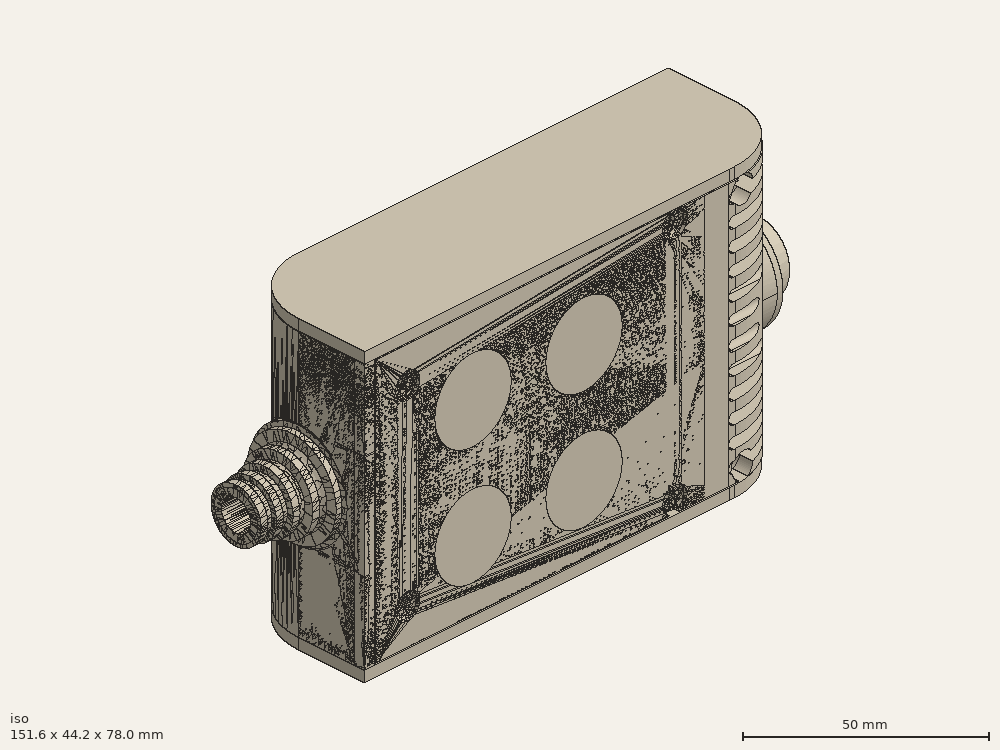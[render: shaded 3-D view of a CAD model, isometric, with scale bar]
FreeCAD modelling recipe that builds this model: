
FCSTD DOCUMENT  (FreeCAD 0.19R0.19.2)
Label: enclosure_180FCStd
License: All rights reserved
LicenseURL: http://en.wikipedia.org/wiki/All_rights_reserved
objects: Part::Revolution×152, Part::MultiFuse×146, Part::Feature×146, Sketcher::SketchObject×84, Part::Cut×70, Part::Cylinder×70, Part::Extrusion×67, Part::Fillet×58, Part::Box×36, App::MeasureDistance×4, PartDesign::Body×2, Image::ImagePlane×1
note: 831 computed .brp shape members not serialized (recipe doc carries the construction recipe); baked Part::Feature solids carry a one-line shape summary decoded from their .brp

FEATURE [Sketcher::SketchObject] Sketch  label="topSketch"
  FullyConstrained = true
  sketch-geometry (20):
    g0: LineSegment StartX=5.21097e-06 StartY=3 StartZ=0 EndX=5.21097e-06 EndY=19 EndZ=0
    g1: ArcOfCircle CenterX=19 CenterY=19 CenterZ=0 NormalX=0 NormalY=0 NormalZ=1 AngleXU=0 Radius=19 StartAngle=1.5708 EndAngle=3.14159
    g2: ArcOfCircle CenterX=19 CenterY=19 CenterZ=0 NormalX=0 NormalY=0 NormalZ=1 AngleXU=0 Radius=16 StartAngle=1.5708 EndAngle=3.14159
    g3: LineSegment StartX=114 StartY=35 StartZ=0 EndX=19 EndY=35 EndZ=0
    g4: LineSegment StartX=5.21097e-06 StartY=3 StartZ=0 EndX=5.21097e-06 EndY=0 EndZ=0
    g5: LineSegment StartX=3 StartY=0 StartZ=0 EndX=5.21097e-06 EndY=0 EndZ=0
    g6: LineSegment StartX=3 StartY=19 StartZ=0 EndX=3 EndY=0 EndZ=0
    g7: LineSegment StartX=19 StartY=38 StartZ=0 EndX=124 EndY=38 EndZ=0
    g8: Circle CenterX=119 CenterY=35 CenterZ=0 NormalX=0 NormalY=0 NormalZ=1 AngleXU=0 Radius=1
    g9: Circle CenterX=121 CenterY=35 CenterZ=0 NormalX=0 NormalY=0 NormalZ=1 AngleXU=0 Radius=1
    g10: Circle CenterX=121 CenterY=33 CenterZ=0 NormalX=0 NormalY=0 NormalZ=1 AngleXU=0 Radius=1
    g11: BSplineCurve PolesCount=3 KnotsCount=2 Degree=2 IsPeriodic=0
    g12: GeomPoint X=119 Y=35 Z=0
    g13: GeomPoint X=121 Y=33 Z=0
    g14: LineSegment StartX=119 StartY=35 StartZ=0 EndX=114 EndY=35 EndZ=0
    g15: ArcOfCircle CenterX=105 CenterY=19 CenterZ=0 NormalX=0 NormalY=0 NormalZ=1 AngleXU=0 Radius=19 StartAngle=5.7297 EndAngle=6.28319
    g16: ArcOfCircle CenterX=105 CenterY=19 CenterZ=0 NormalX=0 NormalY=0 NormalZ=1 AngleXU=0 Radius=16 StartAngle=5.60905 EndAngle=6.28319
    g17: LineSegment StartX=121 StartY=33 StartZ=0 EndX=121 EndY=19 EndZ=0
    g18: LineSegment StartX=124 StartY=38 StartZ=0 EndX=124 EndY=19 EndZ=0
    g19: LineSegment StartX=117.5 StartY=9.01251 StartZ=0 EndX=121.163 EndY=9.0125 EndZ=0
  constraints (46):
    c: Vertical(g0)
    c: Block(g0)
    c: Coincident(g1,g0)
    c: Block(g1)
    c: Coincident(g2,g1)
    c: Block(g2)
    c: Coincident(g3,g2)
    c: Horizontal(g3)
    c: Tangent(g3,g2)
    c: Coincident(g4,g0)
    c: Distance(g4) = 3
    c: Vertical(g4)
    c: Coincident(g5,g4)
    c: Horizontal(g5)
    c: Coincident(g6,g2)
    c: Coincident(g6,g5)
    c: Vertical(g6)
    c: Horizontal(g7)
    c: Distance(g7) = 105
    c: Coincident(g7,g1)
    c: Block(g3)
    c: Weight(g8) = 1
    c: Equal(g8,g9)
    c: Equal(g8,g10)
    c: InternalAlignment(g8,g11)
    c: InternalAlignment(g9,g11)
    c: InternalAlignment(g10,g11)
    c: InternalAlignment(g12,g11)
    c: InternalAlignment(g13,g11)
    c: Block(g11)
    c: Coincident(g14,g11)
    c: Coincident(g14,g3)
    c: Horizontal(g14)
    c: Block(g15)
    c: Coincident(g16,g15)
    c: Block(g16)
    c: Coincident(g17,g11)
    c: Coincident(g17,g16)
    c: Vertical(g17)
    c: Distance(g17) = 14
    c: Coincident(g18,g7)
    c: Coincident(g18,g15)
    c: Vertical(g18)
    c: Distance(g18) = 19
    c: Coincident(g19,g16)
    c: Coincident(g19,g15)
FEATURE [Sketcher::SketchObject] Sketch001  label="bottomSketch"
  FullyConstrained = true
  sketch-geometry (32):
    g0: LineSegment StartX=3.3 StartY=-6.03275e-07 StartZ=0 EndX=98 EndY=-6.03275e-07 EndZ=0
    g1: ArcOfCircle CenterX=98 CenterY=19 CenterZ=0 NormalX=0 NormalY=0 NormalZ=1 AngleXU=0 Radius=19 StartAngle=4.71239 EndAngle=5.71103
    g2: LineSegment StartX=6.3 StartY=8 StartZ=0 EndX=3.3 EndY=8 EndZ=0
    g3: LineSegment StartX=3.3 StartY=8 StartZ=0 EndX=3.3 EndY=-6.03275e-07 EndZ=0
    g4: ArcOfCircle CenterX=8.3 CenterY=5 CenterZ=0 NormalX=0 NormalY=0 NormalZ=1 AngleXU=0 Radius=2 StartAngle=3.14159 EndAngle=4.71239
    g5: LineSegment StartX=6.3 StartY=8 StartZ=0 EndX=6.3 EndY=5 EndZ=0
    g6: ArcOfCircle CenterX=98 CenterY=19 CenterZ=0 NormalX=0 NormalY=0 NormalZ=1 AngleXU=0 Radius=12.7 StartAngle=4.71239 EndAngle=6.28319
    g7: LineSegment StartX=94.7 StartY=3 StartZ=0 EndX=8.3 EndY=3 EndZ=0
    g8-g12: Circle x5 (B-spline internal-alignment scaffolding for g13; pole/knot coordinates omitted)
    g13: BSplineCurve PolesCount=5 KnotsCount=3 Degree=3 IsPeriodic=0
    g14: GeomPoint X=98 Y=6.3 Z=0
    g15: GeomPoint X=96.3938 Y=4.71946 Z=0
    g16: GeomPoint X=94.7 Y=3 Z=0
    g17-g23: Circle x7 (B-spline internal-alignment scaffolding for g24; pole/knot coordinates omitted)
    g24: BSplineCurve PolesCount=7 KnotsCount=5 Degree=3 IsPeriodic=0
    g25-g29: GeomPoint x5 (B-spline internal-alignment scaffolding for g24; pole/knot coordinates omitted)
    g30: ArcOfCircle CenterX=98 CenterY=19 CenterZ=0 NormalX=0 NormalY=0 NormalZ=1 AngleXU=0 Radius=15.7 StartAngle=5.81226 EndAngle=6.28319
    g31: LineSegment StartX=110.7 StartY=19 StartZ=0 EndX=113.7 EndY=19 EndZ=0
  constraints (41):
    c: Horizontal(g0)
    c: Coincident(g1,g0)
    c: Block(g1)
    c: Horizontal(g2)
    c: Distance(g2) = 3
    c: Coincident(g3,g2)
    c: Vertical(g3)
    c: Coincident(g3,g0)
    c: Block(g4)
    c: Block(g2)
    c: Coincident(g5,g2)
    c: Coincident(g5,g4)
    c: Vertical(g5)
    c: Coincident(g6,g1)
    c: Block(g6)
    c: Coincident(g7,g4)
    c: Horizontal(g7)
    c: Block(g0)
    c: Block(g7)
    c: Block(g3)
    c: Coincident(g13,g6)
    c: Weight(g8) = 1
    c: Equal(g8, g9-g12) x4
    c: Coincident(g13,g7)
    c: InternalAlignment(g8-g12 -> g13) x5
    c: InternalAlignment(g14,g13)
    c: InternalAlignment(g15,g13)
    c: InternalAlignment(g16,g13)
    c: Block(g13)
    c: Weight(g17) = 1
    c: Equal(g17, g18-g23) x6
    c: Coincident(g24,g1)
    c: InternalAlignment(g17-g23 -> g24) x7
    c: InternalAlignment(g25-g29 -> g24) x5
    c: Block(g24)
    c: Coincident(g30,g24)
    c: Coincident(g31,g6)
    c: Coincident(g31,g30)
    c: Horizontal(g31)
    c: Block(g31)
    c: Block(g30)
FEATURE [Part::Extrusion] Extrude  label="top"
  Base = -> Sketch
  Dir = (0,0,1)
  DirMode = 2
  FaceMakerClass = Part::FaceMakerBullseye
  LengthFwd = 72
  LengthRev = 0
  Solid = true
  Symmetric = false
FEATURE [Part::Extrusion] Extrude001  label="bottom"
  Base = -> Sketch001
  Dir = (0,0,1)
  DirMode = 2
  FaceMakerClass = Part::FaceMakerBullseye
  LengthFwd = 71.4
  LengthRev = 0
  Placement = pos=(0,0,0.3) rot=(0,0,1;0rad)
  Solid = true
  Symmetric = false
FEATURE [Sketcher::SketchObject] Sketch002  label="topSketch001"
  FullyConstrained = true
  sketch-geometry (8):
    g0: ArcOfCircle CenterX=19 CenterY=19.0975 CenterZ=0 NormalX=0 NormalY=0 NormalZ=1 AngleXU=0 Radius=18.9025 StartAngle=1.5708 EndAngle=3.14674
    g1: LineSegment StartX=0.0977805 StartY=19.0003 StartZ=0 EndX=0.0977805 EndY=0.000251602 EndZ=0
    g2: LineSegment StartX=19 StartY=38 StartZ=0 EndX=124 EndY=38 EndZ=0
    g3: LineSegment StartX=0.0977805 StartY=0.000251602 StartZ=0 EndX=105.098 EndY=0.000251602 EndZ=0
    g4: LineSegment StartX=124 StartY=38 StartZ=0 EndX=125.616 EndY=38 EndZ=0
    g5: LineSegment StartX=105.098 StartY=0.000251602 StartZ=0 EndX=106.713 EndY=0.000251602 EndZ=0
    g6: ArcOfCircle CenterX=106.616 CenterY=19 CenterZ=0 NormalX=0 NormalY=0 NormalZ=1 AngleXU=0 Radius=19 StartAngle=4.71754 EndAngle=6.28319
    g7: LineSegment StartX=125.616 StartY=38 StartZ=0 EndX=125.616 EndY=19 EndZ=0
  constraints (21):
    c: Block(g0)
    c: Coincident(g1,g0)
    c: Vertical(g1)
    c: Horizontal(g2)
    c: Distance(g2) = 105
    c: Coincident(g2,g0)
    c: Distance(g1) = 19
    c: Coincident(g3,g1)
    c: Horizontal(g3)
    c: Distance(g3) = 105
    c: Coincident(g4,g2)
    c: Horizontal(g4)
    c: Distance(g4) = 1.61553
    c: Horizontal(g5)
    c: Equal(g4,g5) = 1.61553
    c: Coincident(g5,g3)
    c: Block(g6)
    c: Coincident(g6,g5)
    c: Coincident(g7,g4)
    c: Coincident(g7,g6)
    c: Vertical(g7)
FEATURE [Part::Extrusion] Extrude002  label="sideA"
  Base = -> Sketch002
  Dir = (0,0,1)
  DirMode = 2
  FaceMakerClass = Part::FaceMakerBullseye
  LengthFwd = 3
  LengthRev = 0
  Placement = pos=(0,0,-3) rot=(0,0,1;0rad)
  Solid = true
  Symmetric = false
FEATURE [Sketcher::SketchObject] Sketch003  label="topSketch002"
  FullyConstrained = true
  sketch-geometry (6):
    g0: LineSegment StartX=19 StartY=38 StartZ=0 EndX=117 EndY=38 EndZ=0
    g1: ArcOfCircle CenterX=19 CenterY=19 CenterZ=0 NormalX=0 NormalY=0 NormalZ=1 AngleXU=0 Radius=19 StartAngle=1.5708 EndAngle=3.14159
    g2: LineSegment StartX=117 StartY=38 StartZ=0 EndX=117 EndY=19 EndZ=0
    g3: LineSegment StartX=98 StartY=1.0161e-12 StartZ=0 EndX=5.22862e-06 EndY=1.0161e-12 EndZ=0
    g4: LineSegment StartX=5.22862e-06 StartY=19 StartZ=0 EndX=5.22862e-06 EndY=1.0161e-12 EndZ=0
    g5: ArcOfCircle CenterX=98 CenterY=19 CenterZ=0 NormalX=0 NormalY=0 NormalZ=1 AngleXU=0 Radius=19 StartAngle=4.71239 EndAngle=6.28319
  constraints (16):
    c: Horizontal(g0)
    c: Distance(g0) = 98
    c: Coincident(g1,g0)
    c: Block(g1)
    c: Coincident(g2,g0)
    c: Vertical(g2)
    c: Distance(g2) = 19
    c: Horizontal(g3)
    c: Coincident(g4,g1)
    c: Vertical(g4)
    c: Coincident(g3,g4)
    c: Block(g3)
    c: Coincident(g5,g2)
    c: Coincident(g5,g3)
    c: Block(g0)
    c: Block(g5)
FEATURE [Sketcher::SketchObject] Sketch004
  FullyConstrained = true
  MapMode = 3
  Placement = pos=(0,0,0) rot=(1,0,0;1.5708rad)
  Support = -> [Extrude]
  sketch-geometry (8):
    g0: Circle CenterX=80.351 CenterY=-67.6202 CenterZ=0 NormalX=0 NormalY=0 NormalZ=1 AngleXU=0 Radius=2
    g1: Circle CenterX=80.351 CenterY=-67.6202 CenterZ=0 NormalX=0 NormalY=0 NormalZ=1 AngleXU=0 Radius=3
    g2: Circle CenterX=80.351 CenterY=-4.92017 CenterZ=0 NormalX=0 NormalY=0 NormalZ=1 AngleXU=0 Radius=2
    g3: Circle CenterX=80.351 CenterY=-4.92017 CenterZ=0 NormalX=0 NormalY=0 NormalZ=1 AngleXU=0 Radius=3
    g4: Circle CenterX=23.851 CenterY=-4.92017 CenterZ=0 NormalX=0 NormalY=0 NormalZ=1 AngleXU=0 Radius=2
    g5: Circle CenterX=23.851 CenterY=-4.92017 CenterZ=0 NormalX=0 NormalY=0 NormalZ=1 AngleXU=0 Radius=3
    g6: Circle CenterX=23.851 CenterY=-67.6202 CenterZ=0 NormalX=0 NormalY=0 NormalZ=1 AngleXU=0 Radius=2
    g7: Circle CenterX=23.851 CenterY=-67.6202 CenterZ=0 NormalX=0 NormalY=0 NormalZ=1 AngleXU=0 Radius=3
  constraints (8):
    c: Block(g3)
    c: Block(g2)
    c: Block(g1)
    c: Block(g0)
    c: Block(g6)
    c: Block(g7)
    c: Block(g4)
    c: Block(g5)
FEATURE [Part::Extrusion] Extrude004
  Base = -> Sketch004
  Dir = (0,-1,2e-16)
  DirMode = 2
  FaceMakerClass = Part::FaceMakerBullseye
  LengthFwd = 6
  LengthRev = 0
  Placement = pos=(0,9,0) rot=(0,0,1;0rad)
  Solid = true
  Symmetric = false
FEATURE [Sketcher::SketchObject] Sketch005
  FullyConstrained = true
  MapMode = 3
  Placement = pos=(0,0,0) rot=(1,0,0;1.5708rad)
  Support = -> [Extrude]
  sketch-geometry (8):
    g0: Circle CenterX=80.351 CenterY=-67.6202 CenterZ=0 NormalX=0 NormalY=0 NormalZ=1 AngleXU=0 Radius=3
    g1: Circle CenterX=80.351 CenterY=-4.92017 CenterZ=0 NormalX=0 NormalY=0 NormalZ=1 AngleXU=0 Radius=3
    g2: Circle CenterX=23.851 CenterY=-4.92017 CenterZ=0 NormalX=0 NormalY=0 NormalZ=1 AngleXU=0 Radius=3
    g3: Circle CenterX=23.851 CenterY=-67.6202 CenterZ=0 NormalX=0 NormalY=0 NormalZ=1 AngleXU=0 Radius=3
    g4: Circle CenterX=23.851 CenterY=-67.6202 CenterZ=0 NormalX=0 NormalY=0 NormalZ=1 AngleXU=0 Radius=5
    g5: Circle CenterX=80.351 CenterY=-67.6202 CenterZ=0 NormalX=0 NormalY=0 NormalZ=1 AngleXU=0 Radius=5
    g6: Circle CenterX=23.851 CenterY=-4.92017 CenterZ=0 NormalX=0 NormalY=0 NormalZ=1 AngleXU=0 Radius=5
    g7: Circle CenterX=80.351 CenterY=-4.92017 CenterZ=0 NormalX=0 NormalY=0 NormalZ=1 AngleXU=0 Radius=5
  constraints (8):
    c: Block(g1)
    c: Block(g0)
    c: Block(g3)
    c: Block(g2)
    c: Block(g5)
    c: Block(g4)
    c: Block(g6)
    c: Block(g7)
FEATURE [Part::Extrusion] Extrude005
  Base = -> Sketch005
  Dir = (0,-1,2e-16)
  DirMode = 2
  FaceMakerClass = Part::FaceMakerBullseye
  LengthFwd = 2
  LengthRev = 0
  Solid = true
  Symmetric = false
FEATURE [Sketcher::SketchObject] Sketch006
  FullyConstrained = true
  MapMode = 3
  Placement = pos=(0,0,0) rot=(1,0,0;1.5708rad)
  sketch-geometry (8):
    g0: Circle CenterX=80.351 CenterY=-67.6202 CenterZ=0 NormalX=0 NormalY=0 NormalZ=1 AngleXU=0 Radius=3
    g1: Circle CenterX=80.351 CenterY=-4.92017 CenterZ=0 NormalX=0 NormalY=0 NormalZ=1 AngleXU=0 Radius=3
    g2: Circle CenterX=23.851 CenterY=-4.92017 CenterZ=0 NormalX=0 NormalY=0 NormalZ=1 AngleXU=0 Radius=3
    g3: Circle CenterX=23.851 CenterY=-67.6202 CenterZ=0 NormalX=0 NormalY=0 NormalZ=1 AngleXU=0 Radius=3
    g4: Circle CenterX=23.851 CenterY=-67.6202 CenterZ=0 NormalX=0 NormalY=0 NormalZ=1 AngleXU=0 Radius=5
    g5: Circle CenterX=80.351 CenterY=-67.6202 CenterZ=0 NormalX=0 NormalY=0 NormalZ=1 AngleXU=0 Radius=5
    g6: Circle CenterX=23.851 CenterY=-4.92017 CenterZ=0 NormalX=0 NormalY=0 NormalZ=1 AngleXU=0 Radius=5
    g7: Circle CenterX=80.351 CenterY=-4.92017 CenterZ=0 NormalX=0 NormalY=0 NormalZ=1 AngleXU=0 Radius=5
  constraints (8):
    c: Block(g1)
    c: Block(g0)
    c: Block(g3)
    c: Block(g2)
    c: Block(g5)
    c: Block(g4)
    c: Block(g6)
    c: Block(g7)
FEATURE [Part::Extrusion] Extrude007
  Base = -> Sketch006
  Dir = (0,-1,2e-16)
  DirMode = 2
  FaceMakerClass = Part::FaceMakerBullseye
  LengthFwd = 2
  LengthRev = 0
  Solid = true
  Symmetric = false
FEATURE [Part::Fillet] Fillet
  Base = -> Extrude007
  Edges = 4 edges r=1.99: [Edge6,Edge12,Edge18,Edge24]
FEATURE [Part::Cut] Cut
  Base = -> Extrude005
  Placement = pos=(0,5,0) rot=(0,0,1;0rad)
  Tool = -> Fillet
FEATURE [Part::MultiFuse] Fusion  label="pCBScrews"
  Placement = pos=(-2.5,0,72.3) rot=(0,0,1;0rad)
  Shapes = -> [Extrude004,Cut]
FEATURE [App::MeasureDistance] Distance  label="Distance: 0.69 mm"
  Distance = 0.685967
  P1 = (24.0138,2.9647,0.3)
  P2 = (23.8901,3,-0.373787)
FEATURE [App::MeasureDistance] Distance001  label="Distance: 0.53 mm"
  Distance = 0.533607
  P1 = (80.2939,3,72.2334)
  P2 = (80.281,2.99661,71.7)
FEATURE [Part::Fillet] Fillet001
  Base = -> Extrude001
  Edges = 1 edges r=2.4: [Edge17]
FEATURE [Part::Fillet] Fillet002  label="bottom001"
  Base = -> Fillet001
  Edges = 1 edges r=2.4: [Edge36]
FEATURE [Part::Fillet] Fillet003  label="top001"
  Base = -> Extrude
  Edges = 1 edges r=2: [Edge1]
FEATURE [Sketcher::SketchObject] Sketch007
  FullyConstrained = true
  sketch-geometry (16):
    g0: LineSegment StartX=4 StartY=0 StartZ=0 EndX=4 EndY=2.4 EndZ=0
    g1: LineSegment StartX=4 StartY=2.4 StartZ=0 EndX=7 EndY=2.4 EndZ=0
    g2: LineSegment StartX=4 StartY=0 StartZ=0 EndX=5.7 EndY=0 EndZ=0
    g3: LineSegment StartX=5.7 StartY=0 StartZ=0 EndX=5.7 EndY=-5.6 EndZ=0
    g4-g8: Circle x5 (B-spline internal-alignment scaffolding for g9; pole/knot coordinates omitted)
    g9: BSplineCurve PolesCount=5 KnotsCount=3 Degree=3 IsPeriodic=0
    g10: GeomPoint X=7 Y=2.4 Z=0
    g11: GeomPoint X=10.4582 Y=-1.55472 Z=0
    g12: GeomPoint X=14 Y=-5.6 Z=0
    g13: LineSegment StartX=14 StartY=-5.6 StartZ=0 EndX=14 EndY=-14.1 EndZ=0
    g14: LineSegment StartX=14 StartY=-14.1 StartZ=0 EndX=6.5 EndY=-14.1 EndZ=0
    g15: LineSegment StartX=5.7 StartY=-5.6 StartZ=0 EndX=6.5 EndY=-14.1 EndZ=0
  constraints (28):
    c: Distance(g0) = 2.4
    c: Vertical(g0)
    c: Block(g0)
    c: Coincident(g1,g0)
    c: Horizontal(g1)
    c: Distance(g1) = 3
    c: Coincident(g2,g0)
    c: Horizontal(g2)
    c: Distance(g2) = 1.7
    c: Coincident(g3,g2)
    c: Vertical(g3)
    c: Distance(g3) = 5.6
    c: Coincident(g9,g1)
    c: Weight(g4) = 1
    c: Equal(g4, g5-g8) x4
    c: InternalAlignment(g4-g8 -> g9) x5
    c: InternalAlignment(g10,g9)
    c: InternalAlignment(g11,g9)
    c: InternalAlignment(g12,g9)
    c: Block(g9)
    c: Coincident(g13,g9)
    c: Vertical(g13)
    c: Distance(g13) = 8.5
    c: Coincident(g14,g13)
    c: Horizontal(g14)
    c: Distance(g14) = 7.5
    c: Coincident(g15,g3)
    c: Coincident(g15,g14)
FEATURE [Part::Feature] Face
  shape: bbox 10 x 16.5 x 2e-07 mm, 1 faces, 0 solids (baked)
FEATURE [Part::Revolution] Revolve  label="plugHousing"
  Angle = 360
  Axis = (0,1,0)
  Base = (0,0,0)
  FaceMakerClass = Part::FaceMakerBullseye
  Placement = pos=(0,0,36.15) rot=(0,0,1;0rad)
  Solid = false
  Source = -> Face
  Symmetric = false
FEATURE [Part::Feature] Face001
  shape: bbox 10 x 16.5 x 2e-07 mm, 1 faces, 0 solids (baked)
FEATURE [Part::Revolution] Revolve001  label="plugHousing001"
  Angle = 360
  Axis = (0,1,0)
  Base = (0,0,0)
  FaceMakerClass = Part::FaceMakerBullseye
  Placement = pos=(0,0,36.15) rot=(0,0,1;0rad)
  Solid = false
  Source = -> Face001
  Symmetric = false
FEATURE [Part::MultiFuse] Fusion001  label="plugHousing002"
  Placement = pos=(0,0,0) rot=(0,0,1;1.5708rad)
  Shapes = -> [Revolve001,Revolve]
FEATURE [Part::Feature] Face002
  shape: bbox 10 x 16.5 x 2e-07 mm, 1 faces, 0 solids (baked)
FEATURE [Part::Revolution] Revolve003  label="plugHousing005"
  Angle = 360
  Axis = (0,1,0)
  Base = (0,0,0)
  FaceMakerClass = Part::FaceMakerBullseye
  Placement = pos=(0,0,36.15) rot=(0,0,1;0rad)
  Solid = false
  Source = -> Face002
  Symmetric = false
FEATURE [Part::Feature] Face003
  shape: bbox 10 x 16.5 x 2e-07 mm, 1 faces, 0 solids (baked)
FEATURE [Part::Revolution] Revolve002  label="plugHousing003"
  Angle = 360
  Axis = (0,1,0)
  Base = (0,0,0)
  FaceMakerClass = Part::FaceMakerBullseye
  Placement = pos=(0,0,36.15) rot=(0,0,1;0rad)
  Solid = false
  Source = -> Face003
  Symmetric = false
FEATURE [Part::MultiFuse] Fusion002  label="plugHousing004"
  Placement = pos=(0,0,0) rot=(0,0,1;1.5708rad)
  Shapes = -> [Revolve002,Revolve003]
FEATURE [Part::MultiFuse] Fusion003  label="plugHousing006"
  Placement = pos=(0,19,0) rot=(0,0,1;3.14159rad)
  Shapes = -> [Fusion002,Fusion001]
FEATURE [Part::Feature] Face004
  shape: bbox 10 x 16.5 x 2e-07 mm, 1 faces, 0 solids (baked)
FEATURE [Part::Revolution] Revolve006  label="plugHousing010"
  Angle = 360
  Axis = (0,1,0)
  Base = (0,0,0)
  FaceMakerClass = Part::FaceMakerBullseye
  Placement = pos=(0,0,36.15) rot=(0,0,1;0rad)
  Solid = false
  Source = -> Face004
  Symmetric = false
FEATURE [Part::Feature] Face005
  shape: bbox 10 x 16.5 x 2e-07 mm, 1 faces, 0 solids (baked)
FEATURE [Part::Revolution] Revolve007  label="plugHousing011"
  Angle = 360
  Axis = (0,1,0)
  Base = (0,0,0)
  FaceMakerClass = Part::FaceMakerBullseye
  Placement = pos=(0,0,36.15) rot=(0,0,1;0rad)
  Solid = false
  Source = -> Face005
  Symmetric = false
FEATURE [Part::Feature] Face006
  shape: bbox 10 x 16.5 x 2e-07 mm, 1 faces, 0 solids (baked)
FEATURE [Part::Revolution] Revolve004  label="plugHousing007"
  Angle = 360
  Axis = (0,1,0)
  Base = (0,0,0)
  FaceMakerClass = Part::FaceMakerBullseye
  Placement = pos=(0,0,36.15) rot=(0,0,1;0rad)
  Solid = false
  Source = -> Face006
  Symmetric = false
FEATURE [Part::MultiFuse] Fusion004  label="plugHousing009"
  Placement = pos=(0,0,0) rot=(0,0,1;1.5708rad)
  Shapes = -> [Revolve004,Revolve007]
FEATURE [Part::Feature] Face007
  shape: bbox 10 x 16.5 x 2e-07 mm, 1 faces, 0 solids (baked)
FEATURE [Part::Revolution] Revolve005  label="plugHousing008"
  Angle = 360
  Axis = (0,1,0)
  Base = (0,0,0)
  FaceMakerClass = Part::FaceMakerBullseye
  Placement = pos=(0,0,36.15) rot=(0,0,1;0rad)
  Solid = false
  Source = -> Face007
  Symmetric = false
FEATURE [Part::MultiFuse] Fusion005  label="plugHousing012"
  Placement = pos=(0,0,0) rot=(0,0,1;1.5708rad)
  Shapes = -> [Revolve006,Revolve005]
FEATURE [Part::MultiFuse] Fusion006  label="plugHousing013"
  Placement = pos=(0,19,0) rot=(0,0,1;3.14159rad)
  Shapes = -> [Fusion005,Fusion004]
FEATURE [Part::MultiFuse] Fusion007  label="plugHousing014"
  Placement = pos=(122.621,0,-0.15) rot=(0,0,1;0rad)
  Shapes = -> [Fusion003,Fusion006]
FEATURE [Part::Cylinder] Cylinder002
  Angle = 360
  AttacherType = Attacher::AttachEngine3D
  Height = 20
  Placement = pos=(0,0,36.15) rot=(0,0,1;0rad)
  Radius = 4
FEATURE [Part::Cylinder] Cylinder003
  Angle = 360
  AttacherType = Attacher::AttachEngine3D
  Height = 10
  Placement = pos=(0,0,36.15) rot=(0,0,1;0rad)
  Radius = 4
FEATURE [Part::MultiFuse] Fusion009  label="removeToCreateHoleForPlugHousing"
  Placement = pos=(70,19,36.15) rot=(0,1,0;1.5708rad)
  Shapes = -> [Cylinder002,Cylinder003]
FEATURE [Part::Cylinder] Cylinder004
  Angle = 360
  AttacherType = Attacher::AttachEngine3D
  Height = 20
  Placement = pos=(0,0,36.15) rot=(0,0,1;0rad)
  Radius = 4
FEATURE [Part::Cylinder] Cylinder005
  Angle = 360
  AttacherType = Attacher::AttachEngine3D
  Height = 10
  Placement = pos=(0,0,36.15) rot=(0,0,1;0rad)
  Radius = 4
FEATURE [Part::MultiFuse] Fusion010  label="removeToCreateHoleForPlugHousing001"
  Placement = pos=(70,19,36.15) rot=(0,1,0;1.5708rad)
  Shapes = -> [Cylinder004,Cylinder005]
FEATURE [Part::Cut] Cut001
  Base = -> Fillet003
  Tool = -> Fusion010
FEATURE [Part::Cut] Cut002  label="Bottom"
  Base = -> Fillet002
  Tool = -> Fusion009
FEATURE [Part::Feature] Face008
  shape: bbox 10 x 16.5 x 2e-07 mm, 1 faces, 0 solids (baked)
FEATURE [Part::Revolution] Revolve011  label="plugHousing021"
  Angle = 360
  Axis = (0,1,0)
  Base = (0,0,0)
  FaceMakerClass = Part::FaceMakerBullseye
  Placement = pos=(0,0,36.15) rot=(0,0,1;0rad)
  Solid = false
  Source = -> Face008
  Symmetric = false
FEATURE [Part::Feature] Face009
  shape: bbox 10 x 16.5 x 2e-07 mm, 1 faces, 0 solids (baked)
FEATURE [Part::Revolution] Revolve012  label="plugHousing022"
  Angle = 360
  Axis = (0,1,0)
  Base = (0,0,0)
  FaceMakerClass = Part::FaceMakerBullseye
  Placement = pos=(0,0,36.15) rot=(0,0,1;0rad)
  Solid = false
  Source = -> Face009
  Symmetric = false
FEATURE [Part::Feature] Face010 .. Face013  x4 (patterned run collapsed; names and placements below)
  shape: bbox 10 x 16.5 x 2e-07 mm, 1 faces, 0 solids (baked)
FEATURE [Part::Revolution] Revolve015  label="plugHousing027"
  Angle = 360
  Axis = (0,1,0)
  Base = (0,0,0)
  FaceMakerClass = Part::FaceMakerBullseye
  Placement = pos=(0,0,36.15) rot=(0,0,1;0rad)
  Solid = false
  Source = -> Face013
  Symmetric = false
FEATURE [Part::Feature] Face014
  shape: bbox 10 x 16.5 x 2e-07 mm, 1 faces, 0 solids (baked)
FEATURE [Part::Feature] Face015
  shape: bbox 10 x 16.5 x 2e-07 mm, 1 faces, 0 solids (baked)
FEATURE [Part::Feature] Face016
  shape: bbox 10 x 16.5 x 2e-07 mm, 1 faces, 0 solids (baked)
FEATURE [Part::Revolution] Revolve019  label="plugHousing033"
  Angle = 360
  Axis = (0,1,0)
  Base = (0,0,0)
  FaceMakerClass = Part::FaceMakerBullseye
  Placement = pos=(0,0,36.15) rot=(0,0,1;0rad)
  Solid = false
  Source = -> Face016
  Symmetric = false
FEATURE [Part::Feature] Face017
  shape: bbox 10 x 16.5 x 2e-07 mm, 1 faces, 0 solids (baked)
FEATURE [Part::Revolution] Revolve020  label="plugHousing034"
  Angle = 360
  Axis = (0,1,0)
  Base = (0,0,0)
  FaceMakerClass = Part::FaceMakerBullseye
  Placement = pos=(0,0,36.15) rot=(0,0,1;0rad)
  Solid = false
  Source = -> Face017
  Symmetric = false
FEATURE [Part::Feature] Face018
  shape: bbox 10 x 16.5 x 2e-07 mm, 1 faces, 0 solids (baked)
FEATURE [Part::Revolution] Revolve016  label="plugHousing030"
  Angle = 360
  Axis = (0,1,0)
  Base = (0,0,0)
  FaceMakerClass = Part::FaceMakerBullseye
  Placement = pos=(0,0,36.15) rot=(0,0,1;0rad)
  Solid = false
  Source = -> Face018
  Symmetric = false
FEATURE [Part::MultiFuse] Fusion020  label="plugHousing038"
  Placement = pos=(0,0,0) rot=(0,0,1;1.5708rad)
  Shapes = -> [Revolve016,Revolve020]
FEATURE [Part::Feature] Face019
  shape: bbox 10 x 16.5 x 2e-07 mm, 1 faces, 0 solids (baked)
FEATURE [Part::Feature] Face020
  shape: bbox 10 x 16.5 x 2e-07 mm, 1 faces, 0 solids (baked)
FEATURE [Part::Revolution] Revolve017  label="plugHousing031"
  Angle = 360
  Axis = (0,1,0)
  Base = (0,0,0)
  FaceMakerClass = Part::FaceMakerBullseye
  Placement = pos=(0,0,36.15) rot=(0,0,1;0rad)
  Solid = false
  Source = -> Face020
  Symmetric = false
FEATURE [Part::MultiFuse] Fusion021  label="plugHousing039"
  Placement = pos=(0,0,0) rot=(0,0,1;1.5708rad)
  Shapes = -> [Revolve019,Revolve017]
FEATURE [Part::MultiFuse] Fusion023  label="plugHousing041"
  Placement = pos=(0,19,0) rot=(0,0,1;3.14159rad)
  Shapes = -> [Fusion021,Fusion020]
FEATURE [Part::Revolution] Revolve022  label="plugHousing043"
  Angle = 360
  Axis = (0,1,0)
  Base = (0,0,0)
  FaceMakerClass = Part::FaceMakerBullseye
  Placement = pos=(0,0,36.15) rot=(0,0,1;0rad)
  Solid = false
  Source = -> Face019
  Symmetric = false
FEATURE [Part::Feature] Face021
  shape: bbox 10 x 16.5 x 2e-07 mm, 1 faces, 0 solids (baked)
FEATURE [Part::Revolution] Revolve023  label="plugHousing044"
  Angle = 360
  Axis = (0,1,0)
  Base = (0,0,0)
  FaceMakerClass = Part::FaceMakerBullseye
  Placement = pos=(0,0,36.15) rot=(0,0,1;0rad)
  Solid = false
  Source = -> Face021
  Symmetric = false
FEATURE [Part::Feature] Face022
  shape: bbox 10 x 16.5 x 2e-07 mm, 1 faces, 0 solids (baked)
FEATURE [Part::Revolution] Revolve018  label="plugHousing032"
  Angle = 360
  Axis = (0,1,0)
  Base = (0,0,0)
  FaceMakerClass = Part::FaceMakerBullseye
  Placement = pos=(0,0,36.15) rot=(0,0,1;0rad)
  Solid = false
  Source = -> Face022
  Symmetric = false
FEATURE [Part::MultiFuse] Fusion022  label="plugHousing040"
  Placement = pos=(0,0,0) rot=(0,0,1;1.5708rad)
  Shapes = -> [Revolve018,Revolve023]
FEATURE [Part::Feature] Face023
  shape: bbox 10 x 16.5 x 2e-07 mm, 1 faces, 0 solids (baked)
FEATURE [Part::Revolution] Revolve021  label="plugHousing035"
  Angle = 360
  Axis = (0,1,0)
  Base = (0,0,0)
  FaceMakerClass = Part::FaceMakerBullseye
  Placement = pos=(0,0,36.15) rot=(0,0,1;0rad)
  Solid = false
  Source = -> Face023
  Symmetric = false
FEATURE [Part::MultiFuse] Fusion018  label="plugHousing036"
  Placement = pos=(0,0,0) rot=(0,0,1;1.5708rad)
  Shapes = -> [Revolve022,Revolve021]
FEATURE [Part::MultiFuse] Fusion019  label="plugHousing037"
  Placement = pos=(0,19,0) rot=(0,0,1;3.14159rad)
  Shapes = -> [Fusion018,Fusion022]
FEATURE [Part::MultiFuse] Fusion024  label="plugHousing042"
  Placement = pos=(122.621,0,-0.15) rot=(0,0,1;0rad)
  Shapes = -> [Fusion023,Fusion019]
FEATURE [Part::Cylinder] Cylinder006
  Angle = 360
  AttacherType = Attacher::AttachEngine3D
  Height = 20
  Placement = pos=(0,0,36.15) rot=(0,0,1;0rad)
  Radius = 14.3
FEATURE [Part::Cylinder] Cylinder007
  Angle = 360
  AttacherType = Attacher::AttachEngine3D
  Height = 10
  Placement = pos=(0,0,36.15) rot=(0,0,1;0rad)
  Radius = 4
FEATURE [Part::MultiFuse] Fusion026  label="removeToCreteHoleForPlugHousing"
  Placement = pos=(70,19,36) rot=(0,1,0;1.5708rad)
  Shapes = -> [Cylinder006,Cylinder007]
FEATURE [Part::Box] Box001  label="Cube001"
  AttacherType = Attacher::AttachEngine3D
  Height = 28
  Length = 3
  Placement = pos=(110.7,19,22) rot=(0,0,1;0rad)
  Width = 15.7
FEATURE [Part::Cut] Cut003  label="top002"
  Base = -> Cut001
  Tool = -> Fusion007
FEATURE [Part::Revolution] Revolve008  label="plugHousing015"
  Angle = 360
  Axis = (0,1,0)
  Base = (0,0,0)
  FaceMakerClass = Part::FaceMakerBullseye
  Placement = pos=(0,0,36.15) rot=(0,0,1;0rad)
  Solid = false
  Source = -> Face010
  Symmetric = false
FEATURE [Part::MultiFuse] Fusion013  label="plugHousing020"
  Placement = pos=(0,0,0) rot=(0,0,1;1.5708rad)
  Shapes = -> [Revolve008,Revolve012]
FEATURE [Part::Cut] Cut004  label="top003"
  Base = -> Cut003
  Placement = pos=(1,0,0) rot=(0,0,1;0rad)
  Tool = -> Fusion026
FEATURE [Part::Cylinder] Cylinder008
  Angle = 360
  AttacherType = Attacher::AttachEngine3D
  Height = 20
  Placement = pos=(0,0,36.15) rot=(0,0,1;0rad)
  Radius = 10.3
FEATURE [Part::Cylinder] Cylinder009
  Angle = 360
  AttacherType = Attacher::AttachEngine3D
  Height = 10
  Placement = pos=(0,0,36.15) rot=(0,0,1;0rad)
  Radius = 4
FEATURE [Part::MultiFuse] Fusion027  label="removeToCreteHoleForPlugHousing001"
  Placement = pos=(70,19,36) rot=(0,1,0;1.5708rad)
  Shapes = -> [Cylinder008,Cylinder009]
FEATURE [Part::Cut] Cut005  label="plugHousingTab"
  Base = -> Box001
  Tool = -> Fusion027
FEATURE [Part::MultiFuse] Fusion028  label="plugHousing045"
  Shapes = -> [Fusion024,Cut005]
FEATURE [Part::Box] Box002  label="Cube002"
  AttacherType = Attacher::AttachEngine3D
  Height = 28.8
  Length = 3
  Placement = pos=(107.3,28,21.6) rot=(0,0,1;0rad)
  Width = 7
FEATURE [Part::Box] Box003  label="Cube003"
  AttacherType = Attacher::AttachEngine3D
  Height = 3
  Length = 6.4
  Placement = pos=(107.3,28,18.6) rot=(0,0,1;0rad)
  Width = 7
FEATURE [Part::Box] Box004  label="Cube004"
  AttacherType = Attacher::AttachEngine3D
  Height = 3
  Length = 6.4
  Placement = pos=(107.3,28,50.4) rot=(0,0,1;0rad)
  Width = 7
FEATURE [Part::MultiFuse] Fusion029  label="plugHousingBracketHolder"
  Shapes = -> [Box004,Box002,Box003]
FEATURE [Part::Cylinder] Cylinder010
  Angle = 360
  AttacherType = Attacher::AttachEngine3D
  Height = 20
  Placement = pos=(0,0,36.15) rot=(0,0,1;0rad)
  Radius = 14.3
FEATURE [Part::Cylinder] Cylinder011
  Angle = 360
  AttacherType = Attacher::AttachEngine3D
  Height = 10
  Placement = pos=(0,0,36.15) rot=(0,0,1;0rad)
  Radius = 4
FEATURE [Part::MultiFuse] Fusion030  label="removeToCreteHoleForPlugHousing002"
  Placement = pos=(70,19,36) rot=(0,1,0;1.5708rad)
  Shapes = -> [Cylinder010,Cylinder011]
FEATURE [Part::Cut] Cut006  label="plugHousingBracketHolder001"
  Base = -> Fusion029
  Tool = -> Fusion030
FEATURE [Part::Cylinder] Cylinder012
  Angle = 360
  AttacherType = Attacher::AttachEngine3D
  Height = 20
  Placement = pos=(0,0,36.15) rot=(0,0,1;0rad)
  Radius = 7
FEATURE [Part::Cylinder] Cylinder013
  Angle = 360
  AttacherType = Attacher::AttachEngine3D
  Height = 10
  Placement = pos=(0,0,36.15) rot=(0,0,1;0rad)
  Radius = 4
FEATURE [Part::MultiFuse] Fusion032  label="removeToCreteHoleForPlugHousing003"
  Placement = pos=(70,19,36) rot=(0,1,0;1.5708rad)
  Shapes = -> [Cylinder012,Cylinder013]
FEATURE [Part::Cut] Cut007  label="bottom002"
  Base = -> Cut002
  Tool = -> Fusion032
FEATURE [Sketcher::SketchObject] Sketch008
  FullyConstrained = true
  sketch-geometry (54):
    g0: LineSegment StartX=-4.2 StartY=0 StartZ=0 EndX=-6.2 EndY=0 EndZ=0
    g1: LineSegment StartX=-14 StartY=-18 StartZ=0 EndX=-14 EndY=-26.5 EndZ=0
    g2: LineSegment StartX=-4.2 StartY=0 StartZ=0 EndX=-4.2 EndY=-13.4877 EndZ=0
    g3: Circle CenterX=-4.2 CenterY=-13.4877 CenterZ=0 NormalX=0 NormalY=0 NormalZ=1 AngleXU=0 Radius=1
    g4: Circle CenterX=-4.2 CenterY=-26.5 CenterZ=0 NormalX=0 NormalY=0 NormalZ=1 AngleXU=0 Radius=1
    g5: Circle CenterX=-8.2 CenterY=-26.5 CenterZ=0 NormalX=0 NormalY=0 NormalZ=1 AngleXU=0 Radius=1
    g6: BSplineCurve PolesCount=3 KnotsCount=2 Degree=2 IsPeriodic=0
    g7: GeomPoint X=-4.2 Y=-13.4877 Z=0
    g8: GeomPoint X=-8.2 Y=-26.5 Z=0
    g9: LineSegment StartX=-14 StartY=-26.5 StartZ=0 EndX=-8.2 EndY=-26.5 EndZ=0
    g10: LineSegment StartX=-10.15 StartY=-12 StartZ=0 EndX=-10.15 EndY=-14 EndZ=0
    g11: LineSegment StartX=-12.8401 StartY=-16 StartZ=0 EndX=-10.1571 EndY=-16 EndZ=0
    g12: LineSegment StartX=-10.15 StartY=-14 StartZ=0 EndX=-8.70761 EndY=-14 EndZ=0
    g13: LineSegment StartX=-12.8401 StartY=-16 StartZ=0 EndX=-12.8401 EndY=-17.6958 EndZ=0
    g14: LineSegment StartX=-10.15 StartY=-12 StartZ=0 EndX=-7.79258 EndY=-12 EndZ=0
    g15: Circle CenterX=-6.2215 CenterY=-2 CenterZ=0 NormalX=0 NormalY=0 NormalZ=1 AngleXU=0 Radius=1
    g16: Circle CenterX=-6.22762 CenterY=-2.58724 CenterZ=0 NormalX=0 NormalY=0 NormalZ=1 AngleXU=0 Radius=1
    g17: Circle CenterX=-6.32538 CenterY=-4 CenterZ=0 NormalX=0 NormalY=0 NormalZ=1 AngleXU=0 Radius=1
    g18: BSplineCurve PolesCount=3 KnotsCount=2 Degree=2 IsPeriodic=0
    g19: GeomPoint X=-6.2215 Y=-2 Z=0
    g20: GeomPoint X=-6.32538 Y=-4 Z=0
    g21: Circle CenterX=-6.48644 CenterY=-5.99526 CenterZ=0 NormalX=0 NormalY=0 NormalZ=1 AngleXU=0 Radius=1
    g22: Circle CenterX=-6.58486 CenterY=-6.99526 CenterZ=0 NormalX=0 NormalY=0 NormalZ=1 AngleXU=0 Radius=1
    g23: Circle CenterX=-6.77343 CenterY=-8 CenterZ=0 NormalX=0 NormalY=0 NormalZ=1 AngleXU=0 Radius=1
    g24: BSplineCurve PolesCount=3 KnotsCount=2 Degree=2 IsPeriodic=0
    g25: GeomPoint X=-6.48644 Y=-5.99526 Z=0
    g26: GeomPoint X=-6.77343 Y=-8 Z=0
    g27: Circle CenterX=-7.19003 CenterY=-10 CenterZ=0 NormalX=0 NormalY=0 NormalZ=1 AngleXU=0 Radius=1
    g28: Circle CenterX=-7.44407 CenterY=-11.0915 CenterZ=0 NormalX=0 NormalY=0 NormalZ=1 AngleXU=0 Radius=1
    g29: Circle CenterX=-7.79258 CenterY=-12 CenterZ=0 NormalX=0 NormalY=0 NormalZ=1 AngleXU=0 Radius=1
    g30: BSplineCurve PolesCount=3 KnotsCount=2 Degree=2 IsPeriodic=0
    g31: GeomPoint X=-7.19003 Y=-10 Z=0
    g32: GeomPoint X=-7.79258 Y=-12 Z=0
    g33: Circle CenterX=-8.70761 CenterY=-14 CenterZ=0 NormalX=0 NormalY=0 NormalZ=1 AngleXU=0 Radius=1
    g34: Circle CenterX=-9.33087 CenterY=-15.1837 CenterZ=0 NormalX=0 NormalY=0 NormalZ=1 AngleXU=0 Radius=1
    g35: Circle CenterX=-10.1571 CenterY=-16 CenterZ=0 NormalX=0 NormalY=0 NormalZ=1 AngleXU=0 Radius=1
    g36: BSplineCurve PolesCount=3 KnotsCount=2 Degree=2 IsPeriodic=0
    g37: GeomPoint X=-8.70761 Y=-14 Z=0
    g38: GeomPoint X=-10.1571 Y=-16 Z=0
    g39: Circle CenterX=-12.8401 CenterY=-17.6958 CenterZ=0 NormalX=0 NormalY=0 NormalZ=1 AngleXU=0 Radius=1
    g40: Circle CenterX=-13.3521 CenterY=-17.9027 CenterZ=0 NormalX=0 NormalY=0 NormalZ=1 AngleXU=0 Radius=1
    g41: Circle CenterX=-14 CenterY=-18 CenterZ=0 NormalX=0 NormalY=0 NormalZ=1 AngleXU=0 Radius=1
    g42: BSplineCurve PolesCount=3 KnotsCount=2 Degree=2 IsPeriodic=0
    g43: GeomPoint X=-12.8401 Y=-17.6958 Z=0
    g44: GeomPoint X=-14 Y=-18 Z=0
    g45: LineSegment StartX=-6.2 StartY=0 StartZ=0 EndX=-7.2 EndY=0 EndZ=0
    g46: LineSegment StartX=-7.2 StartY=0 StartZ=0 EndX=-7.2 EndY=-2 EndZ=0
    g47: LineSegment StartX=-7.2 StartY=-2 StartZ=0 EndX=-6.2215 EndY=-2 EndZ=0
    g48: LineSegment StartX=-6.32538 StartY=-4 StartZ=0 EndX=-7.65538 EndY=-4 EndZ=0
    g49: LineSegment StartX=-7.65538 StartY=-4 StartZ=0 EndX=-7.65538 EndY=-5.99526 EndZ=0
    g50: LineSegment StartX=-7.65538 StartY=-5.99526 StartZ=0 EndX=-6.48644 EndY=-5.99526 EndZ=0
    g51: LineSegment StartX=-6.77343 StartY=-8 StartZ=0 EndX=-8.43343 EndY=-8 EndZ=0
    g52: LineSegment StartX=-8.43343 StartY=-8 StartZ=0 EndX=-8.43343 EndY=-10 EndZ=0
    g53: LineSegment StartX=-8.43343 StartY=-10 StartZ=0 EndX=-7.19003 EndY=-10 EndZ=0
  constraints (112):
    c: Horizontal(g0)
    c: Distance(g0) = 2
    c: Block(g0)
    c: Vertical(g1)
    c: Coincident(g2,g0)
    c: Vertical(g2)
    c: Block(g2)
    c: Coincident(g6,g2)
    c: Weight(g3) = 1
    c: Equal(g3,g4)
    c: Equal(g3,g5)
    c: InternalAlignment(g3,g6)
    c: InternalAlignment(g4,g6)
    c: InternalAlignment(g5,g6)
    c: InternalAlignment(g7,g6)
    c: InternalAlignment(g8,g6)
    c: Block(g6)
    c: Coincident(g9,g1)
    c: Coincident(g9,g6)
    c: Horizontal(g9)
    c: Vertical(g10)
    c: Block(g10)
    c: Horizontal(g11)
    c: Block(g11)
    c: Coincident(g12,g10)
    c: Horizontal(g12)
    c: Block(g12)
    c: Coincident(g13,g11)
    c: Vertical(g13)
    c: Block(g13)
    c: Coincident(g14,g10)
    c: Horizontal(g14)
    c: Block(g14)
    c: Block(g9)
    c: Block(g1)
    c: Weight(g15) = 1
    c: Equal(g15,g16)
    c: Equal(g15,g17)
    c: InternalAlignment(g15,g18)
    c: InternalAlignment(g16,g18)
    c: InternalAlignment(g17,g18)
    c: InternalAlignment(g19,g18)
    c: InternalAlignment(g20,g18)
    c: Weight(g21) = 1
    c: Equal(g21,g22)
    c: Equal(g21,g23)
    c: InternalAlignment(g21,g24)
    c: InternalAlignment(g22,g24)
    c: InternalAlignment(g23,g24)
    c: InternalAlignment(g25,g24)
    c: InternalAlignment(g26,g24)
    c: Weight(g27) = 1
    c: Equal(g27,g28)
    c: Equal(g27,g29)
    c: Coincident(g30,g14)
    c: InternalAlignment(g27,g30)
    c: InternalAlignment(g28,g30)
    c: InternalAlignment(g29,g30)
    c: InternalAlignment(g31,g30)
    c: InternalAlignment(g32,g30)
    c: Coincident(g36,g12)
    c: Weight(g33) = 1
    c: Equal(g33,g34)
    c: Equal(g33,g35)
    c: Coincident(g36,g11)
    c: InternalAlignment(g33,g36)
    c: InternalAlignment(g34,g36)
    c: InternalAlignment(g35,g36)
    c: InternalAlignment(g37,g36)
    c: InternalAlignment(g38,g36)
    c: Coincident(g42,g13)
    c: Weight(g39) = 1
    c: Equal(g39,g40)
    c: Equal(g39,g41)
    c: Coincident(g42,g1)
    c: InternalAlignment(g39,g42)
    c: InternalAlignment(g40,g42)
    c: InternalAlignment(g41,g42)
    c: InternalAlignment(g43,g42)
    c: InternalAlignment(g44,g42)
    c: Block(g18)
    c: Block(g24)
    c: Block(g30)
    c: Block(g36)
    c: Block(g42)
    c: Horizontal(g45)
    c: Coincident(g45,g0)
    c: Vertical(g46)
    c: Coincident(g46,g45)
    c: Coincident(g47,g46)
    c: Coincident(g47,g18)
    c: Horizontal(g47)
    c: Block(g46)
    c: Coincident(g48,g18)
    c: Horizontal(g48)
    c: Distance(g48) = 1.33
    c: Vertical(g49)
    c: Coincident(g49,g48)
    c: Coincident(g50,g49)
    c: Coincident(g50,g24)
    c: Horizontal(g50)
    c: Tangent(g50,g22)
    c: Horizontal(g51)
    c: Coincident(g51,g24)
    c: Block(g51)
    c: Vertical(g52)
    c: Block(g52)
    c: Coincident(g52,g51)
    c: Coincident(g53,g52)
    c: Coincident(g53,g30)
    c: Horizontal(g53)
    c: Distance(g1) = 8.5
FEATURE [Part::Feature] Face024
  shape: bbox 9.8 x 26.5 x 2e-07 mm, 1 faces, 0 solids (baked)
FEATURE [Part::Revolution] Revolve024
  Angle = 360
  Axis = (0,1,0)
  Base = (0,0,0)
  FaceMakerClass = Part::FaceMakerBullseye
  Placement = pos=(0,0,0) rot=(0,0,1;1.5708rad)
  Solid = false
  Source = -> Face024
  Symmetric = false
FEATURE [Part::Feature] Face025
  shape: bbox 9.8 x 26.5 x 2e-07 mm, 1 faces, 0 solids (baked)
FEATURE [Part::Revolution] Revolve025
  Angle = 360
  Axis = (0,1,0)
  Base = (0,0,0)
  FaceMakerClass = Part::FaceMakerBullseye
  Placement = pos=(0,0,0) rot=(0,0,1;1.5708rad)
  Solid = false
  Source = -> Face025
  Symmetric = false
FEATURE [Part::MultiFuse] Fusion033
  Placement = pos=(-18,19,36) rot=(0,0,1;0rad)
  Shapes = -> [Revolve025,Revolve024]
FEATURE [Part::Cylinder] Cylinder014
  Angle = 360
  AttacherType = Attacher::AttachEngine3D
  Height = 20
  Placement = pos=(0,0,36.15) rot=(0,0,1;0rad)
  Radius = 14.3
FEATURE [Part::Cylinder] Cylinder015
  Angle = 360
  AttacherType = Attacher::AttachEngine3D
  Height = 10
  Placement = pos=(0,0,36.15) rot=(0,0,1;0rad)
  Radius = 4
FEATURE [Part::MultiFuse] Fusion034  label="removeToCreteHoleForPlugHousing004"
  Placement = pos=(-42,19,36) rot=(0,1,0;1.5708rad)
  Shapes = -> [Cylinder014,Cylinder015]
FEATURE [Part::Cut] Cut008  label="top004"
  Base = -> Cut004
  Placement = pos=(-1,0,0) rot=(0,0,1;0rad)
  Tool = -> Fusion034
FEATURE [Part::Box] Box005  label="Cube005"
  AttacherType = Attacher::AttachEngine3D
  Height = 28
  Length = 3
  Placement = pos=(110.7,19,22) rot=(0,0,1;0rad)
  Width = 15.7
FEATURE [Part::Cylinder] Cylinder016
  Angle = 360
  AttacherType = Attacher::AttachEngine3D
  Height = 10
  Placement = pos=(0,0,36.15) rot=(0,0,1;0rad)
  Radius = 4
FEATURE [Part::Cylinder] Cylinder017
  Angle = 360
  AttacherType = Attacher::AttachEngine3D
  Height = 20
  Placement = pos=(0,0,36.15) rot=(0,0,1;0rad)
  Radius = 10.3
FEATURE [Part::MultiFuse] Fusion035  label="removeToCreteHoleForPlugHousing005"
  Placement = pos=(70,19,36) rot=(0,1,0;1.5708rad)
  Shapes = -> [Cylinder017,Cylinder016]
FEATURE [Part::Cut] Cut009  label="plugHousingTab001"
  Base = -> Box005
  Placement = pos=(-107.4,-14,0) rot=(0,0,1;0rad)
  Tool = -> Fusion035
FEATURE [Part::Box] Box006  label="Cube006"
  AttacherType = Attacher::AttachEngine3D
  Height = 28
  Length = 3
  Placement = pos=(110.7,19,22) rot=(0,0,1;0rad)
  Width = 15.7
FEATURE [Part::Cylinder] Cylinder018
  Angle = 360
  AttacherType = Attacher::AttachEngine3D
  Height = 10
  Placement = pos=(0,0,36.15) rot=(0,0,1;0rad)
  Radius = 4
FEATURE [Part::Cylinder] Cylinder019
  Angle = 360
  AttacherType = Attacher::AttachEngine3D
  Height = 20
  Placement = pos=(0,0,36.15) rot=(0,0,1;0rad)
  Radius = 10.3
FEATURE [Part::MultiFuse] Fusion036  label="removeToCreteHoleForPlugHousing006"
  Placement = pos=(70,19,36) rot=(0,1,0;1.5708rad)
  Shapes = -> [Cylinder019,Cylinder018]
FEATURE [Part::Cut] Cut010  label="plugHousingTab002"
  Base = -> Box006
  Placement = pos=(-107.4,-14,0) rot=(0,0,1;0rad)
  Tool = -> Fusion036
FEATURE [Part::MultiFuse] Fusion037
  Placement = pos=(9.6,23,0) rot=(0,0,1;3.14159rad)
  Shapes = -> [Cut009,Cut010]
FEATURE [Part::Box] Box  label="Cube"
  AttacherType = Attacher::AttachEngine3D
  Height = 10
  Length = 3
  Placement = pos=(3.3,4,12) rot=(0,0,1;0rad)
  Width = 10
FEATURE [Part::Fillet] Fillet004
  Base = -> Fusion028
  Edges = 1 edges r=2: [Edge25]
FEATURE [Part::Fillet] Fillet005  label="plugHousing046"
  Base = -> Fillet004
  Edges = 1 edges r=2: [Edge8]
FEATURE [Part::Fillet] Fillet006
  Base = -> Box
  Edges = 1 edges r=2: [Edge11]
FEATURE [Part::Box] Box007  label="Cube007"
  AttacherType = Attacher::AttachEngine3D
  Height = 10
  Length = 3
  Placement = pos=(3.3,4,50) rot=(0,0,1;0rad)
  Width = 10
FEATURE [Part::Fillet] Fillet007
  Base = -> Box007
  Edges = 1 edges r=2: [Edge12]
FEATURE [Part::Box] Box008  label="Cube008"
  AttacherType = Attacher::AttachEngine3D
  Height = 28
  Length = 4
  Placement = pos=(5,0,22) rot=(0,0,1;0rad)
  Width = 10
FEATURE [Part::Fillet] Fillet008
  Base = -> Box008
  Edges = 1 edges r=1: [Edge7]
FEATURE [Part::Fillet] Fillet009
  Base = -> Fillet008
  Edges = 1 edges r=2: [Edge5]
FEATURE [Part::Fillet] Fillet010
  Base = -> Fillet009
  Edges = 1 edges r=2: [Edge2]
FEATURE [Sketcher::SketchObject] Sketch009  label="topSketch003"
  FullyConstrained = true
  sketch-geometry (4):
    g0: LineSegment StartX=16.8446 StartY=31.512 StartZ=0 EndX=16.3251 EndY=34.4666 EndZ=0
    g1: ArcOfCircle CenterX=19 CenterY=19.2524 CenterZ=0 NormalX=0 NormalY=0 NormalZ=1 AngleXU=0 Radius=15.4476 StartAngle=1.74483 EndAngle=2.72717
    g2: ArcOfCircle CenterX=19 CenterY=19.2524 CenterZ=0 NormalX=0 NormalY=0 NormalZ=1 AngleXU=0 Radius=12.4476 StartAngle=1.74483 EndAngle=2.73189
    g3: LineSegment StartX=4.86004 StartY=25.4725 StartZ=0 EndX=7.58253 EndY=24.2107 EndZ=0
  constraints (7):
    c: Block(g0)
    c: Coincident(g1,g0)
    c: Coincident(g2,g0)
    c: Coincident(g3,g1)
    c: Coincident(g3,g2)
    c: Block(g1)
    c: Block(g2)
FEATURE [Part::Extrusion] Extrude008
  Base = -> Sketch009
  Dir = (0,0,1)
  DirMode = 2
  FaceMakerClass = Part::FaceMakerBullseye
  LengthFwd = 10
  LengthRev = 0
  Placement = pos=(0,0,31) rot=(0,0,1;0rad)
  Solid = true
  Symmetric = false
FEATURE [Part::Cylinder] Cylinder020
  Angle = 360
  AttacherType = Attacher::AttachEngine3D
  Height = 20
  Placement = pos=(0,0,36.15) rot=(0,0,1;0rad)
  Radius = 8.2
FEATURE [Part::Cylinder] Cylinder021
  Angle = 360
  AttacherType = Attacher::AttachEngine3D
  Height = 10
  Placement = pos=(0,0,36.15) rot=(0,0,1;0rad)
  Radius = 4
FEATURE [Part::MultiFuse] Fusion038  label="removeToCreteHoleForPlugHousing007"
  Placement = pos=(-42,19,36) rot=(0,1,0;1.5708rad)
  Shapes = -> [Cylinder020,Cylinder021]
FEATURE [Part::Cut] Cut011
  Base = -> Extrude008
  Tool = -> Fusion038
FEATURE [Part::Fillet] Fillet011
  Base = -> Cut011
  Edges = 1 edges r=2: [Edge1]
FEATURE [Part::Fillet] Fillet012
  Base = -> Fillet011
  Edges = 1 edges r=2.5: [Edge1]
FEATURE [Part::Fillet] Fillet013
  Base = -> Fillet012
  Edges = 1 edges r=2.5: [Edge2]
FEATURE [Part::Box] Box010  label="Cube010"
  AttacherType = Attacher::AttachEngine3D
  Height = 16
  Length = 8
  Placement = pos=(12.7,31.52,28) rot=(0,0,1;0rad)
  Width = 4
FEATURE [Sketcher::SketchObject] Sketch010  label="topSketch004"
  FullyConstrained = true
  sketch-geometry (4):
    g0: LineSegment StartX=16.8446 StartY=31.512 StartZ=0 EndX=16.3251 EndY=34.4666 EndZ=0
    g1: ArcOfCircle CenterX=19 CenterY=19.2524 CenterZ=0 NormalX=0 NormalY=0 NormalZ=1 AngleXU=0 Radius=15.4476 StartAngle=1.74483 EndAngle=2.72717
    g2: ArcOfCircle CenterX=19 CenterY=19.2524 CenterZ=0 NormalX=0 NormalY=0 NormalZ=1 AngleXU=0 Radius=12.4476 StartAngle=1.74483 EndAngle=2.73189
    g3: LineSegment StartX=4.86004 StartY=25.4725 StartZ=0 EndX=7.58253 EndY=24.2107 EndZ=0
  constraints (7):
    c: Block(g0)
    c: Coincident(g1,g0)
    c: Coincident(g2,g0)
    c: Coincident(g3,g1)
    c: Coincident(g3,g2)
    c: Block(g1)
    c: Block(g2)
FEATURE [Part::Cylinder] Cylinder022
  Angle = 360
  AttacherType = Attacher::AttachEngine3D
  Height = 10
  Placement = pos=(0,0,36.15) rot=(0,0,1;0rad)
  Radius = 4
FEATURE [Sketcher::SketchObject] Sketch011  label="topSketch005"
  FullyConstrained = true
  sketch-geometry (4):
    g0: LineSegment StartX=16.8446 StartY=31.512 StartZ=0 EndX=16.3251 EndY=34.4666 EndZ=0
    g1: ArcOfCircle CenterX=19 CenterY=19.2524 CenterZ=0 NormalX=0 NormalY=0 NormalZ=1 AngleXU=0 Radius=15.4476 StartAngle=1.74483 EndAngle=2.72717
    g2: ArcOfCircle CenterX=19 CenterY=19.2524 CenterZ=0 NormalX=0 NormalY=0 NormalZ=1 AngleXU=0 Radius=12.4476 StartAngle=1.74483 EndAngle=2.73189
    g3: LineSegment StartX=4.86004 StartY=25.4725 StartZ=0 EndX=7.58253 EndY=24.2107 EndZ=0
  constraints (7):
    c: Block(g0)
    c: Coincident(g1,g0)
    c: Coincident(g2,g0)
    c: Coincident(g3,g1)
    c: Coincident(g3,g2)
    c: Block(g1)
    c: Block(g2)
FEATURE [Part::Extrusion] Extrude010
  Base = -> Sketch011
  Dir = (0,0,1)
  DirMode = 2
  FaceMakerClass = Part::FaceMakerBullseye
  LengthFwd = 10.6
  LengthRev = 0
  Placement = pos=(0,0,31) rot=(0,0,1;0rad)
  Solid = true
  Symmetric = false
FEATURE [Part::Cylinder] Cylinder023
  Angle = 360
  AttacherType = Attacher::AttachEngine3D
  Height = 20
  Placement = pos=(0,0,36.15) rot=(0,0,1;0rad)
  Radius = 8.2
FEATURE [Part::MultiFuse] Fusion039  label="removeToCreteHoleForPlugHousing008"
  Placement = pos=(-42,19,36) rot=(0,1,0;1.5708rad)
  Shapes = -> [Cylinder023,Cylinder022]
FEATURE [Part::Cut] Cut012
  Base = -> Extrude010
  Placement = pos=(0,0,-0.3) rot=(0,0,1;0rad)
  Tool = -> Fusion039
FEATURE [Part::Cut] Cut013
  Base = -> Box010
  Tool = -> Cut012
FEATURE [Part::Fillet] Fillet014
  Base = -> Cut013
  Edges = 1 edges r=0.7: [Edge13]
FEATURE [Part::Fillet] Fillet015
  Base = -> Fillet014
  Edges = 1 edges r=0.7: [Edge13]
FEATURE [Part::Fillet] Fillet016
  Base = -> Fillet015
  Edges = 1 edges r=0.7: [Edge16]
FEATURE [Part::Fillet] Fillet017
  Base = -> Fillet016
  Edges = 1 edges r=0.7: [Edge11]
FEATURE [Part::Fillet] Fillet018
  Base = -> Fillet017
  Edges = 1 edges r=0.7: [Edge10]
FEATURE [Part::Fillet] Fillet019
  Base = -> Fillet018
  Edges = 1 edges r=1.2: [Edge5]
FEATURE [Part::Fillet] Fillet020
  Base = -> Fillet019
  Edges = 1 edges r=1.2: [Edge12]
FEATURE [Part::Fillet] Fillet021
  Base = -> Fillet020
  Edges = 1 edges r=2: [Edge1]
  Placement = pos=(0.3,0,0) rot=(0,0,1;0rad)
FEATURE [Part::MultiFuse] Fusion040  label="top005"
  Shapes = -> [Cut008,Fillet021]
FEATURE [Part::MultiFuse] Fusion041  label="wireHolder"
  Shapes = -> [Fusion033,Fillet013]
FEATURE [Part::MultiFuse] Fusion042
  Shapes = -> [Fillet007,Fusion041]
FEATURE [Part::MultiFuse] Fusion043  label="wireHolder001"
  Shapes = -> [Fusion042,Fillet010]
FEATURE [Part::MultiFuse] Fusion044  label="wireHolder002"
  Shapes = -> [Fillet006,Fusion037,Fusion043]
FEATURE [Part::Feature] Face026
  shape: bbox 11 x 6 x 2e-07 mm, 1 faces, 0 solids (baked)
FEATURE [Part::Revolution] Revolve026
  Angle = 360
  Axis = (0,1,0)
  Base = (0,0,0)
  FaceMakerClass = Part::FaceMakerBullseye
  Placement = pos=(30.3,-1,19.7) rot=(0,0,1;0rad)
  Solid = false
  Source = -> Face026
  Symmetric = false
FEATURE [Sketcher::SketchObject] Sketch013  label="topSketch006"
  FullyConstrained = true
  sketch-geometry (13):
    g0: LineSegment StartX=117 StartY=19 StartZ=0 EndX=117 EndY=38 EndZ=0
    g1: ArcOfCircle CenterX=98 CenterY=19 CenterZ=0 NormalX=0 NormalY=0 NormalZ=1 AngleXU=0 Radius=19 StartAngle=5.7297 EndAngle=6.28319
    g2: LineSegment StartX=0 StartY=3 StartZ=0 EndX=0 EndY=19 EndZ=0
    g3: LineSegment StartX=19 StartY=38 StartZ=0 EndX=117 EndY=38 EndZ=0
    g4: ArcOfCircle CenterX=19 CenterY=19 CenterZ=0 NormalX=0 NormalY=0 NormalZ=1 AngleXU=0 Radius=19 StartAngle=1.5708 EndAngle=3.14159
    g5: ArcOfCircle CenterX=19 CenterY=19 CenterZ=0 NormalX=0 NormalY=0 NormalZ=1 AngleXU=0 Radius=16 StartAngle=1.5708 EndAngle=3.14159
    g6: ArcOfCircle CenterX=98 CenterY=19 CenterZ=0 NormalX=0 NormalY=0 NormalZ=1 AngleXU=0 Radius=16 StartAngle=5.60905 EndAngle=6.28319
    g7: LineSegment StartX=114 StartY=19 StartZ=0 EndX=114 EndY=35 EndZ=0
    g8: LineSegment StartX=110.5 StartY=9.01251 StartZ=0 EndX=114.163 EndY=9.01251 EndZ=0
    g9: LineSegment StartX=114 StartY=35 StartZ=0 EndX=19 EndY=35 EndZ=0
    g10: LineSegment StartX=0 StartY=3 StartZ=0 EndX=0 EndY=0 EndZ=0
    g11: LineSegment StartX=3 StartY=0 StartZ=0 EndX=0 EndY=0 EndZ=0
    g12: LineSegment StartX=3 StartY=19 StartZ=0 EndX=3 EndY=0 EndZ=0
  constraints (33):
    c: Vertical(g0)
    c: Distance(g0) = 19
    c: Block(g0)
    c: Coincident(g1,g0)
    c: Block(g1)
    c: Vertical(g2)
    c: Block(g2)
    c: Coincident(g3,g0)
    c: Horizontal(g3)
    c: Distance(g3) = 98
    c: Coincident(g4,g3)
    c: Coincident(g4,g2)
    c: Block(g4)
    c: Coincident(g5,g4)
    c: Coincident(g6,g1)
    c: Block(g6)
    c: Block(g5)
    c: Coincident(g7,g6)
    c: Vertical(g7)
    c: Coincident(g8,g6)
    c: Coincident(g8,g1)
    c: Coincident(g9,g7)
    c: Coincident(g9,g5)
    c: Horizontal(g9)
    c: Tangent(g9,g5)
    c: Coincident(g10,g2)
    c: Distance(g10) = 3
    c: Vertical(g10)
    c: Coincident(g11,g10)
    c: Horizontal(g11)
    c: Coincident(g12,g5)
    c: Coincident(g12,g11)
    c: Vertical(g12)
FEATURE [Part::Extrusion] Extrude011  label="top006"
  Base = -> Sketch013
  Dir = (0,0,1)
  DirMode = 2
  FaceMakerClass = Part::FaceMakerBullseye
  LengthFwd = 72
  LengthRev = 0
  Solid = true
  Symmetric = false
FEATURE [Sketcher::SketchObject] Sketch014
  FullyConstrained = true
  MapMode = 3
  Placement = pos=(0,0,0) rot=(1,0,0;1.5708rad)
  Support = -> [Extrude011]
  sketch-geometry (8):
    g0: Circle CenterX=80.351 CenterY=-67.6202 CenterZ=0 NormalX=0 NormalY=0 NormalZ=1 AngleXU=0 Radius=2
    g1: Circle CenterX=80.351 CenterY=-67.6202 CenterZ=0 NormalX=0 NormalY=0 NormalZ=1 AngleXU=0 Radius=3
    g2: Circle CenterX=80.351 CenterY=-4.92017 CenterZ=0 NormalX=0 NormalY=0 NormalZ=1 AngleXU=0 Radius=2
    g3: Circle CenterX=80.351 CenterY=-4.92017 CenterZ=0 NormalX=0 NormalY=0 NormalZ=1 AngleXU=0 Radius=3
    g4: Circle CenterX=23.851 CenterY=-4.92017 CenterZ=0 NormalX=0 NormalY=0 NormalZ=1 AngleXU=0 Radius=2
    g5: Circle CenterX=23.851 CenterY=-4.92017 CenterZ=0 NormalX=0 NormalY=0 NormalZ=1 AngleXU=0 Radius=3
    g6: Circle CenterX=23.851 CenterY=-67.6202 CenterZ=0 NormalX=0 NormalY=0 NormalZ=1 AngleXU=0 Radius=2
    g7: Circle CenterX=23.851 CenterY=-67.6202 CenterZ=0 NormalX=0 NormalY=0 NormalZ=1 AngleXU=0 Radius=3
  constraints (8):
    c: Block(g3)
    c: Block(g2)
    c: Block(g1)
    c: Block(g0)
    c: Block(g6)
    c: Block(g7)
    c: Block(g4)
    c: Block(g5)
FEATURE [Part::Feature] Face027
  shape: bbox 11 x 6 x 2e-07 mm, 1 faces, 0 solids (baked)
FEATURE [Part::Revolution] Revolve027
  Angle = 360
  Axis = (0,1,0)
  Base = (0,0,0)
  FaceMakerClass = Part::FaceMakerBullseye
  Placement = pos=(30.3,-1,51.7) rot=(0,0,1;0rad)
  Solid = false
  Source = -> Face027
  Symmetric = false
FEATURE [Part::Feature] Face028
  shape: bbox 11 x 6 x 2e-07 mm, 1 faces, 0 solids (baked)
FEATURE [Part::Revolution] Revolve028
  Angle = 360
  Axis = (0,1,0)
  Base = (0,0,0)
  FaceMakerClass = Part::FaceMakerBullseye
  Placement = pos=(62.3,-1,19.7) rot=(0,0,1;0rad)
  Solid = false
  Source = -> Face028
  Symmetric = false
FEATURE [Part::Feature] Face029
  shape: bbox 11 x 6 x 2e-07 mm, 1 faces, 0 solids (baked)
FEATURE [Part::Revolution] Revolve029
  Angle = 360
  Axis = (0,1,0)
  Base = (0,0,0)
  FaceMakerClass = Part::FaceMakerBullseye
  Placement = pos=(62.3,-1,51.7) rot=(0,0,1;0rad)
  Solid = false
  Source = -> Face029
  Symmetric = false
FEATURE [Part::Feature] Wire
  shape: bbox 11 x 5.2 x 2e-07 mm, 0 faces, 0 solids (baked)
FEATURE [Part::Revolution] Revolve030
  Angle = 360
  Axis = (0,1,0)
  Base = (0,0,0)
  FaceMakerClass = Part::FaceMakerBullseye
  Placement = pos=(30.3,38,19.7) rot=(0,0,1;0rad)
  Solid = true
  Source = -> Wire
  Symmetric = false
FEATURE [Part::Feature] Wire001
  shape: bbox 11 x 5.2 x 2e-07 mm, 0 faces, 0 solids (baked)
FEATURE [Part::Revolution] Revolve031
  Angle = 360
  Axis = (0,1,0)
  Base = (0,0,0)
  FaceMakerClass = Part::FaceMakerBullseye
  Placement = pos=(30.3,38,51.7) rot=(0,0,1;0rad)
  Solid = true
  Source = -> Wire001
  Symmetric = false
FEATURE [Part::Feature] Wire002
  shape: bbox 11 x 5.2 x 2e-07 mm, 0 faces, 0 solids (baked)
FEATURE [Part::Revolution] Revolve032
  Angle = 360
  Axis = (0,1,0)
  Base = (0,0,0)
  FaceMakerClass = Part::FaceMakerBullseye
  Placement = pos=(62.3,38,51.7) rot=(0,0,1;0rad)
  Solid = true
  Source = -> Wire002
  Symmetric = false
FEATURE [Part::Feature] Wire003
  shape: bbox 11 x 5.2 x 2e-07 mm, 0 faces, 0 solids (baked)
FEATURE [Part::Revolution] Revolve033
  Angle = 360
  Axis = (0,1,0)
  Base = (0,0,0)
  FaceMakerClass = Part::FaceMakerBullseye
  Placement = pos=(62.3,38,19.7) rot=(0,0,1;0rad)
  Solid = true
  Source = -> Wire003
  Symmetric = false
FEATURE [Part::MultiFuse] Fusion045  label="altRandScrewHousing"
  Shapes = -> [Revolve029,Revolve027,Revolve028,Revolve026]
FEATURE [Part::MultiFuse] Fusion046  label="fanScrewHousing"
  Shapes = -> [Revolve033,Revolve032,Revolve031,Revolve030]
FEATURE [Sketcher::SketchObject] Sketch015
  FullyConstrained = true
  sketch-geometry (17):
    g0: Circle CenterX=-3.5 CenterY=23.5 CenterZ=0 NormalX=0 NormalY=0 NormalZ=1 AngleXU=0 Radius=1
    g1: Circle CenterX=-1 CenterY=15.25 CenterZ=0 NormalX=0 NormalY=0 NormalZ=1 AngleXU=0 Radius=1
    g2: Circle CenterX=-3.5 CenterY=7 CenterZ=0 NormalX=0 NormalY=0 NormalZ=1 AngleXU=0 Radius=1
    g3: BSplineCurve PolesCount=3 KnotsCount=2 Degree=2 IsPeriodic=0
    g4: GeomPoint X=-3.5 Y=23.5 Z=0
    g5: GeomPoint X=-3.5 Y=7 Z=0
    g6: Circle CenterX=-4.8 CenterY=30.5 CenterZ=0 NormalX=0 NormalY=0 NormalZ=1 AngleXU=0 Radius=1
    g7: Circle CenterX=-3.5 CenterY=30.5 CenterZ=0 NormalX=0 NormalY=0 NormalZ=1 AngleXU=0 Radius=1
    g8: Circle CenterX=-3.5 CenterY=29.2 CenterZ=0 NormalX=0 NormalY=0 NormalZ=1 AngleXU=0 Radius=1
    g9: BSplineCurve PolesCount=3 KnotsCount=2 Degree=2 IsPeriodic=0
    g10: GeomPoint X=-4.8 Y=30.5 Z=0
    g11: GeomPoint X=-3.5 Y=29.2 Z=0
    g12: LineSegment StartX=-3.5 StartY=29.2 StartZ=0 EndX=-3.5 EndY=23.5 EndZ=0
    g13: LineSegment StartX=-4.8 StartY=30.5 StartZ=0 EndX=0 EndY=30.5 EndZ=0
    g14: LineSegment StartX=-3.5 StartY=0.3 StartZ=0 EndX=0 EndY=0.3 EndZ=0
    g15: LineSegment StartX=-3.5 StartY=0.3 StartZ=0 EndX=-3.5 EndY=7 EndZ=0
    g16: LineSegment StartX=0 StartY=0.3 StartZ=0 EndX=0 EndY=30.5 EndZ=0
  constraints (33):
    c: Weight(g0) = 1
    c: Equal(g0,g1)
    c: Equal(g0,g2)
    c: InternalAlignment(g0,g3)
    c: InternalAlignment(g1,g3)
    c: InternalAlignment(g2,g3)
    c: InternalAlignment(g4,g3)
    c: InternalAlignment(g5,g3)
    c: Block(g3)
    c: Weight(g6) = 1
    c: Equal(g6,g7)
    c: Equal(g6,g8)
    c: InternalAlignment(g6,g9)
    c: InternalAlignment(g7,g9)
    c: InternalAlignment(g8,g9)
    c: InternalAlignment(g10,g9)
    c: InternalAlignment(g11,g9)
    c: Block(g9)
    c: Coincident(g12,g9)
    c: Coincident(g12,g3)
    c: Vertical(g12)
    c: Coincident(g13,g9)
    c: Horizontal(g13)
    c: Distance(g13) = 4.8
    c: Horizontal(g14)
    c: Block(g14)
    c: Coincident(g15,g14)
    c: Coincident(g15,g3)
    c: Vertical(g15)
    c: Coincident(g16,g14)
    c: Coincident(g16,g13)
    c: Vertical(g16)
    c: Tangent(g16,g1)
FEATURE [Sketcher::SketchObject] Sketch016
  FullyConstrained = true
  sketch-geometry (16):
    g0: Circle CenterX=-3.5 CenterY=23.5 CenterZ=0 NormalX=0 NormalY=0 NormalZ=1 AngleXU=0 Radius=1
    g1: Circle CenterX=-1 CenterY=15.25 CenterZ=0 NormalX=0 NormalY=0 NormalZ=1 AngleXU=0 Radius=1
    g2: Circle CenterX=-3.5 CenterY=7 CenterZ=0 NormalX=0 NormalY=0 NormalZ=1 AngleXU=0 Radius=1
    g3: BSplineCurve PolesCount=3 KnotsCount=2 Degree=2 IsPeriodic=0
    g4: GeomPoint X=-3.5 Y=23.5 Z=0
    g5: GeomPoint X=-3.5 Y=7 Z=0
    g6: LineSegment StartX=-3.5 StartY=28.2 StartZ=0 EndX=-3.5 EndY=23.5 EndZ=0
    g7: LineSegment StartX=0 StartY=29.5 StartZ=0 EndX=0 EndY=30 EndZ=0
    g8: LineSegment StartX=-3.5 StartY=28.2 StartZ=0 EndX=-3.5 EndY=30 EndZ=0
    g9: LineSegment StartX=0 StartY=30 StartZ=0 EndX=0 EndY=30.5 EndZ=0
    g10: LineSegment StartX=0 StartY=30.5 StartZ=0 EndX=-3.5 EndY=30.5 EndZ=0
    g11: LineSegment StartX=-3.5 StartY=30.5 StartZ=0 EndX=-3.5 EndY=30 EndZ=0
    g12: LineSegment StartX=0 StartY=29.5 StartZ=0 EndX=0 EndY=5 EndZ=0
    g13: LineSegment StartX=-3.5 StartY=0.3 StartZ=0 EndX=-3.5 EndY=7 EndZ=0
    g14: LineSegment StartX=-3.5 StartY=0.3 StartZ=0 EndX=0 EndY=0.3 EndZ=0
    g15: LineSegment StartX=0 StartY=5 StartZ=0 EndX=0 EndY=0.3 EndZ=0
  constraints (39):
    c: Weight(g0) = 1
    c: Equal(g0,g1)
    c: Equal(g0,g2)
    c: InternalAlignment(g0,g3)
    c: InternalAlignment(g1,g3)
    c: InternalAlignment(g2,g3)
    c: InternalAlignment(g4,g3)
    c: InternalAlignment(g5,g3)
    c: Block(g3)
    c: Coincident(g6,g3)
    c: Vertical(g6)
    c: Vertical(g7)
    c: Distance(g7) = 0.5
    c: Coincident(g8,g6)
    c: Vertical(g8)
    c: Block(g6)
    c: Block(g7)
    c: Vertical(g9)
    c: Equal(g7,g9) = 0.5
    c: Block(g9)
    c: Coincident(g9,g7)
    c: Horizontal(g10)
    c: Coincident(g10,g9)
    c: Coincident(g11,g10)
    c: Coincident(g11,g8)
    c: Vertical(g11)
    c: Block(g11)
    c: Coincident(g12,g7)
    c: Vertical(g12)
    c: Coincident(g13,g3)
    c: Vertical(g13)
    c: Distance(g13) = 6.7
    c: Coincident(g14,g13)
    c: Horizontal(g14)
    c: Block(g14)
    c: Coincident(g15,g12)
    c: Coincident(g15,g14)
    c: Vertical(g15)
    c: Block(g15)
FEATURE [Sketcher::SketchObject] Sketch017
  FullyConstrained = true
  sketch-geometry (11):
    g0: LineSegment StartX=-3.5 StartY=1e-16 StartZ=0 EndX=-1.6 EndY=1e-16 EndZ=0
    g1: LineSegment StartX=-1.6 StartY=1e-16 StartZ=0 EndX=-1.6 EndY=1.5 EndZ=0
    g2: LineSegment StartX=-3.5 StartY=1.5 StartZ=0 EndX=-1.6 EndY=1.5 EndZ=0
    g3: LineSegment StartX=-3.5 StartY=1e-16 StartZ=0 EndX=-4.8 EndY=1e-16 EndZ=0
    g4: Circle CenterX=-3.5 CenterY=1.3 CenterZ=0 NormalX=0 NormalY=0 NormalZ=1 AngleXU=0 Radius=1
    g5: Circle CenterX=-3.5 CenterY=1e-16 CenterZ=0 NormalX=0 NormalY=0 NormalZ=1 AngleXU=0 Radius=1
    g6: Circle CenterX=-4.8 CenterY=1e-16 CenterZ=0 NormalX=0 NormalY=0 NormalZ=1 AngleXU=0 Radius=1
    g7: BSplineCurve PolesCount=3 KnotsCount=2 Degree=2 IsPeriodic=0
    g8: GeomPoint X=-3.5 Y=1.3 Z=0
    g9: GeomPoint X=-4.8 Y=1e-16 Z=0
    g10: LineSegment StartX=-3.5 StartY=1.3 StartZ=0 EndX=-3.5 EndY=1.5 EndZ=0
  constraints (24):
    c: Horizontal(g0)
    c: Distance(g0) = 1.9
    c: Block(g0)
    c: Coincident(g1,g0)
    c: Vertical(g1)
    c: Coincident(g2,g1)
    c: Horizontal(g2)
    c: Coincident(g3,g0)
    c: Horizontal(g3)
    c: Distance(g3) = 1.3
    c: Weight(g4) = 1
    c: Equal(g4,g5)
    c: Coincident(g5,g0)
    c: Equal(g4,g6)
    c: Coincident(g7,g3)
    c: InternalAlignment(g4,g7)
    c: InternalAlignment(g5,g7)
    c: InternalAlignment(g6,g7)
    c: InternalAlignment(g8,g7)
    c: InternalAlignment(g9,g7)
    c: Coincident(g10,g7)
    c: Coincident(g10,g2)
    c: Vertical(g10)
    c: Block(g10)
FEATURE [Part::Feature] Face035
  shape: bbox 3.2 x 1.5 x 2e-07 mm, 1 faces, 0 solids (baked)
FEATURE [Part::Revolution] Revolve039  label="backCaseScrewRetainer"
  Angle = 360
  Axis = (0,1,0)
  Base = (0,0,0)
  FaceMakerClass = Part::FaceMakerBullseye
  Placement = pos=(12.5,3,62) rot=(0,0,1;0rad)
  Solid = false
  Source = -> Face035
  Symmetric = false
FEATURE [Part::Feature] Face036
  shape: bbox 3.2 x 1.5 x 2e-07 mm, 1 faces, 0 solids (baked)
FEATURE [Part::Feature] Face039
  shape: bbox 4.8 x 30.2 x 2e-07 mm, 1 faces, 0 solids (baked)
FEATURE [Part::Revolution] Revolve043  label="frontCaseScrewPost002"
  Angle = 360
  Axis = (0,1,0)
  Base = (0,0,0)
  FaceMakerClass = Part::FaceMakerBullseye
  Placement = pos=(89.5,4.5,3.5) rot=(0,0,1;0rad)
  Solid = false
  Source = -> Face039
  Symmetric = false
FEATURE [Part::Feature] Face042
  shape: bbox 4.8 x 30.2 x 2e-07 mm, 1 faces, 0 solids (baked)
FEATURE [Part::Revolution] Revolve046  label="frontCaseScrewPost003"
  Angle = 360
  Axis = (0,1,0)
  Base = (0,0,0)
  FaceMakerClass = Part::FaceMakerBullseye
  Placement = pos=(89.5,4.5,68.5) rot=(0,0,1;0rad)
  Solid = false
  Source = -> Face042
  Symmetric = false
FEATURE [Part::Feature] Face043
  shape: bbox 3.2 x 1.5 x 2e-07 mm, 1 faces, 0 solids (baked)
FEATURE [Part::Revolution] Revolve047  label="frontCaseScrewRetainer002"
  Angle = 360
  Axis = (0,1,0)
  Base = (0,0,0)
  FaceMakerClass = Part::FaceMakerBullseye
  Placement = pos=(89.5,3,68.5) rot=(0,0,1;0rad)
  Solid = false
  Source = -> Face043
  Symmetric = false
FEATURE [Part::Feature] Face044
  shape: bbox 3.2 x 1.5 x 2e-07 mm, 1 faces, 0 solids (baked)
FEATURE [Part::Revolution] Revolve048  label="frontCaseScrewRetainer003"
  Angle = 360
  Axis = (0,1,0)
  Base = (0,0,0)
  FaceMakerClass = Part::FaceMakerBullseye
  Placement = pos=(89.5,3,3.5) rot=(0,0,1;0rad)
  Solid = false
  Source = -> Face044
  Symmetric = false
FEATURE [App::MeasureDistance] Distance002  label="Distance: 1.67 mm"
  Distance = 1.66921
  P1 = (99.2361,4.7524,71.7)
  P2 = (99.2347,6.42161,71.7)
FEATURE [Sketcher::SketchObject] Sketch018
  FullyConstrained = true
  sketch-geometry (7):
    g0: LineSegment StartX=0 StartY=0 StartZ=0 EndX=0 EndY=6 EndZ=0
    g1: Circle CenterX=0 CenterY=0 CenterZ=0 NormalX=0 NormalY=0 NormalZ=1 AngleXU=0 Radius=1
    g2: Circle CenterX=8 CenterY=6 CenterZ=0 NormalX=0 NormalY=0 NormalZ=1 AngleXU=0 Radius=1
    g3: BSplineCurve PolesCount=3 KnotsCount=2 Degree=2 IsPeriodic=0
    g4: GeomPoint X=0 Y=0 Z=0
    g5: GeomPoint X=8 Y=6 Z=0
    g6: LineSegment StartX=0 StartY=6 StartZ=0 EndX=8 EndY=6 EndZ=0
  constraints (14):
    c: Coincident(g0,g-1)
    c: Distance(g0) = 6
    c: Vertical(g0)
    c: Coincident(g3,g0)
    c: Weight(g1) = 1
    c: Equal(g1,g2)
    c: InternalAlignment(g1,g3)
    c: InternalAlignment(g2,g3)
    c: InternalAlignment(g4,g3)
    c: InternalAlignment(g5,g3)
    c: Block(g3)
    c: Coincident(g6,g0)
    c: Coincident(g6,g3)
    c: Horizontal(g6)
FEATURE [Part::Extrusion] Extrude012  label="caseScrewPillarBracket"
  Base = -> Sketch018
  Dir = (0,0,1)
  DirMode = 2
  FaceMakerClass = Part::FaceMakerBullseye
  LengthFwd = 2.4
  LengthRev = 0
  Placement = pos=(15.76,29,8.8) rot=(0,1,0;0rad)
  Solid = true
  Symmetric = false
FEATURE [Sketcher::SketchObject] Sketch019
  FullyConstrained = true
  sketch-geometry (7):
    g0: LineSegment StartX=0 StartY=0 StartZ=0 EndX=0 EndY=6 EndZ=0
    g1: Circle CenterX=0 CenterY=0 CenterZ=0 NormalX=0 NormalY=0 NormalZ=1 AngleXU=0 Radius=1
    g2: Circle CenterX=8 CenterY=6 CenterZ=0 NormalX=0 NormalY=0 NormalZ=1 AngleXU=0 Radius=1
    g3: BSplineCurve PolesCount=3 KnotsCount=2 Degree=2 IsPeriodic=0
    g4: GeomPoint X=0 Y=0 Z=0
    g5: GeomPoint X=8 Y=6 Z=0
    g6: LineSegment StartX=0 StartY=6 StartZ=0 EndX=8 EndY=6 EndZ=0
  constraints (14):
    c: Coincident(g0,g-1)
    c: Distance(g0) = 6
    c: Vertical(g0)
    c: Coincident(g3,g0)
    c: Weight(g1) = 1
    c: Equal(g1,g2)
    c: InternalAlignment(g1,g3)
    c: InternalAlignment(g2,g3)
    c: InternalAlignment(g4,g3)
    c: InternalAlignment(g5,g3)
    c: Block(g3)
    c: Coincident(g6,g0)
    c: Coincident(g6,g3)
    c: Horizontal(g6)
FEATURE [Part::Extrusion] Extrude013  label="caseScrewPillarBracket001"
  Base = -> Sketch019
  Dir = (0,0,1)
  DirMode = 2
  FaceMakerClass = Part::FaceMakerBullseye
  LengthFwd = 2.4
  LengthRev = 0
  Placement = pos=(15.76,29,60.8) rot=(0,0,1;0rad)
  Solid = true
  Symmetric = false
FEATURE [Sketcher::SketchObject] Sketch020
  FullyConstrained = true
  sketch-geometry (7):
    g0: LineSegment StartX=0 StartY=0 StartZ=0 EndX=0 EndY=6 EndZ=0
    g1: Circle CenterX=0 CenterY=0 CenterZ=0 NormalX=0 NormalY=0 NormalZ=1 AngleXU=0 Radius=1
    g2: Circle CenterX=8 CenterY=6 CenterZ=0 NormalX=0 NormalY=0 NormalZ=1 AngleXU=0 Radius=1
    g3: BSplineCurve PolesCount=3 KnotsCount=2 Degree=2 IsPeriodic=0
    g4: GeomPoint X=0 Y=0 Z=0
    g5: GeomPoint X=8 Y=6 Z=0
    g6: LineSegment StartX=0 StartY=6 StartZ=0 EndX=8 EndY=6 EndZ=0
  constraints (14):
    c: Coincident(g0,g-1)
    c: Distance(g0) = 6
    c: Vertical(g0)
    c: Coincident(g3,g0)
    c: Weight(g1) = 1
    c: Equal(g1,g2)
    c: InternalAlignment(g1,g3)
    c: InternalAlignment(g2,g3)
    c: InternalAlignment(g4,g3)
    c: InternalAlignment(g5,g3)
    c: Block(g3)
    c: Coincident(g6,g0)
    c: Coincident(g6,g3)
    c: Horizontal(g6)
FEATURE [Part::Extrusion] Extrude014  label="caseScrewPillarBracket002"
  Base = -> Sketch020
  Dir = (0,0,1)
  DirMode = 2
  FaceMakerClass = Part::FaceMakerBullseye
  LengthFwd = 2.4
  LengthRev = 0
  Placement = pos=(13.7,29,13.26) rot=(0,-1,0;1.5708rad)
  Solid = true
  Symmetric = false
FEATURE [Sketcher::SketchObject] Sketch021
  FullyConstrained = true
  sketch-geometry (7):
    g0: LineSegment StartX=0 StartY=0 StartZ=0 EndX=0 EndY=6 EndZ=0
    g1: Circle CenterX=0 CenterY=0 CenterZ=0 NormalX=0 NormalY=0 NormalZ=1 AngleXU=0 Radius=1
    g2: Circle CenterX=8 CenterY=6 CenterZ=0 NormalX=0 NormalY=0 NormalZ=1 AngleXU=0 Radius=1
    g3: BSplineCurve PolesCount=3 KnotsCount=2 Degree=2 IsPeriodic=0
    g4: GeomPoint X=0 Y=0 Z=0
    g5: GeomPoint X=8 Y=6 Z=0
    g6: LineSegment StartX=0 StartY=6 StartZ=0 EndX=8 EndY=6 EndZ=0
  constraints (14):
    c: Coincident(g0,g-1)
    c: Distance(g0) = 6
    c: Vertical(g0)
    c: Coincident(g3,g0)
    c: Weight(g1) = 1
    c: Equal(g1,g2)
    c: InternalAlignment(g1,g3)
    c: InternalAlignment(g2,g3)
    c: InternalAlignment(g4,g3)
    c: InternalAlignment(g5,g3)
    c: Block(g3)
    c: Coincident(g6,g0)
    c: Coincident(g6,g3)
    c: Horizontal(g6)
FEATURE [Part::Extrusion] Extrude015  label="caseScrewPillarBracket003"
  Base = -> Sketch021
  Dir = (0,0,1)
  DirMode = 2
  FaceMakerClass = Part::FaceMakerBullseye
  LengthFwd = 2.4
  LengthRev = 0
  Placement = pos=(11.3,29,58.74) rot=(0,1,0;1.5708rad)
  Solid = true
  Symmetric = false
FEATURE [Sketcher::SketchObject] Sketch022
  FullyConstrained = true
  sketch-geometry (7):
    g0: LineSegment StartX=0 StartY=0 StartZ=0 EndX=0 EndY=6 EndZ=0
    g1: Circle CenterX=0 CenterY=0 CenterZ=0 NormalX=0 NormalY=0 NormalZ=1 AngleXU=0 Radius=1
    g2: Circle CenterX=8 CenterY=6 CenterZ=0 NormalX=0 NormalY=0 NormalZ=1 AngleXU=0 Radius=1
    g3: BSplineCurve PolesCount=3 KnotsCount=2 Degree=2 IsPeriodic=0
    g4: GeomPoint X=0 Y=0 Z=0
    g5: GeomPoint X=8 Y=6 Z=0
    g6: LineSegment StartX=0 StartY=6 StartZ=0 EndX=8 EndY=6 EndZ=0
  constraints (14):
    c: Coincident(g0,g-1)
    c: Distance(g0) = 6
    c: Vertical(g0)
    c: Coincident(g3,g0)
    c: Weight(g1) = 1
    c: Equal(g1,g2)
    c: InternalAlignment(g1,g3)
    c: InternalAlignment(g2,g3)
    c: InternalAlignment(g4,g3)
    c: InternalAlignment(g5,g3)
    c: Block(g3)
    c: Coincident(g6,g0)
    c: Coincident(g6,g3)
    c: Horizontal(g6)
FEATURE [Part::Extrusion] Extrude016  label="caseScrewPillarBracket004"
  Base = -> Sketch022
  Dir = (0,0,1)
  DirMode = 2
  FaceMakerClass = Part::FaceMakerBullseye
  LengthFwd = 2.4
  LengthRev = 0
  Placement = pos=(88.3,29,65.23) rot=(0,1,0;1.5708rad)
  Solid = true
  Symmetric = false
FEATURE [Sketcher::SketchObject] Sketch023
  FullyConstrained = true
  sketch-geometry (7):
    g0: LineSegment StartX=0 StartY=0 StartZ=0 EndX=0 EndY=6 EndZ=0
    g1: Circle CenterX=0 CenterY=0 CenterZ=0 NormalX=0 NormalY=0 NormalZ=1 AngleXU=0 Radius=1
    g2: Circle CenterX=8 CenterY=6 CenterZ=0 NormalX=0 NormalY=0 NormalZ=1 AngleXU=0 Radius=1
    g3: BSplineCurve PolesCount=3 KnotsCount=2 Degree=2 IsPeriodic=0
    g4: GeomPoint X=0 Y=0 Z=0
    g5: GeomPoint X=8 Y=6 Z=0
    g6: LineSegment StartX=0 StartY=6 StartZ=0 EndX=8 EndY=6 EndZ=0
  constraints (14):
    c: Coincident(g0,g-1)
    c: Distance(g0) = 6
    c: Vertical(g0)
    c: Coincident(g3,g0)
    c: Weight(g1) = 1
    c: Equal(g1,g2)
    c: InternalAlignment(g1,g3)
    c: InternalAlignment(g2,g3)
    c: InternalAlignment(g4,g3)
    c: InternalAlignment(g5,g3)
    c: Block(g3)
    c: Coincident(g6,g0)
    c: Coincident(g6,g3)
    c: Horizontal(g6)
FEATURE [Part::Extrusion] Extrude017  label="caseScrewPillarBracket005"
  Base = -> Sketch023
  Dir = (0,0,1)
  DirMode = 2
  FaceMakerClass = Part::FaceMakerBullseye
  LengthFwd = 2.4
  LengthRev = 0
  Placement = pos=(90.7,29,6.77) rot=(0,-1,0;1.5708rad)
  Solid = true
  Symmetric = false
FEATURE [Sketcher::SketchObject] Sketch024
  FullyConstrained = true
  sketch-geometry (7):
    g0: LineSegment StartX=0 StartY=0 StartZ=0 EndX=0 EndY=6 EndZ=0
    g1: Circle CenterX=0 CenterY=0 CenterZ=0 NormalX=0 NormalY=0 NormalZ=1 AngleXU=0 Radius=1
    g2: Circle CenterX=8 CenterY=6 CenterZ=0 NormalX=0 NormalY=0 NormalZ=1 AngleXU=0 Radius=1
    g3: BSplineCurve PolesCount=3 KnotsCount=2 Degree=2 IsPeriodic=0
    g4: GeomPoint X=0 Y=0 Z=0
    g5: GeomPoint X=8 Y=6 Z=0
    g6: LineSegment StartX=0 StartY=6 StartZ=0 EndX=8 EndY=6 EndZ=0
  constraints (14):
    c: Coincident(g0,g-1)
    c: Distance(g0) = 6
    c: Vertical(g0)
    c: Coincident(g3,g0)
    c: Weight(g1) = 1
    c: Equal(g1,g2)
    c: InternalAlignment(g1,g3)
    c: InternalAlignment(g2,g3)
    c: InternalAlignment(g4,g3)
    c: InternalAlignment(g5,g3)
    c: Block(g3)
    c: Coincident(g6,g0)
    c: Coincident(g6,g3)
    c: Horizontal(g6)
FEATURE [Part::Extrusion] Extrude018  label="caseScrewPillarBracket006"
  Base = -> Sketch024
  Dir = (0,0,1)
  DirMode = 2
  FaceMakerClass = Part::FaceMakerBullseye
  LengthFwd = 2.4
  LengthRev = 0
  Placement = pos=(103.7,29,6.77) rot=(0,-1,0;1.5708rad)
  Solid = true
  Symmetric = false
FEATURE [Sketcher::SketchObject] Sketch025
  FullyConstrained = true
  sketch-geometry (7):
    g0: LineSegment StartX=0 StartY=0 StartZ=0 EndX=0 EndY=6 EndZ=0
    g1: Circle CenterX=0 CenterY=0 CenterZ=0 NormalX=0 NormalY=0 NormalZ=1 AngleXU=0 Radius=1
    g2: Circle CenterX=8 CenterY=6 CenterZ=0 NormalX=0 NormalY=0 NormalZ=1 AngleXU=0 Radius=1
    g3: BSplineCurve PolesCount=3 KnotsCount=2 Degree=2 IsPeriodic=0
    g4: GeomPoint X=0 Y=0 Z=0
    g5: GeomPoint X=8 Y=6 Z=0
    g6: LineSegment StartX=0 StartY=6 StartZ=0 EndX=8 EndY=6 EndZ=0
  constraints (14):
    c: Coincident(g0,g-1)
    c: Distance(g0) = 6
    c: Vertical(g0)
    c: Coincident(g3,g0)
    c: Weight(g1) = 1
    c: Equal(g1,g2)
    c: InternalAlignment(g1,g3)
    c: InternalAlignment(g2,g3)
    c: InternalAlignment(g4,g3)
    c: InternalAlignment(g5,g3)
    c: Block(g3)
    c: Coincident(g6,g0)
    c: Coincident(g6,g3)
    c: Horizontal(g6)
FEATURE [Part::Extrusion] Extrude019  label="caseScrewPillarBracket007"
  Base = -> Sketch025
  Dir = (0,0,1)
  DirMode = 2
  FaceMakerClass = Part::FaceMakerBullseye
  LengthFwd = 2.4
  LengthRev = 0
  Placement = pos=(101.3,29,65.23) rot=(0,1,0;1.5708rad)
  Solid = true
  Symmetric = false
FEATURE [Part::Box] Box011  label="frontCaseScrewPillarBracket"
  AttacherType = Attacher::AttachEngine3D
  Height = 2.4
  Length = 16
  Placement = pos=(87,28,2.3) rot=(0,0,1;0rad)
  Width = 7
FEATURE [Part::Box] Box012  label="frontCaseScrewPillarBracket001"
  AttacherType = Attacher::AttachEngine3D
  Height = 2.4
  Length = 16
  Placement = pos=(87,28,67.3) rot=(0,0,1;0rad)
  Width = 7
FEATURE [Sketcher::SketchObject] Sketch026
  FullyConstrained = true
  sketch-geometry (17):
    g0: Circle CenterX=-3.5 CenterY=23.5 CenterZ=0 NormalX=0 NormalY=0 NormalZ=1 AngleXU=0 Radius=1
    g1: Circle CenterX=-1 CenterY=15.25 CenterZ=0 NormalX=0 NormalY=0 NormalZ=1 AngleXU=0 Radius=1
    g2: Circle CenterX=-3.5 CenterY=7 CenterZ=0 NormalX=0 NormalY=0 NormalZ=1 AngleXU=0 Radius=1
    g3: BSplineCurve PolesCount=3 KnotsCount=2 Degree=2 IsPeriodic=0
    g4: GeomPoint X=-3.5 Y=23.5 Z=0
    g5: GeomPoint X=-3.5 Y=7 Z=0
    g6: Circle CenterX=-4.8 CenterY=30.5 CenterZ=0 NormalX=0 NormalY=0 NormalZ=1 AngleXU=0 Radius=1
    g7: Circle CenterX=-3.5 CenterY=30.5 CenterZ=0 NormalX=0 NormalY=0 NormalZ=1 AngleXU=0 Radius=1
    g8: Circle CenterX=-3.5 CenterY=29.2 CenterZ=0 NormalX=0 NormalY=0 NormalZ=1 AngleXU=0 Radius=1
    g9: BSplineCurve PolesCount=3 KnotsCount=2 Degree=2 IsPeriodic=0
    g10: GeomPoint X=-4.8 Y=30.5 Z=0
    g11: GeomPoint X=-3.5 Y=29.2 Z=0
    g12: LineSegment StartX=-3.5 StartY=29.2 StartZ=0 EndX=-3.5 EndY=23.5 EndZ=0
    g13: LineSegment StartX=-4.8 StartY=30.5 StartZ=0 EndX=0 EndY=30.5 EndZ=0
    g14: LineSegment StartX=-3.5 StartY=5 StartZ=0 EndX=-3.5 EndY=7 EndZ=0
    g15: LineSegment StartX=0 StartY=5 StartZ=0 EndX=0 EndY=30.5 EndZ=0
    g16: LineSegment StartX=-3.5 StartY=5 StartZ=0 EndX=0 EndY=5 EndZ=0
  constraints (33):
    c: Weight(g0) = 1
    c: Equal(g0,g1)
    c: Equal(g0,g2)
    c: InternalAlignment(g0,g3)
    c: InternalAlignment(g1,g3)
    c: InternalAlignment(g2,g3)
    c: InternalAlignment(g4,g3)
    c: InternalAlignment(g5,g3)
    c: Block(g3)
    c: Weight(g6) = 1
    c: Equal(g6,g7)
    c: Equal(g6,g8)
    c: InternalAlignment(g6,g9)
    c: InternalAlignment(g7,g9)
    c: InternalAlignment(g8,g9)
    c: InternalAlignment(g10,g9)
    c: InternalAlignment(g11,g9)
    c: Block(g9)
    c: Coincident(g12,g9)
    c: Coincident(g12,g3)
    c: Vertical(g12)
    c: Coincident(g13,g9)
    c: Horizontal(g13)
    c: Distance(g13) = 4.8
    c: Coincident(g14,g3)
    c: Vertical(g14)
    c: Coincident(g15,g13)
    c: Vertical(g15)
    c: Tangent(g15,g1)
    c: Distance(g14) = 2
    c: Coincident(g16,g14)
    c: Horizontal(g16)
    c: Coincident(g15,g16)
FEATURE [Part::Feature] Face050
  shape: bbox 4.8 x 25.5 x 2e-07 mm, 1 faces, 0 solids (baked)
FEATURE [Part::Revolution] Revolve054  label="moreFrontCaseScrewPost001"
  Angle = 360
  Axis = (0,1,0)
  Base = (0,0,0)
  FaceMakerClass = Part::FaceMakerBullseye
  Placement = pos=(102.5,4.5,3.5) rot=(0,0,1;0rad)
  Solid = false
  Source = -> Face050
  Symmetric = false
FEATURE [Part::Feature] Face051
  shape: bbox 4.8 x 25.5 x 2e-07 mm, 1 faces, 0 solids (baked)
FEATURE [Part::Revolution] Revolve055  label="moreFrontCaseScrewPost002"
  Angle = 360
  Axis = (0,1,0)
  Base = (0,0,0)
  FaceMakerClass = Part::FaceMakerBullseye
  Placement = pos=(102.5,4.5,68.5) rot=(0,0,1;0rad)
  Solid = false
  Source = -> Face051
  Symmetric = false
FEATURE [Sketcher::SketchObject] Sketch027
  FullyConstrained = true
  sketch-geometry (10):
    g0: LineSegment StartX=-1.6 StartY=4.7 StartZ=0 EndX=-1.6 EndY=1.7 EndZ=0
    g1: LineSegment StartX=-3.5 StartY=4.7 StartZ=0 EndX=-1.6 EndY=4.7 EndZ=0
    g2: LineSegment StartX=-1.6 StartY=1.7 StartZ=0 EndX=-1.6 EndY=1.5 EndZ=0
    g3: LineSegment StartX=-1.6 StartY=1.5 StartZ=0 EndX=-5.2 EndY=1.5 EndZ=0
    g4: Circle CenterX=-3.5 CenterY=4.7 CenterZ=0 NormalX=0 NormalY=0 NormalZ=1 AngleXU=0 Radius=1
    g5: Circle CenterX=-3.59627 CenterY=2.99743 CenterZ=0 NormalX=0 NormalY=0 NormalZ=1 AngleXU=0 Radius=1
    g6: Circle CenterX=-5.2 CenterY=1.5 CenterZ=0 NormalX=0 NormalY=0 NormalZ=1 AngleXU=0 Radius=1
    g7: BSplineCurve PolesCount=3 KnotsCount=2 Degree=2 IsPeriodic=0
    g8: GeomPoint X=-3.5 Y=4.7 Z=0
    g9: GeomPoint X=-5.2 Y=1.5 Z=0
  constraints (23):
    c: Vertical(g0)
    c: Distance(g0) = 3
    c: Coincident(g1,g0)
    c: Horizontal(g1)
    c: Block(g0)
    c: Block(g1)
    c: Coincident(g2,g0)
    c: Vertical(g2)
    c: Distance(g2) = 0.2
    c: Coincident(g3,g2)
    c: Horizontal(g3)
    c: Block(g3)
    c: Coincident(g7,g1)
    c: Weight(g4) = 1
    c: Equal(g4,g5)
    c: Equal(g4,g6)
    c: Coincident(g7,g3)
    c: InternalAlignment(g4,g7)
    c: InternalAlignment(g5,g7)
    c: InternalAlignment(g6,g7)
    c: InternalAlignment(g8,g7)
    c: InternalAlignment(g9,g7)
    c: Block(g7)
FEATURE [Sketcher::SketchObject] Sketch028
  FullyConstrained = true
  sketch-geometry (18):
    g0: LineSegment StartX=0 StartY=3e-16 StartZ=0 EndX=0 EndY=1.7 EndZ=0
    g1: LineSegment StartX=-3.5 StartY=0 StartZ=0 EndX=-3.5 EndY=0.9 EndZ=0
    g2: Circle CenterX=-2.7 CenterY=1.7 CenterZ=0 NormalX=0 NormalY=0 NormalZ=1 AngleXU=0 Radius=1
    g3: Circle CenterX=-3.5 CenterY=1.7 CenterZ=0 NormalX=0 NormalY=0 NormalZ=1 AngleXU=0 Radius=1
    g4: Circle CenterX=-3.5 CenterY=0.9 CenterZ=0 NormalX=0 NormalY=0 NormalZ=1 AngleXU=0 Radius=1
    g5: BSplineCurve PolesCount=3 KnotsCount=2 Degree=2 IsPeriodic=0
    g6: GeomPoint X=-2.7 Y=1.7 Z=0
    g7: GeomPoint X=-3.5 Y=0.9 Z=0
    g8: LineSegment StartX=-3.5 StartY=0 StartZ=0 EndX=-3.5 EndY=-7 EndZ=0
    g9: LineSegment StartX=0 StartY=3e-16 StartZ=0 EndX=0 EndY=-7 EndZ=0
    g10: LineSegment StartX=-3.5 StartY=-7 StartZ=0 EndX=0 EndY=-7 EndZ=0
    g11: LineSegment StartX=-2.7 StartY=1.7 StartZ=0 EndX=-1.6 EndY=1.7 EndZ=0
    g12: LineSegment StartX=0 StartY=1.7 StartZ=0 EndX=0 EndY=4.5 EndZ=0
    g13: LineSegment StartX=0 StartY=4.5 StartZ=0 EndX=0 EndY=10.8 EndZ=0
    g14: LineSegment StartX=0 StartY=10.8 StartZ=0 EndX=-2 EndY=10.8 EndZ=0
    g15: LineSegment StartX=-1.6 StartY=4.7 StartZ=0 EndX=-1.6 EndY=1.7 EndZ=0
    g16: LineSegment StartX=-1.6 StartY=4.7 StartZ=0 EndX=-2 EndY=4.7 EndZ=0
    g17: LineSegment StartX=-2 StartY=4.7 StartZ=0 EndX=-2 EndY=10.8 EndZ=0
  constraints (44):
    c: Vertical(g0)
    c: Vertical(g1)
    c: Distance(g1) = 0.9
    c: Block(g0)
    c: Distance(g0) = 1.7
    c: Weight(g2) = 1
    c: Equal(g2,g3)
    c: Equal(g2,g4)
    c: Coincident(g5,g1)
    c: InternalAlignment(g2,g5)
    c: InternalAlignment(g3,g5)
    c: InternalAlignment(g4,g5)
    c: InternalAlignment(g6,g5)
    c: InternalAlignment(g7,g5)
    c: Block(g5)
    c: Coincident(g8,g1)
    c: Vertical(g8)
    c: Distance(g8) = 7
    c: Vertical(g9)
    c: Equal(g8,g9) = 7
    c: Coincident(g9,g0)
    c: Coincident(g10,g8)
    c: Coincident(g10,g9)
    c: Horizontal(g10)
    c: Coincident(g11,g5)
    c: Horizontal(g11)
    c: Coincident(g12,g0)
    c: Vertical(g12)
    c: Distance(g12) = 2.8
    c: Coincident(g13,g12)
    c: Vertical(g13)
    c: Distance(g13) = 6.3
    c: Coincident(g14,g13)
    c: Horizontal(g14)
    c: Distance(g14) = 2
    c: Vertical(g15)
    c: Distance(g15) = 3
    c: Block(g11)
    c: Coincident(g15,g11)
    c: Coincident(g16,g15)
    c: Horizontal(g16)
    c: Coincident(g17,g16)
    c: Coincident(g17,g14)
    c: Vertical(g17)
FEATURE [Part::Revolution] Revolve040  label="backCaseScrewRetainer001"
  Angle = 360
  Axis = (0,1,0)
  Base = (0,0,0)
  FaceMakerClass = Part::FaceMakerBullseye
  Placement = pos=(12.5,3,10) rot=(0,0,1;0rad)
  Solid = false
  Source = -> Face036
  Symmetric = false
FEATURE [Part::Feature] Face055
  shape: bbox 3.5 x 30.2 x 2e-07 mm, 1 faces, 0 solids (baked)
FEATURE [Part::Revolution] Revolve059  label="backCaseScrewPost"
  Angle = 360
  Axis = (0,1,0)
  Base = (0,0,0)
  FaceMakerClass = Part::FaceMakerBullseye
  Placement = pos=(12.5,4.5,10) rot=(0,0,1;0rad)
  Solid = false
  Source = -> Face055
  Symmetric = false
FEATURE [Part::Feature] Face056
  shape: bbox 3.5 x 30.2 x 2e-07 mm, 1 faces, 0 solids (baked)
FEATURE [Part::Revolution] Revolve060  label="backCaseScrewPost001"
  Angle = 360
  Axis = (0,1,0)
  Base = (0,0,0)
  FaceMakerClass = Part::FaceMakerBullseye
  Placement = pos=(12.5,4.5,62) rot=(0,0,1;0rad)
  Solid = false
  Source = -> Face056
  Symmetric = false
FEATURE [Part::Feature] Face057
  shape: bbox 3.5 x 17.8 x 2e-07 mm, 1 faces, 0 solids (baked)
FEATURE [Part::Revolution] Revolve061  label="removeToCreateScrewAndThreadedInsertHole"
  Angle = 360
  Axis = (0,1,0)
  Base = (0,0,0)
  FaceMakerClass = Part::FaceMakerBullseye
  Placement = pos=(12.5,0,10) rot=(0,0,1;0rad)
  Solid = false
  Source = -> Face057
  Symmetric = false
FEATURE [Part::Feature] Face058
  shape: bbox 3.5 x 17.8 x 2e-07 mm, 1 faces, 0 solids (baked)
FEATURE [Part::Revolution] Revolve062  label="removeToCreateScrewAndThreadedInsertHole001"
  Angle = 360
  Axis = (0,1,0)
  Base = (0,0,0)
  FaceMakerClass = Part::FaceMakerBullseye
  Placement = pos=(12.5,0,62) rot=(0,0,1;0rad)
  Solid = false
  Source = -> Face058
  Symmetric = false
FEATURE [Part::Feature] Face059
  shape: bbox 3.5 x 17.8 x 2e-07 mm, 1 faces, 0 solids (baked)
FEATURE [Part::Revolution] Revolve063  label="removeToCreateScrewAndThreadedInsertHole002"
  Angle = 360
  Axis = (0,1,0)
  Base = (0,0,0)
  FaceMakerClass = Part::FaceMakerBullseye
  Placement = pos=(89.5,0,68.5) rot=(0,0,1;0rad)
  Solid = false
  Source = -> Face059
  Symmetric = false
FEATURE [Part::Feature] Face060
  shape: bbox 3.5 x 17.8 x 2e-07 mm, 1 faces, 0 solids (baked)
FEATURE [Part::Revolution] Revolve064  label="removeToCreateScrewAndThreadedInsertHole003"
  Angle = 360
  Axis = (0,1,0)
  Base = (0,0,0)
  FaceMakerClass = Part::FaceMakerBullseye
  Placement = pos=(89.5,0,3.5) rot=(0,0,1;0rad)
  Solid = false
  Source = -> Face060
  Symmetric = false
FEATURE [Part::Feature] Face061
  shape: bbox 3.5 x 17.8 x 2e-07 mm, 1 faces, 0 solids (baked)
FEATURE [Part::Revolution] Revolve065  label="removeToCreateScrewAndThreadedInsertHole004"
  Angle = 360
  Axis = (0,1,0)
  Base = (0,0,0)
  FaceMakerClass = Part::FaceMakerBullseye
  Placement = pos=(102.5,4.7,3.5) rot=(0,0,1;0rad)
  Solid = false
  Source = -> Face061
  Symmetric = false
FEATURE [Part::Feature] Face062
  shape: bbox 3.5 x 17.8 x 2e-07 mm, 1 faces, 0 solids (baked)
FEATURE [Part::Revolution] Revolve066  label="removeToCreateScrewAndThreadedInsertHole005"
  Angle = 360
  Axis = (0,1,0)
  Base = (0,0,0)
  FaceMakerClass = Part::FaceMakerBullseye
  Placement = pos=(102.5,4.7,68.5) rot=(0,0,1;0rad)
  Solid = false
  Source = -> Face062
  Symmetric = false
FEATURE [Part::MultiFuse] Fusion047  label="makeHoles"
  Shapes = -> [Revolve066,Revolve065,Revolve064,Revolve063,Revolve062,Revolve061]
FEATURE [Part::Feature] Face063
  shape: bbox 3.6 x 3.2 x 2e-07 mm, 1 faces, 0 solids (baked)
FEATURE [Part::Revolution] Revolve067  label="moreFrontCaseScrewRetainer002"
  Angle = 360
  Axis = (0,1,0)
  Base = (0,0,0)
  FaceMakerClass = Part::FaceMakerBullseye
  Placement = pos=(102.5,4.5,68.5) rot=(0,0,1;0rad)
  Solid = false
  Source = -> Face063
  Symmetric = false
FEATURE [Part::Feature] Face064
  shape: bbox 3.6 x 3.2 x 2e-07 mm, 1 faces, 0 solids (baked)
FEATURE [Part::Revolution] Revolve068  label="moreFrontCaseScrewRetainer003"
  Angle = 360
  Axis = (0,1,0)
  Base = (0,0,0)
  FaceMakerClass = Part::FaceMakerBullseye
  Placement = pos=(102.5,4.5,3.5) rot=(0,0,1;0rad)
  Solid = false
  Source = -> Face064
  Symmetric = false
FEATURE [Part::Feature] Face065
  shape: bbox 3.5 x 17.8 x 2e-07 mm, 1 faces, 0 solids (baked)
FEATURE [Part::Revolution] Revolve069  label="removeToCreateScrewAndThreadedInsertHole006"
  Angle = 360
  Axis = (0,1,0)
  Base = (0,0,0)
  FaceMakerClass = Part::FaceMakerBullseye
  Placement = pos=(12.5,0,10) rot=(0,0,1;0rad)
  Solid = false
  Source = -> Face065
  Symmetric = false
FEATURE [Part::Feature] Face066
  shape: bbox 3.5 x 17.8 x 2e-07 mm, 1 faces, 0 solids (baked)
FEATURE [Part::Revolution] Revolve070  label="removeToCreateScrewAndThreadedInsertHole007"
  Angle = 360
  Axis = (0,1,0)
  Base = (0,0,0)
  FaceMakerClass = Part::FaceMakerBullseye
  Placement = pos=(12.5,0,62) rot=(0,0,1;0rad)
  Solid = false
  Source = -> Face066
  Symmetric = false
FEATURE [Part::Feature] Face067
  shape: bbox 3.5 x 17.8 x 2e-07 mm, 1 faces, 0 solids (baked)
FEATURE [Part::Revolution] Revolve071  label="removeToCreateScrewAndThreadedInsertHole008"
  Angle = 360
  Axis = (0,1,0)
  Base = (0,0,0)
  FaceMakerClass = Part::FaceMakerBullseye
  Placement = pos=(89.5,0,68.5) rot=(0,0,1;0rad)
  Solid = false
  Source = -> Face067
  Symmetric = false
FEATURE [Part::Feature] Face068
  shape: bbox 3.5 x 17.8 x 2e-07 mm, 1 faces, 0 solids (baked)
FEATURE [Part::Revolution] Revolve072  label="removeToCreateScrewAndThreadedInsertHole009"
  Angle = 360
  Axis = (0,1,0)
  Base = (0,0,0)
  FaceMakerClass = Part::FaceMakerBullseye
  Placement = pos=(89.5,0,3.5) rot=(0,0,1;0rad)
  Solid = false
  Source = -> Face068
  Symmetric = false
FEATURE [Part::Feature] Face069
  shape: bbox 3.5 x 17.8 x 2e-07 mm, 1 faces, 0 solids (baked)
FEATURE [Part::Feature] Face070
  shape: bbox 3.5 x 17.8 x 2e-07 mm, 1 faces, 0 solids (baked)
FEATURE [Part::Revolution] Revolve073  label="removeToCreateScrewAndThreadedInsertHole010"
  Angle = 360
  Axis = (0,1,0)
  Base = (0,0,0)
  FaceMakerClass = Part::FaceMakerBullseye
  Placement = pos=(102.5,4.7,3.5) rot=(0,0,1;0rad)
  Solid = false
  Source = -> Face069
  Symmetric = false
FEATURE [Part::Revolution] Revolve074  label="removeToCreateScrewAndThreadedInsertHole011"
  Angle = 360
  Axis = (0,1,0)
  Base = (0,0,0)
  FaceMakerClass = Part::FaceMakerBullseye
  Placement = pos=(102.5,4.7,68.5) rot=(0,0,1;0rad)
  Solid = false
  Source = -> Face070
  Symmetric = false
FEATURE [Part::MultiFuse] Fusion048  label="makeHoles001"
  Shapes = -> [Revolve074,Revolve073,Revolve072,Revolve071,Revolve070,Revolve069]
FEATURE [Part::MultiFuse] Fusion049  label="caseScrewRetainers"
  Shapes = -> [Revolve067,Revolve068,Revolve048,Revolve047,Revolve039,Revolve040]
FEATURE [Part::Cut] Cut015  label="caseScrewRetainers001"
  Base = -> Fusion049
  Tool = -> Fusion048
FEATURE [Part::MultiFuse] Fusion050  label="casePillars"
  Shapes = -> [Revolve055,Revolve054,Revolve043,Revolve046,Revolve059,Revolve060]
FEATURE [Part::Feature] Face071 .. Face076  x6 (patterned run collapsed; names and placements below)
  shape: bbox 3.5 x 17.8 x 2e-07 mm, 1 faces, 0 solids (baked)
FEATURE [Part::Revolution] Revolve075  label="removeToCreateScrewAndThreadedInsertHole012"
  Angle = 360
  Axis = (0,1,0)
  Base = (0,0,0)
  FaceMakerClass = Part::FaceMakerBullseye
  Placement = pos=(12.5,0,10) rot=(0,0,1;0rad)
  Solid = false
  Source = -> Face071
  Symmetric = false
FEATURE [Part::Revolution] Revolve076  label="removeToCreateScrewAndThreadedInsertHole013"
  Angle = 360
  Axis = (0,1,0)
  Base = (0,0,0)
  FaceMakerClass = Part::FaceMakerBullseye
  Placement = pos=(12.5,0,62) rot=(0,0,1;0rad)
  Solid = false
  Source = -> Face072
  Symmetric = false
FEATURE [Part::Revolution] Revolve077  label="removeToCreateScrewAndThreadedInsertHole014"
  Angle = 360
  Axis = (0,1,0)
  Base = (0,0,0)
  FaceMakerClass = Part::FaceMakerBullseye
  Placement = pos=(89.5,0,68.5) rot=(0,0,1;0rad)
  Solid = false
  Source = -> Face073
  Symmetric = false
FEATURE [Part::Revolution] Revolve078  label="removeToCreateScrewAndThreadedInsertHole015"
  Angle = 360
  Axis = (0,1,0)
  Base = (0,0,0)
  FaceMakerClass = Part::FaceMakerBullseye
  Placement = pos=(89.5,0,3.5) rot=(0,0,1;0rad)
  Solid = false
  Source = -> Face074
  Symmetric = false
FEATURE [Part::Revolution] Revolve079  label="removeToCreateScrewAndThreadedInsertHole016"
  Angle = 360
  Axis = (0,1,0)
  Base = (0,0,0)
  FaceMakerClass = Part::FaceMakerBullseye
  Placement = pos=(102.5,4.7,3.5) rot=(0,0,1;0rad)
  Solid = false
  Source = -> Face075
  Symmetric = false
FEATURE [Part::Revolution] Revolve080  label="removeToCreateScrewAndThreadedInsertHole017"
  Angle = 360
  Axis = (0,1,0)
  Base = (0,0,0)
  FaceMakerClass = Part::FaceMakerBullseye
  Placement = pos=(102.5,4.7,68.5) rot=(0,0,1;0rad)
  Solid = false
  Source = -> Face076
  Symmetric = false
FEATURE [Part::MultiFuse] Fusion051  label="makeHoles002"
  Shapes = -> [Revolve080,Revolve079,Revolve078,Revolve077,Revolve076,Revolve075]
FEATURE [Part::Cut] Cut016  label="caesPillars"
  Base = -> Fusion050
  Tool = -> Fusion051
FEATURE [Part::Revolution] Revolve009  label="plugHousing016"
  Angle = 360
  Axis = (0,1,0)
  Base = (0,0,0)
  FaceMakerClass = Part::FaceMakerBullseye
  Placement = pos=(0,0,36.15) rot=(0,0,1;0rad)
  Solid = false
  Source = -> Face012
  Symmetric = false
FEATURE [Part::MultiFuse] Fusion014  label="plugHousing023"
  Placement = pos=(0,0,0) rot=(0,0,1;1.5708rad)
  Shapes = -> [Revolve011,Revolve009]
FEATURE [Part::Revolution] Revolve010  label="plugHousing017"
  Angle = 360
  Axis = (0,1,0)
  Base = (0,0,0)
  FaceMakerClass = Part::FaceMakerBullseye
  Placement = pos=(0,0,36.15) rot=(0,0,1;0rad)
  Solid = false
  Source = -> Face014
  Symmetric = false
FEATURE [Part::MultiFuse] Fusion015  label="plugHousing024"
  Placement = pos=(0,0,0) rot=(0,0,1;1.5708rad)
  Shapes = -> [Revolve010,Revolve015]
FEATURE [Part::Revolution] Revolve014  label="plugHousing026"
  Angle = 360
  Axis = (0,1,0)
  Base = (0,0,0)
  FaceMakerClass = Part::FaceMakerBullseye
  Placement = pos=(0,0,36.15) rot=(0,0,1;0rad)
  Solid = false
  Source = -> Face011
  Symmetric = false
FEATURE [Part::Revolution] Revolve013  label="plugHousing025"
  Angle = 360
  Axis = (0,1,0)
  Base = (0,0,0)
  FaceMakerClass = Part::FaceMakerBullseye
  Placement = pos=(0,0,36.15) rot=(0,0,1;0rad)
  Solid = false
  Source = -> Face015
  Symmetric = false
FEATURE [Part::MultiFuse] Fusion016  label="plugHousing028"
  Placement = pos=(0,19,0) rot=(0,0,1;3.14159rad)
  Shapes = -> [Fusion014,Fusion013]
FEATURE [Part::MultiFuse] Fusion011  label="plugHousing018"
  Placement = pos=(0,0,0) rot=(0,0,1;1.5708rad)
  Shapes = -> [Revolve014,Revolve013]
FEATURE [Part::MultiFuse] Fusion012  label="plugHousing019"
  Placement = pos=(0,19,0) rot=(0,0,1;3.14159rad)
  Shapes = -> [Fusion011,Fusion015]
FEATURE [Part::MultiFuse] Fusion017  label="plugHousing029"
  Placement = pos=(122.621,0,-0.15) rot=(0,0,1;0rad)
  Shapes = -> [Fusion016,Fusion012]
FEATURE [Part::MultiFuse] Fusion052  label="casePillarRetainers"
  Shapes = -> [Extrude012,Extrude013,Extrude014,Extrude015,Extrude016,Extrude017,Extrude018,Extrude019,Box011,Box012]
FEATURE [Part::Feature] Face077
  shape: bbox 3.5 x 17.8 x 2e-07 mm, 1 faces, 0 solids (baked)
FEATURE [Part::Revolution] Revolve081  label="removeToCreateScrewAndThreadedInsertHole018"
  Angle = 360
  Axis = (0,1,0)
  Base = (0,0,0)
  FaceMakerClass = Part::FaceMakerBullseye
  Placement = pos=(62.3,30.3,19.7) rot=(0,0,1;0rad)
  Solid = false
  Source = -> Face077
  Symmetric = false
FEATURE [Part::Feature] Face078
  shape: bbox 3.5 x 17.8 x 2e-07 mm, 1 faces, 0 solids (baked)
FEATURE [Part::Revolution] Revolve082  label="removeToCreateScrewAndThreadedInsertHole019"
  Angle = 360
  Axis = (0,1,0)
  Base = (0,0,0)
  FaceMakerClass = Part::FaceMakerBullseye
  Placement = pos=(62.3,30.3,51.7) rot=(0,0,1;0rad)
  Solid = false
  Source = -> Face078
  Symmetric = false
FEATURE [Part::Feature] Face079
  shape: bbox 3.5 x 17.8 x 2e-07 mm, 1 faces, 0 solids (baked)
FEATURE [Part::Revolution] Revolve083  label="removeToCreateScrewAndThreadedInsertHole020"
  Angle = 360
  Axis = (0,1,0)
  Base = (0,0,0)
  FaceMakerClass = Part::FaceMakerBullseye
  Placement = pos=(30.3,30.3,19.7) rot=(0,0,1;0rad)
  Solid = false
  Source = -> Face079
  Symmetric = false
FEATURE [Part::Feature] Face080
  shape: bbox 3.5 x 17.8 x 2e-07 mm, 1 faces, 0 solids (baked)
FEATURE [Part::Revolution] Revolve084  label="removeToCreateScrewAndThreadedInsertHole021"
  Angle = 360
  Axis = (0,1,0)
  Base = (0,0,0)
  FaceMakerClass = Part::FaceMakerBullseye
  Placement = pos=(30.3,30.3,51.7) rot=(0,0,1;0rad)
  Solid = false
  Source = -> Face080
  Symmetric = false
FEATURE [Part::MultiFuse] Fusion053  label="createThreadedInsertHolesForFan"
  Shapes = -> [Revolve081,Revolve082,Revolve083,Revolve084]
FEATURE [Part::Cut] Cut017  label="fanScrewHousing001"
  Base = -> Fusion046
  Tool = -> Fusion053
FEATURE [Part::Feature] Face081
  shape: bbox 3.5 x 17.8 x 2e-07 mm, 1 faces, 0 solids (baked)
FEATURE [Part::Revolution] Revolve085  label="removeToCreateScrewAndThreadedInsertHole022"
  Angle = 360
  Axis = (0,1,0)
  Base = (0,0,0)
  FaceMakerClass = Part::FaceMakerBullseye
  Placement = pos=(62.3,30.3,19.7) rot=(0,0,1;0rad)
  Solid = false
  Source = -> Face081
  Symmetric = false
FEATURE [Part::Feature] Face082
  shape: bbox 3.5 x 17.8 x 2e-07 mm, 1 faces, 0 solids (baked)
FEATURE [Part::Revolution] Revolve086  label="removeToCreateScrewAndThreadedInsertHole023"
  Angle = 360
  Axis = (0,1,0)
  Base = (0,0,0)
  FaceMakerClass = Part::FaceMakerBullseye
  Placement = pos=(62.3,30.3,51.7) rot=(0,0,1;0rad)
  Solid = false
  Source = -> Face082
  Symmetric = false
FEATURE [Part::Feature] Face083
  shape: bbox 3.5 x 17.8 x 2e-07 mm, 1 faces, 0 solids (baked)
FEATURE [Part::Revolution] Revolve087  label="removeToCreateScrewAndThreadedInsertHole024"
  Angle = 360
  Axis = (0,1,0)
  Base = (0,0,0)
  FaceMakerClass = Part::FaceMakerBullseye
  Placement = pos=(30.3,30.3,19.7) rot=(0,0,1;0rad)
  Solid = false
  Source = -> Face083
  Symmetric = false
FEATURE [Part::Feature] Face084
  shape: bbox 3.5 x 17.8 x 2e-07 mm, 1 faces, 0 solids (baked)
FEATURE [Part::Revolution] Revolve088  label="removeToCreateScrewAndThreadedInsertHole025"
  Angle = 360
  Axis = (0,1,0)
  Base = (0,0,0)
  FaceMakerClass = Part::FaceMakerBullseye
  Placement = pos=(30.3,30.3,51.7) rot=(0,0,1;0rad)
  Solid = false
  Source = -> Face084
  Symmetric = false
FEATURE [Part::MultiFuse] Fusion054  label="createThreadedInsertHolesForFan001"
  Shapes = -> [Revolve085,Revolve086,Revolve087,Revolve088]
FEATURE [Part::Cut] Cut018  label="top007"
  Base = -> Fusion040
  Tool = -> Fusion054
FEATURE [Sketcher::SketchObject] Sketch029
  FullyConstrained = false
  Placement = pos=(0,0,0) rot=(1,0,0;1.5708rad)
  sketch-geometry (24):
    g0: ArcOfCircle CenterX=-4 CenterY=-10.5 CenterZ=0 NormalX=0 NormalY=0 NormalZ=1 AngleXU=0 Radius=1.5 StartAngle=6e-16 EndAngle=3.14159
    g1: ArcOfCircle CenterX=-34.2 CenterY=-10.5 CenterZ=0 NormalX=0 NormalY=0 NormalZ=1 AngleXU=0 Radius=1.5 StartAngle=0 EndAngle=3.14159
    g2: ArcOfCircle CenterX=-34.2 CenterY=-27.7 CenterZ=0 NormalX=0 NormalY=0 NormalZ=1 AngleXU=0 Radius=1.5 StartAngle=3.14159 EndAngle=6.28319
    g3: ArcOfCircle CenterX=-4 CenterY=-27.7 CenterZ=0 NormalX=0 NormalY=0 NormalZ=1 AngleXU=0 Radius=1.5 StartAngle=3.1416 EndAngle=6.28319
    g4: ArcOfCircle CenterX=-10 CenterY=-4.3 CenterZ=0 NormalX=0 NormalY=0 NormalZ=1 AngleXU=0 Radius=1.5 StartAngle=2e-16 EndAngle=3.14159
    g5: ArcOfCircle CenterX=-16.1 CenterY=-1.8 CenterZ=0 NormalX=0 NormalY=0 NormalZ=1 AngleXU=0 Radius=1.5 StartAngle=5e-16 EndAngle=3.14159
    g6: ArcOfCircle CenterX=-22.1 CenterY=-1.8 CenterZ=0 NormalX=0 NormalY=0 NormalZ=1 AngleXU=0 Radius=1.5 StartAngle=5e-16 EndAngle=3.14159
    g7: ArcOfCircle CenterX=-28.2 CenterY=-4.3 CenterZ=0 NormalX=0 NormalY=0 NormalZ=1 AngleXU=0 Radius=1.5 StartAngle=2e-16 EndAngle=3.14159
    g8: ArcOfCircle CenterX=-10 CenterY=-33.9 CenterZ=0 NormalX=0 NormalY=0 NormalZ=1 AngleXU=0 Radius=1.5 StartAngle=3.14159 EndAngle=6.28319
    g9: ArcOfCircle CenterX=-16.1 CenterY=-36.4 CenterZ=0 NormalX=0 NormalY=0 NormalZ=1 AngleXU=0 Radius=1.5 StartAngle=3.14159 EndAngle=6.28319
    g10: ArcOfCircle CenterX=-22.1 CenterY=-36.4 CenterZ=0 NormalX=0 NormalY=0 NormalZ=1 AngleXU=0 Radius=1.5 StartAngle=3.14159 EndAngle=6.28319
    g11: ArcOfCircle CenterX=-28.2 CenterY=-33.9 CenterZ=0 NormalX=0 NormalY=0 NormalZ=1 AngleXU=0 Radius=1.5 StartAngle=3.14159 EndAngle=6.28319
    g12: LineSegment StartX=-35.7 StartY=-10.5 StartZ=0 EndX=-35.7 EndY=-27.7 EndZ=0
    g13: LineSegment StartX=-32.7 StartY=-10.5 StartZ=0 EndX=-32.7 EndY=-27.7 EndZ=0
    g14: LineSegment StartX=-29.7 StartY=-33.9 StartZ=0 EndX=-29.7 EndY=-4.3 EndZ=0
    g15: LineSegment StartX=-26.7 StartY=-33.9 StartZ=0 EndX=-26.7 EndY=-4.3 EndZ=0
    g16: LineSegment StartX=-2.5 StartY=-10.5 StartZ=0 EndX=-2.5 EndY=-27.7 EndZ=0
    g17: LineSegment StartX=-8.5 StartY=-4.3 StartZ=0 EndX=-8.5 EndY=-33.9 EndZ=0
    g18: LineSegment StartX=-5.5 StartY=-10.5 StartZ=0 EndX=-5.5 EndY=-27.7 EndZ=0
    g19: LineSegment StartX=-11.5 StartY=-4.3 StartZ=0 EndX=-11.5 EndY=-33.9 EndZ=0
    g20: LineSegment StartX=-14.6 StartY=-1.8 StartZ=0 EndX=-14.6 EndY=-36.4 EndZ=0
    g21: LineSegment StartX=-17.6 StartY=-1.8 StartZ=0 EndX=-17.6 EndY=-36.4 EndZ=0
    g22: LineSegment StartX=-20.6 StartY=-36.4 StartZ=0 EndX=-20.6 EndY=-1.8 EndZ=0
    g23: LineSegment StartX=-23.6 StartY=-1.8 StartZ=0 EndX=-23.6 EndY=-36.4 EndZ=0
  constraints (48):
    c: Block(g0)
    c: Block(g1)
    c: Block(g2)
    c: Block(g3)
    c: Block(g4)
    c: Block(g5)
    c: Block(g6)
    c: Block(g7)
    c: Block(g8)
    c: Block(g9)
    c: Block(g10)
    c: Block(g11)
    c: Coincident(g12,g1)
    c: Coincident(g12,g2)
    c: Vertical(g12)
    c: Coincident(g13,g1)
    c: Coincident(g13,g2)
    c: Vertical(g13)
    c: Coincident(g14,g11)
    c: Coincident(g14,g7)
    c: Vertical(g14)
    c: Coincident(g15,g11)
    c: Coincident(g15,g7)
    c: Vertical(g15)
    c: Coincident(g16,g0)
    c: Coincident(g16,g3)
    c: Vertical(g16)
    c: Coincident(g17,g4)
    c: Coincident(g17,g8)
    c: Vertical(g17)
    c: Coincident(g18,g0)
    c: Coincident(g18,g3)
    c: Vertical(g18)
    c: Coincident(g19,g4)
    c: Coincident(g19,g8)
    c: Vertical(g19)
    c: Coincident(g20,g5)
    c: Coincident(g20,g9)
    c: Vertical(g20)
    c: Coincident(g21,g5)
    c: Coincident(g21,g9)
    c: Vertical(g21)
    c: Coincident(g22,g10)
    c: Coincident(g22,g6)
    c: Vertical(g22)
    c: Coincident(g23,g6)
    c: Coincident(g23,g10)
    c: Vertical(g23)
FEATURE [Part::Extrusion] Extrude020  label="removeToCreateFanGrillHoles"
  Base = -> Sketch029
  Dir = (0,-1,6e-16)
  DirMode = 2
  FaceMakerClass = Part::FaceMakerBullseye
  LengthFwd = 10
  LengthRev = 0
  Placement = pos=(65.4,44,54.82) rot=(0,0,1;0rad)
  Solid = true
  Symmetric = false
FEATURE [Part::MultiFuse] Fusion055  label="top008"
  Shapes = -> [Cut017,Cut018]
FEATURE [Part::Cut] Cut019  label="top009"
  Base = -> Fusion055
  Tool = -> Extrude020
FEATURE [App::MeasureDistance] Distance003  label="Distance: 71.95 mm"
  Distance = 71.9513
  P1 = (117,38,72)
  P2 = (117,38,0.0487319)
FEATURE [Sketcher::SketchObject] Sketch030
  FullyConstrained = true
  Placement = pos=(117,19,0) rot=(0.57735,0.57735,0.57735;2.0944rad)
  sketch-geometry (48):
    g0: LineSegment StartX=-49.19 StartY=69.25 StartZ=0 EndX=-49.19 EndY=66.25 EndZ=0
    g1: LineSegment StartX=-49.19 StartY=63.5 StartZ=0 EndX=-49.19 EndY=60.5 EndZ=0
    g2: LineSegment StartX=-49.19 StartY=57.75 StartZ=0 EndX=-49.19 EndY=54.75 EndZ=0
    g3: LineSegment StartX=-49.19 StartY=52 StartZ=0 EndX=-49.19 EndY=49 EndZ=0
    g4: LineSegment StartX=-49.19 StartY=46.25 StartZ=0 EndX=-49.19 EndY=43.25 EndZ=0
    g5: LineSegment StartX=-49.19 StartY=40.5 StartZ=0 EndX=-49.19 EndY=37.5 EndZ=0
    g6: LineSegment StartX=-49.19 StartY=34.5 StartZ=0 EndX=-49.19 EndY=31.5 EndZ=0
    g7: LineSegment StartX=-49.19 StartY=28.75 StartZ=0 EndX=-49.19 EndY=25.75 EndZ=0
    g8: LineSegment StartX=-49.19 StartY=23 StartZ=0 EndX=-49.19 EndY=20 EndZ=0
    g9: LineSegment StartX=-49.19 StartY=17.25 StartZ=0 EndX=-49.19 EndY=14.25 EndZ=0
    g10: LineSegment StartX=-49.19 StartY=11.5 StartZ=0 EndX=-49.19 EndY=8.5 EndZ=0
    g11: LineSegment StartX=-49.19 StartY=5.75 StartZ=0 EndX=-49.19 EndY=2.75 EndZ=0
    g12: ArcOfCircle CenterX=-1.5 CenterY=67.75 CenterZ=0 NormalX=0 NormalY=0 NormalZ=1 AngleXU=0 Radius=1.5 StartAngle=4.71239 EndAngle=7.85398
    g13: ArcOfCircle CenterX=-1.5 CenterY=62 CenterZ=0 NormalX=0 NormalY=0 NormalZ=1 AngleXU=0 Radius=1.5 StartAngle=4.71239 EndAngle=7.85398
    g14: ArcOfCircle CenterX=-1.5 CenterY=56.25 CenterZ=0 NormalX=0 NormalY=0 NormalZ=1 AngleXU=0 Radius=1.5 StartAngle=4.71239 EndAngle=7.85398
    g15: ArcOfCircle CenterX=-11.49 CenterY=50.5 CenterZ=0 NormalX=0 NormalY=0 NormalZ=1 AngleXU=0 Radius=1.5 StartAngle=4.71239 EndAngle=7.85398
    g16: ArcOfCircle CenterX=-16.28 CenterY=44.75 CenterZ=0 NormalX=0 NormalY=0 NormalZ=1 AngleXU=0 Radius=1.5 StartAngle=4.71239 EndAngle=7.85398
    g17: ArcOfCircle CenterX=-18.2337 CenterY=39 CenterZ=0 NormalX=0 NormalY=0 NormalZ=1 AngleXU=0 Radius=1.5 StartAngle=4.71485 EndAngle=7.85398
    g18: ArcOfCircle CenterX=-16.2837 CenterY=27.25 CenterZ=0 NormalX=0 NormalY=0 NormalZ=1 AngleXU=0 Radius=1.5 StartAngle=4.71485 EndAngle=7.85398
    g19: ArcOfCircle CenterX=-18.2337 CenterY=33 CenterZ=0 NormalX=0 NormalY=0 NormalZ=1 AngleXU=0 Radius=1.5 StartAngle=4.71485 EndAngle=7.85398
    g20: ArcOfCircle CenterX=-11.49 CenterY=21.5 CenterZ=0 NormalX=0 NormalY=0 NormalZ=1 AngleXU=0 Radius=1.5 StartAngle=4.71239 EndAngle=7.85398
    g21: ArcOfCircle CenterX=-1.5 CenterY=4.25 CenterZ=0 NormalX=0 NormalY=0 NormalZ=1 AngleXU=0 Radius=1.5 StartAngle=4.71239 EndAngle=7.85398
    g22: ArcOfCircle CenterX=-1.5 CenterY=10 CenterZ=0 NormalX=0 NormalY=0 NormalZ=1 AngleXU=0 Radius=1.5 StartAngle=4.71239 EndAngle=7.85398
    g23: ArcOfCircle CenterX=-1.5 CenterY=15.75 CenterZ=0 NormalX=0 NormalY=0 NormalZ=1 AngleXU=0 Radius=1.5 StartAngle=4.71239 EndAngle=7.85398
    g24: LineSegment StartX=-49.19 StartY=69.25 StartZ=0 EndX=-1.5 EndY=69.25 EndZ=0
    g25: LineSegment StartX=-49.19 StartY=66.25 StartZ=0 EndX=-1.5 EndY=66.25 EndZ=0
    g26: LineSegment StartX=-49.19 StartY=63.5 StartZ=0 EndX=-1.5 EndY=63.5 EndZ=0
    g27: LineSegment StartX=-49.19 StartY=60.5 StartZ=0 EndX=-1.5 EndY=60.5 EndZ=0
    g28: LineSegment StartX=-49.19 StartY=57.75 StartZ=0 EndX=-1.5 EndY=57.75 EndZ=0
    g29: LineSegment StartX=-49.19 StartY=54.75 StartZ=0 EndX=-1.5 EndY=54.75 EndZ=0
    g30: LineSegment StartX=-49.19 StartY=52 StartZ=0 EndX=-11.49 EndY=52 EndZ=0
    g31: LineSegment StartX=-49.19 StartY=49 StartZ=0 EndX=-11.49 EndY=49 EndZ=0
    g32: LineSegment StartX=-49.19 StartY=46.25 StartZ=0 EndX=-16.28 EndY=46.25 EndZ=0
    g33: LineSegment StartX=-49.19 StartY=43.25 StartZ=0 EndX=-16.28 EndY=43.25 EndZ=0
    g34: LineSegment StartX=-49.19 StartY=40.5 StartZ=0 EndX=-18.2337 EndY=40.5 EndZ=0
    g35: LineSegment StartX=-49.19 StartY=37.5 StartZ=0 EndX=-18.23 EndY=37.5 EndZ=0
    g36: LineSegment StartX=-49.19 StartY=34.5 StartZ=0 EndX=-18.2337 EndY=34.5 EndZ=0
    g37: LineSegment StartX=-49.19 StartY=31.5 StartZ=0 EndX=-18.23 EndY=31.5 EndZ=0
    g38: LineSegment StartX=-49.19 StartY=28.75 StartZ=0 EndX=-16.2837 EndY=28.75 EndZ=0
    g39: LineSegment StartX=-49.19 StartY=25.75 StartZ=0 EndX=-16.28 EndY=25.75 EndZ=0
    g40: LineSegment StartX=-49.19 StartY=23 StartZ=0 EndX=-11.49 EndY=23 EndZ=0
    g41: LineSegment StartX=-49.19 StartY=20 StartZ=0 EndX=-11.49 EndY=20 EndZ=0
    g42: LineSegment StartX=-49.19 StartY=17.25 StartZ=0 EndX=-1.5 EndY=17.25 EndZ=0
    g43: LineSegment StartX=-49.19 StartY=14.25 StartZ=0 EndX=-1.5 EndY=14.25 EndZ=0
    g44: LineSegment StartX=-49.19 StartY=11.5 StartZ=0 EndX=-1.5 EndY=11.5 EndZ=0
    g45: LineSegment StartX=-49.19 StartY=8.5 StartZ=0 EndX=-1.5 EndY=8.5 EndZ=0
    g46: LineSegment StartX=-49.19 StartY=5.75 StartZ=0 EndX=-1.5 EndY=5.75 EndZ=0
    g47: LineSegment StartX=-49.19 StartY=2.75 StartZ=0 EndX=-1.5 EndY=2.75 EndZ=0
  constraints (120):
    c: Vertical(g0)
    c: Distance(g0) = 3
    c: Block(g0)
    c: Vertical(g1)
    c: Distance(g1) = 3
    c: Vertical(g2)
    c: Equal(g0,g2) = 3
    c: Block(g2)
    c: Vertical(g3)
    c: Equal(g1,g3) = 3
    c: Vertical(g4)
    c: Equal(g0,g4) = 3
    c: Block(g4)
    c: Vertical(g5)
    c: Equal(g1,g5) = 3
    c: Vertical(g6)
    c: Equal(g0,g6) = 3
    c: Block(g6)
    c: Vertical(g7)
    c: Equal(g1,g7) = 3
    c: Vertical(g8)
    c: Equal(g0,g8) = 3
    c: Block(g8)
    c: Vertical(g9)
    c: Equal(g1,g9) = 3
    c: Vertical(g10)
    c: Equal(g0,g10) = 3
    c: Block(g10)
    c: Vertical(g11)
    c: Equal(g1,g11) = 3
    c: Block(g12)
    c: Block(g13)
    c: Block(g14)
    c: Block(g15)
    c: Block(g16)
    c: Block(g17)
    c: Block(g18)
    c: Block(g19)
    c: Block(g20)
    c: Block(g21)
    c: Block(g22)
    c: Block(g23)
    c: Block(g11)
    c: Block(g9)
    c: Block(g7)
    c: Block(g5)
    c: Block(g3)
    c: Block(g1)
    c: Coincident(g24,g0)
    c: Coincident(g24,g12)
    c: Horizontal(g24)
    c: Coincident(g25,g0)
    c: Coincident(g25,g12)
    c: Horizontal(g25)
    c: Coincident(g26,g1)
    c: Coincident(g26,g13)
    c: Horizontal(g26)
    c: Coincident(g27,g1)
    c: Coincident(g27,g13)
    c: Horizontal(g27)
    c: Coincident(g28,g2)
    c: Coincident(g28,g14)
    c: Horizontal(g28)
    c: Coincident(g29,g2)
    c: Coincident(g29,g14)
    c: Horizontal(g29)
    c: Coincident(g30,g3)
    c: Coincident(g30,g15)
    c: Horizontal(g30)
    c: Coincident(g31,g3)
    c: Coincident(g31,g15)
    c: Horizontal(g31)
    c: Coincident(g32,g4)
    c: Coincident(g32,g16)
    c: Horizontal(g32)
    c: Coincident(g33,g4)
    c: Coincident(g33,g16)
    c: Horizontal(g33)
    c: Coincident(g34,g5)
    c: Coincident(g34,g17)
    c: Horizontal(g34)
    c: Coincident(g35,g5)
    c: Coincident(g35,g17)
    c: Horizontal(g35)
    c: Coincident(g36,g6)
    c: Coincident(g36,g19)
    c: Horizontal(g36)
    c: Coincident(g37,g6)
    c: Coincident(g37,g19)
    c: Horizontal(g37)
    c: Coincident(g38,g7)
    c: Coincident(g38,g18)
    c: Horizontal(g38)
    c: Coincident(g39,g7)
    c: Coincident(g39,g18)
    c: Horizontal(g39)
    c: Coincident(g40,g8)
    c: Coincident(g40,g20)
    c: Horizontal(g40)
    c: Coincident(g41,g8)
    c: Coincident(g41,g20)
    c: Horizontal(g41)
    c: Coincident(g42,g9)
    c: Coincident(g42,g23)
    c: Horizontal(g42)
    c: Coincident(g43,g9)
    c: Coincident(g43,g23)
    c: Horizontal(g43)
    c: Coincident(g44,g10)
    c: Coincident(g44,g22)
    c: Horizontal(g44)
    c: Coincident(g45,g10)
    c: Coincident(g45,g22)
    c: Horizontal(g45)
    c: Coincident(g46,g11)
    c: Coincident(g46,g21)
    c: Horizontal(g46)
    c: Coincident(g47,g11)
    c: Coincident(g47,g21)
    c: Horizontal(g47)
FEATURE [Sketcher::SketchObject] Sketch031
  FullyConstrained = true
  Placement = pos=(117,19,0) rot=(0.57735,0.57735,0.57735;2.0944rad)
  sketch-geometry (24):
    g0: ArcOfCircle CenterX=-49.19 CenterY=67.75 CenterZ=0 NormalX=0 NormalY=0 NormalZ=1 AngleXU=0 Radius=1.5 StartAngle=1.5708 EndAngle=4.71239
    g1: ArcOfCircle CenterX=-49.19 CenterY=62 CenterZ=0 NormalX=0 NormalY=0 NormalZ=1 AngleXU=0 Radius=1.5 StartAngle=1.5708 EndAngle=4.71239
    g2: ArcOfCircle CenterX=-49.19 CenterY=56.25 CenterZ=0 NormalX=0 NormalY=0 NormalZ=1 AngleXU=0 Radius=1.5 StartAngle=1.5708 EndAngle=4.71239
    g3: ArcOfCircle CenterX=-49.19 CenterY=50.5 CenterZ=0 NormalX=0 NormalY=0 NormalZ=1 AngleXU=0 Radius=1.5 StartAngle=1.5708 EndAngle=4.71239
    g4: ArcOfCircle CenterX=-49.19 CenterY=44.75 CenterZ=0 NormalX=0 NormalY=0 NormalZ=1 AngleXU=0 Radius=1.5 StartAngle=1.5708 EndAngle=4.71239
    g5: ArcOfCircle CenterX=-49.19 CenterY=39 CenterZ=0 NormalX=0 NormalY=0 NormalZ=1 AngleXU=0 Radius=1.5 StartAngle=1.5708 EndAngle=4.71239
    g6: ArcOfCircle CenterX=-49.19 CenterY=33 CenterZ=0 NormalX=0 NormalY=0 NormalZ=1 AngleXU=0 Radius=1.5 StartAngle=1.5708 EndAngle=4.71239
    g7: ArcOfCircle CenterX=-49.19 CenterY=27.25 CenterZ=0 NormalX=0 NormalY=0 NormalZ=1 AngleXU=0 Radius=1.5 StartAngle=1.5708 EndAngle=4.71239
    g8: ArcOfCircle CenterX=-49.19 CenterY=21.5 CenterZ=0 NormalX=0 NormalY=0 NormalZ=1 AngleXU=0 Radius=1.5 StartAngle=1.5708 EndAngle=4.71239
    g9: ArcOfCircle CenterX=-49.19 CenterY=15.75 CenterZ=0 NormalX=0 NormalY=0 NormalZ=1 AngleXU=0 Radius=1.5 StartAngle=1.5708 EndAngle=4.71239
    g10: ArcOfCircle CenterX=-49.19 CenterY=10 CenterZ=0 NormalX=0 NormalY=0 NormalZ=1 AngleXU=0 Radius=1.5 StartAngle=1.5708 EndAngle=4.71239
    g11: ArcOfCircle CenterX=-49.19 CenterY=4.25 CenterZ=0 NormalX=0 NormalY=0 NormalZ=1 AngleXU=0 Radius=1.5 StartAngle=1.5708 EndAngle=4.71239
    g12: LineSegment StartX=-49.19 StartY=69.25 StartZ=0 EndX=-49.19 EndY=66.25 EndZ=0
    g13: LineSegment StartX=-49.19 StartY=63.5 StartZ=0 EndX=-49.19 EndY=60.5 EndZ=0
    g14: LineSegment StartX=-49.19 StartY=57.75 StartZ=0 EndX=-49.19 EndY=54.75 EndZ=0
    g15: LineSegment StartX=-49.19 StartY=52 StartZ=0 EndX=-49.19 EndY=49 EndZ=0
    g16: LineSegment StartX=-49.19 StartY=46.25 StartZ=0 EndX=-49.19 EndY=43.25 EndZ=0
    g17: LineSegment StartX=-49.19 StartY=40.5 StartZ=0 EndX=-49.19 EndY=37.5 EndZ=0
    g18: LineSegment StartX=-49.19 StartY=34.5 StartZ=0 EndX=-49.19 EndY=31.5 EndZ=0
    g19: LineSegment StartX=-49.19 StartY=28.75 StartZ=0 EndX=-49.19 EndY=25.75 EndZ=0
    g20: LineSegment StartX=-49.19 StartY=23 StartZ=0 EndX=-49.19 EndY=20 EndZ=0
    g21: LineSegment StartX=-49.19 StartY=17.25 StartZ=0 EndX=-49.19 EndY=14.25 EndZ=0
    g22: LineSegment StartX=-49.19 StartY=11.5 StartZ=0 EndX=-49.19 EndY=8.5 EndZ=0
    g23: LineSegment StartX=-49.19 StartY=5.75 StartZ=0 EndX=-49.19 EndY=2.75 EndZ=0
  constraints (48):
    c: Block(g0)
    c: Block(g1)
    c: Block(g2)
    c: Block(g3)
    c: Block(g4)
    c: Block(g5)
    c: Block(g6)
    c: Block(g7)
    c: Block(g8)
    c: Block(g9)
    c: Block(g10)
    c: Block(g11)
    c: Coincident(g12,g0)
    c: Coincident(g12,g0)
    c: Vertical(g12)
    c: Vertical(g13)
    c: Coincident(g13,g1)
    c: Vertical(g14)
    c: Coincident(g14,g2)
    c: Vertical(g15)
    c: Coincident(g15,g3)
    c: Vertical(g16)
    c: Coincident(g16,g4)
    c: Vertical(g17)
    c: Coincident(g17,g5)
    c: Vertical(g18)
    c: Coincident(g18,g6)
    c: Vertical(g19)
    c: Coincident(g19,g7)
    c: Vertical(g20)
    c: Coincident(g20,g8)
    c: Vertical(g21)
    c: Coincident(g21,g9)
    c: Vertical(g22)
    c: Coincident(g22,g10)
    c: Vertical(g23)
    c: Coincident(g23,g11)
    c: Block(g23)
    c: Block(g22)
    c: Block(g21)
    c: Block(g20)
    c: Block(g13)
    c: Block(g14)
    c: Block(g15)
    c: Block(g16)
    c: Block(g17)
    c: Block(g18)
    c: Block(g19)
FEATURE [Part::Extrusion] Extrude022
  Base = -> Sketch030
  Dir = (1,-2e-16,2e-16)
  DirMode = 2
  FaceMakerClass = Part::FaceMakerBullseye
  LengthFwd = 19
  LengthRev = 0
  Placement = pos=(-19,0,0) rot=(0,0,1;0rad)
  Solid = true
  Symmetric = false
FEATURE [Part::Fillet] Fillet022
  Base = -> Extrude022
  Edges = 24 edges r=1.49: [Edge6,Edge11,Edge18,Edge23,Edge30,Edge35,Edge42,Edge47,Edge54,Edge59,Edge66,Edge71,Edge78,Edge83,Edge90,Edge95,Edge102,Edge107,Edge114,Edge119,Edge126,Edge131,Edge138,Edge143]
FEATURE [Part::Cut] Cut020  label="top010"
  Base = -> Cut019
  Tool = -> Fillet022
FEATURE [Sketcher::SketchObject] Sketch032
  FullyConstrained = true
  Placement = pos=(117,19,0) rot=(0.57735,0.57735,0.57735;2.0944rad)
  sketch-geometry (48):
    g0: LineSegment StartX=-49.19 StartY=69.25 StartZ=0 EndX=-49.19 EndY=66.25 EndZ=0
    g1: LineSegment StartX=-49.19 StartY=63.5 StartZ=0 EndX=-49.19 EndY=60.5 EndZ=0
    g2: LineSegment StartX=-49.19 StartY=57.75 StartZ=0 EndX=-49.19 EndY=54.75 EndZ=0
    g3: LineSegment StartX=-49.19 StartY=52 StartZ=0 EndX=-49.19 EndY=49 EndZ=0
    g4: LineSegment StartX=-49.19 StartY=46.25 StartZ=0 EndX=-49.19 EndY=43.25 EndZ=0
    g5: LineSegment StartX=-49.19 StartY=40.5 StartZ=0 EndX=-49.19 EndY=37.5 EndZ=0
    g6: LineSegment StartX=-49.19 StartY=34.5 StartZ=0 EndX=-49.19 EndY=31.5 EndZ=0
    g7: LineSegment StartX=-49.19 StartY=28.75 StartZ=0 EndX=-49.19 EndY=25.75 EndZ=0
    g8: LineSegment StartX=-49.19 StartY=23 StartZ=0 EndX=-49.19 EndY=20 EndZ=0
    g9: LineSegment StartX=-49.19 StartY=17.25 StartZ=0 EndX=-49.19 EndY=14.25 EndZ=0
    g10: LineSegment StartX=-49.19 StartY=11.5 StartZ=0 EndX=-49.19 EndY=8.5 EndZ=0
    g11: LineSegment StartX=-49.19 StartY=5.75 StartZ=0 EndX=-49.19 EndY=2.75 EndZ=0
    g12: ArcOfCircle CenterX=-1.5 CenterY=67.75 CenterZ=0 NormalX=0 NormalY=0 NormalZ=1 AngleXU=0 Radius=1.5 StartAngle=4.71239 EndAngle=7.85398
    g13: ArcOfCircle CenterX=-1.5 CenterY=62 CenterZ=0 NormalX=0 NormalY=0 NormalZ=1 AngleXU=0 Radius=1.5 StartAngle=4.71239 EndAngle=7.85398
    g14: ArcOfCircle CenterX=-1.5 CenterY=56.25 CenterZ=0 NormalX=0 NormalY=0 NormalZ=1 AngleXU=0 Radius=1.5 StartAngle=4.71239 EndAngle=7.85398
    g15: ArcOfCircle CenterX=-11.49 CenterY=50.5 CenterZ=0 NormalX=0 NormalY=0 NormalZ=1 AngleXU=0 Radius=1.5 StartAngle=4.71239 EndAngle=7.85398
    g16: ArcOfCircle CenterX=-16.28 CenterY=44.75 CenterZ=0 NormalX=0 NormalY=0 NormalZ=1 AngleXU=0 Radius=1.5 StartAngle=4.71239 EndAngle=7.85398
    g17: ArcOfCircle CenterX=-18.2337 CenterY=39 CenterZ=0 NormalX=0 NormalY=0 NormalZ=1 AngleXU=0 Radius=1.5 StartAngle=4.71485 EndAngle=7.85398
    g18: ArcOfCircle CenterX=-16.2837 CenterY=27.25 CenterZ=0 NormalX=0 NormalY=0 NormalZ=1 AngleXU=0 Radius=1.5 StartAngle=4.71485 EndAngle=7.85398
    g19: ArcOfCircle CenterX=-18.2337 CenterY=33 CenterZ=0 NormalX=0 NormalY=0 NormalZ=1 AngleXU=0 Radius=1.5 StartAngle=4.71485 EndAngle=7.85398
    g20: ArcOfCircle CenterX=-11.49 CenterY=21.5 CenterZ=0 NormalX=0 NormalY=0 NormalZ=1 AngleXU=0 Radius=1.5 StartAngle=4.71239 EndAngle=7.85398
    g21: ArcOfCircle CenterX=-1.5 CenterY=4.25 CenterZ=0 NormalX=0 NormalY=0 NormalZ=1 AngleXU=0 Radius=1.5 StartAngle=4.71239 EndAngle=7.85398
    g22: ArcOfCircle CenterX=-1.5 CenterY=10 CenterZ=0 NormalX=0 NormalY=0 NormalZ=1 AngleXU=0 Radius=1.5 StartAngle=4.71239 EndAngle=7.85398
    g23: ArcOfCircle CenterX=-1.5 CenterY=15.75 CenterZ=0 NormalX=0 NormalY=0 NormalZ=1 AngleXU=0 Radius=1.5 StartAngle=4.71239 EndAngle=7.85398
    g24: LineSegment StartX=-49.19 StartY=69.25 StartZ=0 EndX=-1.5 EndY=69.25 EndZ=0
    g25: LineSegment StartX=-49.19 StartY=66.25 StartZ=0 EndX=-1.5 EndY=66.25 EndZ=0
    g26: LineSegment StartX=-49.19 StartY=63.5 StartZ=0 EndX=-1.5 EndY=63.5 EndZ=0
    g27: LineSegment StartX=-49.19 StartY=60.5 StartZ=0 EndX=-1.5 EndY=60.5 EndZ=0
    g28: LineSegment StartX=-49.19 StartY=57.75 StartZ=0 EndX=-1.5 EndY=57.75 EndZ=0
    g29: LineSegment StartX=-49.19 StartY=54.75 StartZ=0 EndX=-1.5 EndY=54.75 EndZ=0
    g30: LineSegment StartX=-49.19 StartY=52 StartZ=0 EndX=-11.49 EndY=52 EndZ=0
    g31: LineSegment StartX=-49.19 StartY=49 StartZ=0 EndX=-11.49 EndY=49 EndZ=0
    g32: LineSegment StartX=-49.19 StartY=46.25 StartZ=0 EndX=-16.28 EndY=46.25 EndZ=0
    g33: LineSegment StartX=-49.19 StartY=43.25 StartZ=0 EndX=-16.28 EndY=43.25 EndZ=0
    g34: LineSegment StartX=-49.19 StartY=40.5 StartZ=0 EndX=-18.2337 EndY=40.5 EndZ=0
    g35: LineSegment StartX=-49.19 StartY=37.5 StartZ=0 EndX=-18.23 EndY=37.5 EndZ=0
    g36: LineSegment StartX=-49.19 StartY=34.5 StartZ=0 EndX=-18.2337 EndY=34.5 EndZ=0
    g37: LineSegment StartX=-49.19 StartY=31.5 StartZ=0 EndX=-18.23 EndY=31.5 EndZ=0
    g38: LineSegment StartX=-49.19 StartY=28.75 StartZ=0 EndX=-16.2837 EndY=28.75 EndZ=0
    g39: LineSegment StartX=-49.19 StartY=25.75 StartZ=0 EndX=-16.28 EndY=25.75 EndZ=0
    g40: LineSegment StartX=-49.19 StartY=23 StartZ=0 EndX=-11.49 EndY=23 EndZ=0
    g41: LineSegment StartX=-49.19 StartY=20 StartZ=0 EndX=-11.49 EndY=20 EndZ=0
    g42: LineSegment StartX=-49.19 StartY=17.25 StartZ=0 EndX=-1.5 EndY=17.25 EndZ=0
    g43: LineSegment StartX=-49.19 StartY=14.25 StartZ=0 EndX=-1.5 EndY=14.25 EndZ=0
    g44: LineSegment StartX=-49.19 StartY=11.5 StartZ=0 EndX=-1.5 EndY=11.5 EndZ=0
    g45: LineSegment StartX=-49.19 StartY=8.5 StartZ=0 EndX=-1.5 EndY=8.5 EndZ=0
    g46: LineSegment StartX=-49.19 StartY=5.75 StartZ=0 EndX=-1.5 EndY=5.75 EndZ=0
    g47: LineSegment StartX=-49.19 StartY=2.75 StartZ=0 EndX=-1.5 EndY=2.75 EndZ=0
  constraints (120):
    c: Vertical(g0)
    c: Distance(g0) = 3
    c: Block(g0)
    c: Vertical(g1)
    c: Distance(g1) = 3
    c: Vertical(g2)
    c: Equal(g0,g2) = 3
    c: Block(g2)
    c: Vertical(g3)
    c: Equal(g1,g3) = 3
    c: Vertical(g4)
    c: Equal(g0,g4) = 3
    c: Block(g4)
    c: Vertical(g5)
    c: Equal(g1,g5) = 3
    c: Vertical(g6)
    c: Equal(g0,g6) = 3
    c: Block(g6)
    c: Vertical(g7)
    c: Equal(g1,g7) = 3
    c: Vertical(g8)
    c: Equal(g0,g8) = 3
    c: Block(g8)
    c: Vertical(g9)
    c: Equal(g1,g9) = 3
    c: Vertical(g10)
    c: Equal(g0,g10) = 3
    c: Block(g10)
    c: Vertical(g11)
    c: Equal(g1,g11) = 3
    c: Block(g12)
    c: Block(g13)
    c: Block(g14)
    c: Block(g15)
    c: Block(g16)
    c: Block(g17)
    c: Block(g18)
    c: Block(g19)
    c: Block(g20)
    c: Block(g21)
    c: Block(g22)
    c: Block(g23)
    c: Block(g11)
    c: Block(g9)
    c: Block(g7)
    c: Block(g5)
    c: Block(g3)
    c: Block(g1)
    c: Coincident(g24,g0)
    c: Coincident(g24,g12)
    c: Horizontal(g24)
    c: Coincident(g25,g0)
    c: Coincident(g25,g12)
    c: Horizontal(g25)
    c: Coincident(g26,g1)
    c: Coincident(g26,g13)
    c: Horizontal(g26)
    c: Coincident(g27,g1)
    c: Coincident(g27,g13)
    c: Horizontal(g27)
    c: Coincident(g28,g2)
    c: Coincident(g28,g14)
    c: Horizontal(g28)
    c: Coincident(g29,g2)
    c: Coincident(g29,g14)
    c: Horizontal(g29)
    c: Coincident(g30,g3)
    c: Coincident(g30,g15)
    c: Horizontal(g30)
    c: Coincident(g31,g3)
    c: Coincident(g31,g15)
    c: Horizontal(g31)
    c: Coincident(g32,g4)
    c: Coincident(g32,g16)
    c: Horizontal(g32)
    c: Coincident(g33,g4)
    c: Coincident(g33,g16)
    c: Horizontal(g33)
    c: Coincident(g34,g5)
    c: Coincident(g34,g17)
    c: Horizontal(g34)
    c: Coincident(g35,g5)
    c: Coincident(g35,g17)
    c: Horizontal(g35)
    c: Coincident(g36,g6)
    c: Coincident(g36,g19)
    c: Horizontal(g36)
    c: Coincident(g37,g6)
    c: Coincident(g37,g19)
    c: Horizontal(g37)
    c: Coincident(g38,g7)
    c: Coincident(g38,g18)
    c: Horizontal(g38)
    c: Coincident(g39,g7)
    c: Coincident(g39,g18)
    c: Horizontal(g39)
    c: Coincident(g40,g8)
    c: Coincident(g40,g20)
    c: Horizontal(g40)
    c: Coincident(g41,g8)
    c: Coincident(g41,g20)
    c: Horizontal(g41)
    c: Coincident(g42,g9)
    c: Coincident(g42,g23)
    c: Horizontal(g42)
    c: Coincident(g43,g9)
    c: Coincident(g43,g23)
    c: Horizontal(g43)
    c: Coincident(g44,g10)
    c: Coincident(g44,g22)
    c: Horizontal(g44)
    c: Coincident(g45,g10)
    c: Coincident(g45,g22)
    c: Horizontal(g45)
    c: Coincident(g46,g11)
    c: Coincident(g46,g21)
    c: Horizontal(g46)
    c: Coincident(g47,g11)
    c: Coincident(g47,g21)
    c: Horizontal(g47)
FEATURE [Part::Extrusion] Extrude023
  Base = -> Sketch032
  Dir = (1,-2e-16,2e-16)
  DirMode = 2
  FaceMakerClass = Part::FaceMakerBullseye
  LengthFwd = 19
  LengthRev = 0
  Placement = pos=(-19,0,0) rot=(0,0,1;0rad)
  Solid = true
  Symmetric = false
FEATURE [Part::Fillet] Fillet023
  Base = -> Extrude023
  Edges = <same value as first occurrence — deduplicated (x6 in doc)>
  Placement = pos=(0,0.05,0) rot=(0,0,1;0rad)
FEATURE [Part::Cut] Cut014  label="bottom003"
  Base = -> Cut007
  Tool = -> Fusion047
FEATURE [Part::Cut] Cut021  label="bottom004"
  Base = -> Cut014
  Tool = -> Fillet023
FEATURE [Sketcher::SketchObject] Sketch033
  FullyConstrained = true
  Placement = pos=(117,19,0) rot=(0.57735,0.57735,0.57735;2.0944rad)
  sketch-geometry (8):
    g0: LineSegment StartX=-49.19 StartY=69.25 StartZ=0 EndX=-49.19 EndY=66.25 EndZ=0
    g1: LineSegment StartX=-49.19 StartY=5.75 StartZ=0 EndX=-49.19 EndY=2.75 EndZ=0
    g2: ArcOfCircle CenterX=-1.5 CenterY=67.75 CenterZ=0 NormalX=0 NormalY=0 NormalZ=1 AngleXU=0 Radius=1.5 StartAngle=4.71239 EndAngle=7.85398
    g3: ArcOfCircle CenterX=-1.5 CenterY=4.25 CenterZ=0 NormalX=0 NormalY=0 NormalZ=1 AngleXU=0 Radius=1.5 StartAngle=4.71239 EndAngle=7.85398
    g4: LineSegment StartX=-49.19 StartY=69.25 StartZ=0 EndX=-1.5 EndY=69.25 EndZ=0
    g5: LineSegment StartX=-49.19 StartY=66.25 StartZ=0 EndX=-1.5 EndY=66.25 EndZ=0
    g6: LineSegment StartX=-49.19 StartY=5.75 StartZ=0 EndX=-1.5 EndY=5.75 EndZ=0
    g7: LineSegment StartX=-49.19 StartY=2.75 StartZ=0 EndX=-1.5 EndY=2.75 EndZ=0
  constraints (19):
    c: Vertical(g0)
    c: Distance(g0) = 3
    c: Block(g0)
    c: Vertical(g1)
    c: Block(g2)
    c: Block(g3)
    c: Block(g1)
    c: Coincident(g4,g0)
    c: Coincident(g4,g2)
    c: Horizontal(g4)
    c: Coincident(g5,g0)
    c: Coincident(g5,g2)
    c: Horizontal(g5)
    c: Coincident(g6,g1)
    c: Coincident(g6,g3)
    c: Horizontal(g6)
    c: Coincident(g7,g1)
    c: Coincident(g7,g3)
    c: Horizontal(g7)
FEATURE [Sketcher::SketchObject] Sketch034
  FullyConstrained = true
  Placement = pos=(117,19,0) rot=(0.57735,0.57735,0.57735;2.0944rad)
  sketch-geometry (8):
    g0: LineSegment StartX=-49.19 StartY=63.5 StartZ=0 EndX=-49.19 EndY=60.5 EndZ=0
    g1: LineSegment StartX=-49.19 StartY=11.5 StartZ=0 EndX=-49.19 EndY=8.5 EndZ=0
    g2: ArcOfCircle CenterX=-1.5 CenterY=62 CenterZ=0 NormalX=0 NormalY=0 NormalZ=1 AngleXU=0 Radius=1.5 StartAngle=4.71239 EndAngle=7.85398
    g3: ArcOfCircle CenterX=-1.5 CenterY=10 CenterZ=0 NormalX=0 NormalY=0 NormalZ=1 AngleXU=0 Radius=1.5 StartAngle=4.71239 EndAngle=7.85398
    g4: LineSegment StartX=-49.19 StartY=63.5 StartZ=0 EndX=-1.5 EndY=63.5 EndZ=0
    g5: LineSegment StartX=-49.19 StartY=60.5 StartZ=0 EndX=-1.5 EndY=60.5 EndZ=0
    g6: LineSegment StartX=-49.19 StartY=11.5 StartZ=0 EndX=-1.5 EndY=11.5 EndZ=0
    g7: LineSegment StartX=-49.19 StartY=8.5 StartZ=0 EndX=-1.5 EndY=8.5 EndZ=0
  constraints (19):
    c: Vertical(g0)
    c: Distance(g0) = 3
    c: Vertical(g1)
    c: Block(g1)
    c: Block(g2)
    c: Block(g3)
    c: Block(g0)
    c: Coincident(g4,g0)
    c: Coincident(g4,g2)
    c: Horizontal(g4)
    c: Coincident(g5,g0)
    c: Coincident(g5,g2)
    c: Horizontal(g5)
    c: Coincident(g6,g1)
    c: Coincident(g6,g3)
    c: Horizontal(g6)
    c: Coincident(g7,g1)
    c: Coincident(g7,g3)
    c: Horizontal(g7)
FEATURE [Part::Extrusion] Extrude024
  Base = -> Sketch033
  Dir = (1,0,0)
  DirMode = 2
  FaceMakerClass = Part::FaceMakerBullseye
  LengthFwd = 10
  LengthRev = 0
  Solid = true
  Symmetric = false
FEATURE [Part::Extrusion] Extrude025
  Base = -> Sketch034
  Dir = (1,0,0)
  DirMode = 2
  FaceMakerClass = Part::FaceMakerBullseye
  LengthFwd = 10
  LengthRev = 0
  Solid = true
  Symmetric = false
FEATURE [Part::Fillet] Fillet024  label="removeFromtMoreFrontCaseScrewRetainers"
  Base = -> Extrude024
  Edges = 4 edges r=1.49: [Edge6,Edge11,Edge18,Edge23]
  Placement = pos=(-11,0,0) rot=(0,0,1;0rad)
FEATURE [Part::Fillet] Fillet025  label="removeFromtMoreFrontCaseScrewRetainers001"
  Base = -> Extrude025
  Edges = 4 edges r=1.49: [Edge6,Edge11,Edge18,Edge23]
  Placement = pos=(-19,0,0) rot=(0,0,1;0rad)
FEATURE [Part::Cut] Cut022
  Base = -> Cut015
  Tool = -> Fillet025
FEATURE [Part::Cut] Cut023  label="screwRetainers"
  Base = -> Cut022
  Tool = -> Fillet024
FEATURE [Part::MultiFuse] Fusion056  label="bottom005"
  Shapes = -> [Fusion044,Cut021]
FEATURE [Part::MultiFuse] Fusion057  label="casePillars001"
  Shapes = -> [Cut016,Fusion052]
FEATURE [Part::MultiFuse] Fusion058  label="bottom006"
  Shapes = -> [Fusion056,Cut023]
FEATURE [Part::MultiFuse] Fusion059  label="bottom007"
  Shapes = -> [Fusion058,Fillet005]
FEATURE [Part::MultiFuse] Fusion060  label="bottom008"
  Shapes = -> [Fusion059,Fusion]
FEATURE [Part::MultiFuse] Fusion061  label="top011"
  Shapes = -> [Cut006,Cut020]
FEATURE [Part::MultiFuse] Fusion062  label="top012"
  Shapes = -> [Fusion057,Fusion061]
FEATURE [Sketcher::SketchObject] Sketch035  label="topSketch007"
  FullyConstrained = true
  sketch-geometry (6):
    g0: LineSegment StartX=19 StartY=38 StartZ=0 EndX=117 EndY=38 EndZ=0
    g1: ArcOfCircle CenterX=19 CenterY=19 CenterZ=0 NormalX=0 NormalY=0 NormalZ=1 AngleXU=0 Radius=19 StartAngle=1.5708 EndAngle=3.14159
    g2: LineSegment StartX=117 StartY=38 StartZ=0 EndX=117 EndY=19 EndZ=0
    g3: LineSegment StartX=98 StartY=1.0161e-12 StartZ=0 EndX=5.22862e-06 EndY=1.0161e-12 EndZ=0
    g4: LineSegment StartX=5.22862e-06 StartY=19 StartZ=0 EndX=5.22862e-06 EndY=1.0161e-12 EndZ=0
    g5: ArcOfCircle CenterX=98 CenterY=19 CenterZ=0 NormalX=0 NormalY=0 NormalZ=1 AngleXU=0 Radius=19 StartAngle=4.71239 EndAngle=6.28319
  constraints (16):
    c: Horizontal(g0)
    c: Distance(g0) = 98
    c: Coincident(g1,g0)
    c: Block(g1)
    c: Coincident(g2,g0)
    c: Vertical(g2)
    c: Distance(g2) = 19
    c: Horizontal(g3)
    c: Coincident(g4,g1)
    c: Vertical(g4)
    c: Coincident(g3,g4)
    c: Block(g3)
    c: Coincident(g5,g2)
    c: Coincident(g5,g3)
    c: Block(g0)
    c: Block(g5)
FEATURE [Part::Extrusion] Extrude026  label="sideA001"
  Base = -> Sketch035
  Dir = (0,0,1)
  DirMode = 2
  FaceMakerClass = Part::FaceMakerBullseye
  LengthFwd = 3
  LengthRev = 0
  Placement = pos=(0,0,-2.7) rot=(0,0,1;0rad)
  Solid = true
  Symmetric = false
FEATURE [Sketcher::SketchObject] Sketch036  label="topSketch008"
  FullyConstrained = true
  sketch-geometry (6):
    g0: LineSegment StartX=19 StartY=38 StartZ=0 EndX=117 EndY=38 EndZ=0
    g1: ArcOfCircle CenterX=19 CenterY=19 CenterZ=0 NormalX=0 NormalY=0 NormalZ=1 AngleXU=0 Radius=19 StartAngle=1.5708 EndAngle=3.14159
    g2: LineSegment StartX=117 StartY=38 StartZ=0 EndX=117 EndY=19 EndZ=0
    g3: LineSegment StartX=98 StartY=1.0161e-12 StartZ=0 EndX=5.22862e-06 EndY=1.0161e-12 EndZ=0
    g4: LineSegment StartX=5.22862e-06 StartY=19 StartZ=0 EndX=5.22862e-06 EndY=1.0161e-12 EndZ=0
    g5: ArcOfCircle CenterX=98 CenterY=19 CenterZ=0 NormalX=0 NormalY=0 NormalZ=1 AngleXU=0 Radius=19 StartAngle=4.71239 EndAngle=6.28319
  constraints (16):
    c: Horizontal(g0)
    c: Distance(g0) = 98
    c: Coincident(g1,g0)
    c: Block(g1)
    c: Coincident(g2,g0)
    c: Vertical(g2)
    c: Distance(g2) = 19
    c: Horizontal(g3)
    c: Coincident(g4,g1)
    c: Vertical(g4)
    c: Coincident(g3,g4)
    c: Block(g3)
    c: Coincident(g5,g2)
    c: Coincident(g5,g3)
    c: Block(g0)
    c: Block(g5)
FEATURE [Part::Extrusion] Extrude027  label="sideB001"
  Base = -> Sketch036
  Dir = (0,0,1)
  DirMode = 2
  FaceMakerClass = Part::FaceMakerBullseye
  LengthFwd = 3
  LengthRev = 0
  Placement = pos=(0,0,71.7) rot=(0,0,1;0rad)
  Solid = true
  Symmetric = false
FEATURE [Part::MultiFuse] Fusion064  label="removeFromBottom"
  Shapes = -> [Extrude026,Extrude027]
FEATURE [Part::Cut] Cut024  label="bottom009"
  Base = -> Fusion060
  Tool = -> Fusion064
FEATURE [Sketcher::SketchObject] Sketch037  label="topSketch009"
  FullyConstrained = true
  sketch-geometry (8):
    g0: ArcOfCircle CenterX=19 CenterY=19.1201 CenterZ=0 NormalX=0 NormalY=0 NormalZ=1 AngleXU=0 Radius=18.8799 StartAngle=1.5708 EndAngle=3.14793
    g1: LineSegment StartX=0.120501 StartY=19.0004 StartZ=0 EndX=0.120501 EndY=0.000382114 EndZ=0
    g2: LineSegment StartX=19 StartY=38 StartZ=0 EndX=124 EndY=38 EndZ=0
    g3: LineSegment StartX=0.120501 StartY=0.000382114 StartZ=0 EndX=105.121 EndY=0.000382114 EndZ=0
    g4: LineSegment StartX=124 StartY=38 StartZ=0 EndX=125.616 EndY=38 EndZ=0
    g5: LineSegment StartX=105.121 StartY=0.000382114 StartZ=0 EndX=106.736 EndY=0.000382114 EndZ=0
    g6: ArcOfCircle CenterX=106.616 CenterY=19 CenterZ=0 NormalX=0 NormalY=0 NormalZ=1 AngleXU=0 Radius=19 StartAngle=4.71873 EndAngle=6.28319
    g7: LineSegment StartX=125.616 StartY=38 StartZ=0 EndX=125.616 EndY=19 EndZ=0
  constraints (21):
    c: Block(g0)
    c: Coincident(g1,g0)
    c: Vertical(g1)
    c: Horizontal(g2)
    c: Distance(g2) = 105
    c: Coincident(g2,g0)
    c: Distance(g1) = 19
    c: Coincident(g3,g1)
    c: Horizontal(g3)
    c: Distance(g3) = 105
    c: Coincident(g4,g2)
    c: Horizontal(g4)
    c: Distance(g4) = 1.61553
    c: Horizontal(g5)
    c: Equal(g4,g5) = 1.61553
    c: Coincident(g5,g3)
    c: Block(g6)
    c: Coincident(g6,g5)
    c: Coincident(g7,g4)
    c: Coincident(g7,g6)
    c: Vertical(g7)
FEATURE [Part::Extrusion] Extrude028  label="sideB"
  Base = -> Sketch037
  Dir = (0,0,1)
  DirMode = 2
  FaceMakerClass = Part::FaceMakerBullseye
  LengthFwd = 3
  LengthRev = 0
  Placement = pos=(0,0,72) rot=(0,0,1;0rad)
  Solid = true
  Symmetric = false
FEATURE [Sketcher::SketchObject] Sketch038  label="topSketch010"
  FullyConstrained = true
  sketch-geometry (22):
    g0: LineSegment StartX=5.21097e-06 StartY=3 StartZ=0 EndX=5.21097e-06 EndY=19 EndZ=0
    g1: ArcOfCircle CenterX=19 CenterY=19 CenterZ=0 NormalX=0 NormalY=0 NormalZ=1 AngleXU=0 Radius=19 StartAngle=1.5708 EndAngle=3.14159
    g2: ArcOfCircle CenterX=19 CenterY=19 CenterZ=0 NormalX=0 NormalY=0 NormalZ=1 AngleXU=0 Radius=16 StartAngle=1.5708 EndAngle=3.14159
    g3: LineSegment StartX=114 StartY=35 StartZ=0 EndX=19 EndY=35 EndZ=0
    g4: LineSegment StartX=5.21097e-06 StartY=3 StartZ=0 EndX=5.21097e-06 EndY=0 EndZ=0
    g5: LineSegment StartX=3 StartY=0 StartZ=0 EndX=5.21097e-06 EndY=0 EndZ=0
    g6: LineSegment StartX=3 StartY=19 StartZ=0 EndX=3 EndY=0 EndZ=0
    g7: LineSegment StartX=19 StartY=38 StartZ=0 EndX=124 EndY=38 EndZ=0
    g8: Circle CenterX=119 CenterY=35 CenterZ=0 NormalX=0 NormalY=0 NormalZ=1 AngleXU=0 Radius=1
    g9: Circle CenterX=121 CenterY=35 CenterZ=0 NormalX=0 NormalY=0 NormalZ=1 AngleXU=0 Radius=1
    g10: Circle CenterX=121 CenterY=33 CenterZ=0 NormalX=0 NormalY=0 NormalZ=1 AngleXU=0 Radius=1
    g11: BSplineCurve PolesCount=3 KnotsCount=2 Degree=2 IsPeriodic=0
    g12: GeomPoint X=119 Y=35 Z=0
    g13: GeomPoint X=121 Y=33 Z=0
    g14: LineSegment StartX=119 StartY=35 StartZ=0 EndX=114 EndY=35 EndZ=0
    g15: ArcOfCircle CenterX=105 CenterY=19 CenterZ=0 NormalX=0 NormalY=0 NormalZ=1 AngleXU=0 Radius=16 StartAngle=5.60905 EndAngle=6.28319
    g16: LineSegment StartX=121 StartY=33 StartZ=0 EndX=121 EndY=19 EndZ=0
    g17: LineSegment StartX=117.5 StartY=9.01251 StartZ=0 EndX=121.163 EndY=9.0125 EndZ=0
    g18: ArcOfCircle CenterX=105 CenterY=19 CenterZ=0 NormalX=0 NormalY=0 NormalZ=1 AngleXU=0 Radius=20.6155 StartAngle=5.7297 EndAngle=6.28319
    g19: LineSegment StartX=121.163 StartY=9.0125 StartZ=0 EndX=122.538 EndY=8.16329 EndZ=0
    g20: LineSegment StartX=124 StartY=38 StartZ=0 EndX=125.616 EndY=38 EndZ=0
    g21: LineSegment StartX=125.616 StartY=19 StartZ=0 EndX=125.616 EndY=38 EndZ=0
  constraints (49):
    c: Vertical(g0)
    c: Block(g0)
    c: Coincident(g1,g0)
    c: Block(g1)
    c: Coincident(g2,g1)
    c: Block(g2)
    c: Coincident(g3,g2)
    c: Horizontal(g3)
    c: Tangent(g3,g2)
    c: Coincident(g4,g0)
    c: Distance(g4) = 3
    c: Vertical(g4)
    c: Coincident(g5,g4)
    c: Horizontal(g5)
    c: Coincident(g6,g2)
    c: Coincident(g6,g5)
    c: Vertical(g6)
    c: Horizontal(g7)
    c: Distance(g7) = 105
    c: Coincident(g7,g1)
    c: Block(g3)
    c: Weight(g8) = 1
    c: Equal(g8,g9)
    c: Equal(g8,g10)
    c: InternalAlignment(g8,g11)
    c: InternalAlignment(g9,g11)
    c: InternalAlignment(g10,g11)
    c: InternalAlignment(g12,g11)
    c: InternalAlignment(g13,g11)
    c: Block(g11)
    c: Coincident(g14,g11)
    c: Coincident(g14,g3)
    c: Horizontal(g14)
    c: Block(g15)
    c: Coincident(g16,g11)
    c: Coincident(g16,g15)
    c: Vertical(g16)
    c: Distance(g16) = 14
    c: Coincident(g17,g15)
    c: Block(g18)
    c: Coincident(g19,g18)
    c: Coincident(g20,g7)
    c: Horizontal(g20)
    c: Vertical(g21)
    c: Coincident(g20,g21)
    c: Block(g20)
    c: Block(g21)
    c: Block(g19)
    c: Block(g17)
FEATURE [Part::Extrusion] Extrude029
  Base = -> Sketch038
  Dir = (0,0,1)
  DirMode = 2
  FaceMakerClass = Part::FaceMakerBullseye
  LengthFwd = 72
  LengthRev = 0
  Solid = true
  Symmetric = false
FEATURE [Part::Feature] Face085
  shape: bbox 4.8 x 25.5 x 2e-07 mm, 1 faces, 0 solids (baked)
FEATURE [Part::Revolution] Revolve089  label="moreFrontCaseScrewPost003"
  Angle = 360
  Axis = (0,1,0)
  Base = (0,0,0)
  FaceMakerClass = Part::FaceMakerBullseye
  Placement = pos=(109.5,4.5,3.5) rot=(0,0,1;0rad)
  Solid = false
  Source = -> Face085
  Symmetric = false
FEATURE [Part::Feature] Face086
  shape: bbox 4.8 x 25.5 x 2e-07 mm, 1 faces, 0 solids (baked)
FEATURE [Part::Revolution] Revolve090  label="moreFrontCaseScrewPost004"
  Angle = 360
  Axis = (0,1,0)
  Base = (0,0,0)
  FaceMakerClass = Part::FaceMakerBullseye
  Placement = pos=(109.5,4.5,68.5) rot=(0,0,1;0rad)
  Solid = false
  Source = -> Face086
  Symmetric = false
FEATURE [Part::Fillet] Fillet026  label="top013"
  Base = -> Extrude029
  Edges = 1 edges r=2: [Edge35]
FEATURE [Sketcher::SketchObject] Sketch039
  FullyConstrained = true
  sketch-geometry (7):
    g0: LineSegment StartX=0 StartY=0 StartZ=0 EndX=0 EndY=6 EndZ=0
    g1: Circle CenterX=0 CenterY=0 CenterZ=0 NormalX=0 NormalY=0 NormalZ=1 AngleXU=0 Radius=1
    g2: Circle CenterX=8 CenterY=6 CenterZ=0 NormalX=0 NormalY=0 NormalZ=1 AngleXU=0 Radius=1
    g3: BSplineCurve PolesCount=3 KnotsCount=2 Degree=2 IsPeriodic=0
    g4: GeomPoint X=0 Y=0 Z=0
    g5: GeomPoint X=8 Y=6 Z=0
    g6: LineSegment StartX=0 StartY=6 StartZ=0 EndX=8 EndY=6 EndZ=0
  constraints (14):
    c: Coincident(g0,g-1)
    c: Distance(g0) = 6
    c: Vertical(g0)
    c: Coincident(g3,g0)
    c: Weight(g1) = 1
    c: Equal(g1,g2)
    c: InternalAlignment(g1,g3)
    c: InternalAlignment(g2,g3)
    c: InternalAlignment(g4,g3)
    c: InternalAlignment(g5,g3)
    c: Block(g3)
    c: Coincident(g6,g0)
    c: Coincident(g6,g3)
    c: Horizontal(g6)
FEATURE [Sketcher::SketchObject] Sketch040
  FullyConstrained = true
  sketch-geometry (7):
    g0: LineSegment StartX=0 StartY=0 StartZ=0 EndX=0 EndY=6 EndZ=0
    g1: Circle CenterX=0 CenterY=0 CenterZ=0 NormalX=0 NormalY=0 NormalZ=1 AngleXU=0 Radius=1
    g2: Circle CenterX=8 CenterY=6 CenterZ=0 NormalX=0 NormalY=0 NormalZ=1 AngleXU=0 Radius=1
    g3: BSplineCurve PolesCount=3 KnotsCount=2 Degree=2 IsPeriodic=0
    g4: GeomPoint X=0 Y=0 Z=0
    g5: GeomPoint X=8 Y=6 Z=0
    g6: LineSegment StartX=0 StartY=6 StartZ=0 EndX=8 EndY=6 EndZ=0
  constraints (14):
    c: Coincident(g0,g-1)
    c: Distance(g0) = 6
    c: Vertical(g0)
    c: Coincident(g3,g0)
    c: Weight(g1) = 1
    c: Equal(g1,g2)
    c: InternalAlignment(g1,g3)
    c: InternalAlignment(g2,g3)
    c: InternalAlignment(g4,g3)
    c: InternalAlignment(g5,g3)
    c: Block(g3)
    c: Coincident(g6,g0)
    c: Coincident(g6,g3)
    c: Horizontal(g6)
FEATURE [Sketcher::SketchObject] Sketch041
  FullyConstrained = true
  sketch-geometry (7):
    g0: LineSegment StartX=0 StartY=0 StartZ=0 EndX=0 EndY=6 EndZ=0
    g1: Circle CenterX=0 CenterY=0 CenterZ=0 NormalX=0 NormalY=0 NormalZ=1 AngleXU=0 Radius=1
    g2: Circle CenterX=8 CenterY=6 CenterZ=0 NormalX=0 NormalY=0 NormalZ=1 AngleXU=0 Radius=1
    g3: BSplineCurve PolesCount=3 KnotsCount=2 Degree=2 IsPeriodic=0
    g4: GeomPoint X=0 Y=0 Z=0
    g5: GeomPoint X=8 Y=6 Z=0
    g6: LineSegment StartX=0 StartY=6 StartZ=0 EndX=8 EndY=6 EndZ=0
  constraints (14):
    c: Coincident(g0,g-1)
    c: Distance(g0) = 6
    c: Vertical(g0)
    c: Coincident(g3,g0)
    c: Weight(g1) = 1
    c: Equal(g1,g2)
    c: InternalAlignment(g1,g3)
    c: InternalAlignment(g2,g3)
    c: InternalAlignment(g4,g3)
    c: InternalAlignment(g5,g3)
    c: Block(g3)
    c: Coincident(g6,g0)
    c: Coincident(g6,g3)
    c: Horizontal(g6)
FEATURE [Sketcher::SketchObject] Sketch042
  FullyConstrained = true
  sketch-geometry (7):
    g0: LineSegment StartX=0 StartY=0 StartZ=0 EndX=0 EndY=6 EndZ=0
    g1: Circle CenterX=0 CenterY=0 CenterZ=0 NormalX=0 NormalY=0 NormalZ=1 AngleXU=0 Radius=1
    g2: Circle CenterX=8 CenterY=6 CenterZ=0 NormalX=0 NormalY=0 NormalZ=1 AngleXU=0 Radius=1
    g3: BSplineCurve PolesCount=3 KnotsCount=2 Degree=2 IsPeriodic=0
    g4: GeomPoint X=0 Y=0 Z=0
    g5: GeomPoint X=8 Y=6 Z=0
    g6: LineSegment StartX=0 StartY=6 StartZ=0 EndX=8 EndY=6 EndZ=0
  constraints (14):
    c: Coincident(g0,g-1)
    c: Distance(g0) = 6
    c: Vertical(g0)
    c: Coincident(g3,g0)
    c: Weight(g1) = 1
    c: Equal(g1,g2)
    c: InternalAlignment(g1,g3)
    c: InternalAlignment(g2,g3)
    c: InternalAlignment(g4,g3)
    c: InternalAlignment(g5,g3)
    c: Block(g3)
    c: Coincident(g6,g0)
    c: Coincident(g6,g3)
    c: Horizontal(g6)
FEATURE [Part::Extrusion] Extrude030  label="caseScrewPillarBracket008"
  Base = -> Sketch039
  Dir = (0,0,1)
  DirMode = 2
  FaceMakerClass = Part::FaceMakerBullseye
  LengthFwd = 2.4
  LengthRev = 0
  Placement = pos=(15.76,29,8.8) rot=(0,1,0;0rad)
  Solid = true
  Symmetric = false
FEATURE [Part::Extrusion] Extrude031  label="caseScrewPillarBracket009"
  Base = -> Sketch040
  Dir = (0,0,1)
  DirMode = 2
  FaceMakerClass = Part::FaceMakerBullseye
  LengthFwd = 2.4
  LengthRev = 0
  Placement = pos=(15.76,29,60.8) rot=(0,0,1;0rad)
  Solid = true
  Symmetric = false
FEATURE [Part::Extrusion] Extrude032  label="caseScrewPillarBracket010"
  Base = -> Sketch041
  Dir = (0,0,1)
  DirMode = 2
  FaceMakerClass = Part::FaceMakerBullseye
  LengthFwd = 2.4
  LengthRev = 0
  Placement = pos=(13.7,29,13.26) rot=(0,-1,0;1.5708rad)
  Solid = true
  Symmetric = false
FEATURE [Part::Extrusion] Extrude033  label="caseScrewPillarBracket011"
  Base = -> Sketch042
  Dir = (0,0,1)
  DirMode = 2
  FaceMakerClass = Part::FaceMakerBullseye
  LengthFwd = 2.4
  LengthRev = 0
  Placement = pos=(11.3,29,58.74) rot=(0,1,0;1.5708rad)
  Solid = true
  Symmetric = false
FEATURE [Sketcher::SketchObject] Sketch043
  FullyConstrained = true
  sketch-geometry (7):
    g0: LineSegment StartX=0 StartY=0 StartZ=0 EndX=0 EndY=6 EndZ=0
    g1: Circle CenterX=0 CenterY=0 CenterZ=0 NormalX=0 NormalY=0 NormalZ=1 AngleXU=0 Radius=1
    g2: Circle CenterX=8 CenterY=6 CenterZ=0 NormalX=0 NormalY=0 NormalZ=1 AngleXU=0 Radius=1
    g3: BSplineCurve PolesCount=3 KnotsCount=2 Degree=2 IsPeriodic=0
    g4: GeomPoint X=0 Y=0 Z=0
    g5: GeomPoint X=8 Y=6 Z=0
    g6: LineSegment StartX=0 StartY=6 StartZ=0 EndX=8 EndY=6 EndZ=0
  constraints (14):
    c: Coincident(g0,g-1)
    c: Distance(g0) = 6
    c: Vertical(g0)
    c: Coincident(g3,g0)
    c: Weight(g1) = 1
    c: Equal(g1,g2)
    c: InternalAlignment(g1,g3)
    c: InternalAlignment(g2,g3)
    c: InternalAlignment(g4,g3)
    c: InternalAlignment(g5,g3)
    c: Block(g3)
    c: Coincident(g6,g0)
    c: Coincident(g6,g3)
    c: Horizontal(g6)
FEATURE [Part::Extrusion] Extrude034  label="caseScrewPillarBracket012"
  Base = -> Sketch043
  Dir = (0,0,1)
  DirMode = 2
  FaceMakerClass = Part::FaceMakerBullseye
  LengthFwd = 2.4
  LengthRev = 0
  Placement = pos=(88.3,29,65.23) rot=(0,1,0;1.5708rad)
  Solid = true
  Symmetric = false
FEATURE [Sketcher::SketchObject] Sketch044
  FullyConstrained = true
  sketch-geometry (7):
    g0: LineSegment StartX=0 StartY=0 StartZ=0 EndX=0 EndY=6 EndZ=0
    g1: Circle CenterX=0 CenterY=0 CenterZ=0 NormalX=0 NormalY=0 NormalZ=1 AngleXU=0 Radius=1
    g2: Circle CenterX=8 CenterY=6 CenterZ=0 NormalX=0 NormalY=0 NormalZ=1 AngleXU=0 Radius=1
    g3: BSplineCurve PolesCount=3 KnotsCount=2 Degree=2 IsPeriodic=0
    g4: GeomPoint X=0 Y=0 Z=0
    g5: GeomPoint X=8 Y=6 Z=0
    g6: LineSegment StartX=0 StartY=6 StartZ=0 EndX=8 EndY=6 EndZ=0
  constraints (14):
    c: Coincident(g0,g-1)
    c: Distance(g0) = 6
    c: Vertical(g0)
    c: Coincident(g3,g0)
    c: Weight(g1) = 1
    c: Equal(g1,g2)
    c: InternalAlignment(g1,g3)
    c: InternalAlignment(g2,g3)
    c: InternalAlignment(g4,g3)
    c: InternalAlignment(g5,g3)
    c: Block(g3)
    c: Coincident(g6,g0)
    c: Coincident(g6,g3)
    c: Horizontal(g6)
FEATURE [Part::Extrusion] Extrude035  label="caseScrewPillarBracket013"
  Base = -> Sketch044
  Dir = (0,0,1)
  DirMode = 2
  FaceMakerClass = Part::FaceMakerBullseye
  LengthFwd = 2.4
  LengthRev = 0
  Placement = pos=(90.7,29,6.77) rot=(0,-1,0;1.5708rad)
  Solid = true
  Symmetric = false
FEATURE [Sketcher::SketchObject] Sketch045
  FullyConstrained = true
  sketch-geometry (7):
    g0: LineSegment StartX=0 StartY=0 StartZ=0 EndX=0 EndY=6 EndZ=0
    g1: Circle CenterX=0 CenterY=0 CenterZ=0 NormalX=0 NormalY=0 NormalZ=1 AngleXU=0 Radius=1
    g2: Circle CenterX=8 CenterY=6 CenterZ=0 NormalX=0 NormalY=0 NormalZ=1 AngleXU=0 Radius=1
    g3: BSplineCurve PolesCount=3 KnotsCount=2 Degree=2 IsPeriodic=0
    g4: GeomPoint X=0 Y=0 Z=0
    g5: GeomPoint X=8 Y=6 Z=0
    g6: LineSegment StartX=0 StartY=6 StartZ=0 EndX=8 EndY=6 EndZ=0
  constraints (14):
    c: Coincident(g0,g-1)
    c: Distance(g0) = 6
    c: Vertical(g0)
    c: Coincident(g3,g0)
    c: Weight(g1) = 1
    c: Equal(g1,g2)
    c: InternalAlignment(g1,g3)
    c: InternalAlignment(g2,g3)
    c: InternalAlignment(g4,g3)
    c: InternalAlignment(g5,g3)
    c: Block(g3)
    c: Coincident(g6,g0)
    c: Coincident(g6,g3)
    c: Horizontal(g6)
FEATURE [Sketcher::SketchObject] Sketch046
  FullyConstrained = true
  sketch-geometry (7):
    g0: LineSegment StartX=0 StartY=0 StartZ=0 EndX=0 EndY=6 EndZ=0
    g1: Circle CenterX=0 CenterY=0 CenterZ=0 NormalX=0 NormalY=0 NormalZ=1 AngleXU=0 Radius=1
    g2: Circle CenterX=8 CenterY=6 CenterZ=0 NormalX=0 NormalY=0 NormalZ=1 AngleXU=0 Radius=1
    g3: BSplineCurve PolesCount=3 KnotsCount=2 Degree=2 IsPeriodic=0
    g4: GeomPoint X=0 Y=0 Z=0
    g5: GeomPoint X=8 Y=6 Z=0
    g6: LineSegment StartX=0 StartY=6 StartZ=0 EndX=8 EndY=6 EndZ=0
  constraints (14):
    c: Coincident(g0,g-1)
    c: Distance(g0) = 6
    c: Vertical(g0)
    c: Coincident(g3,g0)
    c: Weight(g1) = 1
    c: Equal(g1,g2)
    c: InternalAlignment(g1,g3)
    c: InternalAlignment(g2,g3)
    c: InternalAlignment(g4,g3)
    c: InternalAlignment(g5,g3)
    c: Block(g3)
    c: Coincident(g6,g0)
    c: Coincident(g6,g3)
    c: Horizontal(g6)
FEATURE [Part::Extrusion] Extrude036  label="caseScrewPillarBracket014"
  Base = -> Sketch045
  Dir = (0,0,1)
  DirMode = 2
  FaceMakerClass = Part::FaceMakerBullseye
  LengthFwd = 2.4
  LengthRev = 0
  Placement = pos=(110.7,29,6.77) rot=(0,-1,0;1.5708rad)
  Solid = true
  Symmetric = false
FEATURE [Part::Extrusion] Extrude037  label="caseScrewPillarBracket015"
  Base = -> Sketch046
  Dir = (0,0,1)
  DirMode = 2
  FaceMakerClass = Part::FaceMakerBullseye
  LengthFwd = 2.4
  LengthRev = 0
  Placement = pos=(108.3,29,65.23) rot=(0,1,0;1.5708rad)
  Solid = true
  Symmetric = false
FEATURE [Part::Box] Box013  label="frontCaseScrewPillarBracket002"
  AttacherType = Attacher::AttachEngine3D
  Height = 2.4
  Length = 22
  Placement = pos=(87,28,2.3) rot=(0,0,1;0rad)
  Width = 7
FEATURE [Part::Box] Box014  label="frontCaseScrewPillarBracket003"
  AttacherType = Attacher::AttachEngine3D
  Height = 2.4
  Length = 22
  Placement = pos=(87,28,67.3) rot=(0,0,1;0rad)
  Width = 7
FEATURE [Part::Feature] Face087
  shape: bbox 4.8 x 30.2 x 2e-07 mm, 1 faces, 0 solids (baked)
FEATURE [Part::Revolution] Revolve091  label="frontCaseScrewPost004"
  Angle = 360
  Axis = (0,1,0)
  Base = (0,0,0)
  FaceMakerClass = Part::FaceMakerBullseye
  Placement = pos=(89.5,4.5,3.5) rot=(0,0,1;0rad)
  Solid = false
  Source = -> Face087
  Symmetric = false
FEATURE [Part::Feature] Face088
  shape: bbox 4.8 x 30.2 x 2e-07 mm, 1 faces, 0 solids (baked)
FEATURE [Part::Revolution] Revolve092  label="frontCaseScrewPost005"
  Angle = 360
  Axis = (0,1,0)
  Base = (0,0,0)
  FaceMakerClass = Part::FaceMakerBullseye
  Placement = pos=(89.5,4.5,68.5) rot=(0,0,1;0rad)
  Solid = false
  Source = -> Face088
  Symmetric = false
FEATURE [Part::Feature] Face089
  shape: bbox 3.5 x 30.2 x 2e-07 mm, 1 faces, 0 solids (baked)
FEATURE [Part::Revolution] Revolve093  label="backCaseScrewPost002"
  Angle = 360
  Axis = (0,1,0)
  Base = (0,0,0)
  FaceMakerClass = Part::FaceMakerBullseye
  Placement = pos=(12.5,4.5,10) rot=(0,0,1;0rad)
  Solid = false
  Source = -> Face089
  Symmetric = false
FEATURE [Part::Feature] Face090
  shape: bbox 3.5 x 30.2 x 2e-07 mm, 1 faces, 0 solids (baked)
FEATURE [Part::Revolution] Revolve094  label="backCaseScrewPost003"
  Angle = 360
  Axis = (0,1,0)
  Base = (0,0,0)
  FaceMakerClass = Part::FaceMakerBullseye
  Placement = pos=(12.5,4.5,62) rot=(0,0,1;0rad)
  Solid = false
  Source = -> Face090
  Symmetric = false
FEATURE [Part::Box] Box015  label="Cube011"
  AttacherType = Attacher::AttachEngine3D
  Height = 28.8
  Length = 3
  Placement = pos=(107.3,28,21.6) rot=(0,0,1;0rad)
  Width = 7
FEATURE [Part::Box] Box016  label="Cube012"
  AttacherType = Attacher::AttachEngine3D
  Height = 3
  Length = 7.4
  Placement = pos=(107.3,28,18.6) rot=(0,0,1;0rad)
  Width = 7
FEATURE [Part::Box] Box017  label="Cube013"
  AttacherType = Attacher::AttachEngine3D
  Height = 3
  Length = 7.4
  Placement = pos=(107.3,28,50.4) rot=(0,0,1;0rad)
  Width = 7
FEATURE [Part::Cylinder] Cylinder024
  Angle = 360
  AttacherType = Attacher::AttachEngine3D
  Height = 20
  Placement = pos=(0,0,36.15) rot=(0,0,1;0rad)
  Radius = 14.3
FEATURE [Part::Cylinder] Cylinder025
  Angle = 360
  AttacherType = Attacher::AttachEngine3D
  Height = 10
  Placement = pos=(0,0,36.15) rot=(0,0,1;0rad)
  Radius = 4
FEATURE [Part::MultiFuse] Fusion066  label="removeToCreteHoleForPlugHousing009"
  Placement = pos=(70,19,36) rot=(0,1,0;1.5708rad)
  Shapes = -> [Cylinder024,Cylinder025]
FEATURE [Part::MultiFuse] Fusion065  label="plugHousingBracketHolder002"
  Shapes = -> [Box017,Box015,Box016]
FEATURE [Part::Cut] Cut025  label="plugHousingBracketHolder003"
  Base = -> Fusion065
  Placement = pos=(7,0,0) rot=(0,0,1;0rad)
  Tool = -> Fusion066
FEATURE [Sketcher::SketchObject] Sketch047
  FullyConstrained = false
  Placement = pos=(0,0,0) rot=(1,0,0;1.5708rad)
  sketch-geometry (24):
    g0: ArcOfCircle CenterX=-4 CenterY=-10.5 CenterZ=0 NormalX=0 NormalY=0 NormalZ=1 AngleXU=0 Radius=1.5 StartAngle=6e-16 EndAngle=3.14159
    g1: ArcOfCircle CenterX=-34.2 CenterY=-10.5 CenterZ=0 NormalX=0 NormalY=0 NormalZ=1 AngleXU=0 Radius=1.5 StartAngle=0 EndAngle=3.14159
    g2: ArcOfCircle CenterX=-34.2 CenterY=-27.7 CenterZ=0 NormalX=0 NormalY=0 NormalZ=1 AngleXU=0 Radius=1.5 StartAngle=3.14159 EndAngle=6.28319
    g3: ArcOfCircle CenterX=-4 CenterY=-27.7 CenterZ=0 NormalX=0 NormalY=0 NormalZ=1 AngleXU=0 Radius=1.5 StartAngle=3.1416 EndAngle=6.28319
    g4: ArcOfCircle CenterX=-10 CenterY=-4.3 CenterZ=0 NormalX=0 NormalY=0 NormalZ=1 AngleXU=0 Radius=1.5 StartAngle=2e-16 EndAngle=3.14159
    g5: ArcOfCircle CenterX=-16.1 CenterY=-1.8 CenterZ=0 NormalX=0 NormalY=0 NormalZ=1 AngleXU=0 Radius=1.5 StartAngle=5e-16 EndAngle=3.14159
    g6: ArcOfCircle CenterX=-22.1 CenterY=-1.8 CenterZ=0 NormalX=0 NormalY=0 NormalZ=1 AngleXU=0 Radius=1.5 StartAngle=5e-16 EndAngle=3.14159
    g7: ArcOfCircle CenterX=-28.2 CenterY=-4.3 CenterZ=0 NormalX=0 NormalY=0 NormalZ=1 AngleXU=0 Radius=1.5 StartAngle=2e-16 EndAngle=3.14159
    g8: ArcOfCircle CenterX=-10 CenterY=-33.9 CenterZ=0 NormalX=0 NormalY=0 NormalZ=1 AngleXU=0 Radius=1.5 StartAngle=3.14159 EndAngle=6.28319
    g9: ArcOfCircle CenterX=-16.1 CenterY=-36.4 CenterZ=0 NormalX=0 NormalY=0 NormalZ=1 AngleXU=0 Radius=1.5 StartAngle=3.14159 EndAngle=6.28319
    g10: ArcOfCircle CenterX=-22.1 CenterY=-36.4 CenterZ=0 NormalX=0 NormalY=0 NormalZ=1 AngleXU=0 Radius=1.5 StartAngle=3.14159 EndAngle=6.28319
    g11: ArcOfCircle CenterX=-28.2 CenterY=-33.9 CenterZ=0 NormalX=0 NormalY=0 NormalZ=1 AngleXU=0 Radius=1.5 StartAngle=3.14159 EndAngle=6.28319
    g12: LineSegment StartX=-35.7 StartY=-10.5 StartZ=0 EndX=-35.7 EndY=-27.7 EndZ=0
    g13: LineSegment StartX=-32.7 StartY=-10.5 StartZ=0 EndX=-32.7 EndY=-27.7 EndZ=0
    g14: LineSegment StartX=-29.7 StartY=-33.9 StartZ=0 EndX=-29.7 EndY=-4.3 EndZ=0
    g15: LineSegment StartX=-26.7 StartY=-33.9 StartZ=0 EndX=-26.7 EndY=-4.3 EndZ=0
    g16: LineSegment StartX=-2.5 StartY=-10.5 StartZ=0 EndX=-2.5 EndY=-27.7 EndZ=0
    g17: LineSegment StartX=-8.5 StartY=-4.3 StartZ=0 EndX=-8.5 EndY=-33.9 EndZ=0
    g18: LineSegment StartX=-5.5 StartY=-10.5 StartZ=0 EndX=-5.5 EndY=-27.7 EndZ=0
    g19: LineSegment StartX=-11.5 StartY=-4.3 StartZ=0 EndX=-11.5 EndY=-33.9 EndZ=0
    g20: LineSegment StartX=-14.6 StartY=-1.8 StartZ=0 EndX=-14.6 EndY=-36.4 EndZ=0
    g21: LineSegment StartX=-17.6 StartY=-1.8 StartZ=0 EndX=-17.6 EndY=-36.4 EndZ=0
    g22: LineSegment StartX=-20.6 StartY=-36.4 StartZ=0 EndX=-20.6 EndY=-1.8 EndZ=0
    g23: LineSegment StartX=-23.6 StartY=-1.8 StartZ=0 EndX=-23.6 EndY=-36.4 EndZ=0
  constraints (48):
    c: Block(g0)
    c: Block(g1)
    c: Block(g2)
    c: Block(g3)
    c: Block(g4)
    c: Block(g5)
    c: Block(g6)
    c: Block(g7)
    c: Block(g8)
    c: Block(g9)
    c: Block(g10)
    c: Block(g11)
    c: Coincident(g12,g1)
    c: Coincident(g12,g2)
    c: Vertical(g12)
    c: Coincident(g13,g1)
    c: Coincident(g13,g2)
    c: Vertical(g13)
    c: Coincident(g14,g11)
    c: Coincident(g14,g7)
    c: Vertical(g14)
    c: Coincident(g15,g11)
    c: Coincident(g15,g7)
    c: Vertical(g15)
    c: Coincident(g16,g0)
    c: Coincident(g16,g3)
    c: Vertical(g16)
    c: Coincident(g17,g4)
    c: Coincident(g17,g8)
    c: Vertical(g17)
    c: Coincident(g18,g0)
    c: Coincident(g18,g3)
    c: Vertical(g18)
    c: Coincident(g19,g4)
    c: Coincident(g19,g8)
    c: Vertical(g19)
    c: Coincident(g20,g5)
    c: Coincident(g20,g9)
    c: Vertical(g20)
    c: Coincident(g21,g5)
    c: Coincident(g21,g9)
    c: Vertical(g21)
    c: Coincident(g22,g10)
    c: Coincident(g22,g6)
    c: Vertical(g22)
    c: Coincident(g23,g6)
    c: Coincident(g23,g10)
    c: Vertical(g23)
FEATURE [Part::Extrusion] Extrude038  label="removeToCreateFanGrillHoles001"
  Base = -> Sketch047
  Dir = (0,-1,6e-16)
  DirMode = 2
  FaceMakerClass = Part::FaceMakerBullseye
  LengthFwd = 10
  LengthRev = 0
  Placement = pos=(65.4,44,54.82) rot=(0,0,1;0rad)
  Solid = true
  Symmetric = false
FEATURE [Part::Feature] Wire004
  shape: bbox 11 x 5.2 x 2e-07 mm, 0 faces, 0 solids (baked)
FEATURE [Part::Revolution] Revolve095
  Angle = 360
  Axis = (0,1,0)
  Base = (0,0,0)
  FaceMakerClass = Part::FaceMakerBullseye
  Placement = pos=(30.3,38,19.7) rot=(0,0,1;0rad)
  Solid = true
  Source = -> Wire004
  Symmetric = false
FEATURE [Part::Feature] Wire005
  shape: bbox 11 x 5.2 x 2e-07 mm, 0 faces, 0 solids (baked)
FEATURE [Part::Revolution] Revolve096
  Angle = 360
  Axis = (0,1,0)
  Base = (0,0,0)
  FaceMakerClass = Part::FaceMakerBullseye
  Placement = pos=(30.3,38,51.7) rot=(0,0,1;0rad)
  Solid = true
  Source = -> Wire005
  Symmetric = false
FEATURE [Part::Feature] Wire006
  shape: bbox 11 x 5.2 x 2e-07 mm, 0 faces, 0 solids (baked)
FEATURE [Part::Revolution] Revolve097
  Angle = 360
  Axis = (0,1,0)
  Base = (0,0,0)
  FaceMakerClass = Part::FaceMakerBullseye
  Placement = pos=(62.3,38,51.7) rot=(0,0,1;0rad)
  Solid = true
  Source = -> Wire006
  Symmetric = false
FEATURE [Part::Feature] Wire007
  shape: bbox 11 x 5.2 x 2e-07 mm, 0 faces, 0 solids (baked)
FEATURE [Part::Revolution] Revolve098
  Angle = 360
  Axis = (0,1,0)
  Base = (0,0,0)
  FaceMakerClass = Part::FaceMakerBullseye
  Placement = pos=(62.3,38,19.7) rot=(0,0,1;0rad)
  Solid = true
  Source = -> Wire007
  Symmetric = false
FEATURE [Part::MultiFuse] Fusion067  label="fanScrewHousing002"
  Shapes = -> [Revolve098,Revolve097,Revolve096,Revolve095]
FEATURE [Part::Feature] Face091 .. Face094  x4 (patterned run collapsed; names and placements below)
  shape: bbox 3.5 x 17.8 x 2e-07 mm, 1 faces, 0 solids (baked)
FEATURE [Part::Revolution] Revolve099  label="removeToCreateScrewAndThreadedInsertHole026"
  Angle = 360
  Axis = (0,1,0)
  Base = (0,0,0)
  FaceMakerClass = Part::FaceMakerBullseye
  Placement = pos=(62.3,30.3,19.7) rot=(0,0,1;0rad)
  Solid = false
  Source = -> Face091
  Symmetric = false
FEATURE [Part::Revolution] Revolve100  label="removeToCreateScrewAndThreadedInsertHole027"
  Angle = 360
  Axis = (0,1,0)
  Base = (0,0,0)
  FaceMakerClass = Part::FaceMakerBullseye
  Placement = pos=(62.3,30.3,51.7) rot=(0,0,1;0rad)
  Solid = false
  Source = -> Face092
  Symmetric = false
FEATURE [Part::Revolution] Revolve101  label="removeToCreateScrewAndThreadedInsertHole028"
  Angle = 360
  Axis = (0,1,0)
  Base = (0,0,0)
  FaceMakerClass = Part::FaceMakerBullseye
  Placement = pos=(30.3,30.3,19.7) rot=(0,0,1;0rad)
  Solid = false
  Source = -> Face093
  Symmetric = false
FEATURE [Part::Revolution] Revolve102  label="removeToCreateScrewAndThreadedInsertHole029"
  Angle = 360
  Axis = (0,1,0)
  Base = (0,0,0)
  FaceMakerClass = Part::FaceMakerBullseye
  Placement = pos=(30.3,30.3,51.7) rot=(0,0,1;0rad)
  Solid = false
  Source = -> Face094
  Symmetric = false
FEATURE [Part::MultiFuse] Fusion068  label="createThreadedInsertHolesForFan002"
  Shapes = -> [Revolve099,Revolve100,Revolve101,Revolve102]
FEATURE [Part::Cut] Cut026  label="fanScrewHousing003"
  Base = -> Fusion067
  Tool = -> Fusion068
FEATURE [Sketcher::SketchObject] Sketch048
  FullyConstrained = false
  Placement = pos=(0,0,0) rot=(1,0,0;1.5708rad)
  sketch-geometry (24):
    g0: ArcOfCircle CenterX=-4 CenterY=-10.5 CenterZ=0 NormalX=0 NormalY=0 NormalZ=1 AngleXU=0 Radius=1.5 StartAngle=6e-16 EndAngle=3.14159
    g1: ArcOfCircle CenterX=-34.2 CenterY=-10.5 CenterZ=0 NormalX=0 NormalY=0 NormalZ=1 AngleXU=0 Radius=1.5 StartAngle=0 EndAngle=3.14159
    g2: ArcOfCircle CenterX=-34.2 CenterY=-27.7 CenterZ=0 NormalX=0 NormalY=0 NormalZ=1 AngleXU=0 Radius=1.5 StartAngle=3.14159 EndAngle=6.28319
    g3: ArcOfCircle CenterX=-4 CenterY=-27.7 CenterZ=0 NormalX=0 NormalY=0 NormalZ=1 AngleXU=0 Radius=1.5 StartAngle=3.1416 EndAngle=6.28319
    g4: ArcOfCircle CenterX=-10 CenterY=-4.3 CenterZ=0 NormalX=0 NormalY=0 NormalZ=1 AngleXU=0 Radius=1.5 StartAngle=2e-16 EndAngle=3.14159
    g5: ArcOfCircle CenterX=-16.1 CenterY=-1.8 CenterZ=0 NormalX=0 NormalY=0 NormalZ=1 AngleXU=0 Radius=1.5 StartAngle=5e-16 EndAngle=3.14159
    g6: ArcOfCircle CenterX=-22.1 CenterY=-1.8 CenterZ=0 NormalX=0 NormalY=0 NormalZ=1 AngleXU=0 Radius=1.5 StartAngle=5e-16 EndAngle=3.14159
    g7: ArcOfCircle CenterX=-28.2 CenterY=-4.3 CenterZ=0 NormalX=0 NormalY=0 NormalZ=1 AngleXU=0 Radius=1.5 StartAngle=2e-16 EndAngle=3.14159
    g8: ArcOfCircle CenterX=-10 CenterY=-33.9 CenterZ=0 NormalX=0 NormalY=0 NormalZ=1 AngleXU=0 Radius=1.5 StartAngle=3.14159 EndAngle=6.28319
    g9: ArcOfCircle CenterX=-16.1 CenterY=-36.4 CenterZ=0 NormalX=0 NormalY=0 NormalZ=1 AngleXU=0 Radius=1.5 StartAngle=3.14159 EndAngle=6.28319
    g10: ArcOfCircle CenterX=-22.1 CenterY=-36.4 CenterZ=0 NormalX=0 NormalY=0 NormalZ=1 AngleXU=0 Radius=1.5 StartAngle=3.14159 EndAngle=6.28319
    g11: ArcOfCircle CenterX=-28.2 CenterY=-33.9 CenterZ=0 NormalX=0 NormalY=0 NormalZ=1 AngleXU=0 Radius=1.5 StartAngle=3.14159 EndAngle=6.28319
    g12: LineSegment StartX=-35.7 StartY=-10.5 StartZ=0 EndX=-35.7 EndY=-27.7 EndZ=0
    g13: LineSegment StartX=-32.7 StartY=-10.5 StartZ=0 EndX=-32.7 EndY=-27.7 EndZ=0
    g14: LineSegment StartX=-29.7 StartY=-33.9 StartZ=0 EndX=-29.7 EndY=-4.3 EndZ=0
    g15: LineSegment StartX=-26.7 StartY=-33.9 StartZ=0 EndX=-26.7 EndY=-4.3 EndZ=0
    g16: LineSegment StartX=-2.5 StartY=-10.5 StartZ=0 EndX=-2.5 EndY=-27.7 EndZ=0
    g17: LineSegment StartX=-8.5 StartY=-4.3 StartZ=0 EndX=-8.5 EndY=-33.9 EndZ=0
    g18: LineSegment StartX=-5.5 StartY=-10.5 StartZ=0 EndX=-5.5 EndY=-27.7 EndZ=0
    g19: LineSegment StartX=-11.5 StartY=-4.3 StartZ=0 EndX=-11.5 EndY=-33.9 EndZ=0
    g20: LineSegment StartX=-14.6 StartY=-1.8 StartZ=0 EndX=-14.6 EndY=-36.4 EndZ=0
    g21: LineSegment StartX=-17.6 StartY=-1.8 StartZ=0 EndX=-17.6 EndY=-36.4 EndZ=0
    g22: LineSegment StartX=-20.6 StartY=-36.4 StartZ=0 EndX=-20.6 EndY=-1.8 EndZ=0
    g23: LineSegment StartX=-23.6 StartY=-1.8 StartZ=0 EndX=-23.6 EndY=-36.4 EndZ=0
  constraints (48):
    c: Block(g0)
    c: Block(g1)
    c: Block(g2)
    c: Block(g3)
    c: Block(g4)
    c: Block(g5)
    c: Block(g6)
    c: Block(g7)
    c: Block(g8)
    c: Block(g9)
    c: Block(g10)
    c: Block(g11)
    c: Coincident(g12,g1)
    c: Coincident(g12,g2)
    c: Vertical(g12)
    c: Coincident(g13,g1)
    c: Coincident(g13,g2)
    c: Vertical(g13)
    c: Coincident(g14,g11)
    c: Coincident(g14,g7)
    c: Vertical(g14)
    c: Coincident(g15,g11)
    c: Coincident(g15,g7)
    c: Vertical(g15)
    c: Coincident(g16,g0)
    c: Coincident(g16,g3)
    c: Vertical(g16)
    c: Coincident(g17,g4)
    c: Coincident(g17,g8)
    c: Vertical(g17)
    c: Coincident(g18,g0)
    c: Coincident(g18,g3)
    c: Vertical(g18)
    c: Coincident(g19,g4)
    c: Coincident(g19,g8)
    c: Vertical(g19)
    c: Coincident(g20,g5)
    c: Coincident(g20,g9)
    c: Vertical(g20)
    c: Coincident(g21,g5)
    c: Coincident(g21,g9)
    c: Vertical(g21)
    c: Coincident(g22,g10)
    c: Coincident(g22,g6)
    c: Vertical(g22)
    c: Coincident(g23,g6)
    c: Coincident(g23,g10)
    c: Vertical(g23)
FEATURE [Part::Extrusion] Extrude039  label="removeToCreateFanGrillHoles002"
  Base = -> Sketch048
  Dir = (0,-1,6e-16)
  DirMode = 2
  FaceMakerClass = Part::FaceMakerBullseye
  LengthFwd = 10
  LengthRev = 0
  Placement = pos=(65.4,44,54.82) rot=(0,0,1;0rad)
  Solid = true
  Symmetric = false
FEATURE [Part::Cut] Cut027  label="fanScrewHousing004"
  Base = -> Cut026
  Tool = -> Extrude038
FEATURE [Part::Cut] Cut028  label="top014"
  Base = -> Fillet026
  Tool = -> Extrude039
FEATURE [Part::Feature] Face095 .. Face098  x4 (patterned run collapsed; names and placements below)
  shape: bbox 3.5 x 17.8 x 2e-07 mm, 1 faces, 0 solids (baked)
FEATURE [Part::Revolution] Revolve103  label="removeToCreateScrewAndThreadedInsertHole030"
  Angle = 360
  Axis = (0,1,0)
  Base = (0,0,0)
  FaceMakerClass = Part::FaceMakerBullseye
  Placement = pos=(62.3,30.3,19.7) rot=(0,0,1;0rad)
  Solid = false
  Source = -> Face095
  Symmetric = false
FEATURE [Part::Revolution] Revolve104  label="removeToCreateScrewAndThreadedInsertHole031"
  Angle = 360
  Axis = (0,1,0)
  Base = (0,0,0)
  FaceMakerClass = Part::FaceMakerBullseye
  Placement = pos=(62.3,30.3,51.7) rot=(0,0,1;0rad)
  Solid = false
  Source = -> Face096
  Symmetric = false
FEATURE [Part::Revolution] Revolve105  label="removeToCreateScrewAndThreadedInsertHole032"
  Angle = 360
  Axis = (0,1,0)
  Base = (0,0,0)
  FaceMakerClass = Part::FaceMakerBullseye
  Placement = pos=(30.3,30.3,19.7) rot=(0,0,1;0rad)
  Solid = false
  Source = -> Face097
  Symmetric = false
FEATURE [Part::Revolution] Revolve106  label="removeToCreateScrewAndThreadedInsertHole033"
  Angle = 360
  Axis = (0,1,0)
  Base = (0,0,0)
  FaceMakerClass = Part::FaceMakerBullseye
  Placement = pos=(30.3,30.3,51.7) rot=(0,0,1;0rad)
  Solid = false
  Source = -> Face098
  Symmetric = false
FEATURE [Part::MultiFuse] Fusion069  label="createThreadedInsertHolesForFan003"
  Shapes = -> [Revolve103,Revolve104,Revolve105,Revolve106]
FEATURE [Part::Cut] Cut029  label="top015"
  Base = -> Cut028
  Tool = -> Fusion054
FEATURE [Part::Cut] Cut030  label="fanScrewHousing005"
  Base = -> Cut027
  Tool = -> Fusion069
FEATURE [Part::Cylinder] Cylinder026  label="removeToCreteHoleForPlugHousing010"
  Angle = 360
  AttacherType = Attacher::AttachEngine3D
  Height = 20
  Placement = pos=(-2,19,36) rot=(0,1,0;1.5708rad)
  Radius = 14.3
FEATURE [Part::Box] Box018  label="removeToCreteHoleForPlugHousing011"
  AttacherType = Attacher::AttachEngine3D
  Height = 28.6
  Length = 10
  Placement = pos=(-2,0,21.7) rot=(0,0,1;0rad)
  Width = 19
FEATURE [Part::Box] Box019  label="wireHolderBottomCaseBit"
  AttacherType = Attacher::AttachEngine3D
  Height = 28
  Length = 3
  Placement = pos=(0,0,22) rot=(0,0,1;0rad)
  Width = 21
FEATURE [Part::Cylinder] Cylinder027  label="removeToCreteHoleForPlugHousing012"
  Angle = 360
  AttacherType = Attacher::AttachEngine3D
  Height = 20
  Placement = pos=(-2,19,36) rot=(0,1,0;1.5708rad)
  Radius = 14.3
FEATURE [Part::Cut] Cut031  label="wireHolderBottomCaseBit001"
  Base = -> Box019
  Tool = -> Cylinder027
FEATURE [Part::MultiFuse] Fusion070  label="removeToCreteHoleForPlugHousing013"
  Shapes = -> [Box018,Cylinder026]
FEATURE [Part::Cut] Cut032  label="top016"
  Base = -> Cut029
  Tool = -> Fusion070
FEATURE [Part::Cylinder] Cylinder028
  Angle = 360
  AttacherType = Attacher::AttachEngine3D
  Height = 20
  Placement = pos=(0,0,36.15) rot=(0,0,1;0rad)
  Radius = 14.3
FEATURE [Part::Cylinder] Cylinder029
  Angle = 360
  AttacherType = Attacher::AttachEngine3D
  Height = 10
  Placement = pos=(0,0,36.15) rot=(0,0,1;0rad)
  Radius = 4
FEATURE [Part::MultiFuse] Fusion071  label="removeToCreteHoleForPlugHousing014"
  Placement = pos=(70,19,36) rot=(0,1,0;1.5708rad)
  Shapes = -> [Cylinder028,Cylinder029]
FEATURE [Sketcher::SketchObject] Sketch049  label="topSketch011"
  FullyConstrained = true
  sketch-geometry (4):
    g0: ArcOfCircle CenterX=105 CenterY=19 CenterZ=0 NormalX=0 NormalY=0 NormalZ=1 AngleXU=0 Radius=20.6155 StartAngle=5.54125 EndAngle=6.28319
    g1: ArcOfCircle CenterX=105 CenterY=19 CenterZ=0 NormalX=0 NormalY=0 NormalZ=1 AngleXU=0 Radius=13 StartAngle=5.54125 EndAngle=6.28319
    g2: LineSegment StartX=118 StartY=19 StartZ=0 EndX=125.616 EndY=19 EndZ=0
    g3: LineSegment StartX=114.583 StartY=10.2157 StartZ=0 EndX=120.197 EndY=5.06982 EndZ=0
  constraints (7):
    c: Block(g0)
    c: Block(g1)
    c: Coincident(g2,g1)
    c: Coincident(g2,g0)
    c: Horizontal(g2)
    c: Coincident(g3,g1)
    c: Coincident(g3,g0)
FEATURE [Part::Box] Box020  label="removeToCreteHoleForPlugHousing015"
  AttacherType = Attacher::AttachEngine3D
  Height = 28.6
  Length = 20
  Placement = pos=(106.15,0,21.7) rot=(0,0,1;0rad)
  Width = 19
FEATURE [Part::MultiFuse] Fusion072  label="removeToCreteHoleForPlugHousing016"
  Shapes = -> [Box020,Fusion071]
FEATURE [Part::Cut] Cut033  label="removeToCreteHoleForPlugHousing017"
  Base = -> Cut032
  Tool = -> Fusion072
FEATURE [Part::Cylinder] Cylinder030
  Angle = 360
  AttacherType = Attacher::AttachEngine3D
  Height = 20
  Placement = pos=(0,0,36.15) rot=(0,0,1;0rad)
  Radius = 14.3
FEATURE [Part::Cylinder] Cylinder031
  Angle = 360
  AttacherType = Attacher::AttachEngine3D
  Height = 10
  Placement = pos=(0,0,36.15) rot=(0,0,1;0rad)
  Radius = 4
FEATURE [Part::Box] Box021  label="removeToCreteHoleForPlugHousing019"
  AttacherType = Attacher::AttachEngine3D
  Height = 28.6
  Length = 20
  Placement = pos=(106.15,0,21.7) rot=(0,0,1;0rad)
  Width = 19
FEATURE [Part::MultiFuse] Fusion074  label="removeToCreteHoleForPlugHousing020"
  Placement = pos=(70,19,36) rot=(0,1,0;1.5708rad)
  Shapes = -> [Cylinder030,Cylinder031]
FEATURE [Part::MultiFuse] Fusion073  label="removeToCreteHoleForPlugHousing018"
  Placement = pos=(0,0,28.3) rot=(0,0,1;0rad)
  Shapes = -> [Box021,Fusion074]
FEATURE [Part::Cylinder] Cylinder032
  Angle = 360
  AttacherType = Attacher::AttachEngine3D
  Height = 20
  Placement = pos=(0,0,36.15) rot=(0,0,1;0rad)
  Radius = 14.3
FEATURE [Part::Cylinder] Cylinder033
  Angle = 360
  AttacherType = Attacher::AttachEngine3D
  Height = 10
  Placement = pos=(0,0,36.15) rot=(0,0,1;0rad)
  Radius = 4
FEATURE [Part::Box] Box022  label="removeToCreteHoleForPlugHousing021"
  AttacherType = Attacher::AttachEngine3D
  Height = 28.6
  Length = 20
  Placement = pos=(106.15,0,21.7) rot=(0,0,1;0rad)
  Width = 19
FEATURE [Part::MultiFuse] Fusion076  label="removeToCreteHoleForPlugHousing023"
  Placement = pos=(70,19,36) rot=(0,1,0;1.5708rad)
  Shapes = -> [Cylinder032,Cylinder033]
FEATURE [Part::MultiFuse] Fusion075  label="removeToCreteHoleForPlugHousing022"
  Placement = pos=(0,0,-28.3) rot=(0,0,1;0rad)
  Shapes = -> [Box022,Fusion076]
FEATURE [Part::MultiFuse] Fusion077  label="removeToCreatePlugHousingBottomBit"
  Shapes = -> [Fusion075,Fusion073]
FEATURE [Part::Cylinder] Cylinder034
  Angle = 360
  AttacherType = Attacher::AttachEngine3D
  Height = 20
  Placement = pos=(0,0,36.15) rot=(0,0,1;0rad)
  Radius = 14
FEATURE [Part::Cylinder] Cylinder035
  Angle = 360
  AttacherType = Attacher::AttachEngine3D
  Height = 10
  Placement = pos=(0,0,36.15) rot=(0,0,1;0rad)
  Radius = 4
FEATURE [Part::MultiFuse] Fusion078  label="removeToCreteHoleForPlugHousing024"
  Placement = pos=(70,19,36) rot=(0,1,0;1.5708rad)
  Shapes = -> [Cylinder034,Cylinder035]
FEATURE [Part::MultiFuse] Fusion079  label="removeToCreatePlugHousingBottomBit001"
  Shapes = -> [Fusion078,Fusion077]
FEATURE [Part::Extrusion] Extrude040  label="bottomPlugHousingBit"
  Base = -> Sketch049
  Dir = (0,0,1)
  DirMode = 2
  FaceMakerClass = Part::FaceMakerBullseye
  LengthFwd = 72
  LengthRev = 0
  Solid = true
  Symmetric = false
FEATURE [Part::Cut] Cut034  label="bottomPlugHousingBit001"
  Base = -> Extrude040
  Placement = pos=(-0.09,0,0) rot=(0,0,1;0rad)
  Tool = -> Fusion079
FEATURE [Part::Box] Box023  label="Cube014"
  AttacherType = Attacher::AttachEngine3D
  Height = 16
  Length = 8
  Placement = pos=(12.7,31.52,28) rot=(0,0,1;0rad)
  Width = 4
FEATURE [Part::Cylinder] Cylinder036
  Angle = 360
  AttacherType = Attacher::AttachEngine3D
  Height = 10
  Placement = pos=(0,0,36.15) rot=(0,0,1;0rad)
  Radius = 4
FEATURE [Part::Cylinder] Cylinder037
  Angle = 360
  AttacherType = Attacher::AttachEngine3D
  Height = 20
  Placement = pos=(0,0,36.15) rot=(0,0,1;0rad)
  Radius = 8.2
FEATURE [Part::MultiFuse] Fusion080  label="removeToCreteHoleForPlugHousing025"
  Placement = pos=(-42,19,36) rot=(0,1,0;1.5708rad)
  Shapes = -> [Cylinder037,Cylinder036]
FEATURE [Sketcher::SketchObject] Sketch050  label="topSketch012"
  FullyConstrained = true
  sketch-geometry (4):
    g0: LineSegment StartX=16.8446 StartY=31.512 StartZ=0 EndX=16.3251 EndY=34.4666 EndZ=0
    g1: ArcOfCircle CenterX=19 CenterY=19.2524 CenterZ=0 NormalX=0 NormalY=0 NormalZ=1 AngleXU=0 Radius=15.4476 StartAngle=1.74483 EndAngle=2.72717
    g2: ArcOfCircle CenterX=19 CenterY=19.2524 CenterZ=0 NormalX=0 NormalY=0 NormalZ=1 AngleXU=0 Radius=12.4476 StartAngle=1.74483 EndAngle=2.73189
    g3: LineSegment StartX=4.86004 StartY=25.4725 StartZ=0 EndX=7.58253 EndY=24.2107 EndZ=0
  constraints (7):
    c: Block(g0)
    c: Coincident(g1,g0)
    c: Coincident(g2,g0)
    c: Coincident(g3,g1)
    c: Coincident(g3,g2)
    c: Block(g1)
    c: Block(g2)
FEATURE [Part::Extrusion] Extrude041
  Base = -> Sketch050
  Dir = (0,0,1)
  DirMode = 2
  FaceMakerClass = Part::FaceMakerBullseye
  LengthFwd = 10.6
  LengthRev = 0
  Placement = pos=(0,0,31) rot=(0,0,1;0rad)
  Solid = true
  Symmetric = false
FEATURE [Part::Cut] Cut035
  Base = -> Extrude041
  Placement = pos=(0,0,-0.3) rot=(0,0,1;0rad)
  Tool = -> Fusion080
FEATURE [Part::Cut] Cut036
  Base = -> Box023
  Tool = -> Cut035
FEATURE [Part::Fillet] Fillet027
  Base = -> Cut036
  Edges = 1 edges r=0.7: [Edge13]
FEATURE [Part::Fillet] Fillet028
  Base = -> Fillet027
  Edges = 1 edges r=0.7: [Edge13]
FEATURE [Part::Fillet] Fillet029
  Base = -> Fillet028
  Edges = 1 edges r=0.7: [Edge16]
FEATURE [Part::Fillet] Fillet030
  Base = -> Fillet029
  Edges = 1 edges r=0.7: [Edge11]
FEATURE [Part::Fillet] Fillet031
  Base = -> Fillet030
  Edges = 1 edges r=0.7: [Edge10]
FEATURE [Part::Fillet] Fillet032
  Base = -> Fillet031
  Edges = 1 edges r=1.2: [Edge5]
FEATURE [Part::Fillet] Fillet033
  Base = -> Fillet032
  Edges = 1 edges r=1.2: [Edge12]
FEATURE [Part::Fillet] Fillet034  label="wireHousingRetainer"
  Base = -> Fillet033
  Edges = 1 edges r=2: [Edge1]
  Placement = pos=(0.3,0,0) rot=(0,0,1;0rad)
FEATURE [Part::Feature] Face099
  shape: bbox 3.5 x 17.8 x 2e-07 mm, 1 faces, 0 solids (baked)
FEATURE [Part::Revolution] Revolve107  label="removeToCreateScrewAndThreadedInsertHole034"
  Angle = 360
  Axis = (0,1,0)
  Base = (0,0,0)
  FaceMakerClass = Part::FaceMakerBullseye
  Placement = pos=(12.5,0,10) rot=(0,0,1;0rad)
  Solid = false
  Source = -> Face099
  Symmetric = false
FEATURE [Part::Feature] Face100
  shape: bbox 3.5 x 17.8 x 2e-07 mm, 1 faces, 0 solids (baked)
FEATURE [Part::Revolution] Revolve108  label="removeToCreateScrewAndThreadedInsertHole035"
  Angle = 360
  Axis = (0,1,0)
  Base = (0,0,0)
  FaceMakerClass = Part::FaceMakerBullseye
  Placement = pos=(12.5,0,62) rot=(0,0,1;0rad)
  Solid = false
  Source = -> Face100
  Symmetric = false
FEATURE [Part::Feature] Face101
  shape: bbox 3.5 x 17.8 x 2e-07 mm, 1 faces, 0 solids (baked)
FEATURE [Part::Revolution] Revolve109  label="removeToCreateScrewAndThreadedInsertHole036"
  Angle = 360
  Axis = (0,1,0)
  Base = (0,0,0)
  FaceMakerClass = Part::FaceMakerBullseye
  Placement = pos=(89.5,0,68.5) rot=(0,0,1;0rad)
  Solid = false
  Source = -> Face101
  Symmetric = false
FEATURE [Part::Feature] Face102
  shape: bbox 3.5 x 17.8 x 2e-07 mm, 1 faces, 0 solids (baked)
FEATURE [Part::Revolution] Revolve110  label="removeToCreateScrewAndThreadedInsertHole037"
  Angle = 360
  Axis = (0,1,0)
  Base = (0,0,0)
  FaceMakerClass = Part::FaceMakerBullseye
  Placement = pos=(89.5,0,3.5) rot=(0,0,1;0rad)
  Solid = false
  Source = -> Face102
  Symmetric = false
FEATURE [Part::Feature] Face103
  shape: bbox 3.5 x 17.8 x 2e-07 mm, 1 faces, 0 solids (baked)
FEATURE [Part::Revolution] Revolve111  label="removeToCreateScrewAndThreadedInsertHole038"
  Angle = 360
  Axis = (0,1,0)
  Base = (0,0,0)
  FaceMakerClass = Part::FaceMakerBullseye
  Placement = pos=(109.5,4.7,3.5) rot=(0,0,1;0rad)
  Solid = false
  Source = -> Face103
  Symmetric = false
FEATURE [Part::Feature] Face104
  shape: bbox 3.5 x 17.8 x 2e-07 mm, 1 faces, 0 solids (baked)
FEATURE [Part::Revolution] Revolve112  label="removeToCreateScrewAndThreadedInsertHole039"
  Angle = 360
  Axis = (0,1,0)
  Base = (0,0,0)
  FaceMakerClass = Part::FaceMakerBullseye
  Placement = pos=(109.5,4.7,68.5) rot=(0,0,1;0rad)
  Solid = false
  Source = -> Face104
  Symmetric = false
FEATURE [Part::MultiFuse] Fusion081  label="removeToCreateScrewAndThreadedInsertHole040"
  Shapes = -> [Revolve107,Revolve108,Revolve109,Revolve110,Revolve111,Revolve112]
FEATURE [Part::MultiFuse] Fusion082  label="casePillars002"
  Shapes = -> [Revolve094,Revolve092,Revolve090,Revolve089,Revolve091,Revolve093]
FEATURE [Part::Cut] Cut037  label="casePillars003"
  Base = -> Fusion082
  Tool = -> Fusion081
FEATURE [Sketcher::SketchObject] Sketch051
  FullyConstrained = true
  Placement = pos=(117,19,0) rot=(0.57735,0.57735,0.57735;2.0944rad)
  sketch-geometry (48):
    g0: LineSegment StartX=-49.19 StartY=69.25 StartZ=0 EndX=-49.19 EndY=66.25 EndZ=0
    g1: LineSegment StartX=-49.19 StartY=63.5 StartZ=0 EndX=-49.19 EndY=60.5 EndZ=0
    g2: LineSegment StartX=-49.19 StartY=57.75 StartZ=0 EndX=-49.19 EndY=54.75 EndZ=0
    g3: LineSegment StartX=-49.19 StartY=52 StartZ=0 EndX=-49.19 EndY=49 EndZ=0
    g4: LineSegment StartX=-49.19 StartY=46.25 StartZ=0 EndX=-49.19 EndY=43.25 EndZ=0
    g5: LineSegment StartX=-49.19 StartY=40.5 StartZ=0 EndX=-49.19 EndY=37.5 EndZ=0
    g6: LineSegment StartX=-49.19 StartY=34.5 StartZ=0 EndX=-49.19 EndY=31.5 EndZ=0
    g7: LineSegment StartX=-49.19 StartY=28.75 StartZ=0 EndX=-49.19 EndY=25.75 EndZ=0
    g8: LineSegment StartX=-49.19 StartY=23 StartZ=0 EndX=-49.19 EndY=20 EndZ=0
    g9: LineSegment StartX=-49.19 StartY=17.25 StartZ=0 EndX=-49.19 EndY=14.25 EndZ=0
    g10: LineSegment StartX=-49.19 StartY=11.5 StartZ=0 EndX=-49.19 EndY=8.5 EndZ=0
    g11: LineSegment StartX=-49.19 StartY=5.75 StartZ=0 EndX=-49.19 EndY=2.75 EndZ=0
    g12: ArcOfCircle CenterX=-1.5 CenterY=67.75 CenterZ=0 NormalX=0 NormalY=0 NormalZ=1 AngleXU=0 Radius=1.5 StartAngle=4.71239 EndAngle=7.85398
    g13: ArcOfCircle CenterX=-1.5 CenterY=62 CenterZ=0 NormalX=0 NormalY=0 NormalZ=1 AngleXU=0 Radius=1.5 StartAngle=4.71239 EndAngle=7.85398
    g14: ArcOfCircle CenterX=-1.5 CenterY=56.25 CenterZ=0 NormalX=0 NormalY=0 NormalZ=1 AngleXU=0 Radius=1.5 StartAngle=4.71239 EndAngle=7.85398
    g15: ArcOfCircle CenterX=-11.49 CenterY=50.5 CenterZ=0 NormalX=0 NormalY=0 NormalZ=1 AngleXU=0 Radius=1.5 StartAngle=4.71239 EndAngle=7.85398
    g16: ArcOfCircle CenterX=-16.28 CenterY=44.75 CenterZ=0 NormalX=0 NormalY=0 NormalZ=1 AngleXU=0 Radius=1.5 StartAngle=4.71239 EndAngle=7.85398
    g17: ArcOfCircle CenterX=-18.2337 CenterY=39 CenterZ=0 NormalX=0 NormalY=0 NormalZ=1 AngleXU=0 Radius=1.5 StartAngle=4.71485 EndAngle=7.85398
    g18: ArcOfCircle CenterX=-16.2837 CenterY=27.25 CenterZ=0 NormalX=0 NormalY=0 NormalZ=1 AngleXU=0 Radius=1.5 StartAngle=4.71485 EndAngle=7.85398
    g19: ArcOfCircle CenterX=-18.2337 CenterY=33 CenterZ=0 NormalX=0 NormalY=0 NormalZ=1 AngleXU=0 Radius=1.5 StartAngle=4.71485 EndAngle=7.85398
    g20: ArcOfCircle CenterX=-11.49 CenterY=21.5 CenterZ=0 NormalX=0 NormalY=0 NormalZ=1 AngleXU=0 Radius=1.5 StartAngle=4.71239 EndAngle=7.85398
    g21: ArcOfCircle CenterX=-1.5 CenterY=4.25 CenterZ=0 NormalX=0 NormalY=0 NormalZ=1 AngleXU=0 Radius=1.5 StartAngle=4.71239 EndAngle=7.85398
    g22: ArcOfCircle CenterX=-1.5 CenterY=10 CenterZ=0 NormalX=0 NormalY=0 NormalZ=1 AngleXU=0 Radius=1.5 StartAngle=4.71239 EndAngle=7.85398
    g23: ArcOfCircle CenterX=-1.5 CenterY=15.75 CenterZ=0 NormalX=0 NormalY=0 NormalZ=1 AngleXU=0 Radius=1.5 StartAngle=4.71239 EndAngle=7.85398
    g24: LineSegment StartX=-49.19 StartY=69.25 StartZ=0 EndX=-1.5 EndY=69.25 EndZ=0
    g25: LineSegment StartX=-49.19 StartY=66.25 StartZ=0 EndX=-1.5 EndY=66.25 EndZ=0
    g26: LineSegment StartX=-49.19 StartY=63.5 StartZ=0 EndX=-1.5 EndY=63.5 EndZ=0
    g27: LineSegment StartX=-49.19 StartY=60.5 StartZ=0 EndX=-1.5 EndY=60.5 EndZ=0
    g28: LineSegment StartX=-49.19 StartY=57.75 StartZ=0 EndX=-1.5 EndY=57.75 EndZ=0
    g29: LineSegment StartX=-49.19 StartY=54.75 StartZ=0 EndX=-1.5 EndY=54.75 EndZ=0
    g30: LineSegment StartX=-49.19 StartY=52 StartZ=0 EndX=-11.49 EndY=52 EndZ=0
    g31: LineSegment StartX=-49.19 StartY=49 StartZ=0 EndX=-11.49 EndY=49 EndZ=0
    g32: LineSegment StartX=-49.19 StartY=46.25 StartZ=0 EndX=-16.28 EndY=46.25 EndZ=0
    g33: LineSegment StartX=-49.19 StartY=43.25 StartZ=0 EndX=-16.28 EndY=43.25 EndZ=0
    g34: LineSegment StartX=-49.19 StartY=40.5 StartZ=0 EndX=-18.2337 EndY=40.5 EndZ=0
    g35: LineSegment StartX=-49.19 StartY=37.5 StartZ=0 EndX=-18.23 EndY=37.5 EndZ=0
    g36: LineSegment StartX=-49.19 StartY=34.5 StartZ=0 EndX=-18.2337 EndY=34.5 EndZ=0
    g37: LineSegment StartX=-49.19 StartY=31.5 StartZ=0 EndX=-18.23 EndY=31.5 EndZ=0
    g38: LineSegment StartX=-49.19 StartY=28.75 StartZ=0 EndX=-16.2837 EndY=28.75 EndZ=0
    g39: LineSegment StartX=-49.19 StartY=25.75 StartZ=0 EndX=-16.28 EndY=25.75 EndZ=0
    g40: LineSegment StartX=-49.19 StartY=23 StartZ=0 EndX=-11.49 EndY=23 EndZ=0
    g41: LineSegment StartX=-49.19 StartY=20 StartZ=0 EndX=-11.49 EndY=20 EndZ=0
    g42: LineSegment StartX=-49.19 StartY=17.25 StartZ=0 EndX=-1.5 EndY=17.25 EndZ=0
    g43: LineSegment StartX=-49.19 StartY=14.25 StartZ=0 EndX=-1.5 EndY=14.25 EndZ=0
    g44: LineSegment StartX=-49.19 StartY=11.5 StartZ=0 EndX=-1.5 EndY=11.5 EndZ=0
    g45: LineSegment StartX=-49.19 StartY=8.5 StartZ=0 EndX=-1.5 EndY=8.5 EndZ=0
    g46: LineSegment StartX=-49.19 StartY=5.75 StartZ=0 EndX=-1.5 EndY=5.75 EndZ=0
    g47: LineSegment StartX=-49.19 StartY=2.75 StartZ=0 EndX=-1.5 EndY=2.75 EndZ=0
  constraints (120):
    c: Vertical(g0)
    c: Distance(g0) = 3
    c: Block(g0)
    c: Vertical(g1)
    c: Distance(g1) = 3
    c: Vertical(g2)
    c: Equal(g0,g2) = 3
    c: Block(g2)
    c: Vertical(g3)
    c: Equal(g1,g3) = 3
    c: Vertical(g4)
    c: Equal(g0,g4) = 3
    c: Block(g4)
    c: Vertical(g5)
    c: Equal(g1,g5) = 3
    c: Vertical(g6)
    c: Equal(g0,g6) = 3
    c: Block(g6)
    c: Vertical(g7)
    c: Equal(g1,g7) = 3
    c: Vertical(g8)
    c: Equal(g0,g8) = 3
    c: Block(g8)
    c: Vertical(g9)
    c: Equal(g1,g9) = 3
    c: Vertical(g10)
    c: Equal(g0,g10) = 3
    c: Block(g10)
    c: Vertical(g11)
    c: Equal(g1,g11) = 3
    c: Block(g12)
    c: Block(g13)
    c: Block(g14)
    c: Block(g15)
    c: Block(g16)
    c: Block(g17)
    c: Block(g18)
    c: Block(g19)
    c: Block(g20)
    c: Block(g21)
    c: Block(g22)
    c: Block(g23)
    c: Block(g11)
    c: Block(g9)
    c: Block(g7)
    c: Block(g5)
    c: Block(g3)
    c: Block(g1)
    c: Coincident(g24,g0)
    c: Coincident(g24,g12)
    c: Horizontal(g24)
    c: Coincident(g25,g0)
    c: Coincident(g25,g12)
    c: Horizontal(g25)
    c: Coincident(g26,g1)
    c: Coincident(g26,g13)
    c: Horizontal(g26)
    c: Coincident(g27,g1)
    c: Coincident(g27,g13)
    c: Horizontal(g27)
    c: Coincident(g28,g2)
    c: Coincident(g28,g14)
    c: Horizontal(g28)
    c: Coincident(g29,g2)
    c: Coincident(g29,g14)
    c: Horizontal(g29)
    c: Coincident(g30,g3)
    c: Coincident(g30,g15)
    c: Horizontal(g30)
    c: Coincident(g31,g3)
    c: Coincident(g31,g15)
    c: Horizontal(g31)
    c: Coincident(g32,g4)
    c: Coincident(g32,g16)
    c: Horizontal(g32)
    c: Coincident(g33,g4)
    c: Coincident(g33,g16)
    c: Horizontal(g33)
    c: Coincident(g34,g5)
    c: Coincident(g34,g17)
    c: Horizontal(g34)
    c: Coincident(g35,g5)
    c: Coincident(g35,g17)
    c: Horizontal(g35)
    c: Coincident(g36,g6)
    c: Coincident(g36,g19)
    c: Horizontal(g36)
    c: Coincident(g37,g6)
    c: Coincident(g37,g19)
    c: Horizontal(g37)
    c: Coincident(g38,g7)
    c: Coincident(g38,g18)
    c: Horizontal(g38)
    c: Coincident(g39,g7)
    c: Coincident(g39,g18)
    c: Horizontal(g39)
    c: Coincident(g40,g8)
    c: Coincident(g40,g20)
    c: Horizontal(g40)
    c: Coincident(g41,g8)
    c: Coincident(g41,g20)
    c: Horizontal(g41)
    c: Coincident(g42,g9)
    c: Coincident(g42,g23)
    c: Horizontal(g42)
    c: Coincident(g43,g9)
    c: Coincident(g43,g23)
    c: Horizontal(g43)
    c: Coincident(g44,g10)
    c: Coincident(g44,g22)
    c: Horizontal(g44)
    c: Coincident(g45,g10)
    c: Coincident(g45,g22)
    c: Horizontal(g45)
    c: Coincident(g46,g11)
    c: Coincident(g46,g21)
    c: Horizontal(g46)
    c: Coincident(g47,g11)
    c: Coincident(g47,g21)
    c: Horizontal(g47)
FEATURE [Part::Extrusion] Extrude042
  Base = -> Sketch051
  Dir = (1,-2e-16,2e-16)
  DirMode = 2
  FaceMakerClass = Part::FaceMakerBullseye
  LengthFwd = 19
  LengthRev = 0
  Placement = pos=(-19,0,0) rot=(0,0,1;0rad)
  Solid = true
  Symmetric = false
FEATURE [Part::Fillet] Fillet035  label="removeToCreateVentalationHoles"
  Base = -> Extrude042
  Edges = <same value as first occurrence — deduplicated (x6 in doc)>
  Placement = pos=(7,0,0) rot=(0,0,1;0rad)
FEATURE [Part::Cut] Cut038  label="top017"
  Base = -> Cut033
  Tool = -> Fillet035
FEATURE [Sketcher::SketchObject] Sketch052  label="bottomSketch001"
  FullyConstrained = true
  sketch-geometry (45):
    g0: LineSegment StartX=6.29999 StartY=8 StartZ=0 EndX=3.29999 EndY=8 EndZ=0
    g1: LineSegment StartX=3.29999 StartY=8 StartZ=0 EndX=3.29999 EndY=-6.03275e-07 EndZ=0
    g2: ArcOfCircle CenterX=8.29999 CenterY=5 CenterZ=0 NormalX=0 NormalY=0 NormalZ=1 AngleXU=0 Radius=2 StartAngle=3.14159 EndAngle=4.71239
    g3: LineSegment StartX=6.29999 StartY=8 StartZ=0 EndX=6.29999 EndY=5 EndZ=0
    g4: ArcOfCircle CenterX=105 CenterY=19 CenterZ=0 NormalX=0 NormalY=0 NormalZ=1 AngleXU=0 Radius=12.7 StartAngle=4.71239 EndAngle=5.94289
    g5-g11: Circle x7 (B-spline internal-alignment scaffolding for g12; pole/knot coordinates omitted)
    g12: BSplineCurve PolesCount=7 KnotsCount=5 Degree=3 IsPeriodic=0
    g13-g17: GeomPoint x5 (B-spline internal-alignment scaffolding for g12; pole/knot coordinates omitted)
    g18: ArcOfCircle CenterX=105 CenterY=19 CenterZ=0 NormalX=0 NormalY=0 NormalZ=1 AngleXU=0 Radius=15.7 StartAngle=5.81226 EndAngle=6.28319
    g19: BSplineCurve PolesCount=5 KnotsCount=3 Degree=3 IsPeriodic=0
    g20: LineSegment StartX=8.29999 StartY=3 StartZ=0 EndX=101.7 EndY=3 EndZ=0
    g21: LineSegment StartX=3.29999 StartY=-6.03275e-07 StartZ=0 EndX=105 EndY=-6.03275e-07 EndZ=0
    g22: LineSegment StartX=120.974 StartY=8.71251 StartZ=0 EndX=122.332 EndY=7.83778 EndZ=0
    g23: LineSegment StartX=105 StartY=-6.03274e-07 StartZ=0 EndX=113 EndY=-6.03274e-07 EndZ=0
    g24: ArcOfCircle CenterX=105 CenterY=19 CenterZ=0 NormalX=0 NormalY=0 NormalZ=1 AngleXU=0 Radius=20.6155 StartAngle=5.11091 EndAngle=5.71103
    g25: ArcOfCircle CenterX=117.7 CenterY=19 CenterZ=0 NormalX=0 NormalY=0 NormalZ=1 AngleXU=0 Radius=3 StartAngle=1.2e-15 EndAngle=2.10468
    g26: Circle CenterX=116.345 CenterY=16.3232 CenterZ=0 NormalX=0 NormalY=0 NormalZ=1 AngleXU=0 Radius=1
    g27: Circle CenterX=117.24 CenterY=15.7584 CenterZ=0 NormalX=0 NormalY=0 NormalZ=1 AngleXU=0 Radius=1
    g28: Circle CenterX=116.972 CenterY=14.7612 CenterZ=0 NormalX=0 NormalY=0 NormalZ=1 AngleXU=0 Radius=1
    g29: BSplineCurve PolesCount=3 KnotsCount=2 Degree=2 IsPeriodic=0
    g30: GeomPoint X=116.345 Y=16.3232 Z=0
    g31: GeomPoint X=116.972 Y=14.7612 Z=0
    g32: Circle CenterX=115.828 CenterY=17.157 CenterZ=0 NormalX=0 NormalY=0 NormalZ=1 AngleXU=0 Radius=1
    g33: Circle CenterX=115.841 CenterY=16.639 CenterZ=0 NormalX=0 NormalY=0 NormalZ=1 AngleXU=0 Radius=1
    g34: Circle CenterX=116.345 CenterY=16.3232 CenterZ=0 NormalX=0 NormalY=0 NormalZ=1 AngleXU=0 Radius=1
    g35: BSplineCurve PolesCount=3 KnotsCount=2 Degree=2 IsPeriodic=0
    g36: GeomPoint X=115.828 Y=17.157 Z=0
    g37: GeomPoint X=116.345 Y=16.3232 Z=0
    g38: LineSegment StartX=115.828 StartY=17.157 StartZ=0 EndX=115.828 EndY=20.8307 EndZ=0
    g39: Circle CenterX=115.828 CenterY=20.8307 CenterZ=0 NormalX=0 NormalY=0 NormalZ=1 AngleXU=0 Radius=1
    g40: Circle CenterX=115.831 CenterY=21.3396 CenterZ=0 NormalX=0 NormalY=0 NormalZ=1 AngleXU=0 Radius=1
    g41: Circle CenterX=116.173 CenterY=21.5825 CenterZ=0 NormalX=0 NormalY=0 NormalZ=1 AngleXU=0 Radius=1
    g42: BSplineCurve PolesCount=3 KnotsCount=2 Degree=2 IsPeriodic=0
    g43: GeomPoint X=115.828 Y=20.8307 Z=0
    g44: GeomPoint X=116.173 Y=21.5825 Z=0
  constraints (70):
    c: Horizontal(g0)
    c: Distance(g0) = 3
    c: Coincident(g1,g0)
    c: Vertical(g1)
    c: Block(g2)
    c: Block(g0)
    c: Coincident(g3,g0)
    c: Coincident(g3,g2)
    c: Vertical(g3)
    c: Block(g1)
    c: Block(g4)
    c: Coincident(g19,g4)
    c: Block(g19)
    c: Equal(g5, g6-g11) x6
    c: InternalAlignment(g5-g11 -> g12) x7
    c: InternalAlignment(g13-g17 -> g12) x5
    c: Block(g12)
    c: Coincident(g18,g12)
    c: Block(g18)
    c: Coincident(g20,g2)
    c: Coincident(g20,g19)
    c: Horizontal(g20)
    c: Distance(g20) = 93.4
    c: Coincident(g21,g1)
    c: Horizontal(g21)
    c: Distance(g21) = 101.7
    c: Horizontal(g23)
    c: Distance(g23) = 8
    c: Coincident(g24,g23)
    c: Block(g23)
    c: Coincident(g22,g24)
    c: Block(g24)
    c: Block(g22)
    c: Distance(g22) = 1.61553
    c: Coincident(g25,g18)
    c: Block(g25)
    c: Weight(g26) = 1
    c: Equal(g26,g27)
    c: Equal(g26,g28)
    c: Coincident(g29,g4)
    c: InternalAlignment(g26,g29)
    c: InternalAlignment(g27,g29)
    c: InternalAlignment(g28,g29)
    c: InternalAlignment(g30,g29)
    c: InternalAlignment(g31,g29)
    c: Block(g29)
    c: Weight(g32) = 1
    c: Equal(g32,g33)
    c: Equal(g32,g34)
    c: Coincident(g35,g29)
    c: InternalAlignment(g32,g35)
    c: InternalAlignment(g33,g35)
    c: InternalAlignment(g34,g35)
    c: InternalAlignment(g36,g35)
    c: InternalAlignment(g37,g35)
    c: Block(g35)
    c: Coincident(g38,g35)
    c: Vertical(g38)
    c: Block(g38)
    c: Coincident(g42,g38)
    c: Weight(g39) = 1
    c: Equal(g39,g40)
    c: Equal(g39,g41)
    c: Coincident(g42,g25)
    c: InternalAlignment(g39,g42)
    c: InternalAlignment(g40,g42)
    c: InternalAlignment(g41,g42)
    c: InternalAlignment(g43,g42)
    c: InternalAlignment(g44,g42)
    c: Block(g42)
FEATURE [Part::Extrusion] Extrude043  label="bottom010"
  Base = -> Sketch052
  Dir = (0,0,1)
  DirMode = 2
  FaceMakerClass = Part::FaceMakerBullseye
  LengthFwd = 71.4
  LengthRev = 0
  Placement = pos=(0,0,0.3) rot=(0,0,1;0rad)
  Solid = true
  Symmetric = false
FEATURE [Sketcher::SketchObject] Sketch053  label="topSketch013"
  FullyConstrained = true
  sketch-geometry (22):
    g0: LineSegment StartX=5.21097e-06 StartY=3 StartZ=0 EndX=5.21097e-06 EndY=19 EndZ=0
    g1: ArcOfCircle CenterX=19 CenterY=19 CenterZ=0 NormalX=0 NormalY=0 NormalZ=1 AngleXU=0 Radius=19 StartAngle=1.5708 EndAngle=3.14159
    g2: ArcOfCircle CenterX=19 CenterY=19 CenterZ=0 NormalX=0 NormalY=0 NormalZ=1 AngleXU=0 Radius=16 StartAngle=1.5708 EndAngle=3.14159
    g3: LineSegment StartX=114 StartY=35 StartZ=0 EndX=19 EndY=35 EndZ=0
    g4: LineSegment StartX=5.21097e-06 StartY=3 StartZ=0 EndX=5.21097e-06 EndY=0 EndZ=0
    g5: LineSegment StartX=3 StartY=0 StartZ=0 EndX=5.21097e-06 EndY=0 EndZ=0
    g6: LineSegment StartX=3 StartY=19 StartZ=0 EndX=3 EndY=0 EndZ=0
    g7: LineSegment StartX=19 StartY=38 StartZ=0 EndX=124 EndY=38 EndZ=0
    g8: Circle CenterX=119 CenterY=35 CenterZ=0 NormalX=0 NormalY=0 NormalZ=1 AngleXU=0 Radius=1
    g9: Circle CenterX=121 CenterY=35 CenterZ=0 NormalX=0 NormalY=0 NormalZ=1 AngleXU=0 Radius=1
    g10: Circle CenterX=121 CenterY=33 CenterZ=0 NormalX=0 NormalY=0 NormalZ=1 AngleXU=0 Radius=1
    g11: BSplineCurve PolesCount=3 KnotsCount=2 Degree=2 IsPeriodic=0
    g12: GeomPoint X=119 Y=35 Z=0
    g13: GeomPoint X=121 Y=33 Z=0
    g14: LineSegment StartX=119 StartY=35 StartZ=0 EndX=114 EndY=35 EndZ=0
    g15: ArcOfCircle CenterX=105 CenterY=19 CenterZ=0 NormalX=0 NormalY=0 NormalZ=1 AngleXU=0 Radius=16 StartAngle=5.60905 EndAngle=6.28319
    g16: LineSegment StartX=121 StartY=33 StartZ=0 EndX=121 EndY=19 EndZ=0
    g17: LineSegment StartX=117.5 StartY=9.01251 StartZ=0 EndX=121.163 EndY=9.0125 EndZ=0
    g18: ArcOfCircle CenterX=105 CenterY=19 CenterZ=0 NormalX=0 NormalY=0 NormalZ=1 AngleXU=0 Radius=20.6155 StartAngle=5.7297 EndAngle=6.28319
    g19: LineSegment StartX=121.163 StartY=9.0125 StartZ=0 EndX=122.538 EndY=8.16329 EndZ=0
    g20: LineSegment StartX=124 StartY=38 StartZ=0 EndX=125.616 EndY=38 EndZ=0
    g21: LineSegment StartX=125.616 StartY=19 StartZ=0 EndX=125.616 EndY=38 EndZ=0
  constraints (50):
    c: Vertical(g0)
    c: Block(g0)
    c: Coincident(g1,g0)
    c: Block(g1)
    c: Coincident(g2,g1)
    c: Block(g2)
    c: Coincident(g3,g2)
    c: Horizontal(g3)
    c: Tangent(g3,g2)
    c: Coincident(g4,g0)
    c: Distance(g4) = 3
    c: Vertical(g4)
    c: Coincident(g5,g4)
    c: Horizontal(g5)
    c: Coincident(g6,g2)
    c: Coincident(g6,g5)
    c: Vertical(g6)
    c: Horizontal(g7)
    c: Distance(g7) = 105
    c: Coincident(g7,g1)
    c: Block(g3)
    c: Weight(g8) = 1
    c: Equal(g8,g9)
    c: Equal(g8,g10)
    c: InternalAlignment(g8,g11)
    c: InternalAlignment(g9,g11)
    c: InternalAlignment(g10,g11)
    c: InternalAlignment(g12,g11)
    c: InternalAlignment(g13,g11)
    c: Block(g11)
    c: Coincident(g14,g11)
    c: Coincident(g14,g3)
    c: Horizontal(g14)
    c: Block(g15)
    c: Coincident(g16,g11)
    c: Coincident(g16,g15)
    c: Vertical(g16)
    c: Distance(g16) = 14
    c: Coincident(g17,g15)
    c: Block(g18)
    c: Coincident(g19,g18)
    c: Coincident(g20,g7)
    c: Horizontal(g20)
    c: Vertical(g21)
    c: Coincident(g20,g21)
    c: Block(g20)
    c: Block(g21)
    c: Block(g19)
    c: Block(g17)
    c: Distance(g20) = 1.61553
FEATURE [Part::Extrusion] Extrude044
  Base = -> Sketch053
  Dir = (0,0,1)
  DirMode = 2
  FaceMakerClass = Part::FaceMakerBullseye
  LengthFwd = 72
  LengthRev = 0
  Solid = true
  Symmetric = false
FEATURE [Part::Fillet] Fillet036  label="top018"
  Base = -> Extrude044
  Edges = 1 edges r=2: [Edge41]
FEATURE [Sketcher::SketchObject] Sketch054
  FullyConstrained = false
  Placement = pos=(0,0,0) rot=(1,0,0;1.5708rad)
  sketch-geometry (24):
    g0: ArcOfCircle CenterX=-4 CenterY=-10.5 CenterZ=0 NormalX=0 NormalY=0 NormalZ=1 AngleXU=0 Radius=1.5 StartAngle=6e-16 EndAngle=3.14159
    g1: ArcOfCircle CenterX=-34.2 CenterY=-10.5 CenterZ=0 NormalX=0 NormalY=0 NormalZ=1 AngleXU=0 Radius=1.5 StartAngle=0 EndAngle=3.14159
    g2: ArcOfCircle CenterX=-34.2 CenterY=-27.7 CenterZ=0 NormalX=0 NormalY=0 NormalZ=1 AngleXU=0 Radius=1.5 StartAngle=3.14159 EndAngle=6.28319
    g3: ArcOfCircle CenterX=-4 CenterY=-27.7 CenterZ=0 NormalX=0 NormalY=0 NormalZ=1 AngleXU=0 Radius=1.5 StartAngle=3.1416 EndAngle=6.28319
    g4: ArcOfCircle CenterX=-10 CenterY=-4.3 CenterZ=0 NormalX=0 NormalY=0 NormalZ=1 AngleXU=0 Radius=1.5 StartAngle=2e-16 EndAngle=3.14159
    g5: ArcOfCircle CenterX=-16.1 CenterY=-1.8 CenterZ=0 NormalX=0 NormalY=0 NormalZ=1 AngleXU=0 Radius=1.5 StartAngle=5e-16 EndAngle=3.14159
    g6: ArcOfCircle CenterX=-22.1 CenterY=-1.8 CenterZ=0 NormalX=0 NormalY=0 NormalZ=1 AngleXU=0 Radius=1.5 StartAngle=5e-16 EndAngle=3.14159
    g7: ArcOfCircle CenterX=-28.2 CenterY=-4.3 CenterZ=0 NormalX=0 NormalY=0 NormalZ=1 AngleXU=0 Radius=1.5 StartAngle=2e-16 EndAngle=3.14159
    g8: ArcOfCircle CenterX=-10 CenterY=-33.9 CenterZ=0 NormalX=0 NormalY=0 NormalZ=1 AngleXU=0 Radius=1.5 StartAngle=3.14159 EndAngle=6.28319
    g9: ArcOfCircle CenterX=-16.1 CenterY=-36.4 CenterZ=0 NormalX=0 NormalY=0 NormalZ=1 AngleXU=0 Radius=1.5 StartAngle=3.14159 EndAngle=6.28319
    g10: ArcOfCircle CenterX=-22.1 CenterY=-36.4 CenterZ=0 NormalX=0 NormalY=0 NormalZ=1 AngleXU=0 Radius=1.5 StartAngle=3.14159 EndAngle=6.28319
    g11: ArcOfCircle CenterX=-28.2 CenterY=-33.9 CenterZ=0 NormalX=0 NormalY=0 NormalZ=1 AngleXU=0 Radius=1.5 StartAngle=3.14159 EndAngle=6.28319
    g12: LineSegment StartX=-35.7 StartY=-10.5 StartZ=0 EndX=-35.7 EndY=-27.7 EndZ=0
    g13: LineSegment StartX=-32.7 StartY=-10.5 StartZ=0 EndX=-32.7 EndY=-27.7 EndZ=0
    g14: LineSegment StartX=-29.7 StartY=-33.9 StartZ=0 EndX=-29.7 EndY=-4.3 EndZ=0
    g15: LineSegment StartX=-26.7 StartY=-33.9 StartZ=0 EndX=-26.7 EndY=-4.3 EndZ=0
    g16: LineSegment StartX=-2.5 StartY=-10.5 StartZ=0 EndX=-2.5 EndY=-27.7 EndZ=0
    g17: LineSegment StartX=-8.5 StartY=-4.3 StartZ=0 EndX=-8.5 EndY=-33.9 EndZ=0
    g18: LineSegment StartX=-5.5 StartY=-10.5 StartZ=0 EndX=-5.5 EndY=-27.7 EndZ=0
    g19: LineSegment StartX=-11.5 StartY=-4.3 StartZ=0 EndX=-11.5 EndY=-33.9 EndZ=0
    g20: LineSegment StartX=-14.6 StartY=-1.8 StartZ=0 EndX=-14.6 EndY=-36.4 EndZ=0
    g21: LineSegment StartX=-17.6 StartY=-1.8 StartZ=0 EndX=-17.6 EndY=-36.4 EndZ=0
    g22: LineSegment StartX=-20.6 StartY=-36.4 StartZ=0 EndX=-20.6 EndY=-1.8 EndZ=0
    g23: LineSegment StartX=-23.6 StartY=-1.8 StartZ=0 EndX=-23.6 EndY=-36.4 EndZ=0
  constraints (48):
    c: Block(g0)
    c: Block(g1)
    c: Block(g2)
    c: Block(g3)
    c: Block(g4)
    c: Block(g5)
    c: Block(g6)
    c: Block(g7)
    c: Block(g8)
    c: Block(g9)
    c: Block(g10)
    c: Block(g11)
    c: Coincident(g12,g1)
    c: Coincident(g12,g2)
    c: Vertical(g12)
    c: Coincident(g13,g1)
    c: Coincident(g13,g2)
    c: Vertical(g13)
    c: Coincident(g14,g11)
    c: Coincident(g14,g7)
    c: Vertical(g14)
    c: Coincident(g15,g11)
    c: Coincident(g15,g7)
    c: Vertical(g15)
    c: Coincident(g16,g0)
    c: Coincident(g16,g3)
    c: Vertical(g16)
    c: Coincident(g17,g4)
    c: Coincident(g17,g8)
    c: Vertical(g17)
    c: Coincident(g18,g0)
    c: Coincident(g18,g3)
    c: Vertical(g18)
    c: Coincident(g19,g4)
    c: Coincident(g19,g8)
    c: Vertical(g19)
    c: Coincident(g20,g5)
    c: Coincident(g20,g9)
    c: Vertical(g20)
    c: Coincident(g21,g5)
    c: Coincident(g21,g9)
    c: Vertical(g21)
    c: Coincident(g22,g10)
    c: Coincident(g22,g6)
    c: Vertical(g22)
    c: Coincident(g23,g6)
    c: Coincident(g23,g10)
    c: Vertical(g23)
FEATURE [Part::Extrusion] Extrude045  label="removeToCreateFanGrillHoles003"
  Base = -> Sketch054
  Dir = (0,-1,6e-16)
  DirMode = 2
  FaceMakerClass = Part::FaceMakerBullseye
  LengthFwd = 10
  LengthRev = 0
  Placement = pos=(65.4,44,54.82) rot=(0,0,1;0rad)
  Solid = true
  Symmetric = false
FEATURE [Part::Feature] Face105 .. Face108  x4 (patterned run collapsed; names and placements below)
  shape: bbox 3.5 x 17.8 x 2e-07 mm, 1 faces, 0 solids (baked)
FEATURE [Part::Revolution] Revolve113  label="removeToCreateScrewAndThreadedInsertHole041"
  Angle = 360
  Axis = (0,1,0)
  Base = (0,0,0)
  FaceMakerClass = Part::FaceMakerBullseye
  Placement = pos=(62.3,30.3,19.7) rot=(0,0,1;0rad)
  Solid = false
  Source = -> Face105
  Symmetric = false
FEATURE [Part::Revolution] Revolve114  label="removeToCreateScrewAndThreadedInsertHole042"
  Angle = 360
  Axis = (0,1,0)
  Base = (0,0,0)
  FaceMakerClass = Part::FaceMakerBullseye
  Placement = pos=(62.3,30.3,51.7) rot=(0,0,1;0rad)
  Solid = false
  Source = -> Face106
  Symmetric = false
FEATURE [Part::Revolution] Revolve115  label="removeToCreateScrewAndThreadedInsertHole043"
  Angle = 360
  Axis = (0,1,0)
  Base = (0,0,0)
  FaceMakerClass = Part::FaceMakerBullseye
  Placement = pos=(30.3,30.3,19.7) rot=(0,0,1;0rad)
  Solid = false
  Source = -> Face107
  Symmetric = false
FEATURE [Part::Revolution] Revolve116  label="removeToCreateScrewAndThreadedInsertHole044"
  Angle = 360
  Axis = (0,1,0)
  Base = (0,0,0)
  FaceMakerClass = Part::FaceMakerBullseye
  Placement = pos=(30.3,30.3,51.7) rot=(0,0,1;0rad)
  Solid = false
  Source = -> Face108
  Symmetric = false
FEATURE [Part::MultiFuse] Fusion083  label="createThreadedInsertHolesForFan004"
  Shapes = -> [Revolve113,Revolve114,Revolve115,Revolve116]
FEATURE [Part::Box] Box024  label="removeToCreteHoleForPlugHousing026"
  AttacherType = Attacher::AttachEngine3D
  Height = 28.6
  Length = 10
  Placement = pos=(-2,0,21.7) rot=(0,0,1;0rad)
  Width = 19
FEATURE [Part::Cylinder] Cylinder038  label="removeToCreteHoleForPlugHousing027"
  Angle = 360
  AttacherType = Attacher::AttachEngine3D
  Height = 20
  Placement = pos=(-2,19,36) rot=(0,1,0;1.5708rad)
  Radius = 14.3
FEATURE [Part::MultiFuse] Fusion084  label="removeToCreteHoleForPlugHousing028"
  Shapes = -> [Box024,Cylinder038]
FEATURE [Part::Cylinder] Cylinder039
  Angle = 360
  AttacherType = Attacher::AttachEngine3D
  Height = 20
  Placement = pos=(0,0,36.15) rot=(0,0,1;0rad)
  Radius = 14.3
FEATURE [Part::Cylinder] Cylinder040
  Angle = 360
  AttacherType = Attacher::AttachEngine3D
  Height = 10
  Placement = pos=(0,0,36.15) rot=(0,0,1;0rad)
  Radius = 4
FEATURE [Part::Box] Box025  label="removeToCreteHoleForPlugHousing030"
  AttacherType = Attacher::AttachEngine3D
  Height = 28.6
  Length = 20
  Placement = pos=(106.15,0,21.7) rot=(0,0,1;0rad)
  Width = 19
FEATURE [Part::MultiFuse] Fusion086  label="removeToCreteHoleForPlugHousing031"
  Placement = pos=(70,19,36) rot=(0,1,0;1.5708rad)
  Shapes = -> [Cylinder039,Cylinder040]
FEATURE [Part::MultiFuse] Fusion085  label="removeToCreteHoleForPlugHousing029"
  Shapes = -> [Box025,Fusion086]
FEATURE [Sketcher::SketchObject] Sketch055
  FullyConstrained = true
  Placement = pos=(117,19,0) rot=(0.57735,0.57735,0.57735;2.0944rad)
  sketch-geometry (48):
    g0: LineSegment StartX=-49.19 StartY=69.25 StartZ=0 EndX=-49.19 EndY=66.25 EndZ=0
    g1: LineSegment StartX=-49.19 StartY=63.5 StartZ=0 EndX=-49.19 EndY=60.5 EndZ=0
    g2: LineSegment StartX=-49.19 StartY=57.75 StartZ=0 EndX=-49.19 EndY=54.75 EndZ=0
    g3: LineSegment StartX=-49.19 StartY=52 StartZ=0 EndX=-49.19 EndY=49 EndZ=0
    g4: LineSegment StartX=-49.19 StartY=46.25 StartZ=0 EndX=-49.19 EndY=43.25 EndZ=0
    g5: LineSegment StartX=-49.19 StartY=40.5 StartZ=0 EndX=-49.19 EndY=37.5 EndZ=0
    g6: LineSegment StartX=-49.19 StartY=34.5 StartZ=0 EndX=-49.19 EndY=31.5 EndZ=0
    g7: LineSegment StartX=-49.19 StartY=28.75 StartZ=0 EndX=-49.19 EndY=25.75 EndZ=0
    g8: LineSegment StartX=-49.19 StartY=23 StartZ=0 EndX=-49.19 EndY=20 EndZ=0
    g9: LineSegment StartX=-49.19 StartY=17.25 StartZ=0 EndX=-49.19 EndY=14.25 EndZ=0
    g10: LineSegment StartX=-49.19 StartY=11.5 StartZ=0 EndX=-49.19 EndY=8.5 EndZ=0
    g11: LineSegment StartX=-49.19 StartY=5.75 StartZ=0 EndX=-49.19 EndY=2.75 EndZ=0
    g12: ArcOfCircle CenterX=-1.5 CenterY=67.75 CenterZ=0 NormalX=0 NormalY=0 NormalZ=1 AngleXU=0 Radius=1.5 StartAngle=4.71239 EndAngle=7.85398
    g13: ArcOfCircle CenterX=-1.5 CenterY=62 CenterZ=0 NormalX=0 NormalY=0 NormalZ=1 AngleXU=0 Radius=1.5 StartAngle=4.71239 EndAngle=7.85398
    g14: ArcOfCircle CenterX=-1.5 CenterY=56.25 CenterZ=0 NormalX=0 NormalY=0 NormalZ=1 AngleXU=0 Radius=1.5 StartAngle=4.71239 EndAngle=7.85398
    g15: ArcOfCircle CenterX=-11.49 CenterY=50.5 CenterZ=0 NormalX=0 NormalY=0 NormalZ=1 AngleXU=0 Radius=1.5 StartAngle=4.71239 EndAngle=7.85398
    g16: ArcOfCircle CenterX=-16.28 CenterY=44.75 CenterZ=0 NormalX=0 NormalY=0 NormalZ=1 AngleXU=0 Radius=1.5 StartAngle=4.71239 EndAngle=7.85398
    g17: ArcOfCircle CenterX=-18.2337 CenterY=39 CenterZ=0 NormalX=0 NormalY=0 NormalZ=1 AngleXU=0 Radius=1.5 StartAngle=4.71485 EndAngle=7.85398
    g18: ArcOfCircle CenterX=-16.2837 CenterY=27.25 CenterZ=0 NormalX=0 NormalY=0 NormalZ=1 AngleXU=0 Radius=1.5 StartAngle=4.71485 EndAngle=7.85398
    g19: ArcOfCircle CenterX=-18.2337 CenterY=33 CenterZ=0 NormalX=0 NormalY=0 NormalZ=1 AngleXU=0 Radius=1.5 StartAngle=4.71485 EndAngle=7.85398
    g20: ArcOfCircle CenterX=-11.49 CenterY=21.5 CenterZ=0 NormalX=0 NormalY=0 NormalZ=1 AngleXU=0 Radius=1.5 StartAngle=4.71239 EndAngle=7.85398
    g21: ArcOfCircle CenterX=-1.5 CenterY=4.25 CenterZ=0 NormalX=0 NormalY=0 NormalZ=1 AngleXU=0 Radius=1.5 StartAngle=4.71239 EndAngle=7.85398
    g22: ArcOfCircle CenterX=-1.5 CenterY=10 CenterZ=0 NormalX=0 NormalY=0 NormalZ=1 AngleXU=0 Radius=1.5 StartAngle=4.71239 EndAngle=7.85398
    g23: ArcOfCircle CenterX=-1.5 CenterY=15.75 CenterZ=0 NormalX=0 NormalY=0 NormalZ=1 AngleXU=0 Radius=1.5 StartAngle=4.71239 EndAngle=7.85398
    g24: LineSegment StartX=-49.19 StartY=69.25 StartZ=0 EndX=-1.5 EndY=69.25 EndZ=0
    g25: LineSegment StartX=-49.19 StartY=66.25 StartZ=0 EndX=-1.5 EndY=66.25 EndZ=0
    g26: LineSegment StartX=-49.19 StartY=63.5 StartZ=0 EndX=-1.5 EndY=63.5 EndZ=0
    g27: LineSegment StartX=-49.19 StartY=60.5 StartZ=0 EndX=-1.5 EndY=60.5 EndZ=0
    g28: LineSegment StartX=-49.19 StartY=57.75 StartZ=0 EndX=-1.5 EndY=57.75 EndZ=0
    g29: LineSegment StartX=-49.19 StartY=54.75 StartZ=0 EndX=-1.5 EndY=54.75 EndZ=0
    g30: LineSegment StartX=-49.19 StartY=52 StartZ=0 EndX=-11.49 EndY=52 EndZ=0
    g31: LineSegment StartX=-49.19 StartY=49 StartZ=0 EndX=-11.49 EndY=49 EndZ=0
    g32: LineSegment StartX=-49.19 StartY=46.25 StartZ=0 EndX=-16.28 EndY=46.25 EndZ=0
    g33: LineSegment StartX=-49.19 StartY=43.25 StartZ=0 EndX=-16.28 EndY=43.25 EndZ=0
    g34: LineSegment StartX=-49.19 StartY=40.5 StartZ=0 EndX=-18.2337 EndY=40.5 EndZ=0
    g35: LineSegment StartX=-49.19 StartY=37.5 StartZ=0 EndX=-18.23 EndY=37.5 EndZ=0
    g36: LineSegment StartX=-49.19 StartY=34.5 StartZ=0 EndX=-18.2337 EndY=34.5 EndZ=0
    g37: LineSegment StartX=-49.19 StartY=31.5 StartZ=0 EndX=-18.23 EndY=31.5 EndZ=0
    g38: LineSegment StartX=-49.19 StartY=28.75 StartZ=0 EndX=-16.2837 EndY=28.75 EndZ=0
    g39: LineSegment StartX=-49.19 StartY=25.75 StartZ=0 EndX=-16.28 EndY=25.75 EndZ=0
    g40: LineSegment StartX=-49.19 StartY=23 StartZ=0 EndX=-11.49 EndY=23 EndZ=0
    g41: LineSegment StartX=-49.19 StartY=20 StartZ=0 EndX=-11.49 EndY=20 EndZ=0
    g42: LineSegment StartX=-49.19 StartY=17.25 StartZ=0 EndX=-1.5 EndY=17.25 EndZ=0
    g43: LineSegment StartX=-49.19 StartY=14.25 StartZ=0 EndX=-1.5 EndY=14.25 EndZ=0
    g44: LineSegment StartX=-49.19 StartY=11.5 StartZ=0 EndX=-1.5 EndY=11.5 EndZ=0
    g45: LineSegment StartX=-49.19 StartY=8.5 StartZ=0 EndX=-1.5 EndY=8.5 EndZ=0
    g46: LineSegment StartX=-49.19 StartY=5.75 StartZ=0 EndX=-1.5 EndY=5.75 EndZ=0
    g47: LineSegment StartX=-49.19 StartY=2.75 StartZ=0 EndX=-1.5 EndY=2.75 EndZ=0
  constraints (120):
    c: Vertical(g0)
    c: Distance(g0) = 3
    c: Block(g0)
    c: Vertical(g1)
    c: Distance(g1) = 3
    c: Vertical(g2)
    c: Equal(g0,g2) = 3
    c: Block(g2)
    c: Vertical(g3)
    c: Equal(g1,g3) = 3
    c: Vertical(g4)
    c: Equal(g0,g4) = 3
    c: Block(g4)
    c: Vertical(g5)
    c: Equal(g1,g5) = 3
    c: Vertical(g6)
    c: Equal(g0,g6) = 3
    c: Block(g6)
    c: Vertical(g7)
    c: Equal(g1,g7) = 3
    c: Vertical(g8)
    c: Equal(g0,g8) = 3
    c: Block(g8)
    c: Vertical(g9)
    c: Equal(g1,g9) = 3
    c: Vertical(g10)
    c: Equal(g0,g10) = 3
    c: Block(g10)
    c: Vertical(g11)
    c: Equal(g1,g11) = 3
    c: Block(g12)
    c: Block(g13)
    c: Block(g14)
    c: Block(g15)
    c: Block(g16)
    c: Block(g17)
    c: Block(g18)
    c: Block(g19)
    c: Block(g20)
    c: Block(g21)
    c: Block(g22)
    c: Block(g23)
    c: Block(g11)
    c: Block(g9)
    c: Block(g7)
    c: Block(g5)
    c: Block(g3)
    c: Block(g1)
    c: Coincident(g24,g0)
    c: Coincident(g24,g12)
    c: Horizontal(g24)
    c: Coincident(g25,g0)
    c: Coincident(g25,g12)
    c: Horizontal(g25)
    c: Coincident(g26,g1)
    c: Coincident(g26,g13)
    c: Horizontal(g26)
    c: Coincident(g27,g1)
    c: Coincident(g27,g13)
    c: Horizontal(g27)
    c: Coincident(g28,g2)
    c: Coincident(g28,g14)
    c: Horizontal(g28)
    c: Coincident(g29,g2)
    c: Coincident(g29,g14)
    c: Horizontal(g29)
    c: Coincident(g30,g3)
    c: Coincident(g30,g15)
    c: Horizontal(g30)
    c: Coincident(g31,g3)
    c: Coincident(g31,g15)
    c: Horizontal(g31)
    c: Coincident(g32,g4)
    c: Coincident(g32,g16)
    c: Horizontal(g32)
    c: Coincident(g33,g4)
    c: Coincident(g33,g16)
    c: Horizontal(g33)
    c: Coincident(g34,g5)
    c: Coincident(g34,g17)
    c: Horizontal(g34)
    c: Coincident(g35,g5)
    c: Coincident(g35,g17)
    c: Horizontal(g35)
    c: Coincident(g36,g6)
    c: Coincident(g36,g19)
    c: Horizontal(g36)
    c: Coincident(g37,g6)
    c: Coincident(g37,g19)
    c: Horizontal(g37)
    c: Coincident(g38,g7)
    c: Coincident(g38,g18)
    c: Horizontal(g38)
    c: Coincident(g39,g7)
    c: Coincident(g39,g18)
    c: Horizontal(g39)
    c: Coincident(g40,g8)
    c: Coincident(g40,g20)
    c: Horizontal(g40)
    c: Coincident(g41,g8)
    c: Coincident(g41,g20)
    c: Horizontal(g41)
    c: Coincident(g42,g9)
    c: Coincident(g42,g23)
    c: Horizontal(g42)
    c: Coincident(g43,g9)
    c: Coincident(g43,g23)
    c: Horizontal(g43)
    c: Coincident(g44,g10)
    c: Coincident(g44,g22)
    c: Horizontal(g44)
    c: Coincident(g45,g10)
    c: Coincident(g45,g22)
    c: Horizontal(g45)
    c: Coincident(g46,g11)
    c: Coincident(g46,g21)
    c: Horizontal(g46)
    c: Coincident(g47,g11)
    c: Coincident(g47,g21)
    c: Horizontal(g47)
FEATURE [Part::Extrusion] Extrude046
  Base = -> Sketch055
  Dir = (1,0,0)
  DirMode = 2
  FaceMakerClass = Part::FaceMakerBullseye
  LengthFwd = 23
  LengthRev = 0
  Placement = pos=(-19,0,0) rot=(0,0,1;0rad)
  Solid = true
  Symmetric = false
FEATURE [Part::Fillet] Fillet038  label="removeToCreateVentalationHoles001"
  Base = -> Extrude046
  Edges = <same value as first occurrence — deduplicated (x6 in doc)>
  Placement = pos=(7,0,0) rot=(0,0,1;0rad)
FEATURE [Sketcher::SketchObject] Sketch056  label="topSketch014"
  FullyConstrained = true
  sketch-geometry (22):
    g0: LineSegment StartX=5.21097e-06 StartY=3 StartZ=0 EndX=5.21097e-06 EndY=19 EndZ=0
    g1: ArcOfCircle CenterX=19 CenterY=19 CenterZ=0 NormalX=0 NormalY=0 NormalZ=1 AngleXU=0 Radius=19 StartAngle=1.5708 EndAngle=3.14159
    g2: ArcOfCircle CenterX=19 CenterY=19 CenterZ=0 NormalX=0 NormalY=0 NormalZ=1 AngleXU=0 Radius=16 StartAngle=1.5708 EndAngle=3.14159
    g3: LineSegment StartX=114 StartY=35 StartZ=0 EndX=19 EndY=35 EndZ=0
    g4: LineSegment StartX=5.21097e-06 StartY=3 StartZ=0 EndX=5.21097e-06 EndY=0 EndZ=0
    g5: LineSegment StartX=3 StartY=0 StartZ=0 EndX=5.21097e-06 EndY=0 EndZ=0
    g6: LineSegment StartX=3 StartY=19 StartZ=0 EndX=3 EndY=0 EndZ=0
    g7: LineSegment StartX=19 StartY=38 StartZ=0 EndX=124 EndY=38 EndZ=0
    g8: Circle CenterX=119 CenterY=35 CenterZ=0 NormalX=0 NormalY=0 NormalZ=1 AngleXU=0 Radius=1
    g9: Circle CenterX=121 CenterY=35 CenterZ=0 NormalX=0 NormalY=0 NormalZ=1 AngleXU=0 Radius=1
    g10: Circle CenterX=121 CenterY=33 CenterZ=0 NormalX=0 NormalY=0 NormalZ=1 AngleXU=0 Radius=1
    g11: BSplineCurve PolesCount=3 KnotsCount=2 Degree=2 IsPeriodic=0
    g12: GeomPoint X=119 Y=35 Z=0
    g13: GeomPoint X=121 Y=33 Z=0
    g14: LineSegment StartX=119 StartY=35 StartZ=0 EndX=114 EndY=35 EndZ=0
    g15: ArcOfCircle CenterX=105 CenterY=19 CenterZ=0 NormalX=0 NormalY=0 NormalZ=1 AngleXU=0 Radius=16 StartAngle=5.60905 EndAngle=6.28319
    g16: LineSegment StartX=121 StartY=33 StartZ=0 EndX=121 EndY=19 EndZ=0
    g17: LineSegment StartX=117.5 StartY=9.01251 StartZ=0 EndX=121.163 EndY=9.0125 EndZ=0
    g18: ArcOfCircle CenterX=105 CenterY=19 CenterZ=0 NormalX=0 NormalY=0 NormalZ=1 AngleXU=0 Radius=20.6155 StartAngle=5.7297 EndAngle=6.28319
    g19: LineSegment StartX=121.163 StartY=9.0125 StartZ=0 EndX=122.538 EndY=8.16329 EndZ=0
    g20: LineSegment StartX=124 StartY=38 StartZ=0 EndX=125.616 EndY=38 EndZ=0
    g21: LineSegment StartX=125.616 StartY=19 StartZ=0 EndX=125.616 EndY=38 EndZ=0
  constraints (49):
    c: Vertical(g0)
    c: Block(g0)
    c: Coincident(g1,g0)
    c: Block(g1)
    c: Coincident(g2,g1)
    c: Block(g2)
    c: Coincident(g3,g2)
    c: Horizontal(g3)
    c: Tangent(g3,g2)
    c: Coincident(g4,g0)
    c: Distance(g4) = 3
    c: Vertical(g4)
    c: Coincident(g5,g4)
    c: Horizontal(g5)
    c: Coincident(g6,g2)
    c: Coincident(g6,g5)
    c: Vertical(g6)
    c: Horizontal(g7)
    c: Distance(g7) = 105
    c: Coincident(g7,g1)
    c: Block(g3)
    c: Weight(g8) = 1
    c: Equal(g8,g9)
    c: Equal(g8,g10)
    c: InternalAlignment(g8,g11)
    c: InternalAlignment(g9,g11)
    c: InternalAlignment(g10,g11)
    c: InternalAlignment(g12,g11)
    c: InternalAlignment(g13,g11)
    c: Block(g11)
    c: Coincident(g14,g11)
    c: Coincident(g14,g3)
    c: Horizontal(g14)
    c: Block(g15)
    c: Coincident(g16,g11)
    c: Coincident(g16,g15)
    c: Vertical(g16)
    c: Distance(g16) = 14
    c: Coincident(g17,g15)
    c: Block(g18)
    c: Coincident(g19,g18)
    c: Coincident(g20,g7)
    c: Horizontal(g20)
    c: Vertical(g21)
    c: Coincident(g20,g21)
    c: Block(g20)
    c: Block(g21)
    c: Block(g19)
    c: Block(g17)
FEATURE [Part::Box] Box026  label="removeToCreteHoleForPlugHousing032"
  AttacherType = Attacher::AttachEngine3D
  Height = 28.6
  Length = 10
  Placement = pos=(-2,0,21.7) rot=(0,0,1;0rad)
  Width = 19
FEATURE [Part::Feature] Face109 .. Face112  x4 (patterned run collapsed; names and placements below)
  shape: bbox 3.5 x 17.8 x 2e-07 mm, 1 faces, 0 solids (baked)
FEATURE [Part::Revolution] Revolve117  label="removeToCreateScrewAndThreadedInsertHole045"
  Angle = 360
  Axis = (0,1,0)
  Base = (0,0,0)
  FaceMakerClass = Part::FaceMakerBullseye
  Placement = pos=(62.3,30.3,19.7) rot=(0,0,1;0rad)
  Solid = false
  Source = -> Face109
  Symmetric = false
FEATURE [Part::Revolution] Revolve118  label="removeToCreateScrewAndThreadedInsertHole046"
  Angle = 360
  Axis = (0,1,0)
  Base = (0,0,0)
  FaceMakerClass = Part::FaceMakerBullseye
  Placement = pos=(62.3,30.3,51.7) rot=(0,0,1;0rad)
  Solid = false
  Source = -> Face110
  Symmetric = false
FEATURE [Part::Revolution] Revolve119  label="removeToCreateScrewAndThreadedInsertHole047"
  Angle = 360
  Axis = (0,1,0)
  Base = (0,0,0)
  FaceMakerClass = Part::FaceMakerBullseye
  Placement = pos=(30.3,30.3,19.7) rot=(0,0,1;0rad)
  Solid = false
  Source = -> Face111
  Symmetric = false
FEATURE [Part::Revolution] Revolve120  label="removeToCreateScrewAndThreadedInsertHole048"
  Angle = 360
  Axis = (0,1,0)
  Base = (0,0,0)
  FaceMakerClass = Part::FaceMakerBullseye
  Placement = pos=(30.3,30.3,51.7) rot=(0,0,1;0rad)
  Solid = false
  Source = -> Face112
  Symmetric = false
FEATURE [Part::MultiFuse] Fusion087  label="createThreadedInsertHolesForFan005"
  Shapes = -> [Revolve117,Revolve118,Revolve119,Revolve120]
FEATURE [Part::Extrusion] Extrude047
  Base = -> Sketch056
  Dir = (0,0,1)
  DirMode = 2
  FaceMakerClass = Part::FaceMakerBullseye
  LengthFwd = 72
  LengthRev = 0
  Solid = true
  Symmetric = false
FEATURE [Part::Fillet] Fillet039  label="top019"
  Base = -> Extrude047
  Edges = 1 edges r=2: [Edge35]
FEATURE [Sketcher::SketchObject] Sketch057
  FullyConstrained = false
  Placement = pos=(0,0,0) rot=(1,0,0;1.5708rad)
  sketch-geometry (24):
    g0: ArcOfCircle CenterX=-4 CenterY=-10.5 CenterZ=0 NormalX=0 NormalY=0 NormalZ=1 AngleXU=0 Radius=1.5 StartAngle=6e-16 EndAngle=3.14159
    g1: ArcOfCircle CenterX=-34.2 CenterY=-10.5 CenterZ=0 NormalX=0 NormalY=0 NormalZ=1 AngleXU=0 Radius=1.5 StartAngle=0 EndAngle=3.14159
    g2: ArcOfCircle CenterX=-34.2 CenterY=-27.7 CenterZ=0 NormalX=0 NormalY=0 NormalZ=1 AngleXU=0 Radius=1.5 StartAngle=3.14159 EndAngle=6.28319
    g3: ArcOfCircle CenterX=-4 CenterY=-27.7 CenterZ=0 NormalX=0 NormalY=0 NormalZ=1 AngleXU=0 Radius=1.5 StartAngle=3.1416 EndAngle=6.28319
    g4: ArcOfCircle CenterX=-10 CenterY=-4.3 CenterZ=0 NormalX=0 NormalY=0 NormalZ=1 AngleXU=0 Radius=1.5 StartAngle=2e-16 EndAngle=3.14159
    g5: ArcOfCircle CenterX=-16.1 CenterY=-1.8 CenterZ=0 NormalX=0 NormalY=0 NormalZ=1 AngleXU=0 Radius=1.5 StartAngle=5e-16 EndAngle=3.14159
    g6: ArcOfCircle CenterX=-22.1 CenterY=-1.8 CenterZ=0 NormalX=0 NormalY=0 NormalZ=1 AngleXU=0 Radius=1.5 StartAngle=5e-16 EndAngle=3.14159
    g7: ArcOfCircle CenterX=-28.2 CenterY=-4.3 CenterZ=0 NormalX=0 NormalY=0 NormalZ=1 AngleXU=0 Radius=1.5 StartAngle=2e-16 EndAngle=3.14159
    g8: ArcOfCircle CenterX=-10 CenterY=-33.9 CenterZ=0 NormalX=0 NormalY=0 NormalZ=1 AngleXU=0 Radius=1.5 StartAngle=3.14159 EndAngle=6.28319
    g9: ArcOfCircle CenterX=-16.1 CenterY=-36.4 CenterZ=0 NormalX=0 NormalY=0 NormalZ=1 AngleXU=0 Radius=1.5 StartAngle=3.14159 EndAngle=6.28319
    g10: ArcOfCircle CenterX=-22.1 CenterY=-36.4 CenterZ=0 NormalX=0 NormalY=0 NormalZ=1 AngleXU=0 Radius=1.5 StartAngle=3.14159 EndAngle=6.28319
    g11: ArcOfCircle CenterX=-28.2 CenterY=-33.9 CenterZ=0 NormalX=0 NormalY=0 NormalZ=1 AngleXU=0 Radius=1.5 StartAngle=3.14159 EndAngle=6.28319
    g12: LineSegment StartX=-35.7 StartY=-10.5 StartZ=0 EndX=-35.7 EndY=-27.7 EndZ=0
    g13: LineSegment StartX=-32.7 StartY=-10.5 StartZ=0 EndX=-32.7 EndY=-27.7 EndZ=0
    g14: LineSegment StartX=-29.7 StartY=-33.9 StartZ=0 EndX=-29.7 EndY=-4.3 EndZ=0
    g15: LineSegment StartX=-26.7 StartY=-33.9 StartZ=0 EndX=-26.7 EndY=-4.3 EndZ=0
    g16: LineSegment StartX=-2.5 StartY=-10.5 StartZ=0 EndX=-2.5 EndY=-27.7 EndZ=0
    g17: LineSegment StartX=-8.5 StartY=-4.3 StartZ=0 EndX=-8.5 EndY=-33.9 EndZ=0
    g18: LineSegment StartX=-5.5 StartY=-10.5 StartZ=0 EndX=-5.5 EndY=-27.7 EndZ=0
    g19: LineSegment StartX=-11.5 StartY=-4.3 StartZ=0 EndX=-11.5 EndY=-33.9 EndZ=0
    g20: LineSegment StartX=-14.6 StartY=-1.8 StartZ=0 EndX=-14.6 EndY=-36.4 EndZ=0
    g21: LineSegment StartX=-17.6 StartY=-1.8 StartZ=0 EndX=-17.6 EndY=-36.4 EndZ=0
    g22: LineSegment StartX=-20.6 StartY=-36.4 StartZ=0 EndX=-20.6 EndY=-1.8 EndZ=0
    g23: LineSegment StartX=-23.6 StartY=-1.8 StartZ=0 EndX=-23.6 EndY=-36.4 EndZ=0
  constraints (48):
    c: Block(g0)
    c: Block(g1)
    c: Block(g2)
    c: Block(g3)
    c: Block(g4)
    c: Block(g5)
    c: Block(g6)
    c: Block(g7)
    c: Block(g8)
    c: Block(g9)
    c: Block(g10)
    c: Block(g11)
    c: Coincident(g12,g1)
    c: Coincident(g12,g2)
    c: Vertical(g12)
    c: Coincident(g13,g1)
    c: Coincident(g13,g2)
    c: Vertical(g13)
    c: Coincident(g14,g11)
    c: Coincident(g14,g7)
    c: Vertical(g14)
    c: Coincident(g15,g11)
    c: Coincident(g15,g7)
    c: Vertical(g15)
    c: Coincident(g16,g0)
    c: Coincident(g16,g3)
    c: Vertical(g16)
    c: Coincident(g17,g4)
    c: Coincident(g17,g8)
    c: Vertical(g17)
    c: Coincident(g18,g0)
    c: Coincident(g18,g3)
    c: Vertical(g18)
    c: Coincident(g19,g4)
    c: Coincident(g19,g8)
    c: Vertical(g19)
    c: Coincident(g20,g5)
    c: Coincident(g20,g9)
    c: Vertical(g20)
    c: Coincident(g21,g5)
    c: Coincident(g21,g9)
    c: Vertical(g21)
    c: Coincident(g22,g10)
    c: Coincident(g22,g6)
    c: Vertical(g22)
    c: Coincident(g23,g6)
    c: Coincident(g23,g10)
    c: Vertical(g23)
FEATURE [Part::Extrusion] Extrude048  label="removeToCreateFanGrillHoles004"
  Base = -> Sketch057
  Dir = (0,-1,6e-16)
  DirMode = 2
  FaceMakerClass = Part::FaceMakerBullseye
  LengthFwd = 10
  LengthRev = 0
  Placement = pos=(65.4,44,54.82) rot=(0,0,1;0rad)
  Solid = true
  Symmetric = false
FEATURE [Part::Cut] Cut040  label="top021"
  Base = -> Fillet039
  Tool = -> Extrude048
FEATURE [Part::Cylinder] Cylinder041  label="removeToCreteHoleForPlugHousing034"
  Angle = 360
  AttacherType = Attacher::AttachEngine3D
  Height = 20
  Placement = pos=(-2,19,36) rot=(0,1,0;1.5708rad)
  Radius = 14.3
FEATURE [Part::MultiFuse] Fusion089  label="removeToCreteHoleForPlugHousing035"
  Shapes = -> [Box026,Cylinder041]
FEATURE [Part::Cylinder] Cylinder042
  Angle = 360
  AttacherType = Attacher::AttachEngine3D
  Height = 20
  Placement = pos=(0,0,36.15) rot=(0,0,1;0rad)
  Radius = 14.3
FEATURE [Part::Cylinder] Cylinder043
  Angle = 360
  AttacherType = Attacher::AttachEngine3D
  Height = 10
  Placement = pos=(0,0,36.15) rot=(0,0,1;0rad)
  Radius = 4
FEATURE [Part::Box] Box027  label="removeToCreteHoleForPlugHousing036"
  AttacherType = Attacher::AttachEngine3D
  Height = 28.6
  Length = 20
  Placement = pos=(106.15,0,21.7) rot=(0,0,1;0rad)
  Width = 19
FEATURE [Part::Cut] Cut041  label="top022"
  Base = -> Cut040
  Tool = -> Fusion087
FEATURE [Part::Cut] Cut039  label="top020"
  Base = -> Cut041
  Tool = -> Fusion089
FEATURE [Part::MultiFuse] Fusion090  label="removeToCreteHoleForPlugHousing037"
  Placement = pos=(70,19,36) rot=(0,1,0;1.5708rad)
  Shapes = -> [Cylinder042,Cylinder043]
FEATURE [Part::MultiFuse] Fusion088  label="removeToCreteHoleForPlugHousing033"
  Shapes = -> [Box027,Fusion090]
FEATURE [Part::Cut] Cut042  label="removeToCreteHoleForPlugHousing038"
  Base = -> Cut039
  Tool = -> Fusion088
FEATURE [Part::MultiFuse] Fusion091  label="removeFromTop"
  Shapes = -> [Fillet038,Fusion085,Fusion084,Fusion083,Extrude045]
FEATURE [Part::Cut] Cut043  label="REAL TOP ====="
  Base = -> Fillet036
  Tool = -> Fusion091
FEATURE [Part::MultiFuse] Fusion092  label="caseScrewPillarBracket016"
  Shapes = -> [Extrude030,Extrude031,Extrude032,Extrude033,Extrude034,Extrude035,Extrude036,Extrude037,Box013,Box014]
FEATURE [Sketcher::SketchObject] Sketch058  label="topSketch015"
  FullyConstrained = true
  sketch-geometry (20):
    g0: LineSegment StartX=5.21097e-06 StartY=3 StartZ=0 EndX=5.21097e-06 EndY=19 EndZ=0
    g1: ArcOfCircle CenterX=19 CenterY=19 CenterZ=0 NormalX=0 NormalY=0 NormalZ=1 AngleXU=0 Radius=19 StartAngle=1.5708 EndAngle=3.14159
    g2: ArcOfCircle CenterX=19 CenterY=19 CenterZ=0 NormalX=0 NormalY=0 NormalZ=1 AngleXU=0 Radius=16 StartAngle=1.5708 EndAngle=3.14159
    g3: LineSegment StartX=114 StartY=35 StartZ=0 EndX=19 EndY=35 EndZ=0
    g4: LineSegment StartX=5.21097e-06 StartY=3 StartZ=0 EndX=5.21097e-06 EndY=0 EndZ=0
    g5: LineSegment StartX=3 StartY=0 StartZ=0 EndX=5.21097e-06 EndY=0 EndZ=0
    g6: LineSegment StartX=3 StartY=19 StartZ=0 EndX=3 EndY=0 EndZ=0
    g7: LineSegment StartX=19 StartY=38 StartZ=0 EndX=124 EndY=38 EndZ=0
    g8: Circle CenterX=119 CenterY=35 CenterZ=0 NormalX=0 NormalY=0 NormalZ=1 AngleXU=0 Radius=1
    g9: Circle CenterX=121 CenterY=35 CenterZ=0 NormalX=0 NormalY=0 NormalZ=1 AngleXU=0 Radius=1
    g10: Circle CenterX=121 CenterY=33 CenterZ=0 NormalX=0 NormalY=0 NormalZ=1 AngleXU=0 Radius=1
    g11: BSplineCurve PolesCount=3 KnotsCount=2 Degree=2 IsPeriodic=0
    g12: GeomPoint X=119 Y=35 Z=0
    g13: GeomPoint X=121 Y=33 Z=0
    g14: LineSegment StartX=119 StartY=35 StartZ=0 EndX=114 EndY=35 EndZ=0
    g15: ArcOfCircle CenterX=105 CenterY=19 CenterZ=0 NormalX=0 NormalY=0 NormalZ=1 AngleXU=0 Radius=19 StartAngle=5.7297 EndAngle=6.28319
    g16: ArcOfCircle CenterX=105 CenterY=19 CenterZ=0 NormalX=0 NormalY=0 NormalZ=1 AngleXU=0 Radius=16 StartAngle=5.60905 EndAngle=6.28319
    g17: LineSegment StartX=121 StartY=33 StartZ=0 EndX=121 EndY=19 EndZ=0
    g18: LineSegment StartX=124 StartY=38 StartZ=0 EndX=124 EndY=19 EndZ=0
    g19: LineSegment StartX=117.5 StartY=9.01251 StartZ=0 EndX=121.163 EndY=9.0125 EndZ=0
  constraints (46):
    c: Vertical(g0)
    c: Block(g0)
    c: Coincident(g1,g0)
    c: Block(g1)
    c: Coincident(g2,g1)
    c: Block(g2)
    c: Coincident(g3,g2)
    c: Horizontal(g3)
    c: Tangent(g3,g2)
    c: Coincident(g4,g0)
    c: Distance(g4) = 3
    c: Vertical(g4)
    c: Coincident(g5,g4)
    c: Horizontal(g5)
    c: Coincident(g6,g2)
    c: Coincident(g6,g5)
    c: Vertical(g6)
    c: Horizontal(g7)
    c: Distance(g7) = 105
    c: Coincident(g7,g1)
    c: Block(g3)
    c: Weight(g8) = 1
    c: Equal(g8,g9)
    c: Equal(g8,g10)
    c: InternalAlignment(g8,g11)
    c: InternalAlignment(g9,g11)
    c: InternalAlignment(g10,g11)
    c: InternalAlignment(g12,g11)
    c: InternalAlignment(g13,g11)
    c: Block(g11)
    c: Coincident(g14,g11)
    c: Coincident(g14,g3)
    c: Horizontal(g14)
    c: Block(g15)
    c: Coincident(g16,g15)
    c: Block(g16)
    c: Coincident(g17,g11)
    c: Coincident(g17,g16)
    c: Vertical(g17)
    c: Distance(g17) = 14
    c: Coincident(g18,g7)
    c: Coincident(g18,g15)
    c: Vertical(g18)
    c: Distance(g18) = 19
    c: Coincident(g19,g16)
    c: Coincident(g19,g15)
FEATURE [Part::Extrusion] Extrude049  label="top023"
  Base = -> Sketch058
  Dir = (0,0,1)
  DirMode = 2
  FaceMakerClass = Part::FaceMakerBullseye
  LengthFwd = 72
  LengthRev = 0
  Solid = true
  Symmetric = false
FEATURE [Sketcher::SketchObject] Sketch059
  FullyConstrained = true
  MapMode = 3
  Placement = pos=(0,0,0) rot=(1,0,0;1.5708rad)
  Support = -> [Extrude049]
  sketch-geometry (8):
    g0: Circle CenterX=80.351 CenterY=-67.6202 CenterZ=0 NormalX=0 NormalY=0 NormalZ=1 AngleXU=0 Radius=2
    g1: Circle CenterX=80.351 CenterY=-67.6202 CenterZ=0 NormalX=0 NormalY=0 NormalZ=1 AngleXU=0 Radius=3
    g2: Circle CenterX=80.351 CenterY=-4.92017 CenterZ=0 NormalX=0 NormalY=0 NormalZ=1 AngleXU=0 Radius=2
    g3: Circle CenterX=80.351 CenterY=-4.92017 CenterZ=0 NormalX=0 NormalY=0 NormalZ=1 AngleXU=0 Radius=3
    g4: Circle CenterX=23.851 CenterY=-4.92017 CenterZ=0 NormalX=0 NormalY=0 NormalZ=1 AngleXU=0 Radius=2
    g5: Circle CenterX=23.851 CenterY=-4.92017 CenterZ=0 NormalX=0 NormalY=0 NormalZ=1 AngleXU=0 Radius=3
    g6: Circle CenterX=23.851 CenterY=-67.6202 CenterZ=0 NormalX=0 NormalY=0 NormalZ=1 AngleXU=0 Radius=2
    g7: Circle CenterX=23.851 CenterY=-67.6202 CenterZ=0 NormalX=0 NormalY=0 NormalZ=1 AngleXU=0 Radius=3
  constraints (8):
    c: Block(g3)
    c: Block(g2)
    c: Block(g1)
    c: Block(g0)
    c: Block(g6)
    c: Block(g7)
    c: Block(g4)
    c: Block(g5)
FEATURE [Sketcher::SketchObject] Sketch060
  FullyConstrained = true
  MapMode = 3
  Placement = pos=(0,0,0) rot=(1,0,0;1.5708rad)
  Support = -> [Extrude049]
  sketch-geometry (8):
    g0: Circle CenterX=80.351 CenterY=-67.6202 CenterZ=0 NormalX=0 NormalY=0 NormalZ=1 AngleXU=0 Radius=3
    g1: Circle CenterX=80.351 CenterY=-4.92017 CenterZ=0 NormalX=0 NormalY=0 NormalZ=1 AngleXU=0 Radius=3
    g2: Circle CenterX=23.851 CenterY=-4.92017 CenterZ=0 NormalX=0 NormalY=0 NormalZ=1 AngleXU=0 Radius=3
    g3: Circle CenterX=23.851 CenterY=-67.6202 CenterZ=0 NormalX=0 NormalY=0 NormalZ=1 AngleXU=0 Radius=3
    g4: Circle CenterX=23.851 CenterY=-67.6202 CenterZ=0 NormalX=0 NormalY=0 NormalZ=1 AngleXU=0 Radius=5
    g5: Circle CenterX=80.351 CenterY=-67.6202 CenterZ=0 NormalX=0 NormalY=0 NormalZ=1 AngleXU=0 Radius=5
    g6: Circle CenterX=23.851 CenterY=-4.92017 CenterZ=0 NormalX=0 NormalY=0 NormalZ=1 AngleXU=0 Radius=5
    g7: Circle CenterX=80.351 CenterY=-4.92017 CenterZ=0 NormalX=0 NormalY=0 NormalZ=1 AngleXU=0 Radius=5
  constraints (8):
    c: Block(g1)
    c: Block(g0)
    c: Block(g3)
    c: Block(g2)
    c: Block(g5)
    c: Block(g4)
    c: Block(g6)
    c: Block(g7)
FEATURE [Sketcher::SketchObject] Sketch061
  FullyConstrained = true
  MapMode = 3
  Placement = pos=(0,0,0) rot=(1,0,0;1.5708rad)
  sketch-geometry (8):
    g0: Circle CenterX=80.351 CenterY=-67.6202 CenterZ=0 NormalX=0 NormalY=0 NormalZ=1 AngleXU=0 Radius=3
    g1: Circle CenterX=80.351 CenterY=-4.92017 CenterZ=0 NormalX=0 NormalY=0 NormalZ=1 AngleXU=0 Radius=3
    g2: Circle CenterX=23.851 CenterY=-4.92017 CenterZ=0 NormalX=0 NormalY=0 NormalZ=1 AngleXU=0 Radius=3
    g3: Circle CenterX=23.851 CenterY=-67.6202 CenterZ=0 NormalX=0 NormalY=0 NormalZ=1 AngleXU=0 Radius=3
    g4: Circle CenterX=23.851 CenterY=-67.6202 CenterZ=0 NormalX=0 NormalY=0 NormalZ=1 AngleXU=0 Radius=5
    g5: Circle CenterX=80.351 CenterY=-67.6202 CenterZ=0 NormalX=0 NormalY=0 NormalZ=1 AngleXU=0 Radius=5
    g6: Circle CenterX=23.851 CenterY=-4.92017 CenterZ=0 NormalX=0 NormalY=0 NormalZ=1 AngleXU=0 Radius=5
    g7: Circle CenterX=80.351 CenterY=-4.92017 CenterZ=0 NormalX=0 NormalY=0 NormalZ=1 AngleXU=0 Radius=5
  constraints (8):
    c: Block(g1)
    c: Block(g0)
    c: Block(g3)
    c: Block(g2)
    c: Block(g5)
    c: Block(g4)
    c: Block(g6)
    c: Block(g7)
FEATURE [Sketcher::SketchObject] Sketch062  label="topSketch016"
  FullyConstrained = true
  sketch-geometry (20):
    g0: LineSegment StartX=5.21097e-06 StartY=3 StartZ=0 EndX=5.21097e-06 EndY=19 EndZ=0
    g1: ArcOfCircle CenterX=19 CenterY=19 CenterZ=0 NormalX=0 NormalY=0 NormalZ=1 AngleXU=0 Radius=19 StartAngle=1.5708 EndAngle=3.14159
    g2: ArcOfCircle CenterX=19 CenterY=19 CenterZ=0 NormalX=0 NormalY=0 NormalZ=1 AngleXU=0 Radius=16 StartAngle=1.5708 EndAngle=3.14159
    g3: LineSegment StartX=114 StartY=35 StartZ=0 EndX=19 EndY=35 EndZ=0
    g4: LineSegment StartX=5.21097e-06 StartY=3 StartZ=0 EndX=5.21097e-06 EndY=0 EndZ=0
    g5: LineSegment StartX=3 StartY=0 StartZ=0 EndX=5.21097e-06 EndY=0 EndZ=0
    g6: LineSegment StartX=3 StartY=19 StartZ=0 EndX=3 EndY=0 EndZ=0
    g7: LineSegment StartX=19 StartY=38 StartZ=0 EndX=124 EndY=38 EndZ=0
    g8: Circle CenterX=119 CenterY=35 CenterZ=0 NormalX=0 NormalY=0 NormalZ=1 AngleXU=0 Radius=1
    g9: Circle CenterX=121 CenterY=35 CenterZ=0 NormalX=0 NormalY=0 NormalZ=1 AngleXU=0 Radius=1
    g10: Circle CenterX=121 CenterY=33 CenterZ=0 NormalX=0 NormalY=0 NormalZ=1 AngleXU=0 Radius=1
    g11: BSplineCurve PolesCount=3 KnotsCount=2 Degree=2 IsPeriodic=0
    g12: GeomPoint X=119 Y=35 Z=0
    g13: GeomPoint X=121 Y=33 Z=0
    g14: LineSegment StartX=119 StartY=35 StartZ=0 EndX=114 EndY=35 EndZ=0
    g15: ArcOfCircle CenterX=105 CenterY=19 CenterZ=0 NormalX=0 NormalY=0 NormalZ=1 AngleXU=0 Radius=19 StartAngle=5.7297 EndAngle=6.28319
    g16: ArcOfCircle CenterX=105 CenterY=19 CenterZ=0 NormalX=0 NormalY=0 NormalZ=1 AngleXU=0 Radius=16 StartAngle=5.60905 EndAngle=6.28319
    g17: LineSegment StartX=121 StartY=33 StartZ=0 EndX=121 EndY=19 EndZ=0
    g18: LineSegment StartX=124 StartY=38 StartZ=0 EndX=124 EndY=19 EndZ=0
    g19: LineSegment StartX=117.5 StartY=9.01251 StartZ=0 EndX=121.163 EndY=9.0125 EndZ=0
  constraints (46):
    c: Vertical(g0)
    c: Block(g0)
    c: Coincident(g1,g0)
    c: Block(g1)
    c: Coincident(g2,g1)
    c: Block(g2)
    c: Coincident(g3,g2)
    c: Horizontal(g3)
    c: Tangent(g3,g2)
    c: Coincident(g4,g0)
    c: Distance(g4) = 3
    c: Vertical(g4)
    c: Coincident(g5,g4)
    c: Horizontal(g5)
    c: Coincident(g6,g2)
    c: Coincident(g6,g5)
    c: Vertical(g6)
    c: Horizontal(g7)
    c: Distance(g7) = 105
    c: Coincident(g7,g1)
    c: Block(g3)
    c: Weight(g8) = 1
    c: Equal(g8,g9)
    c: Equal(g8,g10)
    c: InternalAlignment(g8,g11)
    c: InternalAlignment(g9,g11)
    c: InternalAlignment(g10,g11)
    c: InternalAlignment(g12,g11)
    c: InternalAlignment(g13,g11)
    c: Block(g11)
    c: Coincident(g14,g11)
    c: Coincident(g14,g3)
    c: Horizontal(g14)
    c: Block(g15)
    c: Coincident(g16,g15)
    c: Block(g16)
    c: Coincident(g17,g11)
    c: Coincident(g17,g16)
    c: Vertical(g17)
    c: Distance(g17) = 14
    c: Coincident(g18,g7)
    c: Coincident(g18,g15)
    c: Vertical(g18)
    c: Distance(g18) = 19
    c: Coincident(g19,g16)
    c: Coincident(g19,g15)
FEATURE [Part::Extrusion] Extrude053  label="top024"
  Base = -> Sketch062
  Dir = (0,0,1)
  DirMode = 2
  FaceMakerClass = Part::FaceMakerBullseye
  LengthFwd = 72
  LengthRev = 0
  Solid = true
  Symmetric = false
FEATURE [Sketcher::SketchObject] Sketch063
  FullyConstrained = true
  MapMode = 3
  Placement = pos=(0,0,0) rot=(1,0,0;1.5708rad)
  Support = -> [Extrude053]
  sketch-geometry (8):
    g0: Circle CenterX=80.351 CenterY=-67.6202 CenterZ=0 NormalX=0 NormalY=0 NormalZ=1 AngleXU=0 Radius=2
    g1: Circle CenterX=80.351 CenterY=-67.6202 CenterZ=0 NormalX=0 NormalY=0 NormalZ=1 AngleXU=0 Radius=3
    g2: Circle CenterX=80.351 CenterY=-4.92017 CenterZ=0 NormalX=0 NormalY=0 NormalZ=1 AngleXU=0 Radius=2
    g3: Circle CenterX=80.351 CenterY=-4.92017 CenterZ=0 NormalX=0 NormalY=0 NormalZ=1 AngleXU=0 Radius=3
    g4: Circle CenterX=23.851 CenterY=-4.92017 CenterZ=0 NormalX=0 NormalY=0 NormalZ=1 AngleXU=0 Radius=2
    g5: Circle CenterX=23.851 CenterY=-4.92017 CenterZ=0 NormalX=0 NormalY=0 NormalZ=1 AngleXU=0 Radius=3
    g6: Circle CenterX=23.851 CenterY=-67.6202 CenterZ=0 NormalX=0 NormalY=0 NormalZ=1 AngleXU=0 Radius=2
    g7: Circle CenterX=23.851 CenterY=-67.6202 CenterZ=0 NormalX=0 NormalY=0 NormalZ=1 AngleXU=0 Radius=3
  constraints (8):
    c: Block(g3)
    c: Block(g2)
    c: Block(g1)
    c: Block(g0)
    c: Block(g6)
    c: Block(g7)
    c: Block(g4)
    c: Block(g5)
FEATURE [Part::Extrusion] Extrude054
  Base = -> Sketch063
  Dir = (0,-1,2e-16)
  DirMode = 2
  FaceMakerClass = Part::FaceMakerBullseye
  LengthFwd = 6
  LengthRev = 0
  Placement = pos=(0,9,0) rot=(0,0,1;0rad)
  Solid = true
  Symmetric = false
FEATURE [Sketcher::SketchObject] Sketch064  label="topSketch017"
  FullyConstrained = true
  sketch-geometry (20):
    g0: LineSegment StartX=5.21097e-06 StartY=3 StartZ=0 EndX=5.21097e-06 EndY=19 EndZ=0
    g1: ArcOfCircle CenterX=19 CenterY=19 CenterZ=0 NormalX=0 NormalY=0 NormalZ=1 AngleXU=0 Radius=19 StartAngle=1.5708 EndAngle=3.14159
    g2: ArcOfCircle CenterX=19 CenterY=19 CenterZ=0 NormalX=0 NormalY=0 NormalZ=1 AngleXU=0 Radius=16 StartAngle=1.5708 EndAngle=3.14159
    g3: LineSegment StartX=114 StartY=35 StartZ=0 EndX=19 EndY=35 EndZ=0
    g4: LineSegment StartX=5.21097e-06 StartY=3 StartZ=0 EndX=5.21097e-06 EndY=0 EndZ=0
    g5: LineSegment StartX=3 StartY=0 StartZ=0 EndX=5.21097e-06 EndY=0 EndZ=0
    g6: LineSegment StartX=3 StartY=19 StartZ=0 EndX=3 EndY=0 EndZ=0
    g7: LineSegment StartX=19 StartY=38 StartZ=0 EndX=124 EndY=38 EndZ=0
    g8: Circle CenterX=119 CenterY=35 CenterZ=0 NormalX=0 NormalY=0 NormalZ=1 AngleXU=0 Radius=1
    g9: Circle CenterX=121 CenterY=35 CenterZ=0 NormalX=0 NormalY=0 NormalZ=1 AngleXU=0 Radius=1
    g10: Circle CenterX=121 CenterY=33 CenterZ=0 NormalX=0 NormalY=0 NormalZ=1 AngleXU=0 Radius=1
    g11: BSplineCurve PolesCount=3 KnotsCount=2 Degree=2 IsPeriodic=0
    g12: GeomPoint X=119 Y=35 Z=0
    g13: GeomPoint X=121 Y=33 Z=0
    g14: LineSegment StartX=119 StartY=35 StartZ=0 EndX=114 EndY=35 EndZ=0
    g15: ArcOfCircle CenterX=105 CenterY=19 CenterZ=0 NormalX=0 NormalY=0 NormalZ=1 AngleXU=0 Radius=19 StartAngle=5.7297 EndAngle=6.28319
    g16: ArcOfCircle CenterX=105 CenterY=19 CenterZ=0 NormalX=0 NormalY=0 NormalZ=1 AngleXU=0 Radius=16 StartAngle=5.60905 EndAngle=6.28319
    g17: LineSegment StartX=121 StartY=33 StartZ=0 EndX=121 EndY=19 EndZ=0
    g18: LineSegment StartX=124 StartY=38 StartZ=0 EndX=124 EndY=19 EndZ=0
    g19: LineSegment StartX=117.5 StartY=9.01251 StartZ=0 EndX=121.163 EndY=9.0125 EndZ=0
  constraints (46):
    c: Vertical(g0)
    c: Block(g0)
    c: Coincident(g1,g0)
    c: Block(g1)
    c: Coincident(g2,g1)
    c: Block(g2)
    c: Coincident(g3,g2)
    c: Horizontal(g3)
    c: Tangent(g3,g2)
    c: Coincident(g4,g0)
    c: Distance(g4) = 3
    c: Vertical(g4)
    c: Coincident(g5,g4)
    c: Horizontal(g5)
    c: Coincident(g6,g2)
    c: Coincident(g6,g5)
    c: Vertical(g6)
    c: Horizontal(g7)
    c: Distance(g7) = 105
    c: Coincident(g7,g1)
    c: Block(g3)
    c: Weight(g8) = 1
    c: Equal(g8,g9)
    c: Equal(g8,g10)
    c: InternalAlignment(g8,g11)
    c: InternalAlignment(g9,g11)
    c: InternalAlignment(g10,g11)
    c: InternalAlignment(g12,g11)
    c: InternalAlignment(g13,g11)
    c: Block(g11)
    c: Coincident(g14,g11)
    c: Coincident(g14,g3)
    c: Horizontal(g14)
    c: Block(g15)
    c: Coincident(g16,g15)
    c: Block(g16)
    c: Coincident(g17,g11)
    c: Coincident(g17,g16)
    c: Vertical(g17)
    c: Distance(g17) = 14
    c: Coincident(g18,g7)
    c: Coincident(g18,g15)
    c: Vertical(g18)
    c: Distance(g18) = 19
    c: Coincident(g19,g16)
    c: Coincident(g19,g15)
FEATURE [Sketcher::SketchObject] Sketch065
  FullyConstrained = true
  MapMode = 3
  Placement = pos=(0,0,0) rot=(1,0,0;1.5708rad)
  sketch-geometry (8):
    g0: Circle CenterX=80.351 CenterY=-67.6202 CenterZ=0 NormalX=0 NormalY=0 NormalZ=1 AngleXU=0 Radius=3
    g1: Circle CenterX=80.351 CenterY=-4.92017 CenterZ=0 NormalX=0 NormalY=0 NormalZ=1 AngleXU=0 Radius=3
    g2: Circle CenterX=23.851 CenterY=-4.92017 CenterZ=0 NormalX=0 NormalY=0 NormalZ=1 AngleXU=0 Radius=3
    g3: Circle CenterX=23.851 CenterY=-67.6202 CenterZ=0 NormalX=0 NormalY=0 NormalZ=1 AngleXU=0 Radius=3
    g4: Circle CenterX=23.851 CenterY=-67.6202 CenterZ=0 NormalX=0 NormalY=0 NormalZ=1 AngleXU=0 Radius=5
    g5: Circle CenterX=80.351 CenterY=-67.6202 CenterZ=0 NormalX=0 NormalY=0 NormalZ=1 AngleXU=0 Radius=5
    g6: Circle CenterX=23.851 CenterY=-4.92017 CenterZ=0 NormalX=0 NormalY=0 NormalZ=1 AngleXU=0 Radius=5
    g7: Circle CenterX=80.351 CenterY=-4.92017 CenterZ=0 NormalX=0 NormalY=0 NormalZ=1 AngleXU=0 Radius=5
  constraints (8):
    c: Block(g1)
    c: Block(g0)
    c: Block(g3)
    c: Block(g2)
    c: Block(g5)
    c: Block(g4)
    c: Block(g6)
    c: Block(g7)
FEATURE [Part::Extrusion] Extrude056
  Base = -> Sketch065
  Dir = (0,-1,2e-16)
  DirMode = 2
  FaceMakerClass = Part::FaceMakerBullseye
  LengthFwd = 2
  LengthRev = 0
  Solid = true
  Symmetric = false
FEATURE [Part::Extrusion] Extrude057  label="top025"
  Base = -> Sketch064
  Dir = (0,0,1)
  DirMode = 2
  FaceMakerClass = Part::FaceMakerBullseye
  LengthFwd = 72
  LengthRev = 0
  Solid = true
  Symmetric = false
FEATURE [Sketcher::SketchObject] Sketch066
  FullyConstrained = true
  MapMode = 3
  Placement = pos=(0,0,0) rot=(1,0,0;1.5708rad)
  Support = -> [Extrude057]
  sketch-geometry (8):
    g0: Circle CenterX=80.351 CenterY=-67.6202 CenterZ=0 NormalX=0 NormalY=0 NormalZ=1 AngleXU=0 Radius=3
    g1: Circle CenterX=80.351 CenterY=-4.92017 CenterZ=0 NormalX=0 NormalY=0 NormalZ=1 AngleXU=0 Radius=3
    g2: Circle CenterX=23.851 CenterY=-4.92017 CenterZ=0 NormalX=0 NormalY=0 NormalZ=1 AngleXU=0 Radius=3
    g3: Circle CenterX=23.851 CenterY=-67.6202 CenterZ=0 NormalX=0 NormalY=0 NormalZ=1 AngleXU=0 Radius=3
    g4: Circle CenterX=23.851 CenterY=-67.6202 CenterZ=0 NormalX=0 NormalY=0 NormalZ=1 AngleXU=0 Radius=5
    g5: Circle CenterX=80.351 CenterY=-67.6202 CenterZ=0 NormalX=0 NormalY=0 NormalZ=1 AngleXU=0 Radius=5
    g6: Circle CenterX=23.851 CenterY=-4.92017 CenterZ=0 NormalX=0 NormalY=0 NormalZ=1 AngleXU=0 Radius=5
    g7: Circle CenterX=80.351 CenterY=-4.92017 CenterZ=0 NormalX=0 NormalY=0 NormalZ=1 AngleXU=0 Radius=5
  constraints (8):
    c: Block(g1)
    c: Block(g0)
    c: Block(g3)
    c: Block(g2)
    c: Block(g5)
    c: Block(g4)
    c: Block(g6)
    c: Block(g7)
FEATURE [Part::Extrusion] Extrude055
  Base = -> Sketch066
  Dir = (0,-1,2e-16)
  DirMode = 2
  FaceMakerClass = Part::FaceMakerBullseye
  LengthFwd = 2
  LengthRev = 0
  Solid = true
  Symmetric = false
FEATURE [Part::Fillet] Fillet041
  Base = -> Extrude056
  Edges = 4 edges r=1.99: [Edge6,Edge12,Edge18,Edge24]
FEATURE [Part::Cut] Cut045
  Base = -> Extrude055
  Placement = pos=(0,6,0) rot=(0,0,1;0rad)
  Tool = -> Fillet041
FEATURE [Part::MultiFuse] Fusion095  label="pcbScrewPillars"
  Placement = pos=(-3.2,-1,72.3) rot=(0,0,1;0rad)
  Shapes = -> [Cut045,Extrude054]
FEATURE [Part::Feature] Face113
  shape: bbox 3.2 x 1.5 x 2e-07 mm, 1 faces, 0 solids (baked)
FEATURE [Part::Revolution] Revolve121  label="backCaseScrewRetainer002"
  Angle = 360
  Axis = (0,1,0)
  Base = (0,0,0)
  FaceMakerClass = Part::FaceMakerBullseye
  Placement = pos=(12.5,3,62) rot=(0,0,1;0rad)
  Solid = false
  Source = -> Face113
  Symmetric = false
FEATURE [Part::Feature] Face114
  shape: bbox 3.2 x 1.5 x 2e-07 mm, 1 faces, 0 solids (baked)
FEATURE [Part::Feature] Face115
  shape: bbox 3.2 x 1.5 x 2e-07 mm, 1 faces, 0 solids (baked)
FEATURE [Part::Feature] Face116
  shape: bbox 3.2 x 1.5 x 2e-07 mm, 1 faces, 0 solids (baked)
FEATURE [Part::Revolution] Revolve122  label="frontCaseScrewRetainer004"
  Angle = 360
  Axis = (0,1,0)
  Base = (0,0,0)
  FaceMakerClass = Part::FaceMakerBullseye
  Placement = pos=(89.5,3,68.5) rot=(0,0,1;0rad)
  Solid = false
  Source = -> Face115
  Symmetric = false
FEATURE [Part::Revolution] Revolve123  label="frontCaseScrewRetainer005"
  Angle = 360
  Axis = (0,1,0)
  Base = (0,0,0)
  FaceMakerClass = Part::FaceMakerBullseye
  Placement = pos=(89.5,3,3.5) rot=(0,0,1;0rad)
  Solid = false
  Source = -> Face116
  Symmetric = false
FEATURE [Part::Revolution] Revolve124  label="backCaseScrewRetainer003"
  Angle = 360
  Axis = (0,1,0)
  Base = (0,0,0)
  FaceMakerClass = Part::FaceMakerBullseye
  Placement = pos=(12.5,3,10) rot=(0,0,1;0rad)
  Solid = false
  Source = -> Face114
  Symmetric = false
FEATURE [Part::Feature] Face117
  shape: bbox 3.6 x 3.2 x 2e-07 mm, 1 faces, 0 solids (baked)
FEATURE [Part::Revolution] Revolve125  label="moreFrontCaseScrewRetainer004"
  Angle = 360
  Axis = (0,1,0)
  Base = (0,0,0)
  FaceMakerClass = Part::FaceMakerBullseye
  Placement = pos=(109.5,4.5,68.5) rot=(0,0,1;0rad)
  Solid = false
  Source = -> Face117
  Symmetric = false
FEATURE [Part::Feature] Face118
  shape: bbox 3.6 x 3.2 x 2e-07 mm, 1 faces, 0 solids (baked)
FEATURE [Part::Revolution] Revolve126  label="moreFrontCaseScrewRetainer005"
  Angle = 360
  Axis = (0,1,0)
  Base = (0,0,0)
  FaceMakerClass = Part::FaceMakerBullseye
  Placement = pos=(109.5,4.5,3.5) rot=(0,0,1;0rad)
  Solid = false
  Source = -> Face118
  Symmetric = false
FEATURE [Part::MultiFuse] Fusion096  label="screwRetainers001"
  Shapes = -> [Revolve126,Revolve125,Revolve124,Revolve123,Revolve122,Revolve121]
FEATURE [Part::Feature] Face119
  shape: bbox 10 x 16.5 x 2e-07 mm, 1 faces, 0 solids (baked)
FEATURE [Part::Revolution] Revolve130  label="plugHousing050"
  Angle = 360
  Axis = (0,1,0)
  Base = (0,0,0)
  FaceMakerClass = Part::FaceMakerBullseye
  Placement = pos=(0,0,36.15) rot=(0,0,1;0rad)
  Solid = false
  Source = -> Face119
  Symmetric = false
FEATURE [Part::Feature] Face120
  shape: bbox 10 x 16.5 x 2e-07 mm, 1 faces, 0 solids (baked)
FEATURE [Part::Feature] Face121
  shape: bbox 10 x 16.5 x 2e-07 mm, 1 faces, 0 solids (baked)
FEATURE [Part::Revolution] Revolve127  label="plugHousing047"
  Angle = 360
  Axis = (0,1,0)
  Base = (0,0,0)
  FaceMakerClass = Part::FaceMakerBullseye
  Placement = pos=(0,0,36.15) rot=(0,0,1;0rad)
  Solid = false
  Source = -> Face121
  Symmetric = false
FEATURE [Part::Feature] Face122
  shape: bbox 10 x 16.5 x 2e-07 mm, 1 faces, 0 solids (baked)
FEATURE [Part::Feature] Face123
  shape: bbox 10 x 16.5 x 2e-07 mm, 1 faces, 0 solids (baked)
FEATURE [Part::Revolution] Revolve128  label="plugHousing048"
  Angle = 360
  Axis = (0,1,0)
  Base = (0,0,0)
  FaceMakerClass = Part::FaceMakerBullseye
  Placement = pos=(0,0,36.15) rot=(0,0,1;0rad)
  Solid = false
  Source = -> Face123
  Symmetric = false
FEATURE [Part::MultiFuse] Fusion100  label="plugHousing054"
  Placement = pos=(0,0,0) rot=(0,0,1;1.5708rad)
  Shapes = -> [Revolve130,Revolve128]
FEATURE [Part::Feature] Face124
  shape: bbox 10 x 16.5 x 2e-07 mm, 1 faces, 0 solids (baked)
FEATURE [Part::Feature] Face125
  shape: bbox 10 x 16.5 x 2e-07 mm, 1 faces, 0 solids (baked)
FEATURE [Part::Revolution] Revolve129  label="plugHousing049"
  Angle = 360
  Axis = (0,1,0)
  Base = (0,0,0)
  FaceMakerClass = Part::FaceMakerBullseye
  Placement = pos=(0,0,36.15) rot=(0,0,1;0rad)
  Solid = false
  Source = -> Face125
  Symmetric = false
FEATURE [Part::Feature] Face126
  shape: bbox 10 x 16.5 x 2e-07 mm, 1 faces, 0 solids (baked)
FEATURE [Part::Revolution] Revolve131  label="plugHousing058"
  Angle = 360
  Axis = (0,1,0)
  Base = (0,0,0)
  FaceMakerClass = Part::FaceMakerBullseye
  Placement = pos=(0,0,36.15) rot=(0,0,1;0rad)
  Solid = false
  Source = -> Face120
  Symmetric = false
FEATURE [Part::MultiFuse] Fusion099  label="plugHousing053"
  Placement = pos=(0,0,0) rot=(0,0,1;1.5708rad)
  Shapes = -> [Revolve127,Revolve131]
FEATURE [Part::MultiFuse] Fusion102  label="plugHousing056"
  Placement = pos=(0,19,0) rot=(0,0,1;3.14159rad)
  Shapes = -> [Fusion100,Fusion099]
FEATURE [Part::Revolution] Revolve132  label="plugHousing059"
  Angle = 360
  Axis = (0,1,0)
  Base = (0,0,0)
  FaceMakerClass = Part::FaceMakerBullseye
  Placement = pos=(0,0,36.15) rot=(0,0,1;0rad)
  Solid = false
  Source = -> Face126
  Symmetric = false
FEATURE [Part::Revolution] Revolve133  label="plugHousing060"
  Angle = 360
  Axis = (0,1,0)
  Base = (0,0,0)
  FaceMakerClass = Part::FaceMakerBullseye
  Placement = pos=(0,0,36.15) rot=(0,0,1;0rad)
  Solid = false
  Source = -> Face122
  Symmetric = false
FEATURE [Part::MultiFuse] Fusion097  label="plugHousing051"
  Placement = pos=(0,0,0) rot=(0,0,1;1.5708rad)
  Shapes = -> [Revolve133,Revolve132]
FEATURE [Part::Revolution] Revolve134  label="plugHousing061"
  Angle = 360
  Axis = (0,1,0)
  Base = (0,0,0)
  FaceMakerClass = Part::FaceMakerBullseye
  Placement = pos=(0,0,36.15) rot=(0,0,1;0rad)
  Solid = false
  Source = -> Face124
  Symmetric = false
FEATURE [Part::MultiFuse] Fusion101  label="plugHousing055"
  Placement = pos=(0,0,0) rot=(0,0,1;1.5708rad)
  Shapes = -> [Revolve129,Revolve134]
FEATURE [Part::MultiFuse] Fusion098  label="plugHousing052"
  Placement = pos=(0,19,0) rot=(0,0,1;3.14159rad)
  Shapes = -> [Fusion097,Fusion101]
FEATURE [Part::MultiFuse] Fusion103  label="plugHousing057"
  Placement = pos=(122.621,0,-0.15) rot=(0,0,1;0rad)
  Shapes = -> [Fusion102,Fusion098]
FEATURE [Part::Box] Box028  label="Cube015"
  AttacherType = Attacher::AttachEngine3D
  Height = 28
  Length = 3
  Placement = pos=(110.7,19,22) rot=(0,0,1;0rad)
  Width = 15.7
FEATURE [Part::Cylinder] Cylinder044
  Angle = 360
  AttacherType = Attacher::AttachEngine3D
  Height = 20
  Placement = pos=(0,0,36.15) rot=(0,0,1;0rad)
  Radius = 10.3
FEATURE [Part::Cylinder] Cylinder045
  Angle = 360
  AttacherType = Attacher::AttachEngine3D
  Height = 10
  Placement = pos=(0,0,36.15) rot=(0,0,1;0rad)
  Radius = 4
FEATURE [Part::MultiFuse] Fusion104  label="removeToCreteHoleForPlugHousing040"
  Placement = pos=(70,19,36) rot=(0,1,0;1.5708rad)
  Shapes = -> [Cylinder044,Cylinder045]
FEATURE [Part::Cut] Cut046  label="plugHousingTab003"
  Base = -> Box028
  Tool = -> Fusion104
FEATURE [Part::MultiFuse] Fusion105  label="plugHousing062"
  Shapes = -> [Fusion103,Cut046]
FEATURE [Part::Fillet] Fillet042
  Base = -> Fusion105
  Edges = 1 edges r=2: [Edge25]
FEATURE [Part::Fillet] Fillet043  label="plugHousing063"
  Base = -> Fillet042
  Edges = 1 edges r=2: [Edge8]
  Placement = pos=(7,0,0) rot=(0,0,1;0rad)
FEATURE [Part::Feature] Face127
  shape: bbox 10 x 16.5 x 2e-07 mm, 1 faces, 0 solids (baked)
FEATURE [Part::Feature] Face128
  shape: bbox 10 x 16.5 x 2e-07 mm, 1 faces, 0 solids (baked)
FEATURE [Part::Revolution] Revolve137  label="plugHousing070"
  Angle = 360
  Axis = (0,1,0)
  Base = (0,0,0)
  FaceMakerClass = Part::FaceMakerBullseye
  Placement = pos=(0,0,36.15) rot=(0,0,1;0rad)
  Solid = false
  Source = -> Face127
  Symmetric = false
FEATURE [Part::Revolution] Revolve140  label="plugHousing073"
  Angle = 360
  Axis = (0,1,0)
  Base = (0,0,0)
  FaceMakerClass = Part::FaceMakerBullseye
  Placement = pos=(0,0,36.15) rot=(0,0,1;0rad)
  Solid = false
  Source = -> Face128
  Symmetric = false
FEATURE [Part::Feature] Face129
  shape: bbox 10 x 16.5 x 2e-07 mm, 1 faces, 0 solids (baked)
FEATURE [Part::Revolution] Revolve138  label="plugHousing071"
  Angle = 360
  Axis = (0,1,0)
  Base = (0,0,0)
  FaceMakerClass = Part::FaceMakerBullseye
  Placement = pos=(0,0,36.15) rot=(0,0,1;0rad)
  Solid = false
  Source = -> Face129
  Symmetric = false
FEATURE [Part::Feature] Face130
  shape: bbox 10 x 16.5 x 2e-07 mm, 1 faces, 0 solids (baked)
FEATURE [Part::Revolution] Revolve139  label="plugHousing072"
  Angle = 360
  Axis = (0,1,0)
  Base = (0,0,0)
  FaceMakerClass = Part::FaceMakerBullseye
  Placement = pos=(0,0,36.15) rot=(0,0,1;0rad)
  Solid = false
  Source = -> Face130
  Symmetric = false
FEATURE [Part::Feature] Face131
  shape: bbox 10 x 16.5 x 2e-07 mm, 1 faces, 0 solids (baked)
FEATURE [Part::Revolution] Revolve135  label="plugHousing068"
  Angle = 360
  Axis = (0,1,0)
  Base = (0,0,0)
  FaceMakerClass = Part::FaceMakerBullseye
  Placement = pos=(0,0,36.15) rot=(0,0,1;0rad)
  Solid = false
  Source = -> Face131
  Symmetric = false
FEATURE [Part::MultiFuse] Fusion112  label="plugHousing078"
  Placement = pos=(0,0,0) rot=(0,0,1;1.5708rad)
  Shapes = -> [Revolve135,Revolve139]
FEATURE [Part::Feature] Face132
  shape: bbox 10 x 16.5 x 2e-07 mm, 1 faces, 0 solids (baked)
FEATURE [Part::Revolution] Revolve141  label="plugHousing074"
  Angle = 360
  Axis = (0,1,0)
  Base = (0,0,0)
  FaceMakerClass = Part::FaceMakerBullseye
  Placement = pos=(0,0,36.15) rot=(0,0,1;0rad)
  Solid = false
  Source = -> Face132
  Symmetric = false
FEATURE [Part::MultiFuse] Fusion110  label="plugHousing076"
  Placement = pos=(0,0,0) rot=(0,0,1;1.5708rad)
  Shapes = -> [Revolve141,Revolve140]
FEATURE [Part::Feature] Face133
  shape: bbox 10 x 16.5 x 2e-07 mm, 1 faces, 0 solids (baked)
FEATURE [Part::Revolution] Revolve136  label="plugHousing069"
  Angle = 360
  Axis = (0,1,0)
  Base = (0,0,0)
  FaceMakerClass = Part::FaceMakerBullseye
  Placement = pos=(0,0,36.15) rot=(0,0,1;0rad)
  Solid = false
  Source = -> Face133
  Symmetric = false
FEATURE [Part::MultiFuse] Fusion106  label="plugHousing064"
  Placement = pos=(0,0,0) rot=(0,0,1;1.5708rad)
  Shapes = -> [Revolve138,Revolve136]
FEATURE [Part::MultiFuse] Fusion108  label="plugHousing066"
  Placement = pos=(0,19,0) rot=(0,0,1;3.14159rad)
  Shapes = -> [Fusion106,Fusion112]
FEATURE [Part::Feature] Face134
  shape: bbox 10 x 16.5 x 2e-07 mm, 1 faces, 0 solids (baked)
FEATURE [Part::Revolution] Revolve142  label="plugHousing075"
  Angle = 360
  Axis = (0,1,0)
  Base = (0,0,0)
  FaceMakerClass = Part::FaceMakerBullseye
  Placement = pos=(0,0,36.15) rot=(0,0,1;0rad)
  Solid = false
  Source = -> Face134
  Symmetric = false
FEATURE [Part::MultiFuse] Fusion107  label="plugHousing065"
  Placement = pos=(0,0,0) rot=(0,0,1;1.5708rad)
  Shapes = -> [Revolve137,Revolve142]
FEATURE [Part::MultiFuse] Fusion111  label="plugHousing077"
  Placement = pos=(0,19,0) rot=(0,0,1;3.14159rad)
  Shapes = -> [Fusion110,Fusion107]
FEATURE [Part::MultiFuse] Fusion109  label="plugHousing067"
  Placement = pos=(131.236,0,-0.15) rot=(0,0,1;0rad)
  Shapes = -> [Fusion108,Fusion111]
FEATURE [Part::MultiFuse] Fusion113  label="plugHousing079"
  Shapes = -> [Fillet043,Fusion109]
FEATURE [Part::Feature] Face135
  shape: bbox 3.5 x 17.8 x 2e-07 mm, 1 faces, 0 solids (baked)
FEATURE [Part::Revolution] Revolve143  label="removeToCreateScrewAndThreadedInsertHole049"
  Angle = 360
  Axis = (0,1,0)
  Base = (0,0,0)
  FaceMakerClass = Part::FaceMakerBullseye
  Placement = pos=(12.5,0,10) rot=(0,0,1;0rad)
  Solid = false
  Source = -> Face135
  Symmetric = false
FEATURE [Part::Feature] Face136
  shape: bbox 3.5 x 17.8 x 2e-07 mm, 1 faces, 0 solids (baked)
FEATURE [Part::Revolution] Revolve144  label="removeToCreateScrewAndThreadedInsertHole050"
  Angle = 360
  Axis = (0,1,0)
  Base = (0,0,0)
  FaceMakerClass = Part::FaceMakerBullseye
  Placement = pos=(12.5,0,62) rot=(0,0,1;0rad)
  Solid = false
  Source = -> Face136
  Symmetric = false
FEATURE [Part::Feature] Face137
  shape: bbox 3.5 x 17.8 x 2e-07 mm, 1 faces, 0 solids (baked)
FEATURE [Part::Revolution] Revolve145  label="removeToCreateScrewAndThreadedInsertHole051"
  Angle = 360
  Axis = (0,1,0)
  Base = (0,0,0)
  FaceMakerClass = Part::FaceMakerBullseye
  Placement = pos=(89.5,0,68.5) rot=(0,0,1;0rad)
  Solid = false
  Source = -> Face137
  Symmetric = false
FEATURE [Part::Feature] Face138
  shape: bbox 3.5 x 17.8 x 2e-07 mm, 1 faces, 0 solids (baked)
FEATURE [Part::Revolution] Revolve146  label="removeToCreateScrewAndThreadedInsertHole052"
  Angle = 360
  Axis = (0,1,0)
  Base = (0,0,0)
  FaceMakerClass = Part::FaceMakerBullseye
  Placement = pos=(89.5,0,3.5) rot=(0,0,1;0rad)
  Solid = false
  Source = -> Face138
  Symmetric = false
FEATURE [Part::Feature] Face139
  shape: bbox 3.5 x 17.8 x 2e-07 mm, 1 faces, 0 solids (baked)
FEATURE [Part::Revolution] Revolve147  label="removeToCreateScrewAndThreadedInsertHole053"
  Angle = 360
  Axis = (0,1,0)
  Base = (0,0,0)
  FaceMakerClass = Part::FaceMakerBullseye
  Placement = pos=(109.5,4.7,3.5) rot=(0,0,1;0rad)
  Solid = false
  Source = -> Face139
  Symmetric = false
FEATURE [Part::Feature] Face140
  shape: bbox 3.5 x 17.8 x 2e-07 mm, 1 faces, 0 solids (baked)
FEATURE [Part::Revolution] Revolve148  label="removeToCreateScrewAndThreadedInsertHole054"
  Angle = 360
  Axis = (0,1,0)
  Base = (0,0,0)
  FaceMakerClass = Part::FaceMakerBullseye
  Placement = pos=(109.5,4.7,68.5) rot=(0,0,1;0rad)
  Solid = false
  Source = -> Face140
  Symmetric = false
FEATURE [Part::MultiFuse] Fusion114  label="removeToCreateScrewAndThreadedInsertHole055"
  Shapes = -> [Revolve148,Revolve147,Revolve146,Revolve145,Revolve144,Revolve143]
FEATURE [Part::Cut] Cut047  label="casePillars004"
  Base = -> Cut037
  Tool = -> Fusion114
FEATURE [Part::Feature] Face141
  shape: bbox 3.5 x 17.8 x 2e-07 mm, 1 faces, 0 solids (baked)
FEATURE [Part::Feature] Face142
  shape: bbox 3.5 x 17.8 x 2e-07 mm, 1 faces, 0 solids (baked)
FEATURE [Part::Feature] Face143
  shape: bbox 3.5 x 17.8 x 2e-07 mm, 1 faces, 0 solids (baked)
FEATURE [Part::Revolution] Revolve149  label="removeToCreateScrewAndThreadedInsertHole057"
  Angle = 360
  Axis = (0,1,0)
  Base = (0,0,0)
  FaceMakerClass = Part::FaceMakerBullseye
  Placement = pos=(12.5,0,10) rot=(0,0,1;0rad)
  Solid = false
  Source = -> Face141
  Symmetric = false
FEATURE [Part::Feature] Face144
  shape: bbox 3.5 x 17.8 x 2e-07 mm, 1 faces, 0 solids (baked)
FEATURE [Part::Feature] Face145
  shape: bbox 3.5 x 17.8 x 2e-07 mm, 1 faces, 0 solids (baked)
FEATURE [Part::Feature] Face146
  shape: bbox 3.5 x 17.8 x 2e-07 mm, 1 faces, 0 solids (baked)
FEATURE [Part::Revolution] Revolve150  label="removeToCreateScrewAndThreadedInsertHole058"
  Angle = 360
  Axis = (0,1,0)
  Base = (0,0,0)
  FaceMakerClass = Part::FaceMakerBullseye
  Placement = pos=(12.5,0,62) rot=(0,0,1;0rad)
  Solid = false
  Source = -> Face146
  Symmetric = false
FEATURE [Part::Revolution] Revolve151  label="removeToCreateScrewAndThreadedInsertHole059"
  Angle = 360
  Axis = (0,1,0)
  Base = (0,0,0)
  FaceMakerClass = Part::FaceMakerBullseye
  Placement = pos=(89.5,0,68.5) rot=(0,0,1;0rad)
  Solid = false
  Source = -> Face143
  Symmetric = false
FEATURE [Part::Revolution] Revolve152  label="removeToCreateScrewAndThreadedInsertHole060"
  Angle = 360
  Axis = (0,1,0)
  Base = (0,0,0)
  FaceMakerClass = Part::FaceMakerBullseye
  Placement = pos=(89.5,0,3.5) rot=(0,0,1;0rad)
  Solid = false
  Source = -> Face142
  Symmetric = false
FEATURE [Part::Revolution] Revolve153  label="removeToCreateScrewAndThreadedInsertHole061"
  Angle = 360
  Axis = (0,1,0)
  Base = (0,0,0)
  FaceMakerClass = Part::FaceMakerBullseye
  Placement = pos=(109.5,4.7,3.5) rot=(0,0,1;0rad)
  Solid = false
  Source = -> Face145
  Symmetric = false
FEATURE [Part::Revolution] Revolve154  label="removeToCreateScrewAndThreadedInsertHole062"
  Angle = 360
  Axis = (0,1,0)
  Base = (0,0,0)
  FaceMakerClass = Part::FaceMakerBullseye
  Placement = pos=(109.5,4.7,68.5) rot=(0,0,1;0rad)
  Solid = false
  Source = -> Face144
  Symmetric = false
FEATURE [Part::MultiFuse] Fusion115  label="removeToCreateScrewAndThreadedInsertHole056"
  Shapes = -> [Revolve154,Revolve153,Revolve152,Revolve151,Revolve150,Revolve149]
FEATURE [Part::Feature] Face147
  shape: bbox 9.8 x 26.5 x 2e-07 mm, 1 faces, 0 solids (baked)
FEATURE [Part::Revolution] Revolve155
  Angle = 360
  Axis = (0,1,0)
  Base = (0,0,0)
  FaceMakerClass = Part::FaceMakerBullseye
  Placement = pos=(0,0,0) rot=(0,0,1;1.5708rad)
  Solid = false
  Source = -> Face147
  Symmetric = false
FEATURE [Part::Feature] Face148
  shape: bbox 9.8 x 26.5 x 2e-07 mm, 1 faces, 0 solids (baked)
FEATURE [Part::Revolution] Revolve156
  Angle = 360
  Axis = (0,1,0)
  Base = (0,0,0)
  FaceMakerClass = Part::FaceMakerBullseye
  Placement = pos=(0,0,0) rot=(0,0,1;1.5708rad)
  Solid = false
  Source = -> Face148
  Symmetric = false
FEATURE [Part::MultiFuse] Fusion116
  Placement = pos=(-18,19,36) rot=(0,0,1;0rad)
  Shapes = -> [Revolve156,Revolve155]
FEATURE [Part::Box] Box029  label="Cube016"
  AttacherType = Attacher::AttachEngine3D
  Height = 28
  Length = 3
  Placement = pos=(110.7,19,22) rot=(0,0,1;0rad)
  Width = 15.7
FEATURE [Part::Cylinder] Cylinder046
  Angle = 360
  AttacherType = Attacher::AttachEngine3D
  Height = 10
  Placement = pos=(0,0,36.15) rot=(0,0,1;0rad)
  Radius = 4
FEATURE [Part::Cylinder] Cylinder047
  Angle = 360
  AttacherType = Attacher::AttachEngine3D
  Height = 20
  Placement = pos=(0,0,36.15) rot=(0,0,1;0rad)
  Radius = 10.3
FEATURE [Part::MultiFuse] Fusion117  label="removeToCreteHoleForPlugHousing041"
  Placement = pos=(70,19,36) rot=(0,1,0;1.5708rad)
  Shapes = -> [Cylinder047,Cylinder046]
FEATURE [Part::Cut] Cut049  label="plugHousingTab004"
  Base = -> Box029
  Placement = pos=(-107.4,-14,0) rot=(0,0,1;0rad)
  Tool = -> Fusion117
FEATURE [Part::Box] Box030  label="Cube017"
  AttacherType = Attacher::AttachEngine3D
  Height = 28
  Length = 3
  Placement = pos=(110.7,19,22) rot=(0,0,1;0rad)
  Width = 15.7
FEATURE [Part::Cylinder] Cylinder048
  Angle = 360
  AttacherType = Attacher::AttachEngine3D
  Height = 10
  Placement = pos=(0,0,36.15) rot=(0,0,1;0rad)
  Radius = 4
FEATURE [Part::Cylinder] Cylinder049
  Angle = 360
  AttacherType = Attacher::AttachEngine3D
  Height = 20
  Placement = pos=(0,0,36.15) rot=(0,0,1;0rad)
  Radius = 10.3
FEATURE [Part::MultiFuse] Fusion118  label="removeToCreteHoleForPlugHousing042"
  Placement = pos=(70,19,36) rot=(0,1,0;1.5708rad)
  Shapes = -> [Cylinder049,Cylinder048]
FEATURE [Part::Cut] Cut050  label="plugHousingTab005"
  Base = -> Box030
  Placement = pos=(-107.4,-14,0) rot=(0,0,1;0rad)
  Tool = -> Fusion118
FEATURE [Part::MultiFuse] Fusion119
  Placement = pos=(9.6,23,0) rot=(0,0,1;3.14159rad)
  Shapes = -> [Cut049,Cut050]
FEATURE [Part::Box] Box031  label="Cube018"
  AttacherType = Attacher::AttachEngine3D
  Height = 10
  Length = 3
  Placement = pos=(3.3,4,12) rot=(0,0,1;0rad)
  Width = 10
FEATURE [Part::Fillet] Fillet044
  Base = -> Box031
  Edges = 1 edges r=2: [Edge11]
FEATURE [Part::Box] Box032  label="Cube019"
  AttacherType = Attacher::AttachEngine3D
  Height = 10
  Length = 3
  Placement = pos=(3.3,4,50) rot=(0,0,1;0rad)
  Width = 10
FEATURE [Part::Fillet] Fillet045
  Base = -> Box032
  Edges = 1 edges r=2: [Edge12]
FEATURE [Part::Box] Box033  label="Cube020"
  AttacherType = Attacher::AttachEngine3D
  Height = 28
  Length = 4
  Placement = pos=(5,0,22) rot=(0,0,1;0rad)
  Width = 10
FEATURE [Part::Fillet] Fillet046
  Base = -> Box033
  Edges = 1 edges r=1: [Edge7]
FEATURE [Part::Fillet] Fillet047
  Base = -> Fillet046
  Edges = 1 edges r=2: [Edge5]
FEATURE [Part::Fillet] Fillet048
  Base = -> Fillet047
  Edges = 1 edges r=2: [Edge2]
FEATURE [Part::Cylinder] Cylinder050
  Angle = 360
  AttacherType = Attacher::AttachEngine3D
  Height = 20
  Placement = pos=(0,0,36.15) rot=(0,0,1;0rad)
  Radius = 8.2
FEATURE [Part::Cylinder] Cylinder051
  Angle = 360
  AttacherType = Attacher::AttachEngine3D
  Height = 10
  Placement = pos=(0,0,36.15) rot=(0,0,1;0rad)
  Radius = 4
FEATURE [Part::MultiFuse] Fusion120  label="removeToCreteHoleForPlugHousing043"
  Placement = pos=(-42,19,36) rot=(0,1,0;1.5708rad)
  Shapes = -> [Cylinder050,Cylinder051]
FEATURE [Sketcher::SketchObject] Sketch067  label="topSketch018"
  FullyConstrained = true
  sketch-geometry (4):
    g0: LineSegment StartX=16.8446 StartY=31.512 StartZ=0 EndX=16.3251 EndY=34.4666 EndZ=0
    g1: ArcOfCircle CenterX=19 CenterY=19.2524 CenterZ=0 NormalX=0 NormalY=0 NormalZ=1 AngleXU=0 Radius=15.4476 StartAngle=1.74483 EndAngle=2.72717
    g2: ArcOfCircle CenterX=19 CenterY=19.2524 CenterZ=0 NormalX=0 NormalY=0 NormalZ=1 AngleXU=0 Radius=12.4476 StartAngle=1.74483 EndAngle=2.73189
    g3: LineSegment StartX=4.86004 StartY=25.4725 StartZ=0 EndX=7.58253 EndY=24.2107 EndZ=0
  constraints (7):
    c: Block(g0)
    c: Coincident(g1,g0)
    c: Coincident(g2,g0)
    c: Coincident(g3,g1)
    c: Coincident(g3,g2)
    c: Block(g1)
    c: Block(g2)
FEATURE [Part::Extrusion] Extrude058
  Base = -> Sketch067
  Dir = (0,0,1)
  DirMode = 2
  FaceMakerClass = Part::FaceMakerBullseye
  LengthFwd = 10
  LengthRev = 0
  Placement = pos=(0,0,31) rot=(0,0,1;0rad)
  Solid = true
  Symmetric = false
FEATURE [Part::Cut] Cut051
  Base = -> Extrude058
  Tool = -> Fusion120
FEATURE [Part::Fillet] Fillet049
  Base = -> Cut051
  Edges = 1 edges r=2: [Edge1]
FEATURE [Part::Fillet] Fillet050
  Base = -> Fillet049
  Edges = 1 edges r=2.5: [Edge1]
FEATURE [Part::Fillet] Fillet051
  Base = -> Fillet050
  Edges = 1 edges r=2.5: [Edge2]
FEATURE [Part::MultiFuse] Fusion121  label="wireHolder003"
  Shapes = -> [Fusion116,Fillet051]
FEATURE [Part::MultiFuse] Fusion122
  Shapes = -> [Fillet045,Fusion121]
FEATURE [Part::MultiFuse] Fusion123  label="wireHolder004"
  Shapes = -> [Fusion122,Fillet048]
FEATURE [Part::MultiFuse] Fusion124  label="wireHolder005"
  Shapes = -> [Fillet044,Fusion119,Fusion123]
FEATURE [Sketcher::SketchObject] Sketch068  label="topSketch019"
  FullyConstrained = true
  sketch-geometry (6):
    g0: LineSegment StartX=19 StartY=38 StartZ=0 EndX=117 EndY=38 EndZ=0
    g1: ArcOfCircle CenterX=19 CenterY=19 CenterZ=0 NormalX=0 NormalY=0 NormalZ=1 AngleXU=0 Radius=19 StartAngle=1.5708 EndAngle=3.14159
    g2: LineSegment StartX=117 StartY=38 StartZ=0 EndX=117 EndY=19 EndZ=0
    g3: LineSegment StartX=98 StartY=1.0161e-12 StartZ=0 EndX=5.22862e-06 EndY=1.0161e-12 EndZ=0
    g4: LineSegment StartX=5.22862e-06 StartY=19 StartZ=0 EndX=5.22862e-06 EndY=1.0161e-12 EndZ=0
    g5: ArcOfCircle CenterX=98 CenterY=19 CenterZ=0 NormalX=0 NormalY=0 NormalZ=1 AngleXU=0 Radius=19 StartAngle=4.71239 EndAngle=6.28319
  constraints (16):
    c: Horizontal(g0)
    c: Distance(g0) = 98
    c: Coincident(g1,g0)
    c: Block(g1)
    c: Coincident(g2,g0)
    c: Vertical(g2)
    c: Distance(g2) = 19
    c: Horizontal(g3)
    c: Coincident(g4,g1)
    c: Vertical(g4)
    c: Coincident(g3,g4)
    c: Block(g3)
    c: Coincident(g5,g2)
    c: Coincident(g5,g3)
    c: Block(g0)
    c: Block(g5)
FEATURE [Part::Extrusion] Extrude059  label="sideA002"
  Base = -> Sketch068
  Dir = (0,0,1)
  DirMode = 2
  FaceMakerClass = Part::FaceMakerBullseye
  LengthFwd = 3
  LengthRev = 0
  Placement = pos=(0,0,-2.7) rot=(0,0,1;0rad)
  Solid = true
  Symmetric = false
FEATURE [Sketcher::SketchObject] Sketch069  label="topSketch020"
  FullyConstrained = true
  sketch-geometry (6):
    g0: LineSegment StartX=19 StartY=38 StartZ=0 EndX=117 EndY=38 EndZ=0
    g1: ArcOfCircle CenterX=19 CenterY=19 CenterZ=0 NormalX=0 NormalY=0 NormalZ=1 AngleXU=0 Radius=19 StartAngle=1.5708 EndAngle=3.14159
    g2: LineSegment StartX=117 StartY=38 StartZ=0 EndX=117 EndY=19 EndZ=0
    g3: LineSegment StartX=98 StartY=1.0161e-12 StartZ=0 EndX=5.22862e-06 EndY=1.0161e-12 EndZ=0
    g4: LineSegment StartX=5.22862e-06 StartY=19 StartZ=0 EndX=5.22862e-06 EndY=1.0161e-12 EndZ=0
    g5: ArcOfCircle CenterX=98 CenterY=19 CenterZ=0 NormalX=0 NormalY=0 NormalZ=1 AngleXU=0 Radius=19 StartAngle=4.71239 EndAngle=6.28319
  constraints (16):
    c: Horizontal(g0)
    c: Distance(g0) = 98
    c: Coincident(g1,g0)
    c: Block(g1)
    c: Coincident(g2,g0)
    c: Vertical(g2)
    c: Distance(g2) = 19
    c: Horizontal(g3)
    c: Coincident(g4,g1)
    c: Vertical(g4)
    c: Coincident(g3,g4)
    c: Block(g3)
    c: Coincident(g5,g2)
    c: Coincident(g5,g3)
    c: Block(g0)
    c: Block(g5)
FEATURE [Part::Extrusion] Extrude060  label="sideB002"
  Base = -> Sketch069
  Dir = (0,0,1)
  DirMode = 2
  FaceMakerClass = Part::FaceMakerBullseye
  LengthFwd = 3
  LengthRev = 0
  Placement = pos=(0,0,71.7) rot=(0,0,1;0rad)
  Solid = true
  Symmetric = false
FEATURE [Part::MultiFuse] Fusion127  label="removeFromBottom001"
  Placement = pos=(2,0,0) rot=(0,0,1;0rad)
  Shapes = -> [Extrude059,Extrude060]
FEATURE [Part::Cylinder] Cylinder052
  Angle = 360
  AttacherType = Attacher::AttachEngine3D
  Height = 20
  Placement = pos=(0,0,36.15) rot=(0,0,1;0rad)
  Radius = 14
FEATURE [Part::Cylinder] Cylinder053
  Angle = 360
  AttacherType = Attacher::AttachEngine3D
  Height = 10
  Placement = pos=(0,0,36.15) rot=(0,0,1;0rad)
  Radius = 4
FEATURE [Part::MultiFuse] Fusion128  label="removeToCreteHoleForPlugHousing044"
  Placement = pos=(70,19,36) rot=(0,1,0;1.5708rad)
  Shapes = -> [Cylinder052,Cylinder053]
FEATURE [Part::Cut] Cut052  label="bottom011"
  Base = -> Extrude043
  Tool = -> Fusion128
FEATURE [Part::Cut] Cut054  label="bottom012"
  Base = -> Cut052
  Tool = -> Fusion115
FEATURE [Sketcher::SketchObject] Sketch070
  FullyConstrained = true
  Placement = pos=(117,19,0) rot=(0.57735,0.57735,0.57735;2.0944rad)
  sketch-geometry (48):
    g0: LineSegment StartX=-49.19 StartY=69.25 StartZ=0 EndX=-49.19 EndY=66.25 EndZ=0
    g1: LineSegment StartX=-49.19 StartY=63.5 StartZ=0 EndX=-49.19 EndY=60.5 EndZ=0
    g2: LineSegment StartX=-49.19 StartY=57.75 StartZ=0 EndX=-49.19 EndY=54.75 EndZ=0
    g3: LineSegment StartX=-49.19 StartY=52 StartZ=0 EndX=-49.19 EndY=49 EndZ=0
    g4: LineSegment StartX=-49.19 StartY=46.25 StartZ=0 EndX=-49.19 EndY=43.25 EndZ=0
    g5: LineSegment StartX=-49.19 StartY=40.5 StartZ=0 EndX=-49.19 EndY=37.5 EndZ=0
    g6: LineSegment StartX=-49.19 StartY=34.5 StartZ=0 EndX=-49.19 EndY=31.5 EndZ=0
    g7: LineSegment StartX=-49.19 StartY=28.75 StartZ=0 EndX=-49.19 EndY=25.75 EndZ=0
    g8: LineSegment StartX=-49.19 StartY=23 StartZ=0 EndX=-49.19 EndY=20 EndZ=0
    g9: LineSegment StartX=-49.19 StartY=17.25 StartZ=0 EndX=-49.19 EndY=14.25 EndZ=0
    g10: LineSegment StartX=-49.19 StartY=11.5 StartZ=0 EndX=-49.19 EndY=8.5 EndZ=0
    g11: LineSegment StartX=-49.19 StartY=5.75 StartZ=0 EndX=-49.19 EndY=2.75 EndZ=0
    g12: ArcOfCircle CenterX=-1.5 CenterY=67.75 CenterZ=0 NormalX=0 NormalY=0 NormalZ=1 AngleXU=0 Radius=1.5 StartAngle=4.71239 EndAngle=7.85398
    g13: ArcOfCircle CenterX=-1.5 CenterY=62 CenterZ=0 NormalX=0 NormalY=0 NormalZ=1 AngleXU=0 Radius=1.5 StartAngle=4.71239 EndAngle=7.85398
    g14: ArcOfCircle CenterX=-1.5 CenterY=56.25 CenterZ=0 NormalX=0 NormalY=0 NormalZ=1 AngleXU=0 Radius=1.5 StartAngle=4.71239 EndAngle=7.85398
    g15: ArcOfCircle CenterX=-11.49 CenterY=50.5 CenterZ=0 NormalX=0 NormalY=0 NormalZ=1 AngleXU=0 Radius=1.5 StartAngle=4.71239 EndAngle=7.85398
    g16: ArcOfCircle CenterX=-16.28 CenterY=44.75 CenterZ=0 NormalX=0 NormalY=0 NormalZ=1 AngleXU=0 Radius=1.5 StartAngle=4.71239 EndAngle=7.85398
    g17: ArcOfCircle CenterX=-18.2337 CenterY=39 CenterZ=0 NormalX=0 NormalY=0 NormalZ=1 AngleXU=0 Radius=1.5 StartAngle=4.71485 EndAngle=7.85398
    g18: ArcOfCircle CenterX=-16.2837 CenterY=27.25 CenterZ=0 NormalX=0 NormalY=0 NormalZ=1 AngleXU=0 Radius=1.5 StartAngle=4.71485 EndAngle=7.85398
    g19: ArcOfCircle CenterX=-18.2337 CenterY=33 CenterZ=0 NormalX=0 NormalY=0 NormalZ=1 AngleXU=0 Radius=1.5 StartAngle=4.71485 EndAngle=7.85398
    g20: ArcOfCircle CenterX=-11.49 CenterY=21.5 CenterZ=0 NormalX=0 NormalY=0 NormalZ=1 AngleXU=0 Radius=1.5 StartAngle=4.71239 EndAngle=7.85398
    g21: ArcOfCircle CenterX=-1.5 CenterY=4.25 CenterZ=0 NormalX=0 NormalY=0 NormalZ=1 AngleXU=0 Radius=1.5 StartAngle=4.71239 EndAngle=7.85398
    g22: ArcOfCircle CenterX=-1.5 CenterY=10 CenterZ=0 NormalX=0 NormalY=0 NormalZ=1 AngleXU=0 Radius=1.5 StartAngle=4.71239 EndAngle=7.85398
    g23: ArcOfCircle CenterX=-1.5 CenterY=15.75 CenterZ=0 NormalX=0 NormalY=0 NormalZ=1 AngleXU=0 Radius=1.5 StartAngle=4.71239 EndAngle=7.85398
    g24: LineSegment StartX=-49.19 StartY=69.25 StartZ=0 EndX=-1.5 EndY=69.25 EndZ=0
    g25: LineSegment StartX=-49.19 StartY=66.25 StartZ=0 EndX=-1.5 EndY=66.25 EndZ=0
    g26: LineSegment StartX=-49.19 StartY=63.5 StartZ=0 EndX=-1.5 EndY=63.5 EndZ=0
    g27: LineSegment StartX=-49.19 StartY=60.5 StartZ=0 EndX=-1.5 EndY=60.5 EndZ=0
    g28: LineSegment StartX=-49.19 StartY=57.75 StartZ=0 EndX=-1.5 EndY=57.75 EndZ=0
    g29: LineSegment StartX=-49.19 StartY=54.75 StartZ=0 EndX=-1.5 EndY=54.75 EndZ=0
    g30: LineSegment StartX=-49.19 StartY=52 StartZ=0 EndX=-11.49 EndY=52 EndZ=0
    g31: LineSegment StartX=-49.19 StartY=49 StartZ=0 EndX=-11.49 EndY=49 EndZ=0
    g32: LineSegment StartX=-49.19 StartY=46.25 StartZ=0 EndX=-16.28 EndY=46.25 EndZ=0
    g33: LineSegment StartX=-49.19 StartY=43.25 StartZ=0 EndX=-16.28 EndY=43.25 EndZ=0
    g34: LineSegment StartX=-49.19 StartY=40.5 StartZ=0 EndX=-18.2337 EndY=40.5 EndZ=0
    g35: LineSegment StartX=-49.19 StartY=37.5 StartZ=0 EndX=-18.23 EndY=37.5 EndZ=0
    g36: LineSegment StartX=-49.19 StartY=34.5 StartZ=0 EndX=-18.2337 EndY=34.5 EndZ=0
    g37: LineSegment StartX=-49.19 StartY=31.5 StartZ=0 EndX=-18.23 EndY=31.5 EndZ=0
    g38: LineSegment StartX=-49.19 StartY=28.75 StartZ=0 EndX=-16.2837 EndY=28.75 EndZ=0
    g39: LineSegment StartX=-49.19 StartY=25.75 StartZ=0 EndX=-16.28 EndY=25.75 EndZ=0
    g40: LineSegment StartX=-49.19 StartY=23 StartZ=0 EndX=-11.49 EndY=23 EndZ=0
    g41: LineSegment StartX=-49.19 StartY=20 StartZ=0 EndX=-11.49 EndY=20 EndZ=0
    g42: LineSegment StartX=-49.19 StartY=17.25 StartZ=0 EndX=-1.5 EndY=17.25 EndZ=0
    g43: LineSegment StartX=-49.19 StartY=14.25 StartZ=0 EndX=-1.5 EndY=14.25 EndZ=0
    g44: LineSegment StartX=-49.19 StartY=11.5 StartZ=0 EndX=-1.5 EndY=11.5 EndZ=0
    g45: LineSegment StartX=-49.19 StartY=8.5 StartZ=0 EndX=-1.5 EndY=8.5 EndZ=0
    g46: LineSegment StartX=-49.19 StartY=5.75 StartZ=0 EndX=-1.5 EndY=5.75 EndZ=0
    g47: LineSegment StartX=-49.19 StartY=2.75 StartZ=0 EndX=-1.5 EndY=2.75 EndZ=0
  constraints (120):
    c: Vertical(g0)
    c: Distance(g0) = 3
    c: Block(g0)
    c: Vertical(g1)
    c: Distance(g1) = 3
    c: Vertical(g2)
    c: Equal(g0,g2) = 3
    c: Block(g2)
    c: Vertical(g3)
    c: Equal(g1,g3) = 3
    c: Vertical(g4)
    c: Equal(g0,g4) = 3
    c: Block(g4)
    c: Vertical(g5)
    c: Equal(g1,g5) = 3
    c: Vertical(g6)
    c: Equal(g0,g6) = 3
    c: Block(g6)
    c: Vertical(g7)
    c: Equal(g1,g7) = 3
    c: Vertical(g8)
    c: Equal(g0,g8) = 3
    c: Block(g8)
    c: Vertical(g9)
    c: Equal(g1,g9) = 3
    c: Vertical(g10)
    c: Equal(g0,g10) = 3
    c: Block(g10)
    c: Vertical(g11)
    c: Equal(g1,g11) = 3
    c: Block(g12)
    c: Block(g13)
    c: Block(g14)
    c: Block(g15)
    c: Block(g16)
    c: Block(g17)
    c: Block(g18)
    c: Block(g19)
    c: Block(g20)
    c: Block(g21)
    c: Block(g22)
    c: Block(g23)
    c: Block(g11)
    c: Block(g9)
    c: Block(g7)
    c: Block(g5)
    c: Block(g3)
    c: Block(g1)
    c: Coincident(g24,g0)
    c: Coincident(g24,g12)
    c: Horizontal(g24)
    c: Coincident(g25,g0)
    c: Coincident(g25,g12)
    c: Horizontal(g25)
    c: Coincident(g26,g1)
    c: Coincident(g26,g13)
    c: Horizontal(g26)
    c: Coincident(g27,g1)
    c: Coincident(g27,g13)
    c: Horizontal(g27)
    c: Coincident(g28,g2)
    c: Coincident(g28,g14)
    c: Horizontal(g28)
    c: Coincident(g29,g2)
    c: Coincident(g29,g14)
    c: Horizontal(g29)
    c: Coincident(g30,g3)
    c: Coincident(g30,g15)
    c: Horizontal(g30)
    c: Coincident(g31,g3)
    c: Coincident(g31,g15)
    c: Horizontal(g31)
    c: Coincident(g32,g4)
    c: Coincident(g32,g16)
    c: Horizontal(g32)
    c: Coincident(g33,g4)
    c: Coincident(g33,g16)
    c: Horizontal(g33)
    c: Coincident(g34,g5)
    c: Coincident(g34,g17)
    c: Horizontal(g34)
    c: Coincident(g35,g5)
    c: Coincident(g35,g17)
    c: Horizontal(g35)
    c: Coincident(g36,g6)
    c: Coincident(g36,g19)
    c: Horizontal(g36)
    c: Coincident(g37,g6)
    c: Coincident(g37,g19)
    c: Horizontal(g37)
    c: Coincident(g38,g7)
    c: Coincident(g38,g18)
    c: Horizontal(g38)
    c: Coincident(g39,g7)
    c: Coincident(g39,g18)
    c: Horizontal(g39)
    c: Coincident(g40,g8)
    c: Coincident(g40,g20)
    c: Horizontal(g40)
    c: Coincident(g41,g8)
    c: Coincident(g41,g20)
    c: Horizontal(g41)
    c: Coincident(g42,g9)
    c: Coincident(g42,g23)
    c: Horizontal(g42)
    c: Coincident(g43,g9)
    c: Coincident(g43,g23)
    c: Horizontal(g43)
    c: Coincident(g44,g10)
    c: Coincident(g44,g22)
    c: Horizontal(g44)
    c: Coincident(g45,g10)
    c: Coincident(g45,g22)
    c: Horizontal(g45)
    c: Coincident(g46,g11)
    c: Coincident(g46,g21)
    c: Horizontal(g46)
    c: Coincident(g47,g11)
    c: Coincident(g47,g21)
    c: Horizontal(g47)
FEATURE [Part::Extrusion] Extrude061
  Base = -> Sketch070
  Dir = (1,0,0)
  DirMode = 2
  FaceMakerClass = Part::FaceMakerBullseye
  LengthFwd = 23
  LengthRev = 0
  Placement = pos=(-19,0,0) rot=(0,0,1;0rad)
  Solid = true
  Symmetric = false
FEATURE [Part::Fillet] Fillet052  label="removeToCreateVentalationHoles002"
  Base = -> Extrude061
  Edges = <same value as first occurrence — deduplicated (x6 in doc)>
  Placement = pos=(7,0.02,0) rot=(0,0,1;0rad)
FEATURE [Part::MultiFuse] Fusion130  label="bottom013"
  Shapes = -> [Cut054,Cut034]
FEATURE [Part::Cut] Cut055
  Base = -> Fusion130
  Tool = -> Fillet052
FEATURE [Part::Cylinder] Cylinder054
  Angle = 360
  AttacherType = Attacher::AttachEngine3D
  Height = 20
  Placement = pos=(0,0,36.15) rot=(0,0,1;0rad)
  Radius = 4
FEATURE [Sketcher::SketchObject] Sketch071  label="bottomSketch002"
  FullyConstrained = true
  sketch-geometry (32):
    g0: LineSegment StartX=3.3 StartY=-6.03275e-07 StartZ=0 EndX=98 EndY=-6.03275e-07 EndZ=0
    g1: ArcOfCircle CenterX=98 CenterY=19 CenterZ=0 NormalX=0 NormalY=0 NormalZ=1 AngleXU=0 Radius=19 StartAngle=4.71239 EndAngle=5.71103
    g2: LineSegment StartX=6.3 StartY=8 StartZ=0 EndX=3.3 EndY=8 EndZ=0
    g3: LineSegment StartX=3.3 StartY=8 StartZ=0 EndX=3.3 EndY=-6.03275e-07 EndZ=0
    g4: ArcOfCircle CenterX=8.3 CenterY=5 CenterZ=0 NormalX=0 NormalY=0 NormalZ=1 AngleXU=0 Radius=2 StartAngle=3.14159 EndAngle=4.71239
    g5: LineSegment StartX=6.3 StartY=8 StartZ=0 EndX=6.3 EndY=5 EndZ=0
    g6: ArcOfCircle CenterX=98 CenterY=19 CenterZ=0 NormalX=0 NormalY=0 NormalZ=1 AngleXU=0 Radius=12.7 StartAngle=4.71239 EndAngle=6.28319
    g7: LineSegment StartX=94.7 StartY=3 StartZ=0 EndX=8.3 EndY=3 EndZ=0
    g8-g12: Circle x5 (B-spline internal-alignment scaffolding for g13; pole/knot coordinates omitted)
    g13: BSplineCurve PolesCount=5 KnotsCount=3 Degree=3 IsPeriodic=0
    g14: GeomPoint X=98 Y=6.3 Z=0
    g15: GeomPoint X=96.3938 Y=4.71946 Z=0
    g16: GeomPoint X=94.7 Y=3 Z=0
    g17-g23: Circle x7 (B-spline internal-alignment scaffolding for g24; pole/knot coordinates omitted)
    g24: BSplineCurve PolesCount=7 KnotsCount=5 Degree=3 IsPeriodic=0
    g25-g29: GeomPoint x5 (B-spline internal-alignment scaffolding for g24; pole/knot coordinates omitted)
    g30: ArcOfCircle CenterX=98 CenterY=19 CenterZ=0 NormalX=0 NormalY=0 NormalZ=1 AngleXU=0 Radius=15.7 StartAngle=5.81226 EndAngle=6.28319
    g31: LineSegment StartX=110.7 StartY=19 StartZ=0 EndX=113.7 EndY=19 EndZ=0
  constraints (41):
    c: Horizontal(g0)
    c: Coincident(g1,g0)
    c: Block(g1)
    c: Horizontal(g2)
    c: Distance(g2) = 3
    c: Coincident(g3,g2)
    c: Vertical(g3)
    c: Coincident(g3,g0)
    c: Block(g4)
    c: Block(g2)
    c: Coincident(g5,g2)
    c: Coincident(g5,g4)
    c: Vertical(g5)
    c: Coincident(g6,g1)
    c: Block(g6)
    c: Coincident(g7,g4)
    c: Horizontal(g7)
    c: Block(g0)
    c: Block(g7)
    c: Block(g3)
    c: Coincident(g13,g6)
    c: Weight(g8) = 1
    c: Equal(g8, g9-g12) x4
    c: Coincident(g13,g7)
    c: InternalAlignment(g8-g12 -> g13) x5
    c: InternalAlignment(g14,g13)
    c: InternalAlignment(g15,g13)
    c: InternalAlignment(g16,g13)
    c: Block(g13)
    c: Weight(g17) = 1
    c: Equal(g17, g18-g23) x6
    c: Coincident(g24,g1)
    c: InternalAlignment(g17-g23 -> g24) x7
    c: InternalAlignment(g25-g29 -> g24) x5
    c: Block(g24)
    c: Coincident(g30,g24)
    c: Coincident(g31,g6)
    c: Coincident(g31,g30)
    c: Horizontal(g31)
    c: Block(g31)
    c: Block(g30)
FEATURE [Part::Extrusion] Extrude062  label="bottom014"
  Base = -> Sketch071
  Dir = (0,0,1)
  DirMode = 2
  FaceMakerClass = Part::FaceMakerBullseye
  LengthFwd = 71.4
  LengthRev = 0
  Placement = pos=(0,0,0.3) rot=(0,0,1;0rad)
  Solid = true
  Symmetric = false
FEATURE [Part::Fillet] Fillet054
  Base = -> Extrude062
  Edges = 1 edges r=2.4: [Edge17]
FEATURE [Part::Fillet] Fillet055  label="bottom015"
  Base = -> Fillet054
  Edges = 1 edges r=2.4: [Edge36]
FEATURE [Part::Cylinder] Cylinder055
  Angle = 360
  AttacherType = Attacher::AttachEngine3D
  Height = 10
  Placement = pos=(0,0,36.15) rot=(0,0,1;0rad)
  Radius = 4
FEATURE [Part::MultiFuse] Fusion131  label="removeToCreateHoleForPlugHousing002"
  Placement = pos=(70,19,36.15) rot=(0,1,0;1.5708rad)
  Shapes = -> [Cylinder054,Cylinder055]
FEATURE [Part::Cut] Cut056  label="Bottom001"
  Base = -> Fillet055
  Placement = pos=(9,0,0) rot=(0,0,1;0rad)
  Tool = -> Fusion131
FEATURE [Part::Cut] Cut057
  Base = -> Cut055
  Tool = -> Cut056
FEATURE [Sketcher::SketchObject] Sketch072  label="topSketch021"
  FullyConstrained = true
  sketch-geometry (4):
    g0: ArcOfCircle CenterX=105 CenterY=19 CenterZ=0 NormalX=0 NormalY=0 NormalZ=1 AngleXU=0 Radius=20.6155 StartAngle=5.54125 EndAngle=6.28319
    g1: ArcOfCircle CenterX=105 CenterY=19 CenterZ=0 NormalX=0 NormalY=0 NormalZ=1 AngleXU=0 Radius=13 StartAngle=5.54125 EndAngle=6.28319
    g2: LineSegment StartX=118 StartY=19 StartZ=0 EndX=125.616 EndY=19 EndZ=0
    g3: LineSegment StartX=114.583 StartY=10.2157 StartZ=0 EndX=120.197 EndY=5.06982 EndZ=0
  constraints (7):
    c: Block(g0)
    c: Block(g1)
    c: Coincident(g2,g1)
    c: Coincident(g2,g0)
    c: Horizontal(g2)
    c: Coincident(g3,g1)
    c: Coincident(g3,g0)
FEATURE [Part::Extrusion] Extrude063  label="bottomPlugHousingBit003"
  Base = -> Sketch072
  Dir = (0,0,1)
  DirMode = 2
  FaceMakerClass = Part::FaceMakerBullseye
  LengthFwd = 72
  LengthRev = 0
  Solid = true
  Symmetric = false
FEATURE [Part::Cylinder] Cylinder056
  Angle = 360
  AttacherType = Attacher::AttachEngine3D
  Height = 20
  Placement = pos=(0,0,36.15) rot=(0,0,1;0rad)
  Radius = 14.3
FEATURE [Part::Cylinder] Cylinder057
  Angle = 360
  AttacherType = Attacher::AttachEngine3D
  Height = 10
  Placement = pos=(0,0,36.15) rot=(0,0,1;0rad)
  Radius = 4
FEATURE [Part::Box] Box034  label="removeToCreteHoleForPlugHousing047"
  AttacherType = Attacher::AttachEngine3D
  Height = 28.6
  Length = 20
  Placement = pos=(106.15,0,21.7) rot=(0,0,1;0rad)
  Width = 19
FEATURE [Part::Cylinder] Cylinder058
  Angle = 360
  AttacherType = Attacher::AttachEngine3D
  Height = 20
  Placement = pos=(0,0,36.15) rot=(0,0,1;0rad)
  Radius = 14.3
FEATURE [Part::Cylinder] Cylinder059
  Angle = 360
  AttacherType = Attacher::AttachEngine3D
  Height = 10
  Placement = pos=(0,0,36.15) rot=(0,0,1;0rad)
  Radius = 4
FEATURE [Part::MultiFuse] Fusion134  label="removeToCreteHoleForPlugHousing046"
  Placement = pos=(70,19,36) rot=(0,1,0;1.5708rad)
  Shapes = -> [Cylinder058,Cylinder059]
FEATURE [Part::Cylinder] Cylinder060
  Angle = 360
  AttacherType = Attacher::AttachEngine3D
  Height = 20
  Placement = pos=(0,0,36.15) rot=(0,0,1;0rad)
  Radius = 14
FEATURE [Part::Cylinder] Cylinder061
  Angle = 360
  AttacherType = Attacher::AttachEngine3D
  Height = 10
  Placement = pos=(0,0,36.15) rot=(0,0,1;0rad)
  Radius = 4
FEATURE [Part::MultiFuse] Fusion135  label="removeToCreteHoleForPlugHousing048"
  Placement = pos=(70,19,36) rot=(0,1,0;1.5708rad)
  Shapes = -> [Cylinder060,Cylinder061]
FEATURE [Part::Box] Box035  label="removeToCreteHoleForPlugHousing049"
  AttacherType = Attacher::AttachEngine3D
  Height = 28.6
  Length = 20
  Placement = pos=(106.15,0,21.7) rot=(0,0,1;0rad)
  Width = 19
FEATURE [Part::MultiFuse] Fusion133  label="removeToCreteHoleForPlugHousing045"
  Placement = pos=(0,0,-28.3) rot=(0,0,1;0rad)
  Shapes = -> [Box035,Fusion134]
FEATURE [Part::MultiFuse] Fusion138  label="removeToCreteHoleForPlugHousing051"
  Placement = pos=(70,19,36) rot=(0,1,0;1.5708rad)
  Shapes = -> [Cylinder056,Cylinder057]
FEATURE [Part::MultiFuse] Fusion137  label="removeToCreteHoleForPlugHousing050"
  Placement = pos=(0,0,28.3) rot=(0,0,1;0rad)
  Shapes = -> [Box034,Fusion138]
FEATURE [Part::MultiFuse] Fusion132  label="removeToCreatePlugHousingBottomBit002"
  Shapes = -> [Fusion133,Fusion137]
FEATURE [Part::MultiFuse] Fusion136  label="removeToCreatePlugHousingBottomBit003"
  Shapes = -> [Fusion135,Fusion132]
FEATURE [Part::Cut] Cut058  label="bottomPlugHousingBit002"
  Base = -> Extrude063
  Placement = pos=(-0.09,0,0) rot=(0,0,1;0rad)
  Tool = -> Fusion136
FEATURE [Sketcher::SketchObject] Sketch073  label="bottomSketch003"
  FullyConstrained = true
  sketch-geometry (45):
    g0: LineSegment StartX=6.29999 StartY=8 StartZ=0 EndX=3.29999 EndY=8 EndZ=0
    g1: LineSegment StartX=3.29999 StartY=8 StartZ=0 EndX=3.29999 EndY=-6.03275e-07 EndZ=0
    g2: ArcOfCircle CenterX=8.29999 CenterY=5 CenterZ=0 NormalX=0 NormalY=0 NormalZ=1 AngleXU=0 Radius=2 StartAngle=3.14159 EndAngle=4.71239
    g3: LineSegment StartX=6.29999 StartY=8 StartZ=0 EndX=6.29999 EndY=5 EndZ=0
    g4: ArcOfCircle CenterX=105 CenterY=19 CenterZ=0 NormalX=0 NormalY=0 NormalZ=1 AngleXU=0 Radius=12.7 StartAngle=4.71239 EndAngle=5.94289
    g5-g11: Circle x7 (B-spline internal-alignment scaffolding for g12; pole/knot coordinates omitted)
    g12: BSplineCurve PolesCount=7 KnotsCount=5 Degree=3 IsPeriodic=0
    g13-g17: GeomPoint x5 (B-spline internal-alignment scaffolding for g12; pole/knot coordinates omitted)
    g18: ArcOfCircle CenterX=105 CenterY=19 CenterZ=0 NormalX=0 NormalY=0 NormalZ=1 AngleXU=0 Radius=15.7 StartAngle=5.81226 EndAngle=6.28319
    g19: BSplineCurve PolesCount=5 KnotsCount=3 Degree=3 IsPeriodic=0
    g20: LineSegment StartX=8.29999 StartY=3 StartZ=0 EndX=101.7 EndY=3 EndZ=0
    g21: LineSegment StartX=3.29999 StartY=-6.03275e-07 StartZ=0 EndX=105 EndY=-6.03275e-07 EndZ=0
    g22: LineSegment StartX=120.974 StartY=8.71251 StartZ=0 EndX=122.332 EndY=7.83778 EndZ=0
    g23: LineSegment StartX=105 StartY=-6.03274e-07 StartZ=0 EndX=113 EndY=-6.03274e-07 EndZ=0
    g24: ArcOfCircle CenterX=105 CenterY=19 CenterZ=0 NormalX=0 NormalY=0 NormalZ=1 AngleXU=0 Radius=20.6155 StartAngle=5.11091 EndAngle=5.71103
    g25: ArcOfCircle CenterX=117.7 CenterY=19 CenterZ=0 NormalX=0 NormalY=0 NormalZ=1 AngleXU=0 Radius=3 StartAngle=1.2e-15 EndAngle=2.10468
    g26: Circle CenterX=116.345 CenterY=16.3232 CenterZ=0 NormalX=0 NormalY=0 NormalZ=1 AngleXU=0 Radius=1
    g27: Circle CenterX=117.24 CenterY=15.7584 CenterZ=0 NormalX=0 NormalY=0 NormalZ=1 AngleXU=0 Radius=1
    g28: Circle CenterX=116.972 CenterY=14.7612 CenterZ=0 NormalX=0 NormalY=0 NormalZ=1 AngleXU=0 Radius=1
    g29: BSplineCurve PolesCount=3 KnotsCount=2 Degree=2 IsPeriodic=0
    g30: GeomPoint X=116.345 Y=16.3232 Z=0
    g31: GeomPoint X=116.972 Y=14.7612 Z=0
    g32: Circle CenterX=115.828 CenterY=17.157 CenterZ=0 NormalX=0 NormalY=0 NormalZ=1 AngleXU=0 Radius=1
    g33: Circle CenterX=115.841 CenterY=16.639 CenterZ=0 NormalX=0 NormalY=0 NormalZ=1 AngleXU=0 Radius=1
    g34: Circle CenterX=116.345 CenterY=16.3232 CenterZ=0 NormalX=0 NormalY=0 NormalZ=1 AngleXU=0 Radius=1
    g35: BSplineCurve PolesCount=3 KnotsCount=2 Degree=2 IsPeriodic=0
    g36: GeomPoint X=115.828 Y=17.157 Z=0
    g37: GeomPoint X=116.345 Y=16.3232 Z=0
    g38: LineSegment StartX=115.828 StartY=17.157 StartZ=0 EndX=115.828 EndY=20.8307 EndZ=0
    g39: Circle CenterX=115.828 CenterY=20.8307 CenterZ=0 NormalX=0 NormalY=0 NormalZ=1 AngleXU=0 Radius=1
    g40: Circle CenterX=115.831 CenterY=21.3396 CenterZ=0 NormalX=0 NormalY=0 NormalZ=1 AngleXU=0 Radius=1
    g41: Circle CenterX=116.173 CenterY=21.5825 CenterZ=0 NormalX=0 NormalY=0 NormalZ=1 AngleXU=0 Radius=1
    g42: BSplineCurve PolesCount=3 KnotsCount=2 Degree=2 IsPeriodic=0
    g43: GeomPoint X=115.828 Y=20.8307 Z=0
    g44: GeomPoint X=116.173 Y=21.5825 Z=0
  constraints (70):
    c: Horizontal(g0)
    c: Distance(g0) = 3
    c: Coincident(g1,g0)
    c: Vertical(g1)
    c: Block(g2)
    c: Block(g0)
    c: Coincident(g3,g0)
    c: Coincident(g3,g2)
    c: Vertical(g3)
    c: Block(g1)
    c: Block(g4)
    c: Coincident(g19,g4)
    c: Block(g19)
    c: Equal(g5, g6-g11) x6
    c: InternalAlignment(g5-g11 -> g12) x7
    c: InternalAlignment(g13-g17 -> g12) x5
    c: Block(g12)
    c: Coincident(g18,g12)
    c: Block(g18)
    c: Coincident(g20,g2)
    c: Coincident(g20,g19)
    c: Horizontal(g20)
    c: Distance(g20) = 93.4
    c: Coincident(g21,g1)
    c: Horizontal(g21)
    c: Distance(g21) = 101.7
    c: Horizontal(g23)
    c: Distance(g23) = 8
    c: Coincident(g24,g23)
    c: Block(g23)
    c: Coincident(g22,g24)
    c: Block(g24)
    c: Block(g22)
    c: Distance(g22) = 1.61553
    c: Coincident(g25,g18)
    c: Block(g25)
    c: Weight(g26) = 1
    c: Equal(g26,g27)
    c: Equal(g26,g28)
    c: Coincident(g29,g4)
    c: InternalAlignment(g26,g29)
    c: InternalAlignment(g27,g29)
    c: InternalAlignment(g28,g29)
    c: InternalAlignment(g30,g29)
    c: InternalAlignment(g31,g29)
    c: Block(g29)
    c: Weight(g32) = 1
    c: Equal(g32,g33)
    c: Equal(g32,g34)
    c: Coincident(g35,g29)
    c: InternalAlignment(g32,g35)
    c: InternalAlignment(g33,g35)
    c: InternalAlignment(g34,g35)
    c: InternalAlignment(g36,g35)
    c: InternalAlignment(g37,g35)
    c: Block(g35)
    c: Coincident(g38,g35)
    c: Vertical(g38)
    c: Block(g38)
    c: Coincident(g42,g38)
    c: Weight(g39) = 1
    c: Equal(g39,g40)
    c: Equal(g39,g41)
    c: Coincident(g42,g25)
    c: InternalAlignment(g39,g42)
    c: InternalAlignment(g40,g42)
    c: InternalAlignment(g41,g42)
    c: InternalAlignment(g43,g42)
    c: InternalAlignment(g44,g42)
    c: Block(g42)
FEATURE [Part::Extrusion] Extrude064  label="bottom016"
  Base = -> Sketch073
  Dir = (0,0,1)
  DirMode = 2
  FaceMakerClass = Part::FaceMakerBullseye
  LengthFwd = 71.4
  LengthRev = 0
  Placement = pos=(0,0,0.3) rot=(0,0,1;0rad)
  Solid = true
  Symmetric = false
FEATURE [Part::Revolution] Revolve157  label="removeToCreateScrewAndThreadedInsertHole063"
  Angle = 360
  Axis = (0,1,0)
  Base = (0,0,0)
  FaceMakerClass = Part::FaceMakerBullseye
  Placement = pos=(12.5,0,10) rot=(0,0,1;0rad)
  Solid = false
  Source = -> Face141
  Symmetric = false
FEATURE [Sketcher::SketchObject] Sketch074
  FullyConstrained = true
  Placement = pos=(117,19,0) rot=(0.57735,0.57735,0.57735;2.0944rad)
  sketch-geometry (48):
    g0: LineSegment StartX=-49.19 StartY=69.25 StartZ=0 EndX=-49.19 EndY=66.25 EndZ=0
    g1: LineSegment StartX=-49.19 StartY=63.5 StartZ=0 EndX=-49.19 EndY=60.5 EndZ=0
    g2: LineSegment StartX=-49.19 StartY=57.75 StartZ=0 EndX=-49.19 EndY=54.75 EndZ=0
    g3: LineSegment StartX=-49.19 StartY=52 StartZ=0 EndX=-49.19 EndY=49 EndZ=0
    g4: LineSegment StartX=-49.19 StartY=46.25 StartZ=0 EndX=-49.19 EndY=43.25 EndZ=0
    g5: LineSegment StartX=-49.19 StartY=40.5 StartZ=0 EndX=-49.19 EndY=37.5 EndZ=0
    g6: LineSegment StartX=-49.19 StartY=34.5 StartZ=0 EndX=-49.19 EndY=31.5 EndZ=0
    g7: LineSegment StartX=-49.19 StartY=28.75 StartZ=0 EndX=-49.19 EndY=25.75 EndZ=0
    g8: LineSegment StartX=-49.19 StartY=23 StartZ=0 EndX=-49.19 EndY=20 EndZ=0
    g9: LineSegment StartX=-49.19 StartY=17.25 StartZ=0 EndX=-49.19 EndY=14.25 EndZ=0
    g10: LineSegment StartX=-49.19 StartY=11.5 StartZ=0 EndX=-49.19 EndY=8.5 EndZ=0
    g11: LineSegment StartX=-49.19 StartY=5.75 StartZ=0 EndX=-49.19 EndY=2.75 EndZ=0
    g12: ArcOfCircle CenterX=-1.5 CenterY=67.75 CenterZ=0 NormalX=0 NormalY=0 NormalZ=1 AngleXU=0 Radius=1.5 StartAngle=4.71239 EndAngle=7.85398
    g13: ArcOfCircle CenterX=-1.5 CenterY=62 CenterZ=0 NormalX=0 NormalY=0 NormalZ=1 AngleXU=0 Radius=1.5 StartAngle=4.71239 EndAngle=7.85398
    g14: ArcOfCircle CenterX=-1.5 CenterY=56.25 CenterZ=0 NormalX=0 NormalY=0 NormalZ=1 AngleXU=0 Radius=1.5 StartAngle=4.71239 EndAngle=7.85398
    g15: ArcOfCircle CenterX=-11.49 CenterY=50.5 CenterZ=0 NormalX=0 NormalY=0 NormalZ=1 AngleXU=0 Radius=1.5 StartAngle=4.71239 EndAngle=7.85398
    g16: ArcOfCircle CenterX=-16.28 CenterY=44.75 CenterZ=0 NormalX=0 NormalY=0 NormalZ=1 AngleXU=0 Radius=1.5 StartAngle=4.71239 EndAngle=7.85398
    g17: ArcOfCircle CenterX=-18.2337 CenterY=39 CenterZ=0 NormalX=0 NormalY=0 NormalZ=1 AngleXU=0 Radius=1.5 StartAngle=4.71485 EndAngle=7.85398
    g18: ArcOfCircle CenterX=-16.2837 CenterY=27.25 CenterZ=0 NormalX=0 NormalY=0 NormalZ=1 AngleXU=0 Radius=1.5 StartAngle=4.71485 EndAngle=7.85398
    g19: ArcOfCircle CenterX=-18.2337 CenterY=33 CenterZ=0 NormalX=0 NormalY=0 NormalZ=1 AngleXU=0 Radius=1.5 StartAngle=4.71485 EndAngle=7.85398
    g20: ArcOfCircle CenterX=-11.49 CenterY=21.5 CenterZ=0 NormalX=0 NormalY=0 NormalZ=1 AngleXU=0 Radius=1.5 StartAngle=4.71239 EndAngle=7.85398
    g21: ArcOfCircle CenterX=-1.5 CenterY=4.25 CenterZ=0 NormalX=0 NormalY=0 NormalZ=1 AngleXU=0 Radius=1.5 StartAngle=4.71239 EndAngle=7.85398
    g22: ArcOfCircle CenterX=-1.5 CenterY=10 CenterZ=0 NormalX=0 NormalY=0 NormalZ=1 AngleXU=0 Radius=1.5 StartAngle=4.71239 EndAngle=7.85398
    g23: ArcOfCircle CenterX=-1.5 CenterY=15.75 CenterZ=0 NormalX=0 NormalY=0 NormalZ=1 AngleXU=0 Radius=1.5 StartAngle=4.71239 EndAngle=7.85398
    g24: LineSegment StartX=-49.19 StartY=69.25 StartZ=0 EndX=-1.5 EndY=69.25 EndZ=0
    g25: LineSegment StartX=-49.19 StartY=66.25 StartZ=0 EndX=-1.5 EndY=66.25 EndZ=0
    g26: LineSegment StartX=-49.19 StartY=63.5 StartZ=0 EndX=-1.5 EndY=63.5 EndZ=0
    g27: LineSegment StartX=-49.19 StartY=60.5 StartZ=0 EndX=-1.5 EndY=60.5 EndZ=0
    g28: LineSegment StartX=-49.19 StartY=57.75 StartZ=0 EndX=-1.5 EndY=57.75 EndZ=0
    g29: LineSegment StartX=-49.19 StartY=54.75 StartZ=0 EndX=-1.5 EndY=54.75 EndZ=0
    g30: LineSegment StartX=-49.19 StartY=52 StartZ=0 EndX=-11.49 EndY=52 EndZ=0
    g31: LineSegment StartX=-49.19 StartY=49 StartZ=0 EndX=-11.49 EndY=49 EndZ=0
    g32: LineSegment StartX=-49.19 StartY=46.25 StartZ=0 EndX=-16.28 EndY=46.25 EndZ=0
    g33: LineSegment StartX=-49.19 StartY=43.25 StartZ=0 EndX=-16.28 EndY=43.25 EndZ=0
    g34: LineSegment StartX=-49.19 StartY=40.5 StartZ=0 EndX=-18.2337 EndY=40.5 EndZ=0
    g35: LineSegment StartX=-49.19 StartY=37.5 StartZ=0 EndX=-18.23 EndY=37.5 EndZ=0
    g36: LineSegment StartX=-49.19 StartY=34.5 StartZ=0 EndX=-18.2337 EndY=34.5 EndZ=0
    g37: LineSegment StartX=-49.19 StartY=31.5 StartZ=0 EndX=-18.23 EndY=31.5 EndZ=0
    g38: LineSegment StartX=-49.19 StartY=28.75 StartZ=0 EndX=-16.2837 EndY=28.75 EndZ=0
    g39: LineSegment StartX=-49.19 StartY=25.75 StartZ=0 EndX=-16.28 EndY=25.75 EndZ=0
    g40: LineSegment StartX=-49.19 StartY=23 StartZ=0 EndX=-11.49 EndY=23 EndZ=0
    g41: LineSegment StartX=-49.19 StartY=20 StartZ=0 EndX=-11.49 EndY=20 EndZ=0
    g42: LineSegment StartX=-49.19 StartY=17.25 StartZ=0 EndX=-1.5 EndY=17.25 EndZ=0
    g43: LineSegment StartX=-49.19 StartY=14.25 StartZ=0 EndX=-1.5 EndY=14.25 EndZ=0
    g44: LineSegment StartX=-49.19 StartY=11.5 StartZ=0 EndX=-1.5 EndY=11.5 EndZ=0
    g45: LineSegment StartX=-49.19 StartY=8.5 StartZ=0 EndX=-1.5 EndY=8.5 EndZ=0
    g46: LineSegment StartX=-49.19 StartY=5.75 StartZ=0 EndX=-1.5 EndY=5.75 EndZ=0
    g47: LineSegment StartX=-49.19 StartY=2.75 StartZ=0 EndX=-1.5 EndY=2.75 EndZ=0
  constraints (120):
    c: Vertical(g0)
    c: Distance(g0) = 3
    c: Block(g0)
    c: Vertical(g1)
    c: Distance(g1) = 3
    c: Vertical(g2)
    c: Equal(g0,g2) = 3
    c: Block(g2)
    c: Vertical(g3)
    c: Equal(g1,g3) = 3
    c: Vertical(g4)
    c: Equal(g0,g4) = 3
    c: Block(g4)
    c: Vertical(g5)
    c: Equal(g1,g5) = 3
    c: Vertical(g6)
    c: Equal(g0,g6) = 3
    c: Block(g6)
    c: Vertical(g7)
    c: Equal(g1,g7) = 3
    c: Vertical(g8)
    c: Equal(g0,g8) = 3
    c: Block(g8)
    c: Vertical(g9)
    c: Equal(g1,g9) = 3
    c: Vertical(g10)
    c: Equal(g0,g10) = 3
    c: Block(g10)
    c: Vertical(g11)
    c: Equal(g1,g11) = 3
    c: Block(g12)
    c: Block(g13)
    c: Block(g14)
    c: Block(g15)
    c: Block(g16)
    c: Block(g17)
    c: Block(g18)
    c: Block(g19)
    c: Block(g20)
    c: Block(g21)
    c: Block(g22)
    c: Block(g23)
    c: Block(g11)
    c: Block(g9)
    c: Block(g7)
    c: Block(g5)
    c: Block(g3)
    c: Block(g1)
    c: Coincident(g24,g0)
    c: Coincident(g24,g12)
    c: Horizontal(g24)
    c: Coincident(g25,g0)
    c: Coincident(g25,g12)
    c: Horizontal(g25)
    c: Coincident(g26,g1)
    c: Coincident(g26,g13)
    c: Horizontal(g26)
    c: Coincident(g27,g1)
    c: Coincident(g27,g13)
    c: Horizontal(g27)
    c: Coincident(g28,g2)
    c: Coincident(g28,g14)
    c: Horizontal(g28)
    c: Coincident(g29,g2)
    c: Coincident(g29,g14)
    c: Horizontal(g29)
    c: Coincident(g30,g3)
    c: Coincident(g30,g15)
    c: Horizontal(g30)
    c: Coincident(g31,g3)
    c: Coincident(g31,g15)
    c: Horizontal(g31)
    c: Coincident(g32,g4)
    c: Coincident(g32,g16)
    c: Horizontal(g32)
    c: Coincident(g33,g4)
    c: Coincident(g33,g16)
    c: Horizontal(g33)
    c: Coincident(g34,g5)
    c: Coincident(g34,g17)
    c: Horizontal(g34)
    c: Coincident(g35,g5)
    c: Coincident(g35,g17)
    c: Horizontal(g35)
    c: Coincident(g36,g6)
    c: Coincident(g36,g19)
    c: Horizontal(g36)
    c: Coincident(g37,g6)
    c: Coincident(g37,g19)
    c: Horizontal(g37)
    c: Coincident(g38,g7)
    c: Coincident(g38,g18)
    c: Horizontal(g38)
    c: Coincident(g39,g7)
    c: Coincident(g39,g18)
    c: Horizontal(g39)
    c: Coincident(g40,g8)
    c: Coincident(g40,g20)
    c: Horizontal(g40)
    c: Coincident(g41,g8)
    c: Coincident(g41,g20)
    c: Horizontal(g41)
    c: Coincident(g42,g9)
    c: Coincident(g42,g23)
    c: Horizontal(g42)
    c: Coincident(g43,g9)
    c: Coincident(g43,g23)
    c: Horizontal(g43)
    c: Coincident(g44,g10)
    c: Coincident(g44,g22)
    c: Horizontal(g44)
    c: Coincident(g45,g10)
    c: Coincident(g45,g22)
    c: Horizontal(g45)
    c: Coincident(g46,g11)
    c: Coincident(g46,g21)
    c: Horizontal(g46)
    c: Coincident(g47,g11)
    c: Coincident(g47,g21)
    c: Horizontal(g47)
FEATURE [Part::Extrusion] Extrude065
  Base = -> Sketch074
  Dir = (1,0,0)
  DirMode = 2
  FaceMakerClass = Part::FaceMakerBullseye
  LengthFwd = 23
  LengthRev = 0
  Placement = pos=(-19,0,0) rot=(0,0,1;0rad)
  Solid = true
  Symmetric = false
FEATURE [Part::Fillet] Fillet056  label="removeToCreateVentalationHoles003"
  Base = -> Extrude065
  Edges = <same value as first occurrence — deduplicated (x6 in doc)>
  Placement = pos=(7,0.02,0) rot=(0,0,1;0rad)
FEATURE [Part::Revolution] Revolve158  label="removeToCreateScrewAndThreadedInsertHole065"
  Angle = 360
  Axis = (0,1,0)
  Base = (0,0,0)
  FaceMakerClass = Part::FaceMakerBullseye
  Placement = pos=(12.5,0,62) rot=(0,0,1;0rad)
  Solid = false
  Source = -> Face146
  Symmetric = false
FEATURE [Part::Revolution] Revolve159  label="removeToCreateScrewAndThreadedInsertHole066"
  Angle = 360
  Axis = (0,1,0)
  Base = (0,0,0)
  FaceMakerClass = Part::FaceMakerBullseye
  Placement = pos=(89.5,0,68.5) rot=(0,0,1;0rad)
  Solid = false
  Source = -> Face143
  Symmetric = false
FEATURE [Part::Revolution] Revolve160  label="removeToCreateScrewAndThreadedInsertHole067"
  Angle = 360
  Axis = (0,1,0)
  Base = (0,0,0)
  FaceMakerClass = Part::FaceMakerBullseye
  Placement = pos=(89.5,0,3.5) rot=(0,0,1;0rad)
  Solid = false
  Source = -> Face142
  Symmetric = false
FEATURE [Part::Revolution] Revolve161  label="removeToCreateScrewAndThreadedInsertHole068"
  Angle = 360
  Axis = (0,1,0)
  Base = (0,0,0)
  FaceMakerClass = Part::FaceMakerBullseye
  Placement = pos=(109.5,4.7,3.5) rot=(0,0,1;0rad)
  Solid = false
  Source = -> Face145
  Symmetric = false
FEATURE [Part::Revolution] Revolve162  label="removeToCreateScrewAndThreadedInsertHole069"
  Angle = 360
  Axis = (0,1,0)
  Base = (0,0,0)
  FaceMakerClass = Part::FaceMakerBullseye
  Placement = pos=(109.5,4.7,68.5) rot=(0,0,1;0rad)
  Solid = false
  Source = -> Face144
  Symmetric = false
FEATURE [Part::MultiFuse] Fusion141  label="removeToCreateScrewAndThreadedInsertHole064"
  Shapes = -> [Revolve162,Revolve161,Revolve160,Revolve159,Revolve158,Revolve157]
FEATURE [Part::Cylinder] Cylinder062
  Angle = 360
  AttacherType = Attacher::AttachEngine3D
  Height = 20
  Placement = pos=(0,0,36.15) rot=(0,0,1;0rad)
  Radius = 14
FEATURE [Part::Cylinder] Cylinder063
  Angle = 360
  AttacherType = Attacher::AttachEngine3D
  Height = 10
  Placement = pos=(0,0,36.15) rot=(0,0,1;0rad)
  Radius = 4
FEATURE [Part::MultiFuse] Fusion139  label="removeToCreteHoleForPlugHousing052"
  Placement = pos=(70,19,36) rot=(0,1,0;1.5708rad)
  Shapes = -> [Cylinder062,Cylinder063]
FEATURE [Part::Cut] Cut060  label="bottom017"
  Base = -> Extrude064
  Tool = -> Fusion139
FEATURE [Part::Cut] Cut061  label="bottom019"
  Base = -> Cut060
  Tool = -> Fusion141
FEATURE [Part::MultiFuse] Fusion140  label="bottom018"
  Shapes = -> [Cut061,Cut058]
FEATURE [Part::Cut] Cut059  label="bottom020"
  Base = -> Fusion140
  Tool = -> Fillet056
FEATURE [Part::Box] Box036  label="Cube021"
  AttacherType = Attacher::AttachEngine3D
  Height = 80
  Length = 26
  Placement = pos=(0,-1,-5) rot=(0,0,1;0rad)
  Width = 11
FEATURE [Part::Cut] Cut062  label="removeFromBottom002"
  Base = -> Cut057
  Tool = -> Box036
FEATURE [Part::Cut] Cut063
  Base = -> Cut059
  Tool = -> Cut062
FEATURE [Part::Cut] Cut064  label="pcbStands"
  Base = -> Fusion095
  Tool = -> Fusion127
FEATURE [Sketcher::SketchObject] Sketch075  label="topSketch022"
  FullyConstrained = true
  sketch-geometry (6):
    g0: LineSegment StartX=19 StartY=38 StartZ=0 EndX=117 EndY=38 EndZ=0
    g1: ArcOfCircle CenterX=19 CenterY=19 CenterZ=0 NormalX=0 NormalY=0 NormalZ=1 AngleXU=0 Radius=19 StartAngle=1.5708 EndAngle=3.14159
    g2: LineSegment StartX=117 StartY=38 StartZ=0 EndX=117 EndY=19 EndZ=0
    g3: LineSegment StartX=98 StartY=1.0161e-12 StartZ=0 EndX=5.22862e-06 EndY=1.0161e-12 EndZ=0
    g4: LineSegment StartX=5.22862e-06 StartY=19 StartZ=0 EndX=5.22862e-06 EndY=1.0161e-12 EndZ=0
    g5: ArcOfCircle CenterX=98 CenterY=19 CenterZ=0 NormalX=0 NormalY=0 NormalZ=1 AngleXU=0 Radius=19 StartAngle=4.71239 EndAngle=6.28319
  constraints (16):
    c: Horizontal(g0)
    c: Distance(g0) = 98
    c: Coincident(g1,g0)
    c: Block(g1)
    c: Coincident(g2,g0)
    c: Vertical(g2)
    c: Distance(g2) = 19
    c: Horizontal(g3)
    c: Coincident(g4,g1)
    c: Vertical(g4)
    c: Coincident(g3,g4)
    c: Block(g3)
    c: Coincident(g5,g2)
    c: Coincident(g5,g3)
    c: Block(g0)
    c: Block(g5)
FEATURE [Part::Extrusion] Extrude067  label="sideB003"
  Base = -> Sketch075
  Dir = (0,0,1)
  DirMode = 2
  FaceMakerClass = Part::FaceMakerBullseye
  LengthFwd = 3
  LengthRev = 0
  Placement = pos=(0,0,71.7) rot=(0,0,1;0rad)
  Solid = true
  Symmetric = false
FEATURE [Sketcher::SketchObject] Sketch076  label="topSketch023"
  FullyConstrained = true
  sketch-geometry (6):
    g0: LineSegment StartX=19 StartY=38 StartZ=0 EndX=117 EndY=38 EndZ=0
    g1: ArcOfCircle CenterX=19 CenterY=19 CenterZ=0 NormalX=0 NormalY=0 NormalZ=1 AngleXU=0 Radius=19 StartAngle=1.5708 EndAngle=3.14159
    g2: LineSegment StartX=117 StartY=38 StartZ=0 EndX=117 EndY=19 EndZ=0
    g3: LineSegment StartX=98 StartY=1.0161e-12 StartZ=0 EndX=5.22862e-06 EndY=1.0161e-12 EndZ=0
    g4: LineSegment StartX=5.22862e-06 StartY=19 StartZ=0 EndX=5.22862e-06 EndY=1.0161e-12 EndZ=0
    g5: ArcOfCircle CenterX=98 CenterY=19 CenterZ=0 NormalX=0 NormalY=0 NormalZ=1 AngleXU=0 Radius=19 StartAngle=4.71239 EndAngle=6.28319
  constraints (16):
    c: Horizontal(g0)
    c: Distance(g0) = 98
    c: Coincident(g1,g0)
    c: Block(g1)
    c: Coincident(g2,g0)
    c: Vertical(g2)
    c: Distance(g2) = 19
    c: Horizontal(g3)
    c: Coincident(g4,g1)
    c: Vertical(g4)
    c: Coincident(g3,g4)
    c: Block(g3)
    c: Coincident(g5,g2)
    c: Coincident(g5,g3)
    c: Block(g0)
    c: Block(g5)
FEATURE [Part::Extrusion] Extrude066  label="sideA003"
  Base = -> Sketch076
  Dir = (0,0,1)
  DirMode = 2
  FaceMakerClass = Part::FaceMakerBullseye
  LengthFwd = 3
  LengthRev = 0
  Placement = pos=(0,0,-2.7) rot=(0,0,1;0rad)
  Solid = true
  Symmetric = false
FEATURE [Part::MultiFuse] Fusion142  label="removeFromBottom003"
  Placement = pos=(2,0,0) rot=(0,0,1;0rad)
  Shapes = -> [Extrude066,Extrude067]
FEATURE [Part::Cut] Cut065  label="screwRetainers002"
  Base = -> Fusion096
  Tool = -> Fusion142
FEATURE [Sketcher::SketchObject] Sketch077
  FullyConstrained = true
  Placement = pos=(117,19,0) rot=(0.57735,0.57735,0.57735;2.0944rad)
  sketch-geometry (8):
    g0: LineSegment StartX=-49.19 StartY=63.5 StartZ=0 EndX=-49.19 EndY=60.5 EndZ=0
    g1: LineSegment StartX=-49.19 StartY=11.5 StartZ=0 EndX=-49.19 EndY=8.5 EndZ=0
    g2: ArcOfCircle CenterX=-1.5 CenterY=62 CenterZ=0 NormalX=0 NormalY=0 NormalZ=1 AngleXU=0 Radius=1.5 StartAngle=4.71239 EndAngle=7.85398
    g3: ArcOfCircle CenterX=-1.5 CenterY=10 CenterZ=0 NormalX=0 NormalY=0 NormalZ=1 AngleXU=0 Radius=1.5 StartAngle=4.71239 EndAngle=7.85398
    g4: LineSegment StartX=-49.19 StartY=63.5 StartZ=0 EndX=-1.5 EndY=63.5 EndZ=0
    g5: LineSegment StartX=-49.19 StartY=60.5 StartZ=0 EndX=-1.5 EndY=60.5 EndZ=0
    g6: LineSegment StartX=-49.19 StartY=11.5 StartZ=0 EndX=-1.5 EndY=11.5 EndZ=0
    g7: LineSegment StartX=-49.19 StartY=8.5 StartZ=0 EndX=-1.5 EndY=8.5 EndZ=0
  constraints (19):
    c: Vertical(g0)
    c: Distance(g0) = 3
    c: Vertical(g1)
    c: Block(g1)
    c: Block(g2)
    c: Block(g3)
    c: Block(g0)
    c: Coincident(g4,g0)
    c: Coincident(g4,g2)
    c: Horizontal(g4)
    c: Coincident(g5,g0)
    c: Coincident(g5,g2)
    c: Horizontal(g5)
    c: Coincident(g6,g1)
    c: Coincident(g6,g3)
    c: Horizontal(g6)
    c: Coincident(g7,g1)
    c: Coincident(g7,g3)
    c: Horizontal(g7)
FEATURE [Part::Extrusion] Extrude068
  Base = -> Sketch077
  Dir = (1,0,0)
  DirMode = 2
  FaceMakerClass = Part::FaceMakerBullseye
  LengthFwd = 10
  LengthRev = 0
  Solid = true
  Symmetric = false
FEATURE [Part::Fillet] Fillet057  label="removeFromtMoreFrontCaseScrewRetainers002"
  Base = -> Extrude068
  Edges = 4 edges r=1.49: [Edge6,Edge11,Edge18,Edge23]
  Placement = pos=(-12,0,0) rot=(0,0,1;0rad)
FEATURE [Sketcher::SketchObject] Sketch078
  FullyConstrained = true
  Placement = pos=(117,19,0) rot=(0.57735,0.57735,0.57735;2.0944rad)
  sketch-geometry (8):
    g0: LineSegment StartX=-49.19 StartY=69.25 StartZ=0 EndX=-49.19 EndY=66.25 EndZ=0
    g1: LineSegment StartX=-49.19 StartY=5.75 StartZ=0 EndX=-49.19 EndY=2.75 EndZ=0
    g2: ArcOfCircle CenterX=-1.5 CenterY=67.75 CenterZ=0 NormalX=0 NormalY=0 NormalZ=1 AngleXU=0 Radius=1.5 StartAngle=4.71239 EndAngle=7.85398
    g3: ArcOfCircle CenterX=-1.5 CenterY=4.25 CenterZ=0 NormalX=0 NormalY=0 NormalZ=1 AngleXU=0 Radius=1.5 StartAngle=4.71239 EndAngle=7.85398
    g4: LineSegment StartX=-49.19 StartY=69.25 StartZ=0 EndX=-1.5 EndY=69.25 EndZ=0
    g5: LineSegment StartX=-49.19 StartY=66.25 StartZ=0 EndX=-1.5 EndY=66.25 EndZ=0
    g6: LineSegment StartX=-49.19 StartY=5.75 StartZ=0 EndX=-1.5 EndY=5.75 EndZ=0
    g7: LineSegment StartX=-49.19 StartY=2.75 StartZ=0 EndX=-1.5 EndY=2.75 EndZ=0
  constraints (19):
    c: Vertical(g0)
    c: Distance(g0) = 3
    c: Block(g0)
    c: Vertical(g1)
    c: Block(g2)
    c: Block(g3)
    c: Block(g1)
    c: Coincident(g4,g0)
    c: Coincident(g4,g2)
    c: Horizontal(g4)
    c: Coincident(g5,g0)
    c: Coincident(g5,g2)
    c: Horizontal(g5)
    c: Coincident(g6,g1)
    c: Coincident(g6,g3)
    c: Horizontal(g6)
    c: Coincident(g7,g1)
    c: Coincident(g7,g3)
    c: Horizontal(g7)
FEATURE [Part::Extrusion] Extrude069
  Base = -> Sketch078
  Dir = (1,0,0)
  DirMode = 2
  FaceMakerClass = Part::FaceMakerBullseye
  LengthFwd = 10
  LengthRev = 0
  Solid = true
  Symmetric = false
FEATURE [Part::Fillet] Fillet058  label="removeFromtMoreFrontCaseScrewRetainers003"
  Base = -> Extrude069
  Edges = 4 edges r=1.49: [Edge6,Edge11,Edge18,Edge23]
  Placement = pos=(-4,0,0) rot=(0,0,1;0rad)
FEATURE [Part::Cut] Cut066
  Base = -> Cut065
  Tool = -> Fillet058
FEATURE [Part::Cut] Cut067  label="screwPillars"
  Base = -> Cut066
  Tool = -> Fillet057
FEATURE [Part::MultiFuse] Fusion143  label="bottom021"
  Shapes = -> [Cut031,Cut063]
FEATURE [Part::Cylinder] Cylinder
  Angle = 360
  AttacherType = Attacher::AttachEngine3D
  Height = 10
  Placement = pos=(20.65,12,4.68) rot=(1,0,0;1.5708rad)
  Radius = 2
FEATURE [Part::Cylinder] Cylinder064
  Angle = 360
  AttacherType = Attacher::AttachEngine3D
  Height = 10
  Placement = pos=(20.65,12,67.38) rot=(1,0,0;1.5708rad)
  Radius = 2
FEATURE [Part::Cylinder] Cylinder065
  Angle = 360
  AttacherType = Attacher::AttachEngine3D
  Height = 10
  Placement = pos=(77.15,12,67.38) rot=(1,0,0;1.5708rad)
  Radius = 2
FEATURE [Part::Cylinder] Cylinder066
  Angle = 360
  AttacherType = Attacher::AttachEngine3D
  Height = 10
  Placement = pos=(77.15,12,4.68) rot=(1,0,0;1.5708rad)
  Radius = 2
FEATURE [Part::MultiFuse] Fusion144  label="removeFromThreadedInsertHousing"
  Shapes = -> [Cylinder065,Cylinder064,Cylinder,Cylinder066]
FEATURE [Part::Cut] Cut068  label="pcbStands001"
  Base = -> Cut064
  Tool = -> Fusion144
FEATURE [Part::MultiFuse] Fusion145
  Shapes = -> [Cut068,Fusion143]
FEATURE [Part::MultiFuse] Fusion146
  Shapes = -> [Fusion145]
FEATURE [Part::MultiFuse] Fusion147  label="bottom022"
  Shapes = -> [Cut067,Fusion146]
FEATURE [Part::MultiFuse] Fusion148  label="casePillars005"
  Shapes = -> [Cut047,Fusion092]
FEATURE [Part::MultiFuse] Fusion149  label="bottom023"
  Shapes = -> [Fusion124,Fusion113,Fusion147]
FEATURE [Part::MultiFuse] Fusion150  label="topBits"
  Shapes = -> [Cut025,Fusion148,Cut030,Fillet034]
FEATURE [Part::Feature] Face149 .. Face152  x4 (patterned run collapsed; names and placements below)
  shape: bbox 3.2 x 1.5 x 2e-07 mm, 1 faces, 0 solids (baked)
FEATURE [Part::Feature] Face153
  shape: bbox 3.6 x 3.2 x 2e-07 mm, 1 faces, 0 solids (baked)
FEATURE [Part::Feature] Face154
  shape: bbox 3.6 x 3.2 x 2e-07 mm, 1 faces, 0 solids (baked)
FEATURE [Sketcher::SketchObject] Sketch079  label="topSketch024"
  FullyConstrained = true
  sketch-geometry (6):
    g0: LineSegment StartX=19 StartY=38 StartZ=0 EndX=117 EndY=38 EndZ=0
    g1: ArcOfCircle CenterX=19 CenterY=19 CenterZ=0 NormalX=0 NormalY=0 NormalZ=1 AngleXU=0 Radius=19 StartAngle=1.5708 EndAngle=3.14159
    g2: LineSegment StartX=117 StartY=38 StartZ=0 EndX=117 EndY=19 EndZ=0
    g3: LineSegment StartX=98 StartY=1.0161e-12 StartZ=0 EndX=5.22862e-06 EndY=1.0161e-12 EndZ=0
    g4: LineSegment StartX=5.22862e-06 StartY=19 StartZ=0 EndX=5.22862e-06 EndY=1.0161e-12 EndZ=0
    g5: ArcOfCircle CenterX=98 CenterY=19 CenterZ=0 NormalX=0 NormalY=0 NormalZ=1 AngleXU=0 Radius=19 StartAngle=4.71239 EndAngle=6.28319
  constraints (16):
    c: Horizontal(g0)
    c: Distance(g0) = 98
    c: Coincident(g1,g0)
    c: Block(g1)
    c: Coincident(g2,g0)
    c: Vertical(g2)
    c: Distance(g2) = 19
    c: Horizontal(g3)
    c: Coincident(g4,g1)
    c: Vertical(g4)
    c: Coincident(g3,g4)
    c: Block(g3)
    c: Coincident(g5,g2)
    c: Coincident(g5,g3)
    c: Block(g0)
    c: Block(g5)
FEATURE [Sketcher::SketchObject] Sketch080  label="topSketch025"
  FullyConstrained = true
  sketch-geometry (6):
    g0: LineSegment StartX=19 StartY=38 StartZ=0 EndX=117 EndY=38 EndZ=0
    g1: ArcOfCircle CenterX=19 CenterY=19 CenterZ=0 NormalX=0 NormalY=0 NormalZ=1 AngleXU=0 Radius=19 StartAngle=1.5708 EndAngle=3.14159
    g2: LineSegment StartX=117 StartY=38 StartZ=0 EndX=117 EndY=19 EndZ=0
    g3: LineSegment StartX=98 StartY=1.0161e-12 StartZ=0 EndX=5.22862e-06 EndY=1.0161e-12 EndZ=0
    g4: LineSegment StartX=5.22862e-06 StartY=19 StartZ=0 EndX=5.22862e-06 EndY=1.0161e-12 EndZ=0
    g5: ArcOfCircle CenterX=98 CenterY=19 CenterZ=0 NormalX=0 NormalY=0 NormalZ=1 AngleXU=0 Radius=19 StartAngle=4.71239 EndAngle=6.28319
  constraints (16):
    c: Horizontal(g0)
    c: Distance(g0) = 98
    c: Coincident(g1,g0)
    c: Block(g1)
    c: Coincident(g2,g0)
    c: Vertical(g2)
    c: Distance(g2) = 19
    c: Horizontal(g3)
    c: Coincident(g4,g1)
    c: Vertical(g4)
    c: Coincident(g3,g4)
    c: Block(g3)
    c: Coincident(g5,g2)
    c: Coincident(g5,g3)
    c: Block(g0)
    c: Block(g5)
FEATURE [Part::Extrusion] Extrude070  label="sideA004"
  Base = -> Sketch080
  Dir = (0,0,1)
  DirMode = 2
  FaceMakerClass = Part::FaceMakerBullseye
  LengthFwd = 3
  LengthRev = 0
  Placement = pos=(0,0,-2.7) rot=(0,0,1;0rad)
  Solid = true
  Symmetric = false
FEATURE [Sketcher::SketchObject] Sketch081
  FullyConstrained = true
  Placement = pos=(117,19,0) rot=(0.57735,0.57735,0.57735;2.0944rad)
  sketch-geometry (8):
    g0: LineSegment StartX=-49.19 StartY=63.5 StartZ=0 EndX=-49.19 EndY=60.5 EndZ=0
    g1: LineSegment StartX=-49.19 StartY=11.5 StartZ=0 EndX=-49.19 EndY=8.5 EndZ=0
    g2: ArcOfCircle CenterX=-1.5 CenterY=62 CenterZ=0 NormalX=0 NormalY=0 NormalZ=1 AngleXU=0 Radius=1.5 StartAngle=4.71239 EndAngle=7.85398
    g3: ArcOfCircle CenterX=-1.5 CenterY=10 CenterZ=0 NormalX=0 NormalY=0 NormalZ=1 AngleXU=0 Radius=1.5 StartAngle=4.71239 EndAngle=7.85398
    g4: LineSegment StartX=-49.19 StartY=63.5 StartZ=0 EndX=-1.5 EndY=63.5 EndZ=0
    g5: LineSegment StartX=-49.19 StartY=60.5 StartZ=0 EndX=-1.5 EndY=60.5 EndZ=0
    g6: LineSegment StartX=-49.19 StartY=11.5 StartZ=0 EndX=-1.5 EndY=11.5 EndZ=0
    g7: LineSegment StartX=-49.19 StartY=8.5 StartZ=0 EndX=-1.5 EndY=8.5 EndZ=0
  constraints (19):
    c: Vertical(g0)
    c: Distance(g0) = 3
    c: Vertical(g1)
    c: Block(g1)
    c: Block(g2)
    c: Block(g3)
    c: Block(g0)
    c: Coincident(g4,g0)
    c: Coincident(g4,g2)
    c: Horizontal(g4)
    c: Coincident(g5,g0)
    c: Coincident(g5,g2)
    c: Horizontal(g5)
    c: Coincident(g6,g1)
    c: Coincident(g6,g3)
    c: Horizontal(g6)
    c: Coincident(g7,g1)
    c: Coincident(g7,g3)
    c: Horizontal(g7)
FEATURE [Part::Extrusion] Extrude071  label="sideB004"
  Base = -> Sketch079
  Dir = (0,0,1)
  DirMode = 2
  FaceMakerClass = Part::FaceMakerBullseye
  LengthFwd = 3
  LengthRev = 0
  Placement = pos=(0,0,71.7) rot=(0,0,1;0rad)
  Solid = true
  Symmetric = false
FEATURE [Part::MultiFuse] Fusion152  label="removeFromBottom004"
  Placement = pos=(2,0,0) rot=(0,0,1;0rad)
  Shapes = -> [Extrude070,Extrude071]
FEATURE [Part::Extrusion] Extrude072
  Base = -> Sketch081
  Dir = (1,0,0)
  DirMode = 2
  FaceMakerClass = Part::FaceMakerBullseye
  LengthFwd = 10
  LengthRev = 0
  Solid = true
  Symmetric = false
FEATURE [Part::Fillet] Fillet059  label="removeFromtMoreFrontCaseScrewRetainers004"
  Base = -> Extrude072
  Edges = 4 edges r=1.49: [Edge6,Edge11,Edge18,Edge23]
  Placement = pos=(-12,0,0) rot=(0,0,1;0rad)
FEATURE [Sketcher::SketchObject] Sketch082
  FullyConstrained = true
  Placement = pos=(117,19,0) rot=(0.57735,0.57735,0.57735;2.0944rad)
  sketch-geometry (8):
    g0: LineSegment StartX=-49.19 StartY=69.25 StartZ=0 EndX=-49.19 EndY=66.25 EndZ=0
    g1: LineSegment StartX=-49.19 StartY=5.75 StartZ=0 EndX=-49.19 EndY=2.75 EndZ=0
    g2: ArcOfCircle CenterX=-1.5 CenterY=67.75 CenterZ=0 NormalX=0 NormalY=0 NormalZ=1 AngleXU=0 Radius=1.5 StartAngle=4.71239 EndAngle=7.85398
    g3: ArcOfCircle CenterX=-1.5 CenterY=4.25 CenterZ=0 NormalX=0 NormalY=0 NormalZ=1 AngleXU=0 Radius=1.5 StartAngle=4.71239 EndAngle=7.85398
    g4: LineSegment StartX=-49.19 StartY=69.25 StartZ=0 EndX=-1.5 EndY=69.25 EndZ=0
    g5: LineSegment StartX=-49.19 StartY=66.25 StartZ=0 EndX=-1.5 EndY=66.25 EndZ=0
    g6: LineSegment StartX=-49.19 StartY=5.75 StartZ=0 EndX=-1.5 EndY=5.75 EndZ=0
    g7: LineSegment StartX=-49.19 StartY=2.75 StartZ=0 EndX=-1.5 EndY=2.75 EndZ=0
  constraints (19):
    c: Vertical(g0)
    c: Distance(g0) = 3
    c: Block(g0)
    c: Vertical(g1)
    c: Block(g2)
    c: Block(g3)
    c: Block(g1)
    c: Coincident(g4,g0)
    c: Coincident(g4,g2)
    c: Horizontal(g4)
    c: Coincident(g5,g0)
    c: Coincident(g5,g2)
    c: Horizontal(g5)
    c: Coincident(g6,g1)
    c: Coincident(g6,g3)
    c: Horizontal(g6)
    c: Coincident(g7,g1)
    c: Coincident(g7,g3)
    c: Horizontal(g7)
FEATURE [Part::Extrusion] Extrude073
  Base = -> Sketch082
  Dir = (1,0,0)
  DirMode = 2
  FaceMakerClass = Part::FaceMakerBullseye
  LengthFwd = 10
  LengthRev = 0
  Solid = true
  Symmetric = false
FEATURE [Part::Fillet] Fillet060  label="removeFromtMoreFrontCaseScrewRetainers005"
  Base = -> Extrude073
  Edges = 4 edges r=1.49: [Edge6,Edge11,Edge18,Edge23]
  Placement = pos=(-4,0,0) rot=(0,0,1;0rad)
FEATURE [Part::Revolution] Revolve163  label="backCaseScrewRetainer004"
  Angle = 360
  Axis = (0,1,0)
  Base = (0,0,0)
  FaceMakerClass = Part::FaceMakerBullseye
  Placement = pos=(12.5,3,62) rot=(0,0,1;0rad)
  Solid = false
  Source = -> Face149
  Symmetric = false
FEATURE [Part::Revolution] Revolve164  label="frontCaseScrewRetainer006"
  Angle = 360
  Axis = (0,1,0)
  Base = (0,0,0)
  FaceMakerClass = Part::FaceMakerBullseye
  Placement = pos=(89.5,3,68.5) rot=(0,0,1;0rad)
  Solid = false
  Source = -> Face151
  Symmetric = false
FEATURE [Part::Revolution] Revolve165  label="frontCaseScrewRetainer007"
  Angle = 360
  Axis = (0,1,0)
  Base = (0,0,0)
  FaceMakerClass = Part::FaceMakerBullseye
  Placement = pos=(89.5,3,3.5) rot=(0,0,1;0rad)
  Solid = false
  Source = -> Face152
  Symmetric = false
FEATURE [Part::Revolution] Revolve166  label="backCaseScrewRetainer005"
  Angle = 360
  Axis = (0,1,0)
  Base = (0,0,0)
  FaceMakerClass = Part::FaceMakerBullseye
  Placement = pos=(12.5,3,10) rot=(0,0,1;0rad)
  Solid = false
  Source = -> Face150
  Symmetric = false
FEATURE [Part::Revolution] Revolve167  label="moreFrontCaseScrewRetainer006"
  Angle = 360
  Axis = (0,1,0)
  Base = (0,0,0)
  FaceMakerClass = Part::FaceMakerBullseye
  Placement = pos=(109.5,4.5,68.5) rot=(0,0,1;0rad)
  Solid = false
  Source = -> Face153
  Symmetric = false
FEATURE [Part::Revolution] Revolve168  label="moreFrontCaseScrewRetainer007"
  Angle = 360
  Axis = (0,1,0)
  Base = (0,0,0)
  FaceMakerClass = Part::FaceMakerBullseye
  Placement = pos=(109.5,4.5,3.5) rot=(0,0,1;0rad)
  Solid = false
  Source = -> Face154
  Symmetric = false
FEATURE [Part::MultiFuse] Fusion151  label="screwRetainers003"
  Shapes = -> [Revolve168,Revolve167,Revolve166,Revolve165,Revolve164,Revolve163]
FEATURE [Part::Cut] Cut069  label="screwRetainers004"
  Base = -> Fusion151
  Tool = -> Fusion152
FEATURE [Part::Cut] Cut070
  Base = -> Cut069
  Tool = -> Fillet060
FEATURE [Part::Cut] Cut071  label="screwPillars001"
  Base = -> Cut070
  Tool = -> Fillet059
FEATURE [Part::MultiFuse] Fusion153  label="bottom024"
  Shapes = -> [Fusion149,Cut071]
FEATURE [Part::Cylinder] Cylinder067
  Angle = 360
  AttacherType = Attacher::AttachEngine3D
  Height = 10
  Placement = pos=(20.65,12,4.68) rot=(1,0,0;1.5708rad)
  Radius = 2
FEATURE [Part::Cylinder] Cylinder068
  Angle = 360
  AttacherType = Attacher::AttachEngine3D
  Height = 10
  Placement = pos=(20.65,12,67.38) rot=(1,0,0;1.5708rad)
  Radius = 2
FEATURE [Part::Cylinder] Cylinder069
  Angle = 360
  AttacherType = Attacher::AttachEngine3D
  Height = 10
  Placement = pos=(77.15,12,67.38) rot=(1,0,0;1.5708rad)
  Radius = 2
FEATURE [Part::Cylinder] Cylinder070
  Angle = 360
  AttacherType = Attacher::AttachEngine3D
  Height = 10
  Placement = pos=(77.15,12,4.68) rot=(1,0,0;1.5708rad)
  Radius = 2
FEATURE [Part::MultiFuse] Fusion154  label="removeFromThreadedInsertHousing001"
  Shapes = -> [Cylinder069,Cylinder068,Cylinder067,Cylinder070]
FEATURE [Part::Cut] Cut072  label="bottom025"
  Base = -> Fusion153
  Tool = -> Fusion154
FEATURE [Image::ImagePlane] ImagePlane
  XSize = 339
  YSize = 72
FEATURE [Sketcher::SketchObject] Sketch083
  FullyConstrained = false
  MapMode = 5
  Support = -> [XY_Plane]
  sketch-geometry (81):
    g0: LineSegment StartX=-151.619 StartY=28.8932 StartZ=0 EndX=-140.819 EndY=28.8932 EndZ=0
    g1: LineSegment StartX=-151.619 StartY=24.0313 StartZ=0 EndX=-151.619 EndY=28.8932 EndZ=0
    g2: LineSegment StartX=-140.819 StartY=17.7713 StartZ=0 EndX=-151.619 EndY=17.7713 EndZ=0
    g3: LineSegment StartX=-151.619 StartY=17.7713 StartZ=0 EndX=-151.619 EndY=22.6313 EndZ=0
    g4: LineSegment StartX=-151.619 StartY=22.6313 StartZ=0 EndX=-145.128 EndY=22.6313 EndZ=0
    g5: LineSegment StartX=-145.128 StartY=24.0313 StartZ=0 EndX=-140.819 EndY=28.8932 EndZ=0
    g6: LineSegment StartX=-145.128 StartY=22.6313 StartZ=0 EndX=-140.819 EndY=17.7713 EndZ=0
    g7: ArcOfCircle CenterX=-155.157 CenterY=23.3323 CenterZ=0 NormalX=0 NormalY=0 NormalZ=1 AngleXU=0 Radius=6.92354 StartAngle=1.03434 EndAngle=5.24885
    g8: ArcOfCircle CenterX=-155.157 CenterY=23.3323 CenterZ=0 NormalX=0 NormalY=0 NormalZ=1 AngleXU=0 Radius=12.6269 StartAngle=1.28675 EndAngle=4.99643
    g9: LineSegment StartX=-151.619 StartY=35.4532 StartZ=0 EndX=-151.619 EndY=29.2832 EndZ=0
    g10: LineSegment StartX=-151.619 StartY=17.3813 StartZ=0 EndX=-151.619 EndY=11.2113 EndZ=0
    g11-g21: Circle x11 (B-spline internal-alignment scaffolding for g22; pole/knot coordinates omitted)
    g22: BSplineCurve PolesCount=11 KnotsCount=9 Degree=3 IsPeriodic=0
    g23-g31: GeomPoint x9 (B-spline internal-alignment scaffolding for g22; pole/knot coordinates omitted)
    g32-g49: Circle x18 (B-spline internal-alignment scaffolding for g50; pole/knot coordinates omitted)
    g50: BSplineCurve PolesCount=18 KnotsCount=16 Degree=3 IsPeriodic=0
    g51-g66: GeomPoint x16 (B-spline internal-alignment scaffolding for g50; pole/knot coordinates omitted)
    g67: LineSegment StartX=-117.124 StartY=30.093 StartZ=0 EndX=-117.603 EndY=26.5272 EndZ=0
    g68: LineSegment StartX=-117.603 StartY=17.8472 StartZ=0 EndX=-117.124 EndY=14.2659 EndZ=0
    g69: Ellipse CenterX=-109.671 CenterY=20.025 CenterZ=0 NormalX=0 NormalY=0 NormalZ=1 MajorRadius=3.34798 MinorRadius=2.71052 AngleXU=-1.56793
    g70: GeomPoint X=-109.666 Y=18.0598 Z=0
    g71: GeomPoint X=-109.677 Y=21.9902 Z=0
    g72: Ellipse CenterX=-109.671 CenterY=20.0123 CenterZ=0 NormalX=0 NormalY=0 NormalZ=1 MajorRadius=6.93002 MinorRadius=6.36273 AngleXU=-3.13976
    g73: GeomPoint X=-112.417 Y=20.0073 Z=0
    g74: GeomPoint X=-106.925 Y=20.0173 Z=0
    g75: Ellipse CenterX=-51.7682 CenterY=20.1463 CenterZ=0 NormalX=0 NormalY=0 NormalZ=1 MajorRadius=3.19279 MinorRadius=2.71052 AngleXU=-1.52774
    g76: GeomPoint X=-51.6955 Y=18.4606 Z=0
    g77: GeomPoint X=-51.8408 Y=21.832 Z=0
    g78: GeomPoint X=-54.5142 Y=20.1413 Z=0
    g79: GeomPoint X=-49.0221 Y=20.1513 Z=0
    g80: Ellipse CenterX=-51.7682 CenterY=20.1463 CenterZ=0 NormalX=0 NormalY=0 NormalZ=1 MajorRadius=6.93002 MinorRadius=6.36273 AngleXU=-3.13976
  constraints (51):
    c: Coincident(g1,g0)
    c: Horizontal(g0)
    c: Vertical(g1)
    c: Coincident(g2,g3)
    c: Coincident(g3,g4)
    c: Horizontal(g4)
    c: Horizontal(g2)
    c: Vertical(g3)
    c: Block(g1)
    c: Distance(g3) = 4.86
    c: Block(g4)
    c: Distance(g0) = 10.8
    c: Distance(g2) = 10.8
    c: Coincident(g5,g0)
    c: Coincident(g6,g4)
    c: Coincident(g6,g2)
    c: Block(g8)
    c: Block(g7)
    c: Coincident(g9,g8)
    c: Coincident(g9,g7)
    c: Vertical(g9)
    c: Coincident(g10,g7)
    c: Coincident(g10,g8)
    c: Vertical(g10)
    c: Weight(g11) = 1
    c: Equal(g11, g12-g21) x10
    c: InternalAlignment(g11-g21 -> g22) x11
    c: InternalAlignment(g23-g31 -> g22) x9
    c: Block(g22)
    c: Weight(g32) = 1
    c: Equal(g32, g33-g49) x17
    c: InternalAlignment(g32-g49 -> g50) x18
    c: InternalAlignment(g51-g66 -> g50) x16
    c: Block(g50)
    c: Coincident(g67,g50)
    c: Coincident(g67,g22)
    c: Coincident(g68,g22)
    c: Coincident(g68,g50)
    c: InternalAlignment(g70,g69)
    c: InternalAlignment(g71,g69)
    c: Block(g69)
    c: InternalAlignment(g73,g72)
    c: InternalAlignment(g74,g72)
    c: Block(g72)
    c: InternalAlignment(g76,g75)
    c: InternalAlignment(g77,g75)
    c: InternalAlignment(g78,g80)
    c: InternalAlignment(g79,g80)
    c: Block(g80)
    c: Coincident(g75,g80)
    c: Block(g75)
FEATURE [PartDesign::Body] Body
  Group = -> [Sketch083]
  Origin = -> Origin
FEATURE [Sketcher::SketchObject] Sketch084
  FullyConstrained = true
  MapMode = 5
  Support = -> [XY_Plane001]
FEATURE [PartDesign::Body] Body001
  Group = -> [Sketch084]
  Origin = -> Origin001
